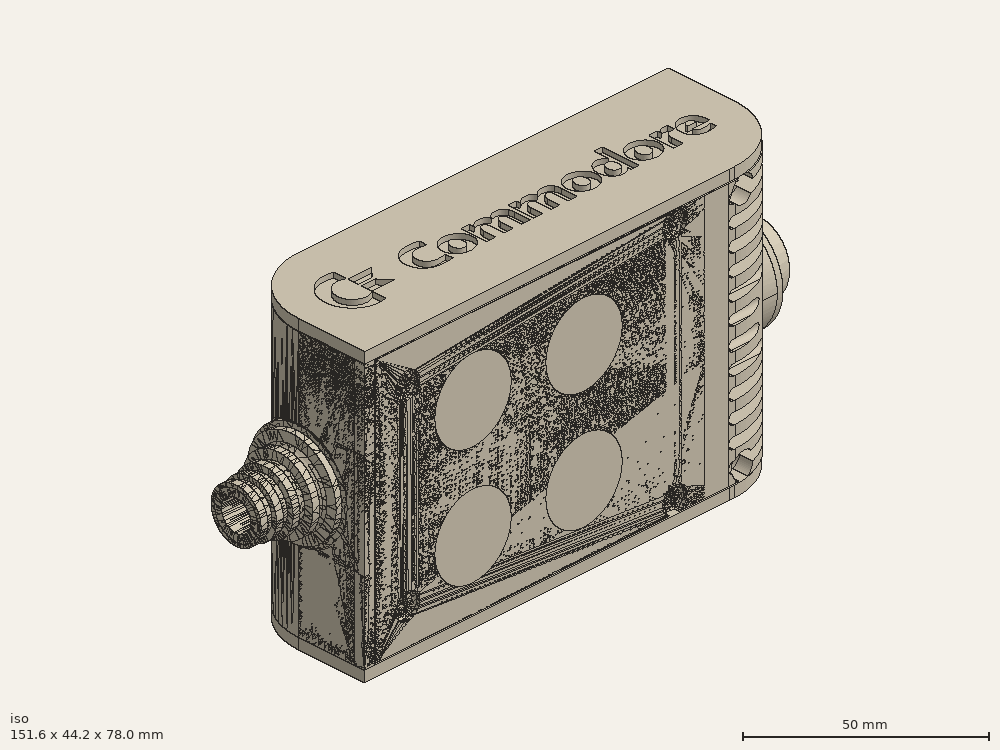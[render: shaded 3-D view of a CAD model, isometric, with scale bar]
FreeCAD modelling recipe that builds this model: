
FCSTD DOCUMENT  (FreeCAD 0.19R0.19.2)
Label: enclosure_222FCStd
License: All rights reserved
LicenseURL: http://en.wikipedia.org/wiki/All_rights_reserved
objects: Part::Revolution×152, Part::MultiFuse×146, Part::Feature×146, Sketcher::SketchObject×89, Part::Extrusion×74, Part::Cut×72, Part::Cylinder×70, Part::Fillet×58, Part::Box×38, App::MeasureDistance×4, Part::Chamfer×4, Part::FeaturePython×2, Image::ImagePlane×1, PartDesign::Body×1, Part::Mirroring×1
note: 853 computed .brp shape members not serialized (recipe doc carries the construction recipe); baked Part::Feature solids carry a one-line shape summary decoded from their .brp

FEATURE [Sketcher::SketchObject] Sketch  label="topSketch"
  FullyConstrained = true
  sketch-geometry (20):
    g0: LineSegment StartX=5.21097e-06 StartY=3 StartZ=0 EndX=5.21097e-06 EndY=19 EndZ=0
    g1: ArcOfCircle CenterX=19 CenterY=19 CenterZ=0 NormalX=0 NormalY=0 NormalZ=1 AngleXU=0 Radius=19 StartAngle=1.5708 EndAngle=3.14159
    g2: ArcOfCircle CenterX=19 CenterY=19 CenterZ=0 NormalX=0 NormalY=0 NormalZ=1 AngleXU=0 Radius=16 StartAngle=1.5708 EndAngle=3.14159
    g3: LineSegment StartX=114 StartY=35 StartZ=0 EndX=19 EndY=35 EndZ=0
    g4: LineSegment StartX=5.21097e-06 StartY=3 StartZ=0 EndX=5.21097e-06 EndY=0 EndZ=0
    g5: LineSegment StartX=3 StartY=0 StartZ=0 EndX=5.21097e-06 EndY=0 EndZ=0
    g6: LineSegment StartX=3 StartY=19 StartZ=0 EndX=3 EndY=0 EndZ=0
    g7: LineSegment StartX=19 StartY=38 StartZ=0 EndX=124 EndY=38 EndZ=0
    g8: Circle CenterX=119 CenterY=35 CenterZ=0 NormalX=0 NormalY=0 NormalZ=1 AngleXU=0 Radius=1
    g9: Circle CenterX=121 CenterY=35 CenterZ=0 NormalX=0 NormalY=0 NormalZ=1 AngleXU=0 Radius=1
    g10: Circle CenterX=121 CenterY=33 CenterZ=0 NormalX=0 NormalY=0 NormalZ=1 AngleXU=0 Radius=1
    g11: BSplineCurve PolesCount=3 KnotsCount=2 Degree=2 IsPeriodic=0
    g12: GeomPoint X=119 Y=35 Z=0
    g13: GeomPoint X=121 Y=33 Z=0
    g14: LineSegment StartX=119 StartY=35 StartZ=0 EndX=114 EndY=35 EndZ=0
    g15: ArcOfCircle CenterX=105 CenterY=19 CenterZ=0 NormalX=0 NormalY=0 NormalZ=1 AngleXU=0 Radius=19 StartAngle=5.7297 EndAngle=6.28319
    g16: ArcOfCircle CenterX=105 CenterY=19 CenterZ=0 NormalX=0 NormalY=0 NormalZ=1 AngleXU=0 Radius=16 StartAngle=5.60905 EndAngle=6.28319
    g17: LineSegment StartX=121 StartY=33 StartZ=0 EndX=121 EndY=19 EndZ=0
    g18: LineSegment StartX=124 StartY=38 StartZ=0 EndX=124 EndY=19 EndZ=0
    g19: LineSegment StartX=117.5 StartY=9.01251 StartZ=0 EndX=121.163 EndY=9.0125 EndZ=0
  constraints (46):
    c: Vertical(g0)
    c: Block(g0)
    c: Coincident(g1,g0)
    c: Block(g1)
    c: Coincident(g2,g1)
    c: Block(g2)
    c: Coincident(g3,g2)
    c: Horizontal(g3)
    c: Tangent(g3,g2)
    c: Coincident(g4,g0)
    c: Distance(g4) = 3
    c: Vertical(g4)
    c: Coincident(g5,g4)
    c: Horizontal(g5)
    c: Coincident(g6,g2)
    c: Coincident(g6,g5)
    c: Vertical(g6)
    c: Horizontal(g7)
    c: Distance(g7) = 105
    c: Coincident(g7,g1)
    c: Block(g3)
    c: Weight(g8) = 1
    c: Equal(g8,g9)
    c: Equal(g8,g10)
    c: InternalAlignment(g8,g11)
    c: InternalAlignment(g9,g11)
    c: InternalAlignment(g10,g11)
    c: InternalAlignment(g12,g11)
    c: InternalAlignment(g13,g11)
    c: Block(g11)
    c: Coincident(g14,g11)
    c: Coincident(g14,g3)
    c: Horizontal(g14)
    c: Block(g15)
    c: Coincident(g16,g15)
    c: Block(g16)
    c: Coincident(g17,g11)
    c: Coincident(g17,g16)
    c: Vertical(g17)
    c: Distance(g17) = 14
    c: Coincident(g18,g7)
    c: Coincident(g18,g15)
    c: Vertical(g18)
    c: Distance(g18) = 19
    c: Coincident(g19,g16)
    c: Coincident(g19,g15)
FEATURE [Sketcher::SketchObject] Sketch001  label="bottomSketch"
  FullyConstrained = true
  sketch-geometry (32):
    g0: LineSegment StartX=3.3 StartY=-6.03275e-07 StartZ=0 EndX=98 EndY=-6.03275e-07 EndZ=0
    g1: ArcOfCircle CenterX=98 CenterY=19 CenterZ=0 NormalX=0 NormalY=0 NormalZ=1 AngleXU=0 Radius=19 StartAngle=4.71239 EndAngle=5.71103
    g2: LineSegment StartX=6.3 StartY=8 StartZ=0 EndX=3.3 EndY=8 EndZ=0
    g3: LineSegment StartX=3.3 StartY=8 StartZ=0 EndX=3.3 EndY=-6.03275e-07 EndZ=0
    g4: ArcOfCircle CenterX=8.3 CenterY=5 CenterZ=0 NormalX=0 NormalY=0 NormalZ=1 AngleXU=0 Radius=2 StartAngle=3.14159 EndAngle=4.71239
    g5: LineSegment StartX=6.3 StartY=8 StartZ=0 EndX=6.3 EndY=5 EndZ=0
    g6: ArcOfCircle CenterX=98 CenterY=19 CenterZ=0 NormalX=0 NormalY=0 NormalZ=1 AngleXU=0 Radius=12.7 StartAngle=4.71239 EndAngle=6.28319
    g7: LineSegment StartX=94.7 StartY=3 StartZ=0 EndX=8.3 EndY=3 EndZ=0
    g8-g12: Circle x5 (B-spline internal-alignment scaffolding for g13; pole/knot coordinates omitted)
    g13: BSplineCurve PolesCount=5 KnotsCount=3 Degree=3 IsPeriodic=0
    g14: GeomPoint X=98 Y=6.3 Z=0
    g15: GeomPoint X=96.3938 Y=4.71946 Z=0
    g16: GeomPoint X=94.7 Y=3 Z=0
    g17-g23: Circle x7 (B-spline internal-alignment scaffolding for g24; pole/knot coordinates omitted)
    g24: BSplineCurve PolesCount=7 KnotsCount=5 Degree=3 IsPeriodic=0
    g25-g29: GeomPoint x5 (B-spline internal-alignment scaffolding for g24; pole/knot coordinates omitted)
    g30: ArcOfCircle CenterX=98 CenterY=19 CenterZ=0 NormalX=0 NormalY=0 NormalZ=1 AngleXU=0 Radius=15.7 StartAngle=5.81226 EndAngle=6.28319
    g31: LineSegment StartX=110.7 StartY=19 StartZ=0 EndX=113.7 EndY=19 EndZ=0
  constraints (41):
    c: Horizontal(g0)
    c: Coincident(g1,g0)
    c: Block(g1)
    c: Horizontal(g2)
    c: Distance(g2) = 3
    c: Coincident(g3,g2)
    c: Vertical(g3)
    c: Coincident(g3,g0)
    c: Block(g4)
    c: Block(g2)
    c: Coincident(g5,g2)
    c: Coincident(g5,g4)
    c: Vertical(g5)
    c: Coincident(g6,g1)
    c: Block(g6)
    c: Coincident(g7,g4)
    c: Horizontal(g7)
    c: Block(g0)
    c: Block(g7)
    c: Block(g3)
    c: Coincident(g13,g6)
    c: Weight(g8) = 1
    c: Equal(g8, g9-g12) x4
    c: Coincident(g13,g7)
    c: InternalAlignment(g8-g12 -> g13) x5
    c: InternalAlignment(g14,g13)
    c: InternalAlignment(g15,g13)
    c: InternalAlignment(g16,g13)
    c: Block(g13)
    c: Weight(g17) = 1
    c: Equal(g17, g18-g23) x6
    c: Coincident(g24,g1)
    c: InternalAlignment(g17-g23 -> g24) x7
    c: InternalAlignment(g25-g29 -> g24) x5
    c: Block(g24)
    c: Coincident(g30,g24)
    c: Coincident(g31,g6)
    c: Coincident(g31,g30)
    c: Horizontal(g31)
    c: Block(g31)
    c: Block(g30)
FEATURE [Part::Extrusion] Extrude  label="top"
  Base = -> Sketch
  Dir = (0,0,1)
  DirMode = 2
  FaceMakerClass = Part::FaceMakerBullseye
  LengthFwd = 72
  LengthRev = 0
  Solid = true
  Symmetric = false
FEATURE [Part::Extrusion] Extrude001  label="bottom"
  Base = -> Sketch001
  Dir = (0,0,1)
  DirMode = 2
  FaceMakerClass = Part::FaceMakerBullseye
  LengthFwd = 71.4
  LengthRev = 0
  Placement = pos=(0,0,0.3) rot=(0,0,1;0rad)
  Solid = true
  Symmetric = false
FEATURE [Sketcher::SketchObject] Sketch002  label="topSketch001"
  FullyConstrained = true
  sketch-geometry (8):
    g0: ArcOfCircle CenterX=19 CenterY=19.0975 CenterZ=0 NormalX=0 NormalY=0 NormalZ=1 AngleXU=0 Radius=18.9025 StartAngle=1.5708 EndAngle=3.14674
    g1: LineSegment StartX=0.0977805 StartY=19.0003 StartZ=0 EndX=0.0977805 EndY=0.000251602 EndZ=0
    g2: LineSegment StartX=19 StartY=38 StartZ=0 EndX=124 EndY=38 EndZ=0
    g3: LineSegment StartX=0.0977805 StartY=0.000251602 StartZ=0 EndX=105.098 EndY=0.000251602 EndZ=0
    g4: LineSegment StartX=124 StartY=38 StartZ=0 EndX=125.616 EndY=38 EndZ=0
    g5: LineSegment StartX=105.098 StartY=0.000251602 StartZ=0 EndX=106.713 EndY=0.000251602 EndZ=0
    g6: ArcOfCircle CenterX=106.616 CenterY=19 CenterZ=0 NormalX=0 NormalY=0 NormalZ=1 AngleXU=0 Radius=19 StartAngle=4.71754 EndAngle=6.28319
    g7: LineSegment StartX=125.616 StartY=38 StartZ=0 EndX=125.616 EndY=19 EndZ=0
  constraints (21):
    c: Block(g0)
    c: Coincident(g1,g0)
    c: Vertical(g1)
    c: Horizontal(g2)
    c: Distance(g2) = 105
    c: Coincident(g2,g0)
    c: Distance(g1) = 19
    c: Coincident(g3,g1)
    c: Horizontal(g3)
    c: Distance(g3) = 105
    c: Coincident(g4,g2)
    c: Horizontal(g4)
    c: Distance(g4) = 1.61553
    c: Horizontal(g5)
    c: Equal(g4,g5) = 1.61553
    c: Coincident(g5,g3)
    c: Block(g6)
    c: Coincident(g6,g5)
    c: Coincident(g7,g4)
    c: Coincident(g7,g6)
    c: Vertical(g7)
FEATURE [Part::Extrusion] Extrude002  label="sideA"
  Base = -> Sketch002
  Dir = (0,0,1)
  DirMode = 2
  FaceMakerClass = Part::FaceMakerBullseye
  LengthFwd = 3
  LengthRev = 0
  Placement = pos=(0,0,-3) rot=(0,0,1;0rad)
  Solid = true
  Symmetric = false
FEATURE [Sketcher::SketchObject] Sketch003  label="topSketch002"
  FullyConstrained = true
  sketch-geometry (6):
    g0: LineSegment StartX=19 StartY=38 StartZ=0 EndX=117 EndY=38 EndZ=0
    g1: ArcOfCircle CenterX=19 CenterY=19 CenterZ=0 NormalX=0 NormalY=0 NormalZ=1 AngleXU=0 Radius=19 StartAngle=1.5708 EndAngle=3.14159
    g2: LineSegment StartX=117 StartY=38 StartZ=0 EndX=117 EndY=19 EndZ=0
    g3: LineSegment StartX=98 StartY=1.0161e-12 StartZ=0 EndX=5.22862e-06 EndY=1.0161e-12 EndZ=0
    g4: LineSegment StartX=5.22862e-06 StartY=19 StartZ=0 EndX=5.22862e-06 EndY=1.0161e-12 EndZ=0
    g5: ArcOfCircle CenterX=98 CenterY=19 CenterZ=0 NormalX=0 NormalY=0 NormalZ=1 AngleXU=0 Radius=19 StartAngle=4.71239 EndAngle=6.28319
  constraints (16):
    c: Horizontal(g0)
    c: Distance(g0) = 98
    c: Coincident(g1,g0)
    c: Block(g1)
    c: Coincident(g2,g0)
    c: Vertical(g2)
    c: Distance(g2) = 19
    c: Horizontal(g3)
    c: Coincident(g4,g1)
    c: Vertical(g4)
    c: Coincident(g3,g4)
    c: Block(g3)
    c: Coincident(g5,g2)
    c: Coincident(g5,g3)
    c: Block(g0)
    c: Block(g5)
FEATURE [Sketcher::SketchObject] Sketch004
  FullyConstrained = true
  MapMode = 3
  Placement = pos=(0,0,0) rot=(1,0,0;1.5708rad)
  Support = -> [Extrude]
  sketch-geometry (8):
    g0: Circle CenterX=80.351 CenterY=-67.6202 CenterZ=0 NormalX=0 NormalY=0 NormalZ=1 AngleXU=0 Radius=2
    g1: Circle CenterX=80.351 CenterY=-67.6202 CenterZ=0 NormalX=0 NormalY=0 NormalZ=1 AngleXU=0 Radius=3
    g2: Circle CenterX=80.351 CenterY=-4.92017 CenterZ=0 NormalX=0 NormalY=0 NormalZ=1 AngleXU=0 Radius=2
    g3: Circle CenterX=80.351 CenterY=-4.92017 CenterZ=0 NormalX=0 NormalY=0 NormalZ=1 AngleXU=0 Radius=3
    g4: Circle CenterX=23.851 CenterY=-4.92017 CenterZ=0 NormalX=0 NormalY=0 NormalZ=1 AngleXU=0 Radius=2
    g5: Circle CenterX=23.851 CenterY=-4.92017 CenterZ=0 NormalX=0 NormalY=0 NormalZ=1 AngleXU=0 Radius=3
    g6: Circle CenterX=23.851 CenterY=-67.6202 CenterZ=0 NormalX=0 NormalY=0 NormalZ=1 AngleXU=0 Radius=2
    g7: Circle CenterX=23.851 CenterY=-67.6202 CenterZ=0 NormalX=0 NormalY=0 NormalZ=1 AngleXU=0 Radius=3
  constraints (8):
    c: Block(g3)
    c: Block(g2)
    c: Block(g1)
    c: Block(g0)
    c: Block(g6)
    c: Block(g7)
    c: Block(g4)
    c: Block(g5)
FEATURE [Part::Extrusion] Extrude004
  Base = -> Sketch004
  Dir = (0,-1,2e-16)
  DirMode = 2
  FaceMakerClass = Part::FaceMakerBullseye
  LengthFwd = 6
  LengthRev = 0
  Placement = pos=(0,9,0) rot=(0,0,1;0rad)
  Solid = true
  Symmetric = false
FEATURE [Sketcher::SketchObject] Sketch005
  FullyConstrained = true
  MapMode = 3
  Placement = pos=(0,0,0) rot=(1,0,0;1.5708rad)
  Support = -> [Extrude]
  sketch-geometry (8):
    g0: Circle CenterX=80.351 CenterY=-67.6202 CenterZ=0 NormalX=0 NormalY=0 NormalZ=1 AngleXU=0 Radius=3
    g1: Circle CenterX=80.351 CenterY=-4.92017 CenterZ=0 NormalX=0 NormalY=0 NormalZ=1 AngleXU=0 Radius=3
    g2: Circle CenterX=23.851 CenterY=-4.92017 CenterZ=0 NormalX=0 NormalY=0 NormalZ=1 AngleXU=0 Radius=3
    g3: Circle CenterX=23.851 CenterY=-67.6202 CenterZ=0 NormalX=0 NormalY=0 NormalZ=1 AngleXU=0 Radius=3
    g4: Circle CenterX=23.851 CenterY=-67.6202 CenterZ=0 NormalX=0 NormalY=0 NormalZ=1 AngleXU=0 Radius=5
    g5: Circle CenterX=80.351 CenterY=-67.6202 CenterZ=0 NormalX=0 NormalY=0 NormalZ=1 AngleXU=0 Radius=5
    g6: Circle CenterX=23.851 CenterY=-4.92017 CenterZ=0 NormalX=0 NormalY=0 NormalZ=1 AngleXU=0 Radius=5
    g7: Circle CenterX=80.351 CenterY=-4.92017 CenterZ=0 NormalX=0 NormalY=0 NormalZ=1 AngleXU=0 Radius=5
  constraints (8):
    c: Block(g1)
    c: Block(g0)
    c: Block(g3)
    c: Block(g2)
    c: Block(g5)
    c: Block(g4)
    c: Block(g6)
    c: Block(g7)
FEATURE [Part::Extrusion] Extrude005
  Base = -> Sketch005
  Dir = (0,-1,2e-16)
  DirMode = 2
  FaceMakerClass = Part::FaceMakerBullseye
  LengthFwd = 2
  LengthRev = 0
  Solid = true
  Symmetric = false
FEATURE [Sketcher::SketchObject] Sketch006
  FullyConstrained = true
  MapMode = 3
  Placement = pos=(0,0,0) rot=(1,0,0;1.5708rad)
  sketch-geometry (8):
    g0: Circle CenterX=80.351 CenterY=-67.6202 CenterZ=0 NormalX=0 NormalY=0 NormalZ=1 AngleXU=0 Radius=3
    g1: Circle CenterX=80.351 CenterY=-4.92017 CenterZ=0 NormalX=0 NormalY=0 NormalZ=1 AngleXU=0 Radius=3
    g2: Circle CenterX=23.851 CenterY=-4.92017 CenterZ=0 NormalX=0 NormalY=0 NormalZ=1 AngleXU=0 Radius=3
    g3: Circle CenterX=23.851 CenterY=-67.6202 CenterZ=0 NormalX=0 NormalY=0 NormalZ=1 AngleXU=0 Radius=3
    g4: Circle CenterX=23.851 CenterY=-67.6202 CenterZ=0 NormalX=0 NormalY=0 NormalZ=1 AngleXU=0 Radius=5
    g5: Circle CenterX=80.351 CenterY=-67.6202 CenterZ=0 NormalX=0 NormalY=0 NormalZ=1 AngleXU=0 Radius=5
    g6: Circle CenterX=23.851 CenterY=-4.92017 CenterZ=0 NormalX=0 NormalY=0 NormalZ=1 AngleXU=0 Radius=5
    g7: Circle CenterX=80.351 CenterY=-4.92017 CenterZ=0 NormalX=0 NormalY=0 NormalZ=1 AngleXU=0 Radius=5
  constraints (8):
    c: Block(g1)
    c: Block(g0)
    c: Block(g3)
    c: Block(g2)
    c: Block(g5)
    c: Block(g4)
    c: Block(g6)
    c: Block(g7)
FEATURE [Part::Extrusion] Extrude007
  Base = -> Sketch006
  Dir = (0,-1,2e-16)
  DirMode = 2
  FaceMakerClass = Part::FaceMakerBullseye
  LengthFwd = 2
  LengthRev = 0
  Solid = true
  Symmetric = false
FEATURE [Part::Fillet] Fillet
  Base = -> Extrude007
  Edges = 4 edges r=1.99: [Edge6,Edge12,Edge18,Edge24]
FEATURE [Part::Cut] Cut
  Base = -> Extrude005
  Placement = pos=(0,5,0) rot=(0,0,1;0rad)
  Tool = -> Fillet
FEATURE [Part::MultiFuse] Fusion  label="pCBScrews"
  Placement = pos=(-2.5,0,72.3) rot=(0,0,1;0rad)
  Shapes = -> [Extrude004,Cut]
FEATURE [App::MeasureDistance] Distance  label="Distance: 0.69 mm"
  Distance = 0.685967
  P1 = (24.0138,2.9647,0.3)
  P2 = (23.8901,3,-0.373787)
FEATURE [App::MeasureDistance] Distance001  label="Distance: 0.53 mm"
  Distance = 0.533607
  P1 = (80.2939,3,72.2334)
  P2 = (80.281,2.99661,71.7)
FEATURE [Part::Fillet] Fillet001
  Base = -> Extrude001
  Edges = 1 edges r=2.4: [Edge17]
FEATURE [Part::Fillet] Fillet002  label="bottom001"
  Base = -> Fillet001
  Edges = 1 edges r=2.4: [Edge36]
FEATURE [Part::Fillet] Fillet003  label="top001"
  Base = -> Extrude
  Edges = 1 edges r=2: [Edge1]
FEATURE [Sketcher::SketchObject] Sketch007
  FullyConstrained = true
  sketch-geometry (16):
    g0: LineSegment StartX=4 StartY=0 StartZ=0 EndX=4 EndY=2.4 EndZ=0
    g1: LineSegment StartX=4 StartY=2.4 StartZ=0 EndX=7 EndY=2.4 EndZ=0
    g2: LineSegment StartX=4 StartY=0 StartZ=0 EndX=5.7 EndY=0 EndZ=0
    g3: LineSegment StartX=5.7 StartY=0 StartZ=0 EndX=5.7 EndY=-5.6 EndZ=0
    g4-g8: Circle x5 (B-spline internal-alignment scaffolding for g9; pole/knot coordinates omitted)
    g9: BSplineCurve PolesCount=5 KnotsCount=3 Degree=3 IsPeriodic=0
    g10: GeomPoint X=7 Y=2.4 Z=0
    g11: GeomPoint X=10.4582 Y=-1.55472 Z=0
    g12: GeomPoint X=14 Y=-5.6 Z=0
    g13: LineSegment StartX=14 StartY=-5.6 StartZ=0 EndX=14 EndY=-14.1 EndZ=0
    g14: LineSegment StartX=14 StartY=-14.1 StartZ=0 EndX=6.5 EndY=-14.1 EndZ=0
    g15: LineSegment StartX=5.7 StartY=-5.6 StartZ=0 EndX=6.5 EndY=-14.1 EndZ=0
  constraints (28):
    c: Distance(g0) = 2.4
    c: Vertical(g0)
    c: Block(g0)
    c: Coincident(g1,g0)
    c: Horizontal(g1)
    c: Distance(g1) = 3
    c: Coincident(g2,g0)
    c: Horizontal(g2)
    c: Distance(g2) = 1.7
    c: Coincident(g3,g2)
    c: Vertical(g3)
    c: Distance(g3) = 5.6
    c: Coincident(g9,g1)
    c: Weight(g4) = 1
    c: Equal(g4, g5-g8) x4
    c: InternalAlignment(g4-g8 -> g9) x5
    c: InternalAlignment(g10,g9)
    c: InternalAlignment(g11,g9)
    c: InternalAlignment(g12,g9)
    c: Block(g9)
    c: Coincident(g13,g9)
    c: Vertical(g13)
    c: Distance(g13) = 8.5
    c: Coincident(g14,g13)
    c: Horizontal(g14)
    c: Distance(g14) = 7.5
    c: Coincident(g15,g3)
    c: Coincident(g15,g14)
FEATURE [Part::Feature] Face
  shape: bbox 10 x 16.5 x 2e-07 mm, 1 faces, 0 solids (baked)
FEATURE [Part::Revolution] Revolve  label="plugHousing"
  Angle = 360
  Axis = (0,1,0)
  Base = (0,0,0)
  FaceMakerClass = Part::FaceMakerBullseye
  Placement = pos=(0,0,36.15) rot=(0,0,1;0rad)
  Solid = false
  Source = -> Face
  Symmetric = false
FEATURE [Part::Feature] Face001
  shape: bbox 10 x 16.5 x 2e-07 mm, 1 faces, 0 solids (baked)
FEATURE [Part::Revolution] Revolve001  label="plugHousing001"
  Angle = 360
  Axis = (0,1,0)
  Base = (0,0,0)
  FaceMakerClass = Part::FaceMakerBullseye
  Placement = pos=(0,0,36.15) rot=(0,0,1;0rad)
  Solid = false
  Source = -> Face001
  Symmetric = false
FEATURE [Part::MultiFuse] Fusion001  label="plugHousing002"
  Placement = pos=(0,0,0) rot=(0,0,1;1.5708rad)
  Shapes = -> [Revolve001,Revolve]
FEATURE [Part::Feature] Face002
  shape: bbox 10 x 16.5 x 2e-07 mm, 1 faces, 0 solids (baked)
FEATURE [Part::Revolution] Revolve003  label="plugHousing005"
  Angle = 360
  Axis = (0,1,0)
  Base = (0,0,0)
  FaceMakerClass = Part::FaceMakerBullseye
  Placement = pos=(0,0,36.15) rot=(0,0,1;0rad)
  Solid = false
  Source = -> Face002
  Symmetric = false
FEATURE [Part::Feature] Face003
  shape: bbox 10 x 16.5 x 2e-07 mm, 1 faces, 0 solids (baked)
FEATURE [Part::Revolution] Revolve002  label="plugHousing003"
  Angle = 360
  Axis = (0,1,0)
  Base = (0,0,0)
  FaceMakerClass = Part::FaceMakerBullseye
  Placement = pos=(0,0,36.15) rot=(0,0,1;0rad)
  Solid = false
  Source = -> Face003
  Symmetric = false
FEATURE [Part::MultiFuse] Fusion002  label="plugHousing004"
  Placement = pos=(0,0,0) rot=(0,0,1;1.5708rad)
  Shapes = -> [Revolve002,Revolve003]
FEATURE [Part::MultiFuse] Fusion003  label="plugHousing006"
  Placement = pos=(0,19,0) rot=(0,0,1;3.14159rad)
  Shapes = -> [Fusion002,Fusion001]
FEATURE [Part::Feature] Face004
  shape: bbox 10 x 16.5 x 2e-07 mm, 1 faces, 0 solids (baked)
FEATURE [Part::Revolution] Revolve006  label="plugHousing010"
  Angle = 360
  Axis = (0,1,0)
  Base = (0,0,0)
  FaceMakerClass = Part::FaceMakerBullseye
  Placement = pos=(0,0,36.15) rot=(0,0,1;0rad)
  Solid = false
  Source = -> Face004
  Symmetric = false
FEATURE [Part::Feature] Face005
  shape: bbox 10 x 16.5 x 2e-07 mm, 1 faces, 0 solids (baked)
FEATURE [Part::Revolution] Revolve007  label="plugHousing011"
  Angle = 360
  Axis = (0,1,0)
  Base = (0,0,0)
  FaceMakerClass = Part::FaceMakerBullseye
  Placement = pos=(0,0,36.15) rot=(0,0,1;0rad)
  Solid = false
  Source = -> Face005
  Symmetric = false
FEATURE [Part::Feature] Face006
  shape: bbox 10 x 16.5 x 2e-07 mm, 1 faces, 0 solids (baked)
FEATURE [Part::Revolution] Revolve004  label="plugHousing007"
  Angle = 360
  Axis = (0,1,0)
  Base = (0,0,0)
  FaceMakerClass = Part::FaceMakerBullseye
  Placement = pos=(0,0,36.15) rot=(0,0,1;0rad)
  Solid = false
  Source = -> Face006
  Symmetric = false
FEATURE [Part::MultiFuse] Fusion004  label="plugHousing009"
  Placement = pos=(0,0,0) rot=(0,0,1;1.5708rad)
  Shapes = -> [Revolve004,Revolve007]
FEATURE [Part::Feature] Face007
  shape: bbox 10 x 16.5 x 2e-07 mm, 1 faces, 0 solids (baked)
FEATURE [Part::Revolution] Revolve005  label="plugHousing008"
  Angle = 360
  Axis = (0,1,0)
  Base = (0,0,0)
  FaceMakerClass = Part::FaceMakerBullseye
  Placement = pos=(0,0,36.15) rot=(0,0,1;0rad)
  Solid = false
  Source = -> Face007
  Symmetric = false
FEATURE [Part::MultiFuse] Fusion005  label="plugHousing012"
  Placement = pos=(0,0,0) rot=(0,0,1;1.5708rad)
  Shapes = -> [Revolve006,Revolve005]
FEATURE [Part::MultiFuse] Fusion006  label="plugHousing013"
  Placement = pos=(0,19,0) rot=(0,0,1;3.14159rad)
  Shapes = -> [Fusion005,Fusion004]
FEATURE [Part::MultiFuse] Fusion007  label="plugHousing014"
  Placement = pos=(122.621,0,-0.15) rot=(0,0,1;0rad)
  Shapes = -> [Fusion003,Fusion006]
FEATURE [Part::Cylinder] Cylinder002
  Angle = 360
  AttacherType = Attacher::AttachEngine3D
  Height = 20
  Placement = pos=(0,0,36.15) rot=(0,0,1;0rad)
  Radius = 4
FEATURE [Part::Cylinder] Cylinder003
  Angle = 360
  AttacherType = Attacher::AttachEngine3D
  Height = 10
  Placement = pos=(0,0,36.15) rot=(0,0,1;0rad)
  Radius = 4
FEATURE [Part::MultiFuse] Fusion009  label="removeToCreateHoleForPlugHousing"
  Placement = pos=(70,19,36.15) rot=(0,1,0;1.5708rad)
  Shapes = -> [Cylinder002,Cylinder003]
FEATURE [Part::Cylinder] Cylinder004
  Angle = 360
  AttacherType = Attacher::AttachEngine3D
  Height = 20
  Placement = pos=(0,0,36.15) rot=(0,0,1;0rad)
  Radius = 4
FEATURE [Part::Cylinder] Cylinder005
  Angle = 360
  AttacherType = Attacher::AttachEngine3D
  Height = 10
  Placement = pos=(0,0,36.15) rot=(0,0,1;0rad)
  Radius = 4
FEATURE [Part::MultiFuse] Fusion010  label="removeToCreateHoleForPlugHousing001"
  Placement = pos=(70,19,36.15) rot=(0,1,0;1.5708rad)
  Shapes = -> [Cylinder004,Cylinder005]
FEATURE [Part::Cut] Cut001
  Base = -> Fillet003
  Tool = -> Fusion010
FEATURE [Part::Cut] Cut002  label="Bottom"
  Base = -> Fillet002
  Tool = -> Fusion009
FEATURE [Part::Feature] Face008
  shape: bbox 10 x 16.5 x 2e-07 mm, 1 faces, 0 solids (baked)
FEATURE [Part::Revolution] Revolve011  label="plugHousing021"
  Angle = 360
  Axis = (0,1,0)
  Base = (0,0,0)
  FaceMakerClass = Part::FaceMakerBullseye
  Placement = pos=(0,0,36.15) rot=(0,0,1;0rad)
  Solid = false
  Source = -> Face008
  Symmetric = false
FEATURE [Part::Feature] Face009
  shape: bbox 10 x 16.5 x 2e-07 mm, 1 faces, 0 solids (baked)
FEATURE [Part::Revolution] Revolve012  label="plugHousing022"
  Angle = 360
  Axis = (0,1,0)
  Base = (0,0,0)
  FaceMakerClass = Part::FaceMakerBullseye
  Placement = pos=(0,0,36.15) rot=(0,0,1;0rad)
  Solid = false
  Source = -> Face009
  Symmetric = false
FEATURE [Part::Feature] Face010 .. Face013  x4 (patterned run collapsed; names and placements below)
  shape: bbox 10 x 16.5 x 2e-07 mm, 1 faces, 0 solids (baked)
FEATURE [Part::Revolution] Revolve015  label="plugHousing027"
  Angle = 360
  Axis = (0,1,0)
  Base = (0,0,0)
  FaceMakerClass = Part::FaceMakerBullseye
  Placement = pos=(0,0,36.15) rot=(0,0,1;0rad)
  Solid = false
  Source = -> Face013
  Symmetric = false
FEATURE [Part::Feature] Face014
  shape: bbox 10 x 16.5 x 2e-07 mm, 1 faces, 0 solids (baked)
FEATURE [Part::Feature] Face015
  shape: bbox 10 x 16.5 x 2e-07 mm, 1 faces, 0 solids (baked)
FEATURE [Part::Feature] Face016
  shape: bbox 10 x 16.5 x 2e-07 mm, 1 faces, 0 solids (baked)
FEATURE [Part::Revolution] Revolve019  label="plugHousing033"
  Angle = 360
  Axis = (0,1,0)
  Base = (0,0,0)
  FaceMakerClass = Part::FaceMakerBullseye
  Placement = pos=(0,0,36.15) rot=(0,0,1;0rad)
  Solid = false
  Source = -> Face016
  Symmetric = false
FEATURE [Part::Feature] Face017
  shape: bbox 10 x 16.5 x 2e-07 mm, 1 faces, 0 solids (baked)
FEATURE [Part::Revolution] Revolve020  label="plugHousing034"
  Angle = 360
  Axis = (0,1,0)
  Base = (0,0,0)
  FaceMakerClass = Part::FaceMakerBullseye
  Placement = pos=(0,0,36.15) rot=(0,0,1;0rad)
  Solid = false
  Source = -> Face017
  Symmetric = false
FEATURE [Part::Feature] Face018
  shape: bbox 10 x 16.5 x 2e-07 mm, 1 faces, 0 solids (baked)
FEATURE [Part::Revolution] Revolve016  label="plugHousing030"
  Angle = 360
  Axis = (0,1,0)
  Base = (0,0,0)
  FaceMakerClass = Part::FaceMakerBullseye
  Placement = pos=(0,0,36.15) rot=(0,0,1;0rad)
  Solid = false
  Source = -> Face018
  Symmetric = false
FEATURE [Part::MultiFuse] Fusion020  label="plugHousing038"
  Placement = pos=(0,0,0) rot=(0,0,1;1.5708rad)
  Shapes = -> [Revolve016,Revolve020]
FEATURE [Part::Feature] Face019
  shape: bbox 10 x 16.5 x 2e-07 mm, 1 faces, 0 solids (baked)
FEATURE [Part::Feature] Face020
  shape: bbox 10 x 16.5 x 2e-07 mm, 1 faces, 0 solids (baked)
FEATURE [Part::Revolution] Revolve017  label="plugHousing031"
  Angle = 360
  Axis = (0,1,0)
  Base = (0,0,0)
  FaceMakerClass = Part::FaceMakerBullseye
  Placement = pos=(0,0,36.15) rot=(0,0,1;0rad)
  Solid = false
  Source = -> Face020
  Symmetric = false
FEATURE [Part::MultiFuse] Fusion021  label="plugHousing039"
  Placement = pos=(0,0,0) rot=(0,0,1;1.5708rad)
  Shapes = -> [Revolve019,Revolve017]
FEATURE [Part::MultiFuse] Fusion023  label="plugHousing041"
  Placement = pos=(0,19,0) rot=(0,0,1;3.14159rad)
  Shapes = -> [Fusion021,Fusion020]
FEATURE [Part::Revolution] Revolve022  label="plugHousing043"
  Angle = 360
  Axis = (0,1,0)
  Base = (0,0,0)
  FaceMakerClass = Part::FaceMakerBullseye
  Placement = pos=(0,0,36.15) rot=(0,0,1;0rad)
  Solid = false
  Source = -> Face019
  Symmetric = false
FEATURE [Part::Feature] Face021
  shape: bbox 10 x 16.5 x 2e-07 mm, 1 faces, 0 solids (baked)
FEATURE [Part::Revolution] Revolve023  label="plugHousing044"
  Angle = 360
  Axis = (0,1,0)
  Base = (0,0,0)
  FaceMakerClass = Part::FaceMakerBullseye
  Placement = pos=(0,0,36.15) rot=(0,0,1;0rad)
  Solid = false
  Source = -> Face021
  Symmetric = false
FEATURE [Part::Feature] Face022
  shape: bbox 10 x 16.5 x 2e-07 mm, 1 faces, 0 solids (baked)
FEATURE [Part::Revolution] Revolve018  label="plugHousing032"
  Angle = 360
  Axis = (0,1,0)
  Base = (0,0,0)
  FaceMakerClass = Part::FaceMakerBullseye
  Placement = pos=(0,0,36.15) rot=(0,0,1;0rad)
  Solid = false
  Source = -> Face022
  Symmetric = false
FEATURE [Part::MultiFuse] Fusion022  label="plugHousing040"
  Placement = pos=(0,0,0) rot=(0,0,1;1.5708rad)
  Shapes = -> [Revolve018,Revolve023]
FEATURE [Part::Feature] Face023
  shape: bbox 10 x 16.5 x 2e-07 mm, 1 faces, 0 solids (baked)
FEATURE [Part::Revolution] Revolve021  label="plugHousing035"
  Angle = 360
  Axis = (0,1,0)
  Base = (0,0,0)
  FaceMakerClass = Part::FaceMakerBullseye
  Placement = pos=(0,0,36.15) rot=(0,0,1;0rad)
  Solid = false
  Source = -> Face023
  Symmetric = false
FEATURE [Part::MultiFuse] Fusion018  label="plugHousing036"
  Placement = pos=(0,0,0) rot=(0,0,1;1.5708rad)
  Shapes = -> [Revolve022,Revolve021]
FEATURE [Part::MultiFuse] Fusion019  label="plugHousing037"
  Placement = pos=(0,19,0) rot=(0,0,1;3.14159rad)
  Shapes = -> [Fusion018,Fusion022]
FEATURE [Part::MultiFuse] Fusion024  label="plugHousing042"
  Placement = pos=(122.621,0,-0.15) rot=(0,0,1;0rad)
  Shapes = -> [Fusion023,Fusion019]
FEATURE [Part::Cylinder] Cylinder006
  Angle = 360
  AttacherType = Attacher::AttachEngine3D
  Height = 20
  Placement = pos=(0,0,36.15) rot=(0,0,1;0rad)
  Radius = 14.3
FEATURE [Part::Cylinder] Cylinder007
  Angle = 360
  AttacherType = Attacher::AttachEngine3D
  Height = 10
  Placement = pos=(0,0,36.15) rot=(0,0,1;0rad)
  Radius = 4
FEATURE [Part::MultiFuse] Fusion026  label="removeToCreteHoleForPlugHousing"
  Placement = pos=(70,19,36) rot=(0,1,0;1.5708rad)
  Shapes = -> [Cylinder006,Cylinder007]
FEATURE [Part::Box] Box001  label="Cube001"
  AttacherType = Attacher::AttachEngine3D
  Height = 28
  Length = 3
  Placement = pos=(110.7,19,22) rot=(0,0,1;0rad)
  Width = 15.7
FEATURE [Part::Cut] Cut003  label="top002"
  Base = -> Cut001
  Tool = -> Fusion007
FEATURE [Part::Revolution] Revolve008  label="plugHousing015"
  Angle = 360
  Axis = (0,1,0)
  Base = (0,0,0)
  FaceMakerClass = Part::FaceMakerBullseye
  Placement = pos=(0,0,36.15) rot=(0,0,1;0rad)
  Solid = false
  Source = -> Face010
  Symmetric = false
FEATURE [Part::MultiFuse] Fusion013  label="plugHousing020"
  Placement = pos=(0,0,0) rot=(0,0,1;1.5708rad)
  Shapes = -> [Revolve008,Revolve012]
FEATURE [Part::Cut] Cut004  label="top003"
  Base = -> Cut003
  Placement = pos=(1,0,0) rot=(0,0,1;0rad)
  Tool = -> Fusion026
FEATURE [Part::Cylinder] Cylinder008
  Angle = 360
  AttacherType = Attacher::AttachEngine3D
  Height = 20
  Placement = pos=(0,0,36.15) rot=(0,0,1;0rad)
  Radius = 10.3
FEATURE [Part::Cylinder] Cylinder009
  Angle = 360
  AttacherType = Attacher::AttachEngine3D
  Height = 10
  Placement = pos=(0,0,36.15) rot=(0,0,1;0rad)
  Radius = 4
FEATURE [Part::MultiFuse] Fusion027  label="removeToCreteHoleForPlugHousing001"
  Placement = pos=(70,19,36) rot=(0,1,0;1.5708rad)
  Shapes = -> [Cylinder008,Cylinder009]
FEATURE [Part::Cut] Cut005  label="plugHousingTab"
  Base = -> Box001
  Tool = -> Fusion027
FEATURE [Part::MultiFuse] Fusion028  label="plugHousing045"
  Shapes = -> [Fusion024,Cut005]
FEATURE [Part::Box] Box002  label="Cube002"
  AttacherType = Attacher::AttachEngine3D
  Height = 28.8
  Length = 3
  Placement = pos=(107.3,28,21.6) rot=(0,0,1;0rad)
  Width = 7
FEATURE [Part::Box] Box003  label="Cube003"
  AttacherType = Attacher::AttachEngine3D
  Height = 3
  Length = 6.4
  Placement = pos=(107.3,28,18.6) rot=(0,0,1;0rad)
  Width = 7
FEATURE [Part::Box] Box004  label="Cube004"
  AttacherType = Attacher::AttachEngine3D
  Height = 3
  Length = 6.4
  Placement = pos=(107.3,28,50.4) rot=(0,0,1;0rad)
  Width = 7
FEATURE [Part::MultiFuse] Fusion029  label="plugHousingBracketHolder"
  Shapes = -> [Box004,Box002,Box003]
FEATURE [Part::Cylinder] Cylinder010
  Angle = 360
  AttacherType = Attacher::AttachEngine3D
  Height = 20
  Placement = pos=(0,0,36.15) rot=(0,0,1;0rad)
  Radius = 14.3
FEATURE [Part::Cylinder] Cylinder011
  Angle = 360
  AttacherType = Attacher::AttachEngine3D
  Height = 10
  Placement = pos=(0,0,36.15) rot=(0,0,1;0rad)
  Radius = 4
FEATURE [Part::MultiFuse] Fusion030  label="removeToCreteHoleForPlugHousing002"
  Placement = pos=(70,19,36) rot=(0,1,0;1.5708rad)
  Shapes = -> [Cylinder010,Cylinder011]
FEATURE [Part::Cut] Cut006  label="plugHousingBracketHolder001"
  Base = -> Fusion029
  Tool = -> Fusion030
FEATURE [Part::Cylinder] Cylinder012
  Angle = 360
  AttacherType = Attacher::AttachEngine3D
  Height = 20
  Placement = pos=(0,0,36.15) rot=(0,0,1;0rad)
  Radius = 7
FEATURE [Part::Cylinder] Cylinder013
  Angle = 360
  AttacherType = Attacher::AttachEngine3D
  Height = 10
  Placement = pos=(0,0,36.15) rot=(0,0,1;0rad)
  Radius = 4
FEATURE [Part::MultiFuse] Fusion032  label="removeToCreteHoleForPlugHousing003"
  Placement = pos=(70,19,36) rot=(0,1,0;1.5708rad)
  Shapes = -> [Cylinder012,Cylinder013]
FEATURE [Part::Cut] Cut007  label="bottom002"
  Base = -> Cut002
  Tool = -> Fusion032
FEATURE [Sketcher::SketchObject] Sketch008
  FullyConstrained = true
  sketch-geometry (54):
    g0: LineSegment StartX=-4.2 StartY=0 StartZ=0 EndX=-6.2 EndY=0 EndZ=0
    g1: LineSegment StartX=-14 StartY=-18 StartZ=0 EndX=-14 EndY=-26.5 EndZ=0
    g2: LineSegment StartX=-4.2 StartY=0 StartZ=0 EndX=-4.2 EndY=-13.4877 EndZ=0
    g3: Circle CenterX=-4.2 CenterY=-13.4877 CenterZ=0 NormalX=0 NormalY=0 NormalZ=1 AngleXU=0 Radius=1
    g4: Circle CenterX=-4.2 CenterY=-26.5 CenterZ=0 NormalX=0 NormalY=0 NormalZ=1 AngleXU=0 Radius=1
    g5: Circle CenterX=-8.2 CenterY=-26.5 CenterZ=0 NormalX=0 NormalY=0 NormalZ=1 AngleXU=0 Radius=1
    g6: BSplineCurve PolesCount=3 KnotsCount=2 Degree=2 IsPeriodic=0
    g7: GeomPoint X=-4.2 Y=-13.4877 Z=0
    g8: GeomPoint X=-8.2 Y=-26.5 Z=0
    g9: LineSegment StartX=-14 StartY=-26.5 StartZ=0 EndX=-8.2 EndY=-26.5 EndZ=0
    g10: LineSegment StartX=-10.15 StartY=-12 StartZ=0 EndX=-10.15 EndY=-14 EndZ=0
    g11: LineSegment StartX=-12.8401 StartY=-16 StartZ=0 EndX=-10.1571 EndY=-16 EndZ=0
    g12: LineSegment StartX=-10.15 StartY=-14 StartZ=0 EndX=-8.70761 EndY=-14 EndZ=0
    g13: LineSegment StartX=-12.8401 StartY=-16 StartZ=0 EndX=-12.8401 EndY=-17.6958 EndZ=0
    g14: LineSegment StartX=-10.15 StartY=-12 StartZ=0 EndX=-7.79258 EndY=-12 EndZ=0
    g15: Circle CenterX=-6.2215 CenterY=-2 CenterZ=0 NormalX=0 NormalY=0 NormalZ=1 AngleXU=0 Radius=1
    g16: Circle CenterX=-6.22762 CenterY=-2.58724 CenterZ=0 NormalX=0 NormalY=0 NormalZ=1 AngleXU=0 Radius=1
    g17: Circle CenterX=-6.32538 CenterY=-4 CenterZ=0 NormalX=0 NormalY=0 NormalZ=1 AngleXU=0 Radius=1
    g18: BSplineCurve PolesCount=3 KnotsCount=2 Degree=2 IsPeriodic=0
    g19: GeomPoint X=-6.2215 Y=-2 Z=0
    g20: GeomPoint X=-6.32538 Y=-4 Z=0
    g21: Circle CenterX=-6.48644 CenterY=-5.99526 CenterZ=0 NormalX=0 NormalY=0 NormalZ=1 AngleXU=0 Radius=1
    g22: Circle CenterX=-6.58486 CenterY=-6.99526 CenterZ=0 NormalX=0 NormalY=0 NormalZ=1 AngleXU=0 Radius=1
    g23: Circle CenterX=-6.77343 CenterY=-8 CenterZ=0 NormalX=0 NormalY=0 NormalZ=1 AngleXU=0 Radius=1
    g24: BSplineCurve PolesCount=3 KnotsCount=2 Degree=2 IsPeriodic=0
    g25: GeomPoint X=-6.48644 Y=-5.99526 Z=0
    g26: GeomPoint X=-6.77343 Y=-8 Z=0
    g27: Circle CenterX=-7.19003 CenterY=-10 CenterZ=0 NormalX=0 NormalY=0 NormalZ=1 AngleXU=0 Radius=1
    g28: Circle CenterX=-7.44407 CenterY=-11.0915 CenterZ=0 NormalX=0 NormalY=0 NormalZ=1 AngleXU=0 Radius=1
    g29: Circle CenterX=-7.79258 CenterY=-12 CenterZ=0 NormalX=0 NormalY=0 NormalZ=1 AngleXU=0 Radius=1
    g30: BSplineCurve PolesCount=3 KnotsCount=2 Degree=2 IsPeriodic=0
    g31: GeomPoint X=-7.19003 Y=-10 Z=0
    g32: GeomPoint X=-7.79258 Y=-12 Z=0
    g33: Circle CenterX=-8.70761 CenterY=-14 CenterZ=0 NormalX=0 NormalY=0 NormalZ=1 AngleXU=0 Radius=1
    g34: Circle CenterX=-9.33087 CenterY=-15.1837 CenterZ=0 NormalX=0 NormalY=0 NormalZ=1 AngleXU=0 Radius=1
    g35: Circle CenterX=-10.1571 CenterY=-16 CenterZ=0 NormalX=0 NormalY=0 NormalZ=1 AngleXU=0 Radius=1
    g36: BSplineCurve PolesCount=3 KnotsCount=2 Degree=2 IsPeriodic=0
    g37: GeomPoint X=-8.70761 Y=-14 Z=0
    g38: GeomPoint X=-10.1571 Y=-16 Z=0
    g39: Circle CenterX=-12.8401 CenterY=-17.6958 CenterZ=0 NormalX=0 NormalY=0 NormalZ=1 AngleXU=0 Radius=1
    g40: Circle CenterX=-13.3521 CenterY=-17.9027 CenterZ=0 NormalX=0 NormalY=0 NormalZ=1 AngleXU=0 Radius=1
    g41: Circle CenterX=-14 CenterY=-18 CenterZ=0 NormalX=0 NormalY=0 NormalZ=1 AngleXU=0 Radius=1
    g42: BSplineCurve PolesCount=3 KnotsCount=2 Degree=2 IsPeriodic=0
    g43: GeomPoint X=-12.8401 Y=-17.6958 Z=0
    g44: GeomPoint X=-14 Y=-18 Z=0
    g45: LineSegment StartX=-6.2 StartY=0 StartZ=0 EndX=-7.2 EndY=0 EndZ=0
    g46: LineSegment StartX=-7.2 StartY=0 StartZ=0 EndX=-7.2 EndY=-2 EndZ=0
    g47: LineSegment StartX=-7.2 StartY=-2 StartZ=0 EndX=-6.2215 EndY=-2 EndZ=0
    g48: LineSegment StartX=-6.32538 StartY=-4 StartZ=0 EndX=-7.65538 EndY=-4 EndZ=0
    g49: LineSegment StartX=-7.65538 StartY=-4 StartZ=0 EndX=-7.65538 EndY=-5.99526 EndZ=0
    g50: LineSegment StartX=-7.65538 StartY=-5.99526 StartZ=0 EndX=-6.48644 EndY=-5.99526 EndZ=0
    g51: LineSegment StartX=-6.77343 StartY=-8 StartZ=0 EndX=-8.43343 EndY=-8 EndZ=0
    g52: LineSegment StartX=-8.43343 StartY=-8 StartZ=0 EndX=-8.43343 EndY=-10 EndZ=0
    g53: LineSegment StartX=-8.43343 StartY=-10 StartZ=0 EndX=-7.19003 EndY=-10 EndZ=0
  constraints (112):
    c: Horizontal(g0)
    c: Distance(g0) = 2
    c: Block(g0)
    c: Vertical(g1)
    c: Coincident(g2,g0)
    c: Vertical(g2)
    c: Block(g2)
    c: Coincident(g6,g2)
    c: Weight(g3) = 1
    c: Equal(g3,g4)
    c: Equal(g3,g5)
    c: InternalAlignment(g3,g6)
    c: InternalAlignment(g4,g6)
    c: InternalAlignment(g5,g6)
    c: InternalAlignment(g7,g6)
    c: InternalAlignment(g8,g6)
    c: Block(g6)
    c: Coincident(g9,g1)
    c: Coincident(g9,g6)
    c: Horizontal(g9)
    c: Vertical(g10)
    c: Block(g10)
    c: Horizontal(g11)
    c: Block(g11)
    c: Coincident(g12,g10)
    c: Horizontal(g12)
    c: Block(g12)
    c: Coincident(g13,g11)
    c: Vertical(g13)
    c: Block(g13)
    c: Coincident(g14,g10)
    c: Horizontal(g14)
    c: Block(g14)
    c: Block(g9)
    c: Block(g1)
    c: Weight(g15) = 1
    c: Equal(g15,g16)
    c: Equal(g15,g17)
    c: InternalAlignment(g15,g18)
    c: InternalAlignment(g16,g18)
    c: InternalAlignment(g17,g18)
    c: InternalAlignment(g19,g18)
    c: InternalAlignment(g20,g18)
    c: Weight(g21) = 1
    c: Equal(g21,g22)
    c: Equal(g21,g23)
    c: InternalAlignment(g21,g24)
    c: InternalAlignment(g22,g24)
    c: InternalAlignment(g23,g24)
    c: InternalAlignment(g25,g24)
    c: InternalAlignment(g26,g24)
    c: Weight(g27) = 1
    c: Equal(g27,g28)
    c: Equal(g27,g29)
    c: Coincident(g30,g14)
    c: InternalAlignment(g27,g30)
    c: InternalAlignment(g28,g30)
    c: InternalAlignment(g29,g30)
    c: InternalAlignment(g31,g30)
    c: InternalAlignment(g32,g30)
    c: Coincident(g36,g12)
    c: Weight(g33) = 1
    c: Equal(g33,g34)
    c: Equal(g33,g35)
    c: Coincident(g36,g11)
    c: InternalAlignment(g33,g36)
    c: InternalAlignment(g34,g36)
    c: InternalAlignment(g35,g36)
    c: InternalAlignment(g37,g36)
    c: InternalAlignment(g38,g36)
    c: Coincident(g42,g13)
    c: Weight(g39) = 1
    c: Equal(g39,g40)
    c: Equal(g39,g41)
    c: Coincident(g42,g1)
    c: InternalAlignment(g39,g42)
    c: InternalAlignment(g40,g42)
    c: InternalAlignment(g41,g42)
    c: InternalAlignment(g43,g42)
    c: InternalAlignment(g44,g42)
    c: Block(g18)
    c: Block(g24)
    c: Block(g30)
    c: Block(g36)
    c: Block(g42)
    c: Horizontal(g45)
    c: Coincident(g45,g0)
    c: Vertical(g46)
    c: Coincident(g46,g45)
    c: Coincident(g47,g46)
    c: Coincident(g47,g18)
    c: Horizontal(g47)
    c: Block(g46)
    c: Coincident(g48,g18)
    c: Horizontal(g48)
    c: Distance(g48) = 1.33
    c: Vertical(g49)
    c: Coincident(g49,g48)
    c: Coincident(g50,g49)
    c: Coincident(g50,g24)
    c: Horizontal(g50)
    c: Tangent(g50,g22)
    c: Horizontal(g51)
    c: Coincident(g51,g24)
    c: Block(g51)
    c: Vertical(g52)
    c: Block(g52)
    c: Coincident(g52,g51)
    c: Coincident(g53,g52)
    c: Coincident(g53,g30)
    c: Horizontal(g53)
    c: Distance(g1) = 8.5
FEATURE [Part::Feature] Face024
  shape: bbox 9.8 x 26.5 x 2e-07 mm, 1 faces, 0 solids (baked)
FEATURE [Part::Revolution] Revolve024
  Angle = 360
  Axis = (0,1,0)
  Base = (0,0,0)
  FaceMakerClass = Part::FaceMakerBullseye
  Placement = pos=(0,0,0) rot=(0,0,1;1.5708rad)
  Solid = false
  Source = -> Face024
  Symmetric = false
FEATURE [Part::Feature] Face025
  shape: bbox 9.8 x 26.5 x 2e-07 mm, 1 faces, 0 solids (baked)
FEATURE [Part::Revolution] Revolve025
  Angle = 360
  Axis = (0,1,0)
  Base = (0,0,0)
  FaceMakerClass = Part::FaceMakerBullseye
  Placement = pos=(0,0,0) rot=(0,0,1;1.5708rad)
  Solid = false
  Source = -> Face025
  Symmetric = false
FEATURE [Part::MultiFuse] Fusion033
  Placement = pos=(-18,19,36) rot=(0,0,1;0rad)
  Shapes = -> [Revolve025,Revolve024]
FEATURE [Part::Cylinder] Cylinder014
  Angle = 360
  AttacherType = Attacher::AttachEngine3D
  Height = 20
  Placement = pos=(0,0,36.15) rot=(0,0,1;0rad)
  Radius = 14.3
FEATURE [Part::Cylinder] Cylinder015
  Angle = 360
  AttacherType = Attacher::AttachEngine3D
  Height = 10
  Placement = pos=(0,0,36.15) rot=(0,0,1;0rad)
  Radius = 4
FEATURE [Part::MultiFuse] Fusion034  label="removeToCreteHoleForPlugHousing004"
  Placement = pos=(-42,19,36) rot=(0,1,0;1.5708rad)
  Shapes = -> [Cylinder014,Cylinder015]
FEATURE [Part::Cut] Cut008  label="top004"
  Base = -> Cut004
  Placement = pos=(-1,0,0) rot=(0,0,1;0rad)
  Tool = -> Fusion034
FEATURE [Part::Box] Box005  label="Cube005"
  AttacherType = Attacher::AttachEngine3D
  Height = 28
  Length = 3
  Placement = pos=(110.7,19,22) rot=(0,0,1;0rad)
  Width = 15.7
FEATURE [Part::Cylinder] Cylinder016
  Angle = 360
  AttacherType = Attacher::AttachEngine3D
  Height = 10
  Placement = pos=(0,0,36.15) rot=(0,0,1;0rad)
  Radius = 4
FEATURE [Part::Cylinder] Cylinder017
  Angle = 360
  AttacherType = Attacher::AttachEngine3D
  Height = 20
  Placement = pos=(0,0,36.15) rot=(0,0,1;0rad)
  Radius = 10.3
FEATURE [Part::MultiFuse] Fusion035  label="removeToCreteHoleForPlugHousing005"
  Placement = pos=(70,19,36) rot=(0,1,0;1.5708rad)
  Shapes = -> [Cylinder017,Cylinder016]
FEATURE [Part::Cut] Cut009  label="plugHousingTab001"
  Base = -> Box005
  Placement = pos=(-107.4,-14,0) rot=(0,0,1;0rad)
  Tool = -> Fusion035
FEATURE [Part::Box] Box006  label="Cube006"
  AttacherType = Attacher::AttachEngine3D
  Height = 28
  Length = 3
  Placement = pos=(110.7,19,22) rot=(0,0,1;0rad)
  Width = 15.7
FEATURE [Part::Cylinder] Cylinder018
  Angle = 360
  AttacherType = Attacher::AttachEngine3D
  Height = 10
  Placement = pos=(0,0,36.15) rot=(0,0,1;0rad)
  Radius = 4
FEATURE [Part::Cylinder] Cylinder019
  Angle = 360
  AttacherType = Attacher::AttachEngine3D
  Height = 20
  Placement = pos=(0,0,36.15) rot=(0,0,1;0rad)
  Radius = 10.3
FEATURE [Part::MultiFuse] Fusion036  label="removeToCreteHoleForPlugHousing006"
  Placement = pos=(70,19,36) rot=(0,1,0;1.5708rad)
  Shapes = -> [Cylinder019,Cylinder018]
FEATURE [Part::Cut] Cut010  label="plugHousingTab002"
  Base = -> Box006
  Placement = pos=(-107.4,-14,0) rot=(0,0,1;0rad)
  Tool = -> Fusion036
FEATURE [Part::MultiFuse] Fusion037
  Placement = pos=(9.6,23,0) rot=(0,0,1;3.14159rad)
  Shapes = -> [Cut009,Cut010]
FEATURE [Part::Box] Box  label="Cube"
  AttacherType = Attacher::AttachEngine3D
  Height = 10
  Length = 3
  Placement = pos=(3.3,4,12) rot=(0,0,1;0rad)
  Width = 10
FEATURE [Part::Fillet] Fillet004
  Base = -> Fusion028
  Edges = 1 edges r=2: [Edge25]
FEATURE [Part::Fillet] Fillet005  label="plugHousing046"
  Base = -> Fillet004
  Edges = 1 edges r=2: [Edge8]
FEATURE [Part::Fillet] Fillet006
  Base = -> Box
  Edges = 1 edges r=2: [Edge11]
FEATURE [Part::Box] Box007  label="Cube007"
  AttacherType = Attacher::AttachEngine3D
  Height = 10
  Length = 3
  Placement = pos=(3.3,4,50) rot=(0,0,1;0rad)
  Width = 10
FEATURE [Part::Fillet] Fillet007
  Base = -> Box007
  Edges = 1 edges r=2: [Edge12]
FEATURE [Part::Box] Box008  label="Cube008"
  AttacherType = Attacher::AttachEngine3D
  Height = 28
  Length = 4
  Placement = pos=(5,0,22) rot=(0,0,1;0rad)
  Width = 10
FEATURE [Part::Fillet] Fillet008
  Base = -> Box008
  Edges = 1 edges r=1: [Edge7]
FEATURE [Part::Fillet] Fillet009
  Base = -> Fillet008
  Edges = 1 edges r=2: [Edge5]
FEATURE [Part::Fillet] Fillet010
  Base = -> Fillet009
  Edges = 1 edges r=2: [Edge2]
FEATURE [Sketcher::SketchObject] Sketch009  label="topSketch003"
  FullyConstrained = true
  sketch-geometry (4):
    g0: LineSegment StartX=16.8446 StartY=31.512 StartZ=0 EndX=16.3251 EndY=34.4666 EndZ=0
    g1: ArcOfCircle CenterX=19 CenterY=19.2524 CenterZ=0 NormalX=0 NormalY=0 NormalZ=1 AngleXU=0 Radius=15.4476 StartAngle=1.74483 EndAngle=2.72717
    g2: ArcOfCircle CenterX=19 CenterY=19.2524 CenterZ=0 NormalX=0 NormalY=0 NormalZ=1 AngleXU=0 Radius=12.4476 StartAngle=1.74483 EndAngle=2.73189
    g3: LineSegment StartX=4.86004 StartY=25.4725 StartZ=0 EndX=7.58253 EndY=24.2107 EndZ=0
  constraints (7):
    c: Block(g0)
    c: Coincident(g1,g0)
    c: Coincident(g2,g0)
    c: Coincident(g3,g1)
    c: Coincident(g3,g2)
    c: Block(g1)
    c: Block(g2)
FEATURE [Part::Extrusion] Extrude008
  Base = -> Sketch009
  Dir = (0,0,1)
  DirMode = 2
  FaceMakerClass = Part::FaceMakerBullseye
  LengthFwd = 10
  LengthRev = 0
  Placement = pos=(0,0,31) rot=(0,0,1;0rad)
  Solid = true
  Symmetric = false
FEATURE [Part::Cylinder] Cylinder020
  Angle = 360
  AttacherType = Attacher::AttachEngine3D
  Height = 20
  Placement = pos=(0,0,36.15) rot=(0,0,1;0rad)
  Radius = 8.2
FEATURE [Part::Cylinder] Cylinder021
  Angle = 360
  AttacherType = Attacher::AttachEngine3D
  Height = 10
  Placement = pos=(0,0,36.15) rot=(0,0,1;0rad)
  Radius = 4
FEATURE [Part::MultiFuse] Fusion038  label="removeToCreteHoleForPlugHousing007"
  Placement = pos=(-42,19,36) rot=(0,1,0;1.5708rad)
  Shapes = -> [Cylinder020,Cylinder021]
FEATURE [Part::Cut] Cut011
  Base = -> Extrude008
  Tool = -> Fusion038
FEATURE [Part::Fillet] Fillet011
  Base = -> Cut011
  Edges = 1 edges r=2: [Edge1]
FEATURE [Part::Fillet] Fillet012
  Base = -> Fillet011
  Edges = 1 edges r=2.5: [Edge1]
FEATURE [Part::Fillet] Fillet013
  Base = -> Fillet012
  Edges = 1 edges r=2.5: [Edge2]
FEATURE [Part::Box] Box010  label="Cube010"
  AttacherType = Attacher::AttachEngine3D
  Height = 16
  Length = 8
  Placement = pos=(12.7,31.52,28) rot=(0,0,1;0rad)
  Width = 4
FEATURE [Sketcher::SketchObject] Sketch010  label="topSketch004"
  FullyConstrained = true
  sketch-geometry (4):
    g0: LineSegment StartX=16.8446 StartY=31.512 StartZ=0 EndX=16.3251 EndY=34.4666 EndZ=0
    g1: ArcOfCircle CenterX=19 CenterY=19.2524 CenterZ=0 NormalX=0 NormalY=0 NormalZ=1 AngleXU=0 Radius=15.4476 StartAngle=1.74483 EndAngle=2.72717
    g2: ArcOfCircle CenterX=19 CenterY=19.2524 CenterZ=0 NormalX=0 NormalY=0 NormalZ=1 AngleXU=0 Radius=12.4476 StartAngle=1.74483 EndAngle=2.73189
    g3: LineSegment StartX=4.86004 StartY=25.4725 StartZ=0 EndX=7.58253 EndY=24.2107 EndZ=0
  constraints (7):
    c: Block(g0)
    c: Coincident(g1,g0)
    c: Coincident(g2,g0)
    c: Coincident(g3,g1)
    c: Coincident(g3,g2)
    c: Block(g1)
    c: Block(g2)
FEATURE [Part::Cylinder] Cylinder022
  Angle = 360
  AttacherType = Attacher::AttachEngine3D
  Height = 10
  Placement = pos=(0,0,36.15) rot=(0,0,1;0rad)
  Radius = 4
FEATURE [Sketcher::SketchObject] Sketch011  label="topSketch005"
  FullyConstrained = true
  sketch-geometry (4):
    g0: LineSegment StartX=16.8446 StartY=31.512 StartZ=0 EndX=16.3251 EndY=34.4666 EndZ=0
    g1: ArcOfCircle CenterX=19 CenterY=19.2524 CenterZ=0 NormalX=0 NormalY=0 NormalZ=1 AngleXU=0 Radius=15.4476 StartAngle=1.74483 EndAngle=2.72717
    g2: ArcOfCircle CenterX=19 CenterY=19.2524 CenterZ=0 NormalX=0 NormalY=0 NormalZ=1 AngleXU=0 Radius=12.4476 StartAngle=1.74483 EndAngle=2.73189
    g3: LineSegment StartX=4.86004 StartY=25.4725 StartZ=0 EndX=7.58253 EndY=24.2107 EndZ=0
  constraints (7):
    c: Block(g0)
    c: Coincident(g1,g0)
    c: Coincident(g2,g0)
    c: Coincident(g3,g1)
    c: Coincident(g3,g2)
    c: Block(g1)
    c: Block(g2)
FEATURE [Part::Extrusion] Extrude010
  Base = -> Sketch011
  Dir = (0,0,1)
  DirMode = 2
  FaceMakerClass = Part::FaceMakerBullseye
  LengthFwd = 10.6
  LengthRev = 0
  Placement = pos=(0,0,31) rot=(0,0,1;0rad)
  Solid = true
  Symmetric = false
FEATURE [Part::Cylinder] Cylinder023
  Angle = 360
  AttacherType = Attacher::AttachEngine3D
  Height = 20
  Placement = pos=(0,0,36.15) rot=(0,0,1;0rad)
  Radius = 8.2
FEATURE [Part::MultiFuse] Fusion039  label="removeToCreteHoleForPlugHousing008"
  Placement = pos=(-42,19,36) rot=(0,1,0;1.5708rad)
  Shapes = -> [Cylinder023,Cylinder022]
FEATURE [Part::Cut] Cut012
  Base = -> Extrude010
  Placement = pos=(0,0,-0.3) rot=(0,0,1;0rad)
  Tool = -> Fusion039
FEATURE [Part::Cut] Cut013
  Base = -> Box010
  Tool = -> Cut012
FEATURE [Part::Fillet] Fillet014
  Base = -> Cut013
  Edges = 1 edges r=0.7: [Edge13]
FEATURE [Part::Fillet] Fillet015
  Base = -> Fillet014
  Edges = 1 edges r=0.7: [Edge13]
FEATURE [Part::Fillet] Fillet016
  Base = -> Fillet015
  Edges = 1 edges r=0.7: [Edge16]
FEATURE [Part::Fillet] Fillet017
  Base = -> Fillet016
  Edges = 1 edges r=0.7: [Edge11]
FEATURE [Part::Fillet] Fillet018
  Base = -> Fillet017
  Edges = 1 edges r=0.7: [Edge10]
FEATURE [Part::Fillet] Fillet019
  Base = -> Fillet018
  Edges = 1 edges r=1.2: [Edge5]
FEATURE [Part::Fillet] Fillet020
  Base = -> Fillet019
  Edges = 1 edges r=1.2: [Edge12]
FEATURE [Part::Fillet] Fillet021
  Base = -> Fillet020
  Edges = 1 edges r=2: [Edge1]
  Placement = pos=(0.3,0,0) rot=(0,0,1;0rad)
FEATURE [Part::MultiFuse] Fusion040  label="top005"
  Shapes = -> [Cut008,Fillet021]
FEATURE [Part::MultiFuse] Fusion041  label="wireHolder"
  Shapes = -> [Fusion033,Fillet013]
FEATURE [Part::MultiFuse] Fusion042
  Shapes = -> [Fillet007,Fusion041]
FEATURE [Part::MultiFuse] Fusion043  label="wireHolder001"
  Shapes = -> [Fusion042,Fillet010]
FEATURE [Part::MultiFuse] Fusion044  label="wireHolder002"
  Shapes = -> [Fillet006,Fusion037,Fusion043]
FEATURE [Part::Feature] Face026
  shape: bbox 11 x 6 x 2e-07 mm, 1 faces, 0 solids (baked)
FEATURE [Part::Revolution] Revolve026
  Angle = 360
  Axis = (0,1,0)
  Base = (0,0,0)
  FaceMakerClass = Part::FaceMakerBullseye
  Placement = pos=(30.3,-1,19.7) rot=(0,0,1;0rad)
  Solid = false
  Source = -> Face026
  Symmetric = false
FEATURE [Sketcher::SketchObject] Sketch013  label="topSketch006"
  FullyConstrained = true
  sketch-geometry (13):
    g0: LineSegment StartX=117 StartY=19 StartZ=0 EndX=117 EndY=38 EndZ=0
    g1: ArcOfCircle CenterX=98 CenterY=19 CenterZ=0 NormalX=0 NormalY=0 NormalZ=1 AngleXU=0 Radius=19 StartAngle=5.7297 EndAngle=6.28319
    g2: LineSegment StartX=0 StartY=3 StartZ=0 EndX=0 EndY=19 EndZ=0
    g3: LineSegment StartX=19 StartY=38 StartZ=0 EndX=117 EndY=38 EndZ=0
    g4: ArcOfCircle CenterX=19 CenterY=19 CenterZ=0 NormalX=0 NormalY=0 NormalZ=1 AngleXU=0 Radius=19 StartAngle=1.5708 EndAngle=3.14159
    g5: ArcOfCircle CenterX=19 CenterY=19 CenterZ=0 NormalX=0 NormalY=0 NormalZ=1 AngleXU=0 Radius=16 StartAngle=1.5708 EndAngle=3.14159
    g6: ArcOfCircle CenterX=98 CenterY=19 CenterZ=0 NormalX=0 NormalY=0 NormalZ=1 AngleXU=0 Radius=16 StartAngle=5.60905 EndAngle=6.28319
    g7: LineSegment StartX=114 StartY=19 StartZ=0 EndX=114 EndY=35 EndZ=0
    g8: LineSegment StartX=110.5 StartY=9.01251 StartZ=0 EndX=114.163 EndY=9.01251 EndZ=0
    g9: LineSegment StartX=114 StartY=35 StartZ=0 EndX=19 EndY=35 EndZ=0
    g10: LineSegment StartX=0 StartY=3 StartZ=0 EndX=0 EndY=0 EndZ=0
    g11: LineSegment StartX=3 StartY=0 StartZ=0 EndX=0 EndY=0 EndZ=0
    g12: LineSegment StartX=3 StartY=19 StartZ=0 EndX=3 EndY=0 EndZ=0
  constraints (33):
    c: Vertical(g0)
    c: Distance(g0) = 19
    c: Block(g0)
    c: Coincident(g1,g0)
    c: Block(g1)
    c: Vertical(g2)
    c: Block(g2)
    c: Coincident(g3,g0)
    c: Horizontal(g3)
    c: Distance(g3) = 98
    c: Coincident(g4,g3)
    c: Coincident(g4,g2)
    c: Block(g4)
    c: Coincident(g5,g4)
    c: Coincident(g6,g1)
    c: Block(g6)
    c: Block(g5)
    c: Coincident(g7,g6)
    c: Vertical(g7)
    c: Coincident(g8,g6)
    c: Coincident(g8,g1)
    c: Coincident(g9,g7)
    c: Coincident(g9,g5)
    c: Horizontal(g9)
    c: Tangent(g9,g5)
    c: Coincident(g10,g2)
    c: Distance(g10) = 3
    c: Vertical(g10)
    c: Coincident(g11,g10)
    c: Horizontal(g11)
    c: Coincident(g12,g5)
    c: Coincident(g12,g11)
    c: Vertical(g12)
FEATURE [Part::Extrusion] Extrude011  label="top006"
  Base = -> Sketch013
  Dir = (0,0,1)
  DirMode = 2
  FaceMakerClass = Part::FaceMakerBullseye
  LengthFwd = 72
  LengthRev = 0
  Solid = true
  Symmetric = false
FEATURE [Sketcher::SketchObject] Sketch014
  FullyConstrained = true
  MapMode = 3
  Placement = pos=(0,0,0) rot=(1,0,0;1.5708rad)
  Support = -> [Extrude011]
  sketch-geometry (8):
    g0: Circle CenterX=80.351 CenterY=-67.6202 CenterZ=0 NormalX=0 NormalY=0 NormalZ=1 AngleXU=0 Radius=2
    g1: Circle CenterX=80.351 CenterY=-67.6202 CenterZ=0 NormalX=0 NormalY=0 NormalZ=1 AngleXU=0 Radius=3
    g2: Circle CenterX=80.351 CenterY=-4.92017 CenterZ=0 NormalX=0 NormalY=0 NormalZ=1 AngleXU=0 Radius=2
    g3: Circle CenterX=80.351 CenterY=-4.92017 CenterZ=0 NormalX=0 NormalY=0 NormalZ=1 AngleXU=0 Radius=3
    g4: Circle CenterX=23.851 CenterY=-4.92017 CenterZ=0 NormalX=0 NormalY=0 NormalZ=1 AngleXU=0 Radius=2
    g5: Circle CenterX=23.851 CenterY=-4.92017 CenterZ=0 NormalX=0 NormalY=0 NormalZ=1 AngleXU=0 Radius=3
    g6: Circle CenterX=23.851 CenterY=-67.6202 CenterZ=0 NormalX=0 NormalY=0 NormalZ=1 AngleXU=0 Radius=2
    g7: Circle CenterX=23.851 CenterY=-67.6202 CenterZ=0 NormalX=0 NormalY=0 NormalZ=1 AngleXU=0 Radius=3
  constraints (8):
    c: Block(g3)
    c: Block(g2)
    c: Block(g1)
    c: Block(g0)
    c: Block(g6)
    c: Block(g7)
    c: Block(g4)
    c: Block(g5)
FEATURE [Part::Feature] Face027
  shape: bbox 11 x 6 x 2e-07 mm, 1 faces, 0 solids (baked)
FEATURE [Part::Revolution] Revolve027
  Angle = 360
  Axis = (0,1,0)
  Base = (0,0,0)
  FaceMakerClass = Part::FaceMakerBullseye
  Placement = pos=(30.3,-1,51.7) rot=(0,0,1;0rad)
  Solid = false
  Source = -> Face027
  Symmetric = false
FEATURE [Part::Feature] Face028
  shape: bbox 11 x 6 x 2e-07 mm, 1 faces, 0 solids (baked)
FEATURE [Part::Revolution] Revolve028
  Angle = 360
  Axis = (0,1,0)
  Base = (0,0,0)
  FaceMakerClass = Part::FaceMakerBullseye
  Placement = pos=(62.3,-1,19.7) rot=(0,0,1;0rad)
  Solid = false
  Source = -> Face028
  Symmetric = false
FEATURE [Part::Feature] Face029
  shape: bbox 11 x 6 x 2e-07 mm, 1 faces, 0 solids (baked)
FEATURE [Part::Revolution] Revolve029
  Angle = 360
  Axis = (0,1,0)
  Base = (0,0,0)
  FaceMakerClass = Part::FaceMakerBullseye
  Placement = pos=(62.3,-1,51.7) rot=(0,0,1;0rad)
  Solid = false
  Source = -> Face029
  Symmetric = false
FEATURE [Part::Feature] Wire
  shape: bbox 11 x 5.2 x 2e-07 mm, 0 faces, 0 solids (baked)
FEATURE [Part::Revolution] Revolve030
  Angle = 360
  Axis = (0,1,0)
  Base = (0,0,0)
  FaceMakerClass = Part::FaceMakerBullseye
  Placement = pos=(30.3,38,19.7) rot=(0,0,1;0rad)
  Solid = true
  Source = -> Wire
  Symmetric = false
FEATURE [Part::Feature] Wire001
  shape: bbox 11 x 5.2 x 2e-07 mm, 0 faces, 0 solids (baked)
FEATURE [Part::Revolution] Revolve031
  Angle = 360
  Axis = (0,1,0)
  Base = (0,0,0)
  FaceMakerClass = Part::FaceMakerBullseye
  Placement = pos=(30.3,38,51.7) rot=(0,0,1;0rad)
  Solid = true
  Source = -> Wire001
  Symmetric = false
FEATURE [Part::Feature] Wire002
  shape: bbox 11 x 5.2 x 2e-07 mm, 0 faces, 0 solids (baked)
FEATURE [Part::Revolution] Revolve032
  Angle = 360
  Axis = (0,1,0)
  Base = (0,0,0)
  FaceMakerClass = Part::FaceMakerBullseye
  Placement = pos=(62.3,38,51.7) rot=(0,0,1;0rad)
  Solid = true
  Source = -> Wire002
  Symmetric = false
FEATURE [Part::Feature] Wire003
  shape: bbox 11 x 5.2 x 2e-07 mm, 0 faces, 0 solids (baked)
FEATURE [Part::Revolution] Revolve033
  Angle = 360
  Axis = (0,1,0)
  Base = (0,0,0)
  FaceMakerClass = Part::FaceMakerBullseye
  Placement = pos=(62.3,38,19.7) rot=(0,0,1;0rad)
  Solid = true
  Source = -> Wire003
  Symmetric = false
FEATURE [Part::MultiFuse] Fusion045  label="altRandScrewHousing"
  Shapes = -> [Revolve029,Revolve027,Revolve028,Revolve026]
FEATURE [Part::MultiFuse] Fusion046  label="fanScrewHousing"
  Shapes = -> [Revolve033,Revolve032,Revolve031,Revolve030]
FEATURE [Sketcher::SketchObject] Sketch015
  FullyConstrained = true
  sketch-geometry (17):
    g0: Circle CenterX=-3.5 CenterY=23.5 CenterZ=0 NormalX=0 NormalY=0 NormalZ=1 AngleXU=0 Radius=1
    g1: Circle CenterX=-1 CenterY=15.25 CenterZ=0 NormalX=0 NormalY=0 NormalZ=1 AngleXU=0 Radius=1
    g2: Circle CenterX=-3.5 CenterY=7 CenterZ=0 NormalX=0 NormalY=0 NormalZ=1 AngleXU=0 Radius=1
    g3: BSplineCurve PolesCount=3 KnotsCount=2 Degree=2 IsPeriodic=0
    g4: GeomPoint X=-3.5 Y=23.5 Z=0
    g5: GeomPoint X=-3.5 Y=7 Z=0
    g6: Circle CenterX=-4.8 CenterY=30.5 CenterZ=0 NormalX=0 NormalY=0 NormalZ=1 AngleXU=0 Radius=1
    g7: Circle CenterX=-3.5 CenterY=30.5 CenterZ=0 NormalX=0 NormalY=0 NormalZ=1 AngleXU=0 Radius=1
    g8: Circle CenterX=-3.5 CenterY=29.2 CenterZ=0 NormalX=0 NormalY=0 NormalZ=1 AngleXU=0 Radius=1
    g9: BSplineCurve PolesCount=3 KnotsCount=2 Degree=2 IsPeriodic=0
    g10: GeomPoint X=-4.8 Y=30.5 Z=0
    g11: GeomPoint X=-3.5 Y=29.2 Z=0
    g12: LineSegment StartX=-3.5 StartY=29.2 StartZ=0 EndX=-3.5 EndY=23.5 EndZ=0
    g13: LineSegment StartX=-4.8 StartY=30.5 StartZ=0 EndX=0 EndY=30.5 EndZ=0
    g14: LineSegment StartX=-3.5 StartY=0.3 StartZ=0 EndX=0 EndY=0.3 EndZ=0
    g15: LineSegment StartX=-3.5 StartY=0.3 StartZ=0 EndX=-3.5 EndY=7 EndZ=0
    g16: LineSegment StartX=0 StartY=0.3 StartZ=0 EndX=0 EndY=30.5 EndZ=0
  constraints (34):
    c: Weight(g0) = 1
    c: Equal(g0,g1)
    c: Equal(g0,g2)
    c: InternalAlignment(g0,g3)
    c: InternalAlignment(g1,g3)
    c: InternalAlignment(g2,g3)
    c: InternalAlignment(g4,g3)
    c: InternalAlignment(g5,g3)
    c: Block(g3)
    c: Weight(g6) = 1
    c: Equal(g6,g7)
    c: Equal(g6,g8)
    c: InternalAlignment(g6,g9)
    c: InternalAlignment(g7,g9)
    c: InternalAlignment(g8,g9)
    c: InternalAlignment(g10,g9)
    c: InternalAlignment(g11,g9)
    c: Block(g9)
    c: Coincident(g12,g9)
    c: Coincident(g12,g3)
    c: Vertical(g12)
    c: Coincident(g13,g9)
    c: Horizontal(g13)
    c: Distance(g13) = 4.8
    c: Horizontal(g14)
    c: Block(g14)
    c: Coincident(g15,g14)
    c: Coincident(g15,g3)
    c: Vertical(g15)
    c: Coincident(g16,g14)
    c: Coincident(g16,g13)
    c: Vertical(g16)
    c: Tangent(g16,g1)
    c: Distance(g14) = 3.5
FEATURE [Sketcher::SketchObject] Sketch016
  FullyConstrained = true
  sketch-geometry (16):
    g0: Circle CenterX=-3.5 CenterY=23.5 CenterZ=0 NormalX=0 NormalY=0 NormalZ=1 AngleXU=0 Radius=1
    g1: Circle CenterX=-1 CenterY=15.25 CenterZ=0 NormalX=0 NormalY=0 NormalZ=1 AngleXU=0 Radius=1
    g2: Circle CenterX=-3.5 CenterY=7 CenterZ=0 NormalX=0 NormalY=0 NormalZ=1 AngleXU=0 Radius=1
    g3: BSplineCurve PolesCount=3 KnotsCount=2 Degree=2 IsPeriodic=0
    g4: GeomPoint X=-3.5 Y=23.5 Z=0
    g5: GeomPoint X=-3.5 Y=7 Z=0
    g6: LineSegment StartX=-3.5 StartY=28.2 StartZ=0 EndX=-3.5 EndY=23.5 EndZ=0
    g7: LineSegment StartX=0 StartY=29.5 StartZ=0 EndX=0 EndY=30 EndZ=0
    g8: LineSegment StartX=-3.5 StartY=28.2 StartZ=0 EndX=-3.5 EndY=30 EndZ=0
    g9: LineSegment StartX=0 StartY=30 StartZ=0 EndX=0 EndY=30.5 EndZ=0
    g10: LineSegment StartX=0 StartY=30.5 StartZ=0 EndX=-3.5 EndY=30.5 EndZ=0
    g11: LineSegment StartX=-3.5 StartY=30.5 StartZ=0 EndX=-3.5 EndY=30 EndZ=0
    g12: LineSegment StartX=0 StartY=29.5 StartZ=0 EndX=0 EndY=5 EndZ=0
    g13: LineSegment StartX=-3.5 StartY=0.3 StartZ=0 EndX=-3.5 EndY=7 EndZ=0
    g14: LineSegment StartX=-3.5 StartY=0.3 StartZ=0 EndX=0 EndY=0.3 EndZ=0
    g15: LineSegment StartX=0 StartY=5 StartZ=0 EndX=0 EndY=0.3 EndZ=0
  constraints (39):
    c: Weight(g0) = 1
    c: Equal(g0,g1)
    c: Equal(g0,g2)
    c: InternalAlignment(g0,g3)
    c: InternalAlignment(g1,g3)
    c: InternalAlignment(g2,g3)
    c: InternalAlignment(g4,g3)
    c: InternalAlignment(g5,g3)
    c: Block(g3)
    c: Coincident(g6,g3)
    c: Vertical(g6)
    c: Vertical(g7)
    c: Distance(g7) = 0.5
    c: Coincident(g8,g6)
    c: Vertical(g8)
    c: Block(g6)
    c: Block(g7)
    c: Vertical(g9)
    c: Equal(g7,g9) = 0.5
    c: Block(g9)
    c: Coincident(g9,g7)
    c: Horizontal(g10)
    c: Coincident(g10,g9)
    c: Coincident(g11,g10)
    c: Coincident(g11,g8)
    c: Vertical(g11)
    c: Block(g11)
    c: Coincident(g12,g7)
    c: Vertical(g12)
    c: Coincident(g13,g3)
    c: Vertical(g13)
    c: Distance(g13) = 6.7
    c: Coincident(g14,g13)
    c: Horizontal(g14)
    c: Block(g14)
    c: Coincident(g15,g12)
    c: Coincident(g15,g14)
    c: Vertical(g15)
    c: Block(g15)
FEATURE [Sketcher::SketchObject] Sketch017
  FullyConstrained = true
  sketch-geometry (11):
    g0: LineSegment StartX=-3.5 StartY=1e-16 StartZ=0 EndX=-1.6 EndY=1e-16 EndZ=0
    g1: LineSegment StartX=-1.6 StartY=1e-16 StartZ=0 EndX=-1.6 EndY=1.5 EndZ=0
    g2: LineSegment StartX=-3.5 StartY=1.5 StartZ=0 EndX=-1.6 EndY=1.5 EndZ=0
    g3: LineSegment StartX=-3.5 StartY=1e-16 StartZ=0 EndX=-4.8 EndY=1e-16 EndZ=0
    g4: Circle CenterX=-3.5 CenterY=1.3 CenterZ=0 NormalX=0 NormalY=0 NormalZ=1 AngleXU=0 Radius=1
    g5: Circle CenterX=-3.5 CenterY=1e-16 CenterZ=0 NormalX=0 NormalY=0 NormalZ=1 AngleXU=0 Radius=1
    g6: Circle CenterX=-4.8 CenterY=1e-16 CenterZ=0 NormalX=0 NormalY=0 NormalZ=1 AngleXU=0 Radius=1
    g7: BSplineCurve PolesCount=3 KnotsCount=2 Degree=2 IsPeriodic=0
    g8: GeomPoint X=-3.5 Y=1.3 Z=0
    g9: GeomPoint X=-4.8 Y=1e-16 Z=0
    g10: LineSegment StartX=-3.5 StartY=1.3 StartZ=0 EndX=-3.5 EndY=1.5 EndZ=0
  constraints (24):
    c: Horizontal(g0)
    c: Distance(g0) = 1.9
    c: Block(g0)
    c: Coincident(g1,g0)
    c: Vertical(g1)
    c: Coincident(g2,g1)
    c: Horizontal(g2)
    c: Coincident(g3,g0)
    c: Horizontal(g3)
    c: Distance(g3) = 1.3
    c: Weight(g4) = 1
    c: Equal(g4,g5)
    c: Coincident(g5,g0)
    c: Equal(g4,g6)
    c: Coincident(g7,g3)
    c: InternalAlignment(g4,g7)
    c: InternalAlignment(g5,g7)
    c: InternalAlignment(g6,g7)
    c: InternalAlignment(g8,g7)
    c: InternalAlignment(g9,g7)
    c: Coincident(g10,g7)
    c: Coincident(g10,g2)
    c: Vertical(g10)
    c: Block(g10)
FEATURE [Part::Feature] Face035
  shape: bbox 3.2 x 1.5 x 2e-07 mm, 1 faces, 0 solids (baked)
FEATURE [Part::Revolution] Revolve039  label="backCaseScrewRetainer"
  Angle = 360
  Axis = (0,1,0)
  Base = (0,0,0)
  FaceMakerClass = Part::FaceMakerBullseye
  Placement = pos=(12.5,3,62) rot=(0,0,1;0rad)
  Solid = false
  Source = -> Face035
  Symmetric = false
FEATURE [Part::Feature] Face036
  shape: bbox 3.2 x 1.5 x 2e-07 mm, 1 faces, 0 solids (baked)
FEATURE [Part::Feature] Face039
  shape: bbox 4.8 x 30.2 x 2e-07 mm, 1 faces, 0 solids (baked)
FEATURE [Part::Revolution] Revolve043  label="frontCaseScrewPost002"
  Angle = 360
  Axis = (0,1,0)
  Base = (0,0,0)
  FaceMakerClass = Part::FaceMakerBullseye
  Placement = pos=(89.5,4.5,3.5) rot=(0,0,1;0rad)
  Solid = false
  Source = -> Face039
  Symmetric = false
FEATURE [Part::Feature] Face042
  shape: bbox 4.8 x 30.2 x 2e-07 mm, 1 faces, 0 solids (baked)
FEATURE [Part::Revolution] Revolve046  label="frontCaseScrewPost003"
  Angle = 360
  Axis = (0,1,0)
  Base = (0,0,0)
  FaceMakerClass = Part::FaceMakerBullseye
  Placement = pos=(89.5,4.5,68.5) rot=(0,0,1;0rad)
  Solid = false
  Source = -> Face042
  Symmetric = false
FEATURE [Part::Feature] Face043
  shape: bbox 3.2 x 1.5 x 2e-07 mm, 1 faces, 0 solids (baked)
FEATURE [Part::Revolution] Revolve047  label="frontCaseScrewRetainer002"
  Angle = 360
  Axis = (0,1,0)
  Base = (0,0,0)
  FaceMakerClass = Part::FaceMakerBullseye
  Placement = pos=(89.5,3,68.5) rot=(0,0,1;0rad)
  Solid = false
  Source = -> Face043
  Symmetric = false
FEATURE [Part::Feature] Face044
  shape: bbox 3.2 x 1.5 x 2e-07 mm, 1 faces, 0 solids (baked)
FEATURE [Part::Revolution] Revolve048  label="frontCaseScrewRetainer003"
  Angle = 360
  Axis = (0,1,0)
  Base = (0,0,0)
  FaceMakerClass = Part::FaceMakerBullseye
  Placement = pos=(89.5,3,3.5) rot=(0,0,1;0rad)
  Solid = false
  Source = -> Face044
  Symmetric = false
FEATURE [App::MeasureDistance] Distance002  label="Distance: 1.67 mm"
  Distance = 1.66921
  P1 = (99.2361,4.7524,71.7)
  P2 = (99.2347,6.42161,71.7)
FEATURE [Sketcher::SketchObject] Sketch018
  FullyConstrained = true
  sketch-geometry (7):
    g0: LineSegment StartX=0 StartY=0 StartZ=0 EndX=0 EndY=6 EndZ=0
    g1: Circle CenterX=0 CenterY=0 CenterZ=0 NormalX=0 NormalY=0 NormalZ=1 AngleXU=0 Radius=1
    g2: Circle CenterX=8 CenterY=6 CenterZ=0 NormalX=0 NormalY=0 NormalZ=1 AngleXU=0 Radius=1
    g3: BSplineCurve PolesCount=3 KnotsCount=2 Degree=2 IsPeriodic=0
    g4: GeomPoint X=0 Y=0 Z=0
    g5: GeomPoint X=8 Y=6 Z=0
    g6: LineSegment StartX=0 StartY=6 StartZ=0 EndX=8 EndY=6 EndZ=0
  constraints (14):
    c: Coincident(g0,g-1)
    c: Distance(g0) = 6
    c: Vertical(g0)
    c: Coincident(g3,g0)
    c: Weight(g1) = 1
    c: Equal(g1,g2)
    c: InternalAlignment(g1,g3)
    c: InternalAlignment(g2,g3)
    c: InternalAlignment(g4,g3)
    c: InternalAlignment(g5,g3)
    c: Block(g3)
    c: Coincident(g6,g0)
    c: Coincident(g6,g3)
    c: Horizontal(g6)
FEATURE [Part::Extrusion] Extrude012  label="caseScrewPillarBracket"
  Base = -> Sketch018
  Dir = (0,0,1)
  DirMode = 2
  FaceMakerClass = Part::FaceMakerBullseye
  LengthFwd = 2.4
  LengthRev = 0
  Placement = pos=(15.76,29,8.8) rot=(0,1,0;0rad)
  Solid = true
  Symmetric = false
FEATURE [Sketcher::SketchObject] Sketch019
  FullyConstrained = true
  sketch-geometry (7):
    g0: LineSegment StartX=0 StartY=0 StartZ=0 EndX=0 EndY=6 EndZ=0
    g1: Circle CenterX=0 CenterY=0 CenterZ=0 NormalX=0 NormalY=0 NormalZ=1 AngleXU=0 Radius=1
    g2: Circle CenterX=8 CenterY=6 CenterZ=0 NormalX=0 NormalY=0 NormalZ=1 AngleXU=0 Radius=1
    g3: BSplineCurve PolesCount=3 KnotsCount=2 Degree=2 IsPeriodic=0
    g4: GeomPoint X=0 Y=0 Z=0
    g5: GeomPoint X=8 Y=6 Z=0
    g6: LineSegment StartX=0 StartY=6 StartZ=0 EndX=8 EndY=6 EndZ=0
  constraints (14):
    c: Coincident(g0,g-1)
    c: Distance(g0) = 6
    c: Vertical(g0)
    c: Coincident(g3,g0)
    c: Weight(g1) = 1
    c: Equal(g1,g2)
    c: InternalAlignment(g1,g3)
    c: InternalAlignment(g2,g3)
    c: InternalAlignment(g4,g3)
    c: InternalAlignment(g5,g3)
    c: Block(g3)
    c: Coincident(g6,g0)
    c: Coincident(g6,g3)
    c: Horizontal(g6)
FEATURE [Part::Extrusion] Extrude013  label="caseScrewPillarBracket001"
  Base = -> Sketch019
  Dir = (0,0,1)
  DirMode = 2
  FaceMakerClass = Part::FaceMakerBullseye
  LengthFwd = 2.4
  LengthRev = 0
  Placement = pos=(15.76,29,60.8) rot=(0,0,1;0rad)
  Solid = true
  Symmetric = false
FEATURE [Sketcher::SketchObject] Sketch020
  FullyConstrained = true
  sketch-geometry (7):
    g0: LineSegment StartX=0 StartY=0 StartZ=0 EndX=0 EndY=6 EndZ=0
    g1: Circle CenterX=0 CenterY=0 CenterZ=0 NormalX=0 NormalY=0 NormalZ=1 AngleXU=0 Radius=1
    g2: Circle CenterX=8 CenterY=6 CenterZ=0 NormalX=0 NormalY=0 NormalZ=1 AngleXU=0 Radius=1
    g3: BSplineCurve PolesCount=3 KnotsCount=2 Degree=2 IsPeriodic=0
    g4: GeomPoint X=0 Y=0 Z=0
    g5: GeomPoint X=8 Y=6 Z=0
    g6: LineSegment StartX=0 StartY=6 StartZ=0 EndX=8 EndY=6 EndZ=0
  constraints (14):
    c: Coincident(g0,g-1)
    c: Distance(g0) = 6
    c: Vertical(g0)
    c: Coincident(g3,g0)
    c: Weight(g1) = 1
    c: Equal(g1,g2)
    c: InternalAlignment(g1,g3)
    c: InternalAlignment(g2,g3)
    c: InternalAlignment(g4,g3)
    c: InternalAlignment(g5,g3)
    c: Block(g3)
    c: Coincident(g6,g0)
    c: Coincident(g6,g3)
    c: Horizontal(g6)
FEATURE [Part::Extrusion] Extrude014  label="caseScrewPillarBracket002"
  Base = -> Sketch020
  Dir = (0,0,1)
  DirMode = 2
  FaceMakerClass = Part::FaceMakerBullseye
  LengthFwd = 2.4
  LengthRev = 0
  Placement = pos=(13.7,29,13.26) rot=(0,-1,0;1.5708rad)
  Solid = true
  Symmetric = false
FEATURE [Sketcher::SketchObject] Sketch021
  FullyConstrained = true
  sketch-geometry (7):
    g0: LineSegment StartX=0 StartY=0 StartZ=0 EndX=0 EndY=6 EndZ=0
    g1: Circle CenterX=0 CenterY=0 CenterZ=0 NormalX=0 NormalY=0 NormalZ=1 AngleXU=0 Radius=1
    g2: Circle CenterX=8 CenterY=6 CenterZ=0 NormalX=0 NormalY=0 NormalZ=1 AngleXU=0 Radius=1
    g3: BSplineCurve PolesCount=3 KnotsCount=2 Degree=2 IsPeriodic=0
    g4: GeomPoint X=0 Y=0 Z=0
    g5: GeomPoint X=8 Y=6 Z=0
    g6: LineSegment StartX=0 StartY=6 StartZ=0 EndX=8 EndY=6 EndZ=0
  constraints (14):
    c: Coincident(g0,g-1)
    c: Distance(g0) = 6
    c: Vertical(g0)
    c: Coincident(g3,g0)
    c: Weight(g1) = 1
    c: Equal(g1,g2)
    c: InternalAlignment(g1,g3)
    c: InternalAlignment(g2,g3)
    c: InternalAlignment(g4,g3)
    c: InternalAlignment(g5,g3)
    c: Block(g3)
    c: Coincident(g6,g0)
    c: Coincident(g6,g3)
    c: Horizontal(g6)
FEATURE [Part::Extrusion] Extrude015  label="caseScrewPillarBracket003"
  Base = -> Sketch021
  Dir = (0,0,1)
  DirMode = 2
  FaceMakerClass = Part::FaceMakerBullseye
  LengthFwd = 2.4
  LengthRev = 0
  Placement = pos=(11.3,29,58.74) rot=(0,1,0;1.5708rad)
  Solid = true
  Symmetric = false
FEATURE [Sketcher::SketchObject] Sketch022
  FullyConstrained = true
  sketch-geometry (7):
    g0: LineSegment StartX=0 StartY=0 StartZ=0 EndX=0 EndY=6 EndZ=0
    g1: Circle CenterX=0 CenterY=0 CenterZ=0 NormalX=0 NormalY=0 NormalZ=1 AngleXU=0 Radius=1
    g2: Circle CenterX=8 CenterY=6 CenterZ=0 NormalX=0 NormalY=0 NormalZ=1 AngleXU=0 Radius=1
    g3: BSplineCurve PolesCount=3 KnotsCount=2 Degree=2 IsPeriodic=0
    g4: GeomPoint X=0 Y=0 Z=0
    g5: GeomPoint X=8 Y=6 Z=0
    g6: LineSegment StartX=0 StartY=6 StartZ=0 EndX=8 EndY=6 EndZ=0
  constraints (14):
    c: Coincident(g0,g-1)
    c: Distance(g0) = 6
    c: Vertical(g0)
    c: Coincident(g3,g0)
    c: Weight(g1) = 1
    c: Equal(g1,g2)
    c: InternalAlignment(g1,g3)
    c: InternalAlignment(g2,g3)
    c: InternalAlignment(g4,g3)
    c: InternalAlignment(g5,g3)
    c: Block(g3)
    c: Coincident(g6,g0)
    c: Coincident(g6,g3)
    c: Horizontal(g6)
FEATURE [Part::Extrusion] Extrude016  label="caseScrewPillarBracket004"
  Base = -> Sketch022
  Dir = (0,0,1)
  DirMode = 2
  FaceMakerClass = Part::FaceMakerBullseye
  LengthFwd = 2.4
  LengthRev = 0
  Placement = pos=(88.3,29,65.23) rot=(0,1,0;1.5708rad)
  Solid = true
  Symmetric = false
FEATURE [Sketcher::SketchObject] Sketch023
  FullyConstrained = true
  sketch-geometry (7):
    g0: LineSegment StartX=0 StartY=0 StartZ=0 EndX=0 EndY=6 EndZ=0
    g1: Circle CenterX=0 CenterY=0 CenterZ=0 NormalX=0 NormalY=0 NormalZ=1 AngleXU=0 Radius=1
    g2: Circle CenterX=8 CenterY=6 CenterZ=0 NormalX=0 NormalY=0 NormalZ=1 AngleXU=0 Radius=1
    g3: BSplineCurve PolesCount=3 KnotsCount=2 Degree=2 IsPeriodic=0
    g4: GeomPoint X=0 Y=0 Z=0
    g5: GeomPoint X=8 Y=6 Z=0
    g6: LineSegment StartX=0 StartY=6 StartZ=0 EndX=8 EndY=6 EndZ=0
  constraints (14):
    c: Coincident(g0,g-1)
    c: Distance(g0) = 6
    c: Vertical(g0)
    c: Coincident(g3,g0)
    c: Weight(g1) = 1
    c: Equal(g1,g2)
    c: InternalAlignment(g1,g3)
    c: InternalAlignment(g2,g3)
    c: InternalAlignment(g4,g3)
    c: InternalAlignment(g5,g3)
    c: Block(g3)
    c: Coincident(g6,g0)
    c: Coincident(g6,g3)
    c: Horizontal(g6)
FEATURE [Part::Extrusion] Extrude017  label="caseScrewPillarBracket005"
  Base = -> Sketch023
  Dir = (0,0,1)
  DirMode = 2
  FaceMakerClass = Part::FaceMakerBullseye
  LengthFwd = 2.4
  LengthRev = 0
  Placement = pos=(90.7,29,6.77) rot=(0,-1,0;1.5708rad)
  Solid = true
  Symmetric = false
FEATURE [Sketcher::SketchObject] Sketch024
  FullyConstrained = true
  sketch-geometry (7):
    g0: LineSegment StartX=0 StartY=0 StartZ=0 EndX=0 EndY=6 EndZ=0
    g1: Circle CenterX=0 CenterY=0 CenterZ=0 NormalX=0 NormalY=0 NormalZ=1 AngleXU=0 Radius=1
    g2: Circle CenterX=8 CenterY=6 CenterZ=0 NormalX=0 NormalY=0 NormalZ=1 AngleXU=0 Radius=1
    g3: BSplineCurve PolesCount=3 KnotsCount=2 Degree=2 IsPeriodic=0
    g4: GeomPoint X=0 Y=0 Z=0
    g5: GeomPoint X=8 Y=6 Z=0
    g6: LineSegment StartX=0 StartY=6 StartZ=0 EndX=8 EndY=6 EndZ=0
  constraints (14):
    c: Coincident(g0,g-1)
    c: Distance(g0) = 6
    c: Vertical(g0)
    c: Coincident(g3,g0)
    c: Weight(g1) = 1
    c: Equal(g1,g2)
    c: InternalAlignment(g1,g3)
    c: InternalAlignment(g2,g3)
    c: InternalAlignment(g4,g3)
    c: InternalAlignment(g5,g3)
    c: Block(g3)
    c: Coincident(g6,g0)
    c: Coincident(g6,g3)
    c: Horizontal(g6)
FEATURE [Part::Extrusion] Extrude018  label="caseScrewPillarBracket006"
  Base = -> Sketch024
  Dir = (0,0,1)
  DirMode = 2
  FaceMakerClass = Part::FaceMakerBullseye
  LengthFwd = 2.4
  LengthRev = 0
  Placement = pos=(103.7,29,6.77) rot=(0,-1,0;1.5708rad)
  Solid = true
  Symmetric = false
FEATURE [Sketcher::SketchObject] Sketch025
  FullyConstrained = true
  sketch-geometry (7):
    g0: LineSegment StartX=0 StartY=0 StartZ=0 EndX=0 EndY=6 EndZ=0
    g1: Circle CenterX=0 CenterY=0 CenterZ=0 NormalX=0 NormalY=0 NormalZ=1 AngleXU=0 Radius=1
    g2: Circle CenterX=8 CenterY=6 CenterZ=0 NormalX=0 NormalY=0 NormalZ=1 AngleXU=0 Radius=1
    g3: BSplineCurve PolesCount=3 KnotsCount=2 Degree=2 IsPeriodic=0
    g4: GeomPoint X=0 Y=0 Z=0
    g5: GeomPoint X=8 Y=6 Z=0
    g6: LineSegment StartX=0 StartY=6 StartZ=0 EndX=8 EndY=6 EndZ=0
  constraints (14):
    c: Coincident(g0,g-1)
    c: Distance(g0) = 6
    c: Vertical(g0)
    c: Coincident(g3,g0)
    c: Weight(g1) = 1
    c: Equal(g1,g2)
    c: InternalAlignment(g1,g3)
    c: InternalAlignment(g2,g3)
    c: InternalAlignment(g4,g3)
    c: InternalAlignment(g5,g3)
    c: Block(g3)
    c: Coincident(g6,g0)
    c: Coincident(g6,g3)
    c: Horizontal(g6)
FEATURE [Part::Extrusion] Extrude019  label="caseScrewPillarBracket007"
  Base = -> Sketch025
  Dir = (0,0,1)
  DirMode = 2
  FaceMakerClass = Part::FaceMakerBullseye
  LengthFwd = 2.4
  LengthRev = 0
  Placement = pos=(101.3,29,65.23) rot=(0,1,0;1.5708rad)
  Solid = true
  Symmetric = false
FEATURE [Part::Box] Box011  label="frontCaseScrewPillarBracket"
  AttacherType = Attacher::AttachEngine3D
  Height = 2.4
  Length = 16
  Placement = pos=(87,28,2.3) rot=(0,0,1;0rad)
  Width = 7
FEATURE [Part::Box] Box012  label="frontCaseScrewPillarBracket001"
  AttacherType = Attacher::AttachEngine3D
  Height = 2.4
  Length = 16
  Placement = pos=(87,28,67.3) rot=(0,0,1;0rad)
  Width = 7
FEATURE [Sketcher::SketchObject] Sketch026
  FullyConstrained = true
  sketch-geometry (17):
    g0: Circle CenterX=-3.5 CenterY=23.5 CenterZ=0 NormalX=0 NormalY=0 NormalZ=1 AngleXU=0 Radius=1
    g1: Circle CenterX=-1 CenterY=15.25 CenterZ=0 NormalX=0 NormalY=0 NormalZ=1 AngleXU=0 Radius=1
    g2: Circle CenterX=-3.5 CenterY=7 CenterZ=0 NormalX=0 NormalY=0 NormalZ=1 AngleXU=0 Radius=1
    g3: BSplineCurve PolesCount=3 KnotsCount=2 Degree=2 IsPeriodic=0
    g4: GeomPoint X=-3.5 Y=23.5 Z=0
    g5: GeomPoint X=-3.5 Y=7 Z=0
    g6: Circle CenterX=-4.8 CenterY=30.5 CenterZ=0 NormalX=0 NormalY=0 NormalZ=1 AngleXU=0 Radius=1
    g7: Circle CenterX=-3.5 CenterY=30.5 CenterZ=0 NormalX=0 NormalY=0 NormalZ=1 AngleXU=0 Radius=1
    g8: Circle CenterX=-3.5 CenterY=29.2 CenterZ=0 NormalX=0 NormalY=0 NormalZ=1 AngleXU=0 Radius=1
    g9: BSplineCurve PolesCount=3 KnotsCount=2 Degree=2 IsPeriodic=0
    g10: GeomPoint X=-4.8 Y=30.5 Z=0
    g11: GeomPoint X=-3.5 Y=29.2 Z=0
    g12: LineSegment StartX=-3.5 StartY=29.2 StartZ=0 EndX=-3.5 EndY=23.5 EndZ=0
    g13: LineSegment StartX=-4.8 StartY=30.5 StartZ=0 EndX=0 EndY=30.5 EndZ=0
    g14: LineSegment StartX=-3.5 StartY=5 StartZ=0 EndX=-3.5 EndY=7 EndZ=0
    g15: LineSegment StartX=0 StartY=5 StartZ=0 EndX=0 EndY=30.5 EndZ=0
    g16: LineSegment StartX=-3.5 StartY=5 StartZ=0 EndX=0 EndY=5 EndZ=0
  constraints (33):
    c: Weight(g0) = 1
    c: Equal(g0,g1)
    c: Equal(g0,g2)
    c: InternalAlignment(g0,g3)
    c: InternalAlignment(g1,g3)
    c: InternalAlignment(g2,g3)
    c: InternalAlignment(g4,g3)
    c: InternalAlignment(g5,g3)
    c: Block(g3)
    c: Weight(g6) = 1
    c: Equal(g6,g7)
    c: Equal(g6,g8)
    c: InternalAlignment(g6,g9)
    c: InternalAlignment(g7,g9)
    c: InternalAlignment(g8,g9)
    c: InternalAlignment(g10,g9)
    c: InternalAlignment(g11,g9)
    c: Block(g9)
    c: Coincident(g12,g9)
    c: Coincident(g12,g3)
    c: Vertical(g12)
    c: Coincident(g13,g9)
    c: Horizontal(g13)
    c: Distance(g13) = 4.8
    c: Coincident(g14,g3)
    c: Vertical(g14)
    c: Coincident(g15,g13)
    c: Vertical(g15)
    c: Tangent(g15,g1)
    c: Distance(g14) = 2
    c: Coincident(g16,g14)
    c: Horizontal(g16)
    c: Coincident(g15,g16)
FEATURE [Part::Feature] Face050
  shape: bbox 4.8 x 25.5 x 2e-07 mm, 1 faces, 0 solids (baked)
FEATURE [Part::Revolution] Revolve054  label="moreFrontCaseScrewPost001"
  Angle = 360
  Axis = (0,1,0)
  Base = (0,0,0)
  FaceMakerClass = Part::FaceMakerBullseye
  Placement = pos=(102.5,4.5,3.5) rot=(0,0,1;0rad)
  Solid = false
  Source = -> Face050
  Symmetric = false
FEATURE [Part::Feature] Face051
  shape: bbox 4.8 x 25.5 x 2e-07 mm, 1 faces, 0 solids (baked)
FEATURE [Part::Revolution] Revolve055  label="moreFrontCaseScrewPost002"
  Angle = 360
  Axis = (0,1,0)
  Base = (0,0,0)
  FaceMakerClass = Part::FaceMakerBullseye
  Placement = pos=(102.5,4.5,68.5) rot=(0,0,1;0rad)
  Solid = false
  Source = -> Face051
  Symmetric = false
FEATURE [Sketcher::SketchObject] Sketch027
  FullyConstrained = true
  sketch-geometry (10):
    g0: LineSegment StartX=-1.6 StartY=4.7 StartZ=0 EndX=-1.6 EndY=1.7 EndZ=0
    g1: LineSegment StartX=-3.5 StartY=4.7 StartZ=0 EndX=-1.6 EndY=4.7 EndZ=0
    g2: LineSegment StartX=-1.6 StartY=1.7 StartZ=0 EndX=-1.6 EndY=1.5 EndZ=0
    g3: LineSegment StartX=-1.6 StartY=1.5 StartZ=0 EndX=-5.2 EndY=1.5 EndZ=0
    g4: Circle CenterX=-3.5 CenterY=4.7 CenterZ=0 NormalX=0 NormalY=0 NormalZ=1 AngleXU=0 Radius=1
    g5: Circle CenterX=-3.59627 CenterY=2.99743 CenterZ=0 NormalX=0 NormalY=0 NormalZ=1 AngleXU=0 Radius=1
    g6: Circle CenterX=-5.2 CenterY=1.5 CenterZ=0 NormalX=0 NormalY=0 NormalZ=1 AngleXU=0 Radius=1
    g7: BSplineCurve PolesCount=3 KnotsCount=2 Degree=2 IsPeriodic=0
    g8: GeomPoint X=-3.5 Y=4.7 Z=0
    g9: GeomPoint X=-5.2 Y=1.5 Z=0
  constraints (23):
    c: Vertical(g0)
    c: Distance(g0) = 3
    c: Coincident(g1,g0)
    c: Horizontal(g1)
    c: Block(g0)
    c: Block(g1)
    c: Coincident(g2,g0)
    c: Vertical(g2)
    c: Distance(g2) = 0.2
    c: Coincident(g3,g2)
    c: Horizontal(g3)
    c: Block(g3)
    c: Coincident(g7,g1)
    c: Weight(g4) = 1
    c: Equal(g4,g5)
    c: Equal(g4,g6)
    c: Coincident(g7,g3)
    c: InternalAlignment(g4,g7)
    c: InternalAlignment(g5,g7)
    c: InternalAlignment(g6,g7)
    c: InternalAlignment(g8,g7)
    c: InternalAlignment(g9,g7)
    c: Block(g7)
FEATURE [Sketcher::SketchObject] Sketch028
  FullyConstrained = true
  sketch-geometry (18):
    g0: LineSegment StartX=0 StartY=3e-16 StartZ=0 EndX=0 EndY=1.7 EndZ=0
    g1: LineSegment StartX=-3.5 StartY=0 StartZ=0 EndX=-3.5 EndY=0.9 EndZ=0
    g2: Circle CenterX=-2.7 CenterY=1.7 CenterZ=0 NormalX=0 NormalY=0 NormalZ=1 AngleXU=0 Radius=1
    g3: Circle CenterX=-3.5 CenterY=1.7 CenterZ=0 NormalX=0 NormalY=0 NormalZ=1 AngleXU=0 Radius=1
    g4: Circle CenterX=-3.5 CenterY=0.9 CenterZ=0 NormalX=0 NormalY=0 NormalZ=1 AngleXU=0 Radius=1
    g5: BSplineCurve PolesCount=3 KnotsCount=2 Degree=2 IsPeriodic=0
    g6: GeomPoint X=-2.7 Y=1.7 Z=0
    g7: GeomPoint X=-3.5 Y=0.9 Z=0
    g8: LineSegment StartX=-3.5 StartY=0 StartZ=0 EndX=-3.5 EndY=-7 EndZ=0
    g9: LineSegment StartX=0 StartY=3e-16 StartZ=0 EndX=0 EndY=-7 EndZ=0
    g10: LineSegment StartX=-3.5 StartY=-7 StartZ=0 EndX=0 EndY=-7 EndZ=0
    g11: LineSegment StartX=-2.7 StartY=1.7 StartZ=0 EndX=-1.6 EndY=1.7 EndZ=0
    g12: LineSegment StartX=0 StartY=1.7 StartZ=0 EndX=0 EndY=4.5 EndZ=0
    g13: LineSegment StartX=0 StartY=4.5 StartZ=0 EndX=0 EndY=10.8 EndZ=0
    g14: LineSegment StartX=0 StartY=10.8 StartZ=0 EndX=-2 EndY=10.8 EndZ=0
    g15: LineSegment StartX=-1.6 StartY=4.7 StartZ=0 EndX=-1.6 EndY=1.7 EndZ=0
    g16: LineSegment StartX=-1.6 StartY=4.7 StartZ=0 EndX=-2 EndY=4.7 EndZ=0
    g17: LineSegment StartX=-2 StartY=4.7 StartZ=0 EndX=-2 EndY=10.8 EndZ=0
  constraints (44):
    c: Vertical(g0)
    c: Vertical(g1)
    c: Distance(g1) = 0.9
    c: Block(g0)
    c: Distance(g0) = 1.7
    c: Weight(g2) = 1
    c: Equal(g2,g3)
    c: Equal(g2,g4)
    c: Coincident(g5,g1)
    c: InternalAlignment(g2,g5)
    c: InternalAlignment(g3,g5)
    c: InternalAlignment(g4,g5)
    c: InternalAlignment(g6,g5)
    c: InternalAlignment(g7,g5)
    c: Block(g5)
    c: Coincident(g8,g1)
    c: Vertical(g8)
    c: Distance(g8) = 7
    c: Vertical(g9)
    c: Equal(g8,g9) = 7
    c: Coincident(g9,g0)
    c: Coincident(g10,g8)
    c: Coincident(g10,g9)
    c: Horizontal(g10)
    c: Coincident(g11,g5)
    c: Horizontal(g11)
    c: Coincident(g12,g0)
    c: Vertical(g12)
    c: Distance(g12) = 2.8
    c: Coincident(g13,g12)
    c: Vertical(g13)
    c: Distance(g13) = 6.3
    c: Coincident(g14,g13)
    c: Horizontal(g14)
    c: Distance(g14) = 2
    c: Vertical(g15)
    c: Distance(g15) = 3
    c: Block(g11)
    c: Coincident(g15,g11)
    c: Coincident(g16,g15)
    c: Horizontal(g16)
    c: Coincident(g17,g16)
    c: Coincident(g17,g14)
    c: Vertical(g17)
FEATURE [Part::Revolution] Revolve040  label="backCaseScrewRetainer001"
  Angle = 360
  Axis = (0,1,0)
  Base = (0,0,0)
  FaceMakerClass = Part::FaceMakerBullseye
  Placement = pos=(12.5,3,10) rot=(0,0,1;0rad)
  Solid = false
  Source = -> Face036
  Symmetric = false
FEATURE [Part::Feature] Face055
  shape: bbox 3.5 x 30.2 x 2e-07 mm, 1 faces, 0 solids (baked)
FEATURE [Part::Revolution] Revolve059  label="backCaseScrewPost"
  Angle = 360
  Axis = (0,1,0)
  Base = (0,0,0)
  FaceMakerClass = Part::FaceMakerBullseye
  Placement = pos=(12.5,4.5,10) rot=(0,0,1;0rad)
  Solid = false
  Source = -> Face055
  Symmetric = false
FEATURE [Part::Feature] Face056
  shape: bbox 3.5 x 30.2 x 2e-07 mm, 1 faces, 0 solids (baked)
FEATURE [Part::Revolution] Revolve060  label="backCaseScrewPost001"
  Angle = 360
  Axis = (0,1,0)
  Base = (0,0,0)
  FaceMakerClass = Part::FaceMakerBullseye
  Placement = pos=(12.5,4.5,62) rot=(0,0,1;0rad)
  Solid = false
  Source = -> Face056
  Symmetric = false
FEATURE [Part::Feature] Face057
  shape: bbox 3.5 x 17.8 x 2e-07 mm, 1 faces, 0 solids (baked)
FEATURE [Part::Revolution] Revolve061  label="removeToCreateScrewAndThreadedInsertHole"
  Angle = 360
  Axis = (0,1,0)
  Base = (0,0,0)
  FaceMakerClass = Part::FaceMakerBullseye
  Placement = pos=(12.5,0,10) rot=(0,0,1;0rad)
  Solid = false
  Source = -> Face057
  Symmetric = false
FEATURE [Part::Feature] Face058
  shape: bbox 3.5 x 17.8 x 2e-07 mm, 1 faces, 0 solids (baked)
FEATURE [Part::Revolution] Revolve062  label="removeToCreateScrewAndThreadedInsertHole001"
  Angle = 360
  Axis = (0,1,0)
  Base = (0,0,0)
  FaceMakerClass = Part::FaceMakerBullseye
  Placement = pos=(12.5,0,62) rot=(0,0,1;0rad)
  Solid = false
  Source = -> Face058
  Symmetric = false
FEATURE [Part::Feature] Face059
  shape: bbox 3.5 x 17.8 x 2e-07 mm, 1 faces, 0 solids (baked)
FEATURE [Part::Revolution] Revolve063  label="removeToCreateScrewAndThreadedInsertHole002"
  Angle = 360
  Axis = (0,1,0)
  Base = (0,0,0)
  FaceMakerClass = Part::FaceMakerBullseye
  Placement = pos=(89.5,0,68.5) rot=(0,0,1;0rad)
  Solid = false
  Source = -> Face059
  Symmetric = false
FEATURE [Part::Feature] Face060
  shape: bbox 3.5 x 17.8 x 2e-07 mm, 1 faces, 0 solids (baked)
FEATURE [Part::Revolution] Revolve064  label="removeToCreateScrewAndThreadedInsertHole003"
  Angle = 360
  Axis = (0,1,0)
  Base = (0,0,0)
  FaceMakerClass = Part::FaceMakerBullseye
  Placement = pos=(89.5,0,3.5) rot=(0,0,1;0rad)
  Solid = false
  Source = -> Face060
  Symmetric = false
FEATURE [Part::Feature] Face061
  shape: bbox 3.5 x 17.8 x 2e-07 mm, 1 faces, 0 solids (baked)
FEATURE [Part::Revolution] Revolve065  label="removeToCreateScrewAndThreadedInsertHole004"
  Angle = 360
  Axis = (0,1,0)
  Base = (0,0,0)
  FaceMakerClass = Part::FaceMakerBullseye
  Placement = pos=(102.5,4.7,3.5) rot=(0,0,1;0rad)
  Solid = false
  Source = -> Face061
  Symmetric = false
FEATURE [Part::Feature] Face062
  shape: bbox 3.5 x 17.8 x 2e-07 mm, 1 faces, 0 solids (baked)
FEATURE [Part::Revolution] Revolve066  label="removeToCreateScrewAndThreadedInsertHole005"
  Angle = 360
  Axis = (0,1,0)
  Base = (0,0,0)
  FaceMakerClass = Part::FaceMakerBullseye
  Placement = pos=(102.5,4.7,68.5) rot=(0,0,1;0rad)
  Solid = false
  Source = -> Face062
  Symmetric = false
FEATURE [Part::MultiFuse] Fusion047  label="makeHoles"
  Shapes = -> [Revolve066,Revolve065,Revolve064,Revolve063,Revolve062,Revolve061]
FEATURE [Part::Feature] Face063
  shape: bbox 3.6 x 3.2 x 2e-07 mm, 1 faces, 0 solids (baked)
FEATURE [Part::Revolution] Revolve067  label="moreFrontCaseScrewRetainer002"
  Angle = 360
  Axis = (0,1,0)
  Base = (0,0,0)
  FaceMakerClass = Part::FaceMakerBullseye
  Placement = pos=(102.5,4.5,68.5) rot=(0,0,1;0rad)
  Solid = false
  Source = -> Face063
  Symmetric = false
FEATURE [Part::Feature] Face064
  shape: bbox 3.6 x 3.2 x 2e-07 mm, 1 faces, 0 solids (baked)
FEATURE [Part::Revolution] Revolve068  label="moreFrontCaseScrewRetainer003"
  Angle = 360
  Axis = (0,1,0)
  Base = (0,0,0)
  FaceMakerClass = Part::FaceMakerBullseye
  Placement = pos=(102.5,4.5,3.5) rot=(0,0,1;0rad)
  Solid = false
  Source = -> Face064
  Symmetric = false
FEATURE [Part::Feature] Face065
  shape: bbox 3.5 x 17.8 x 2e-07 mm, 1 faces, 0 solids (baked)
FEATURE [Part::Revolution] Revolve069  label="removeToCreateScrewAndThreadedInsertHole006"
  Angle = 360
  Axis = (0,1,0)
  Base = (0,0,0)
  FaceMakerClass = Part::FaceMakerBullseye
  Placement = pos=(12.5,0,10) rot=(0,0,1;0rad)
  Solid = false
  Source = -> Face065
  Symmetric = false
FEATURE [Part::Feature] Face066
  shape: bbox 3.5 x 17.8 x 2e-07 mm, 1 faces, 0 solids (baked)
FEATURE [Part::Revolution] Revolve070  label="removeToCreateScrewAndThreadedInsertHole007"
  Angle = 360
  Axis = (0,1,0)
  Base = (0,0,0)
  FaceMakerClass = Part::FaceMakerBullseye
  Placement = pos=(12.5,0,62) rot=(0,0,1;0rad)
  Solid = false
  Source = -> Face066
  Symmetric = false
FEATURE [Part::Feature] Face067
  shape: bbox 3.5 x 17.8 x 2e-07 mm, 1 faces, 0 solids (baked)
FEATURE [Part::Revolution] Revolve071  label="removeToCreateScrewAndThreadedInsertHole008"
  Angle = 360
  Axis = (0,1,0)
  Base = (0,0,0)
  FaceMakerClass = Part::FaceMakerBullseye
  Placement = pos=(89.5,0,68.5) rot=(0,0,1;0rad)
  Solid = false
  Source = -> Face067
  Symmetric = false
FEATURE [Part::Feature] Face068
  shape: bbox 3.5 x 17.8 x 2e-07 mm, 1 faces, 0 solids (baked)
FEATURE [Part::Revolution] Revolve072  label="removeToCreateScrewAndThreadedInsertHole009"
  Angle = 360
  Axis = (0,1,0)
  Base = (0,0,0)
  FaceMakerClass = Part::FaceMakerBullseye
  Placement = pos=(89.5,0,3.5) rot=(0,0,1;0rad)
  Solid = false
  Source = -> Face068
  Symmetric = false
FEATURE [Part::Feature] Face069
  shape: bbox 3.5 x 17.8 x 2e-07 mm, 1 faces, 0 solids (baked)
FEATURE [Part::Feature] Face070
  shape: bbox 3.5 x 17.8 x 2e-07 mm, 1 faces, 0 solids (baked)
FEATURE [Part::Revolution] Revolve073  label="removeToCreateScrewAndThreadedInsertHole010"
  Angle = 360
  Axis = (0,1,0)
  Base = (0,0,0)
  FaceMakerClass = Part::FaceMakerBullseye
  Placement = pos=(102.5,4.7,3.5) rot=(0,0,1;0rad)
  Solid = false
  Source = -> Face069
  Symmetric = false
FEATURE [Part::Revolution] Revolve074  label="removeToCreateScrewAndThreadedInsertHole011"
  Angle = 360
  Axis = (0,1,0)
  Base = (0,0,0)
  FaceMakerClass = Part::FaceMakerBullseye
  Placement = pos=(102.5,4.7,68.5) rot=(0,0,1;0rad)
  Solid = false
  Source = -> Face070
  Symmetric = false
FEATURE [Part::MultiFuse] Fusion048  label="makeHoles001"
  Shapes = -> [Revolve074,Revolve073,Revolve072,Revolve071,Revolve070,Revolve069]
FEATURE [Part::MultiFuse] Fusion049  label="caseScrewRetainers"
  Shapes = -> [Revolve067,Revolve068,Revolve048,Revolve047,Revolve039,Revolve040]
FEATURE [Part::Cut] Cut015  label="caseScrewRetainers001"
  Base = -> Fusion049
  Tool = -> Fusion048
FEATURE [Part::MultiFuse] Fusion050  label="casePillars"
  Shapes = -> [Revolve055,Revolve054,Revolve043,Revolve046,Revolve059,Revolve060]
FEATURE [Part::Feature] Face071 .. Face076  x6 (patterned run collapsed; names and placements below)
  shape: bbox 3.5 x 17.8 x 2e-07 mm, 1 faces, 0 solids (baked)
FEATURE [Part::Revolution] Revolve075  label="removeToCreateScrewAndThreadedInsertHole012"
  Angle = 360
  Axis = (0,1,0)
  Base = (0,0,0)
  FaceMakerClass = Part::FaceMakerBullseye
  Placement = pos=(12.5,0,10) rot=(0,0,1;0rad)
  Solid = false
  Source = -> Face071
  Symmetric = false
FEATURE [Part::Revolution] Revolve076  label="removeToCreateScrewAndThreadedInsertHole013"
  Angle = 360
  Axis = (0,1,0)
  Base = (0,0,0)
  FaceMakerClass = Part::FaceMakerBullseye
  Placement = pos=(12.5,0,62) rot=(0,0,1;0rad)
  Solid = false
  Source = -> Face072
  Symmetric = false
FEATURE [Part::Revolution] Revolve077  label="removeToCreateScrewAndThreadedInsertHole014"
  Angle = 360
  Axis = (0,1,0)
  Base = (0,0,0)
  FaceMakerClass = Part::FaceMakerBullseye
  Placement = pos=(89.5,0,68.5) rot=(0,0,1;0rad)
  Solid = false
  Source = -> Face073
  Symmetric = false
FEATURE [Part::Revolution] Revolve078  label="removeToCreateScrewAndThreadedInsertHole015"
  Angle = 360
  Axis = (0,1,0)
  Base = (0,0,0)
  FaceMakerClass = Part::FaceMakerBullseye
  Placement = pos=(89.5,0,3.5) rot=(0,0,1;0rad)
  Solid = false
  Source = -> Face074
  Symmetric = false
FEATURE [Part::Revolution] Revolve079  label="removeToCreateScrewAndThreadedInsertHole016"
  Angle = 360
  Axis = (0,1,0)
  Base = (0,0,0)
  FaceMakerClass = Part::FaceMakerBullseye
  Placement = pos=(102.5,4.7,3.5) rot=(0,0,1;0rad)
  Solid = false
  Source = -> Face075
  Symmetric = false
FEATURE [Part::Revolution] Revolve080  label="removeToCreateScrewAndThreadedInsertHole017"
  Angle = 360
  Axis = (0,1,0)
  Base = (0,0,0)
  FaceMakerClass = Part::FaceMakerBullseye
  Placement = pos=(102.5,4.7,68.5) rot=(0,0,1;0rad)
  Solid = false
  Source = -> Face076
  Symmetric = false
FEATURE [Part::MultiFuse] Fusion051  label="makeHoles002"
  Shapes = -> [Revolve080,Revolve079,Revolve078,Revolve077,Revolve076,Revolve075]
FEATURE [Part::Cut] Cut016  label="caesPillars"
  Base = -> Fusion050
  Tool = -> Fusion051
FEATURE [Part::Revolution] Revolve009  label="plugHousing016"
  Angle = 360
  Axis = (0,1,0)
  Base = (0,0,0)
  FaceMakerClass = Part::FaceMakerBullseye
  Placement = pos=(0,0,36.15) rot=(0,0,1;0rad)
  Solid = false
  Source = -> Face012
  Symmetric = false
FEATURE [Part::MultiFuse] Fusion014  label="plugHousing023"
  Placement = pos=(0,0,0) rot=(0,0,1;1.5708rad)
  Shapes = -> [Revolve011,Revolve009]
FEATURE [Part::Revolution] Revolve010  label="plugHousing017"
  Angle = 360
  Axis = (0,1,0)
  Base = (0,0,0)
  FaceMakerClass = Part::FaceMakerBullseye
  Placement = pos=(0,0,36.15) rot=(0,0,1;0rad)
  Solid = false
  Source = -> Face014
  Symmetric = false
FEATURE [Part::MultiFuse] Fusion015  label="plugHousing024"
  Placement = pos=(0,0,0) rot=(0,0,1;1.5708rad)
  Shapes = -> [Revolve010,Revolve015]
FEATURE [Part::Revolution] Revolve014  label="plugHousing026"
  Angle = 360
  Axis = (0,1,0)
  Base = (0,0,0)
  FaceMakerClass = Part::FaceMakerBullseye
  Placement = pos=(0,0,36.15) rot=(0,0,1;0rad)
  Solid = false
  Source = -> Face011
  Symmetric = false
FEATURE [Part::Revolution] Revolve013  label="plugHousing025"
  Angle = 360
  Axis = (0,1,0)
  Base = (0,0,0)
  FaceMakerClass = Part::FaceMakerBullseye
  Placement = pos=(0,0,36.15) rot=(0,0,1;0rad)
  Solid = false
  Source = -> Face015
  Symmetric = false
FEATURE [Part::MultiFuse] Fusion016  label="plugHousing028"
  Placement = pos=(0,19,0) rot=(0,0,1;3.14159rad)
  Shapes = -> [Fusion014,Fusion013]
FEATURE [Part::MultiFuse] Fusion011  label="plugHousing018"
  Placement = pos=(0,0,0) rot=(0,0,1;1.5708rad)
  Shapes = -> [Revolve014,Revolve013]
FEATURE [Part::MultiFuse] Fusion012  label="plugHousing019"
  Placement = pos=(0,19,0) rot=(0,0,1;3.14159rad)
  Shapes = -> [Fusion011,Fusion015]
FEATURE [Part::MultiFuse] Fusion017  label="plugHousing029"
  Placement = pos=(122.621,0,-0.15) rot=(0,0,1;0rad)
  Shapes = -> [Fusion016,Fusion012]
FEATURE [Part::MultiFuse] Fusion052  label="casePillarRetainers"
  Shapes = -> [Extrude012,Extrude013,Extrude014,Extrude015,Extrude016,Extrude017,Extrude018,Extrude019,Box011,Box012]
FEATURE [Part::Feature] Face077
  shape: bbox 3.5 x 17.8 x 2e-07 mm, 1 faces, 0 solids (baked)
FEATURE [Part::Revolution] Revolve081  label="removeToCreateScrewAndThreadedInsertHole018"
  Angle = 360
  Axis = (0,1,0)
  Base = (0,0,0)
  FaceMakerClass = Part::FaceMakerBullseye
  Placement = pos=(62.3,30.3,19.7) rot=(0,0,1;0rad)
  Solid = false
  Source = -> Face077
  Symmetric = false
FEATURE [Part::Feature] Face078
  shape: bbox 3.5 x 17.8 x 2e-07 mm, 1 faces, 0 solids (baked)
FEATURE [Part::Revolution] Revolve082  label="removeToCreateScrewAndThreadedInsertHole019"
  Angle = 360
  Axis = (0,1,0)
  Base = (0,0,0)
  FaceMakerClass = Part::FaceMakerBullseye
  Placement = pos=(62.3,30.3,51.7) rot=(0,0,1;0rad)
  Solid = false
  Source = -> Face078
  Symmetric = false
FEATURE [Part::Feature] Face079
  shape: bbox 3.5 x 17.8 x 2e-07 mm, 1 faces, 0 solids (baked)
FEATURE [Part::Revolution] Revolve083  label="removeToCreateScrewAndThreadedInsertHole020"
  Angle = 360
  Axis = (0,1,0)
  Base = (0,0,0)
  FaceMakerClass = Part::FaceMakerBullseye
  Placement = pos=(30.3,30.3,19.7) rot=(0,0,1;0rad)
  Solid = false
  Source = -> Face079
  Symmetric = false
FEATURE [Part::Feature] Face080
  shape: bbox 3.5 x 17.8 x 2e-07 mm, 1 faces, 0 solids (baked)
FEATURE [Part::Revolution] Revolve084  label="removeToCreateScrewAndThreadedInsertHole021"
  Angle = 360
  Axis = (0,1,0)
  Base = (0,0,0)
  FaceMakerClass = Part::FaceMakerBullseye
  Placement = pos=(30.3,30.3,51.7) rot=(0,0,1;0rad)
  Solid = false
  Source = -> Face080
  Symmetric = false
FEATURE [Part::MultiFuse] Fusion053  label="createThreadedInsertHolesForFan"
  Shapes = -> [Revolve081,Revolve082,Revolve083,Revolve084]
FEATURE [Part::Cut] Cut017  label="fanScrewHousing001"
  Base = -> Fusion046
  Tool = -> Fusion053
FEATURE [Part::Feature] Face081
  shape: bbox 3.5 x 17.8 x 2e-07 mm, 1 faces, 0 solids (baked)
FEATURE [Part::Revolution] Revolve085  label="removeToCreateScrewAndThreadedInsertHole022"
  Angle = 360
  Axis = (0,1,0)
  Base = (0,0,0)
  FaceMakerClass = Part::FaceMakerBullseye
  Placement = pos=(62.3,30.3,19.7) rot=(0,0,1;0rad)
  Solid = false
  Source = -> Face081
  Symmetric = false
FEATURE [Part::Feature] Face082
  shape: bbox 3.5 x 17.8 x 2e-07 mm, 1 faces, 0 solids (baked)
FEATURE [Part::Revolution] Revolve086  label="removeToCreateScrewAndThreadedInsertHole023"
  Angle = 360
  Axis = (0,1,0)
  Base = (0,0,0)
  FaceMakerClass = Part::FaceMakerBullseye
  Placement = pos=(62.3,30.3,51.7) rot=(0,0,1;0rad)
  Solid = false
  Source = -> Face082
  Symmetric = false
FEATURE [Part::Feature] Face083
  shape: bbox 3.5 x 17.8 x 2e-07 mm, 1 faces, 0 solids (baked)
FEATURE [Part::Revolution] Revolve087  label="removeToCreateScrewAndThreadedInsertHole024"
  Angle = 360
  Axis = (0,1,0)
  Base = (0,0,0)
  FaceMakerClass = Part::FaceMakerBullseye
  Placement = pos=(30.3,30.3,19.7) rot=(0,0,1;0rad)
  Solid = false
  Source = -> Face083
  Symmetric = false
FEATURE [Part::Feature] Face084
  shape: bbox 3.5 x 17.8 x 2e-07 mm, 1 faces, 0 solids (baked)
FEATURE [Part::Revolution] Revolve088  label="removeToCreateScrewAndThreadedInsertHole025"
  Angle = 360
  Axis = (0,1,0)
  Base = (0,0,0)
  FaceMakerClass = Part::FaceMakerBullseye
  Placement = pos=(30.3,30.3,51.7) rot=(0,0,1;0rad)
  Solid = false
  Source = -> Face084
  Symmetric = false
FEATURE [Part::MultiFuse] Fusion054  label="createThreadedInsertHolesForFan001"
  Shapes = -> [Revolve085,Revolve086,Revolve087,Revolve088]
FEATURE [Part::Cut] Cut018  label="top007"
  Base = -> Fusion040
  Tool = -> Fusion054
FEATURE [Sketcher::SketchObject] Sketch029
  FullyConstrained = false
  Placement = pos=(0,0,0) rot=(1,0,0;1.5708rad)
  sketch-geometry (24):
    g0: ArcOfCircle CenterX=-4 CenterY=-10.5 CenterZ=0 NormalX=0 NormalY=0 NormalZ=1 AngleXU=0 Radius=1.5 StartAngle=6e-16 EndAngle=3.14159
    g1: ArcOfCircle CenterX=-34.2 CenterY=-10.5 CenterZ=0 NormalX=0 NormalY=0 NormalZ=1 AngleXU=0 Radius=1.5 StartAngle=0 EndAngle=3.14159
    g2: ArcOfCircle CenterX=-34.2 CenterY=-27.7 CenterZ=0 NormalX=0 NormalY=0 NormalZ=1 AngleXU=0 Radius=1.5 StartAngle=3.14159 EndAngle=6.28319
    g3: ArcOfCircle CenterX=-4 CenterY=-27.7 CenterZ=0 NormalX=0 NormalY=0 NormalZ=1 AngleXU=0 Radius=1.5 StartAngle=3.1416 EndAngle=6.28319
    g4: ArcOfCircle CenterX=-10 CenterY=-4.3 CenterZ=0 NormalX=0 NormalY=0 NormalZ=1 AngleXU=0 Radius=1.5 StartAngle=2e-16 EndAngle=3.14159
    g5: ArcOfCircle CenterX=-16.1 CenterY=-1.8 CenterZ=0 NormalX=0 NormalY=0 NormalZ=1 AngleXU=0 Radius=1.5 StartAngle=5e-16 EndAngle=3.14159
    g6: ArcOfCircle CenterX=-22.1 CenterY=-1.8 CenterZ=0 NormalX=0 NormalY=0 NormalZ=1 AngleXU=0 Radius=1.5 StartAngle=5e-16 EndAngle=3.14159
    g7: ArcOfCircle CenterX=-28.2 CenterY=-4.3 CenterZ=0 NormalX=0 NormalY=0 NormalZ=1 AngleXU=0 Radius=1.5 StartAngle=2e-16 EndAngle=3.14159
    g8: ArcOfCircle CenterX=-10 CenterY=-33.9 CenterZ=0 NormalX=0 NormalY=0 NormalZ=1 AngleXU=0 Radius=1.5 StartAngle=3.14159 EndAngle=6.28319
    g9: ArcOfCircle CenterX=-16.1 CenterY=-36.4 CenterZ=0 NormalX=0 NormalY=0 NormalZ=1 AngleXU=0 Radius=1.5 StartAngle=3.14159 EndAngle=6.28319
    g10: ArcOfCircle CenterX=-22.1 CenterY=-36.4 CenterZ=0 NormalX=0 NormalY=0 NormalZ=1 AngleXU=0 Radius=1.5 StartAngle=3.14159 EndAngle=6.28319
    g11: ArcOfCircle CenterX=-28.2 CenterY=-33.9 CenterZ=0 NormalX=0 NormalY=0 NormalZ=1 AngleXU=0 Radius=1.5 StartAngle=3.14159 EndAngle=6.28319
    g12: LineSegment StartX=-35.7 StartY=-10.5 StartZ=0 EndX=-35.7 EndY=-27.7 EndZ=0
    g13: LineSegment StartX=-32.7 StartY=-10.5 StartZ=0 EndX=-32.7 EndY=-27.7 EndZ=0
    g14: LineSegment StartX=-29.7 StartY=-33.9 StartZ=0 EndX=-29.7 EndY=-4.3 EndZ=0
    g15: LineSegment StartX=-26.7 StartY=-33.9 StartZ=0 EndX=-26.7 EndY=-4.3 EndZ=0
    g16: LineSegment StartX=-2.5 StartY=-10.5 StartZ=0 EndX=-2.5 EndY=-27.7 EndZ=0
    g17: LineSegment StartX=-8.5 StartY=-4.3 StartZ=0 EndX=-8.5 EndY=-33.9 EndZ=0
    g18: LineSegment StartX=-5.5 StartY=-10.5 StartZ=0 EndX=-5.5 EndY=-27.7 EndZ=0
    g19: LineSegment StartX=-11.5 StartY=-4.3 StartZ=0 EndX=-11.5 EndY=-33.9 EndZ=0
    g20: LineSegment StartX=-14.6 StartY=-1.8 StartZ=0 EndX=-14.6 EndY=-36.4 EndZ=0
    g21: LineSegment StartX=-17.6 StartY=-1.8 StartZ=0 EndX=-17.6 EndY=-36.4 EndZ=0
    g22: LineSegment StartX=-20.6 StartY=-36.4 StartZ=0 EndX=-20.6 EndY=-1.8 EndZ=0
    g23: LineSegment StartX=-23.6 StartY=-1.8 StartZ=0 EndX=-23.6 EndY=-36.4 EndZ=0
  constraints (48):
    c: Block(g0)
    c: Block(g1)
    c: Block(g2)
    c: Block(g3)
    c: Block(g4)
    c: Block(g5)
    c: Block(g6)
    c: Block(g7)
    c: Block(g8)
    c: Block(g9)
    c: Block(g10)
    c: Block(g11)
    c: Coincident(g12,g1)
    c: Coincident(g12,g2)
    c: Vertical(g12)
    c: Coincident(g13,g1)
    c: Coincident(g13,g2)
    c: Vertical(g13)
    c: Coincident(g14,g11)
    c: Coincident(g14,g7)
    c: Vertical(g14)
    c: Coincident(g15,g11)
    c: Coincident(g15,g7)
    c: Vertical(g15)
    c: Coincident(g16,g0)
    c: Coincident(g16,g3)
    c: Vertical(g16)
    c: Coincident(g17,g4)
    c: Coincident(g17,g8)
    c: Vertical(g17)
    c: Coincident(g18,g0)
    c: Coincident(g18,g3)
    c: Vertical(g18)
    c: Coincident(g19,g4)
    c: Coincident(g19,g8)
    c: Vertical(g19)
    c: Coincident(g20,g5)
    c: Coincident(g20,g9)
    c: Vertical(g20)
    c: Coincident(g21,g5)
    c: Coincident(g21,g9)
    c: Vertical(g21)
    c: Coincident(g22,g10)
    c: Coincident(g22,g6)
    c: Vertical(g22)
    c: Coincident(g23,g6)
    c: Coincident(g23,g10)
    c: Vertical(g23)
FEATURE [Part::Extrusion] Extrude020  label="removeToCreateFanGrillHoles"
  Base = -> Sketch029
  Dir = (0,-1,6e-16)
  DirMode = 2
  FaceMakerClass = Part::FaceMakerBullseye
  LengthFwd = 10
  LengthRev = 0
  Placement = pos=(65.4,44,54.82) rot=(0,0,1;0rad)
  Solid = true
  Symmetric = false
FEATURE [Part::MultiFuse] Fusion055  label="top008"
  Shapes = -> [Cut017,Cut018]
FEATURE [Part::Cut] Cut019  label="top009"
  Base = -> Fusion055
  Tool = -> Extrude020
FEATURE [App::MeasureDistance] Distance003  label="Distance: 71.95 mm"
  Distance = 71.9513
  P1 = (117,38,72)
  P2 = (117,38,0.0487319)
FEATURE [Sketcher::SketchObject] Sketch030
  FullyConstrained = true
  Placement = pos=(117,19,0) rot=(0.57735,0.57735,0.57735;2.0944rad)
  sketch-geometry (48):
    g0: LineSegment StartX=-49.19 StartY=69.25 StartZ=0 EndX=-49.19 EndY=66.25 EndZ=0
    g1: LineSegment StartX=-49.19 StartY=63.5 StartZ=0 EndX=-49.19 EndY=60.5 EndZ=0
    g2: LineSegment StartX=-49.19 StartY=57.75 StartZ=0 EndX=-49.19 EndY=54.75 EndZ=0
    g3: LineSegment StartX=-49.19 StartY=52 StartZ=0 EndX=-49.19 EndY=49 EndZ=0
    g4: LineSegment StartX=-49.19 StartY=46.25 StartZ=0 EndX=-49.19 EndY=43.25 EndZ=0
    g5: LineSegment StartX=-49.19 StartY=40.5 StartZ=0 EndX=-49.19 EndY=37.5 EndZ=0
    g6: LineSegment StartX=-49.19 StartY=34.5 StartZ=0 EndX=-49.19 EndY=31.5 EndZ=0
    g7: LineSegment StartX=-49.19 StartY=28.75 StartZ=0 EndX=-49.19 EndY=25.75 EndZ=0
    g8: LineSegment StartX=-49.19 StartY=23 StartZ=0 EndX=-49.19 EndY=20 EndZ=0
    g9: LineSegment StartX=-49.19 StartY=17.25 StartZ=0 EndX=-49.19 EndY=14.25 EndZ=0
    g10: LineSegment StartX=-49.19 StartY=11.5 StartZ=0 EndX=-49.19 EndY=8.5 EndZ=0
    g11: LineSegment StartX=-49.19 StartY=5.75 StartZ=0 EndX=-49.19 EndY=2.75 EndZ=0
    g12: ArcOfCircle CenterX=-1.5 CenterY=67.75 CenterZ=0 NormalX=0 NormalY=0 NormalZ=1 AngleXU=0 Radius=1.5 StartAngle=4.71239 EndAngle=7.85398
    g13: ArcOfCircle CenterX=-1.5 CenterY=62 CenterZ=0 NormalX=0 NormalY=0 NormalZ=1 AngleXU=0 Radius=1.5 StartAngle=4.71239 EndAngle=7.85398
    g14: ArcOfCircle CenterX=-1.5 CenterY=56.25 CenterZ=0 NormalX=0 NormalY=0 NormalZ=1 AngleXU=0 Radius=1.5 StartAngle=4.71239 EndAngle=7.85398
    g15: ArcOfCircle CenterX=-11.49 CenterY=50.5 CenterZ=0 NormalX=0 NormalY=0 NormalZ=1 AngleXU=0 Radius=1.5 StartAngle=4.71239 EndAngle=7.85398
    g16: ArcOfCircle CenterX=-16.28 CenterY=44.75 CenterZ=0 NormalX=0 NormalY=0 NormalZ=1 AngleXU=0 Radius=1.5 StartAngle=4.71239 EndAngle=7.85398
    g17: ArcOfCircle CenterX=-18.2337 CenterY=39 CenterZ=0 NormalX=0 NormalY=0 NormalZ=1 AngleXU=0 Radius=1.5 StartAngle=4.71485 EndAngle=7.85398
    g18: ArcOfCircle CenterX=-16.2837 CenterY=27.25 CenterZ=0 NormalX=0 NormalY=0 NormalZ=1 AngleXU=0 Radius=1.5 StartAngle=4.71485 EndAngle=7.85398
    g19: ArcOfCircle CenterX=-18.2337 CenterY=33 CenterZ=0 NormalX=0 NormalY=0 NormalZ=1 AngleXU=0 Radius=1.5 StartAngle=4.71485 EndAngle=7.85398
    g20: ArcOfCircle CenterX=-11.49 CenterY=21.5 CenterZ=0 NormalX=0 NormalY=0 NormalZ=1 AngleXU=0 Radius=1.5 StartAngle=4.71239 EndAngle=7.85398
    g21: ArcOfCircle CenterX=-1.5 CenterY=4.25 CenterZ=0 NormalX=0 NormalY=0 NormalZ=1 AngleXU=0 Radius=1.5 StartAngle=4.71239 EndAngle=7.85398
    g22: ArcOfCircle CenterX=-1.5 CenterY=10 CenterZ=0 NormalX=0 NormalY=0 NormalZ=1 AngleXU=0 Radius=1.5 StartAngle=4.71239 EndAngle=7.85398
    g23: ArcOfCircle CenterX=-1.5 CenterY=15.75 CenterZ=0 NormalX=0 NormalY=0 NormalZ=1 AngleXU=0 Radius=1.5 StartAngle=4.71239 EndAngle=7.85398
    g24: LineSegment StartX=-49.19 StartY=69.25 StartZ=0 EndX=-1.5 EndY=69.25 EndZ=0
    g25: LineSegment StartX=-49.19 StartY=66.25 StartZ=0 EndX=-1.5 EndY=66.25 EndZ=0
    g26: LineSegment StartX=-49.19 StartY=63.5 StartZ=0 EndX=-1.5 EndY=63.5 EndZ=0
    g27: LineSegment StartX=-49.19 StartY=60.5 StartZ=0 EndX=-1.5 EndY=60.5 EndZ=0
    g28: LineSegment StartX=-49.19 StartY=57.75 StartZ=0 EndX=-1.5 EndY=57.75 EndZ=0
    g29: LineSegment StartX=-49.19 StartY=54.75 StartZ=0 EndX=-1.5 EndY=54.75 EndZ=0
    g30: LineSegment StartX=-49.19 StartY=52 StartZ=0 EndX=-11.49 EndY=52 EndZ=0
    g31: LineSegment StartX=-49.19 StartY=49 StartZ=0 EndX=-11.49 EndY=49 EndZ=0
    g32: LineSegment StartX=-49.19 StartY=46.25 StartZ=0 EndX=-16.28 EndY=46.25 EndZ=0
    g33: LineSegment StartX=-49.19 StartY=43.25 StartZ=0 EndX=-16.28 EndY=43.25 EndZ=0
    g34: LineSegment StartX=-49.19 StartY=40.5 StartZ=0 EndX=-18.2337 EndY=40.5 EndZ=0
    g35: LineSegment StartX=-49.19 StartY=37.5 StartZ=0 EndX=-18.23 EndY=37.5 EndZ=0
    g36: LineSegment StartX=-49.19 StartY=34.5 StartZ=0 EndX=-18.2337 EndY=34.5 EndZ=0
    g37: LineSegment StartX=-49.19 StartY=31.5 StartZ=0 EndX=-18.23 EndY=31.5 EndZ=0
    g38: LineSegment StartX=-49.19 StartY=28.75 StartZ=0 EndX=-16.2837 EndY=28.75 EndZ=0
    g39: LineSegment StartX=-49.19 StartY=25.75 StartZ=0 EndX=-16.28 EndY=25.75 EndZ=0
    g40: LineSegment StartX=-49.19 StartY=23 StartZ=0 EndX=-11.49 EndY=23 EndZ=0
    g41: LineSegment StartX=-49.19 StartY=20 StartZ=0 EndX=-11.49 EndY=20 EndZ=0
    g42: LineSegment StartX=-49.19 StartY=17.25 StartZ=0 EndX=-1.5 EndY=17.25 EndZ=0
    g43: LineSegment StartX=-49.19 StartY=14.25 StartZ=0 EndX=-1.5 EndY=14.25 EndZ=0
    g44: LineSegment StartX=-49.19 StartY=11.5 StartZ=0 EndX=-1.5 EndY=11.5 EndZ=0
    g45: LineSegment StartX=-49.19 StartY=8.5 StartZ=0 EndX=-1.5 EndY=8.5 EndZ=0
    g46: LineSegment StartX=-49.19 StartY=5.75 StartZ=0 EndX=-1.5 EndY=5.75 EndZ=0
    g47: LineSegment StartX=-49.19 StartY=2.75 StartZ=0 EndX=-1.5 EndY=2.75 EndZ=0
  constraints (120):
    c: Vertical(g0)
    c: Distance(g0) = 3
    c: Block(g0)
    c: Vertical(g1)
    c: Distance(g1) = 3
    c: Vertical(g2)
    c: Equal(g0,g2) = 3
    c: Block(g2)
    c: Vertical(g3)
    c: Equal(g1,g3) = 3
    c: Vertical(g4)
    c: Equal(g0,g4) = 3
    c: Block(g4)
    c: Vertical(g5)
    c: Equal(g1,g5) = 3
    c: Vertical(g6)
    c: Equal(g0,g6) = 3
    c: Block(g6)
    c: Vertical(g7)
    c: Equal(g1,g7) = 3
    c: Vertical(g8)
    c: Equal(g0,g8) = 3
    c: Block(g8)
    c: Vertical(g9)
    c: Equal(g1,g9) = 3
    c: Vertical(g10)
    c: Equal(g0,g10) = 3
    c: Block(g10)
    c: Vertical(g11)
    c: Equal(g1,g11) = 3
    c: Block(g12)
    c: Block(g13)
    c: Block(g14)
    c: Block(g15)
    c: Block(g16)
    c: Block(g17)
    c: Block(g18)
    c: Block(g19)
    c: Block(g20)
    c: Block(g21)
    c: Block(g22)
    c: Block(g23)
    c: Block(g11)
    c: Block(g9)
    c: Block(g7)
    c: Block(g5)
    c: Block(g3)
    c: Block(g1)
    c: Coincident(g24,g0)
    c: Coincident(g24,g12)
    c: Horizontal(g24)
    c: Coincident(g25,g0)
    c: Coincident(g25,g12)
    c: Horizontal(g25)
    c: Coincident(g26,g1)
    c: Coincident(g26,g13)
    c: Horizontal(g26)
    c: Coincident(g27,g1)
    c: Coincident(g27,g13)
    c: Horizontal(g27)
    c: Coincident(g28,g2)
    c: Coincident(g28,g14)
    c: Horizontal(g28)
    c: Coincident(g29,g2)
    c: Coincident(g29,g14)
    c: Horizontal(g29)
    c: Coincident(g30,g3)
    c: Coincident(g30,g15)
    c: Horizontal(g30)
    c: Coincident(g31,g3)
    c: Coincident(g31,g15)
    c: Horizontal(g31)
    c: Coincident(g32,g4)
    c: Coincident(g32,g16)
    c: Horizontal(g32)
    c: Coincident(g33,g4)
    c: Coincident(g33,g16)
    c: Horizontal(g33)
    c: Coincident(g34,g5)
    c: Coincident(g34,g17)
    c: Horizontal(g34)
    c: Coincident(g35,g5)
    c: Coincident(g35,g17)
    c: Horizontal(g35)
    c: Coincident(g36,g6)
    c: Coincident(g36,g19)
    c: Horizontal(g36)
    c: Coincident(g37,g6)
    c: Coincident(g37,g19)
    c: Horizontal(g37)
    c: Coincident(g38,g7)
    c: Coincident(g38,g18)
    c: Horizontal(g38)
    c: Coincident(g39,g7)
    c: Coincident(g39,g18)
    c: Horizontal(g39)
    c: Coincident(g40,g8)
    c: Coincident(g40,g20)
    c: Horizontal(g40)
    c: Coincident(g41,g8)
    c: Coincident(g41,g20)
    c: Horizontal(g41)
    c: Coincident(g42,g9)
    c: Coincident(g42,g23)
    c: Horizontal(g42)
    c: Coincident(g43,g9)
    c: Coincident(g43,g23)
    c: Horizontal(g43)
    c: Coincident(g44,g10)
    c: Coincident(g44,g22)
    c: Horizontal(g44)
    c: Coincident(g45,g10)
    c: Coincident(g45,g22)
    c: Horizontal(g45)
    c: Coincident(g46,g11)
    c: Coincident(g46,g21)
    c: Horizontal(g46)
    c: Coincident(g47,g11)
    c: Coincident(g47,g21)
    c: Horizontal(g47)
FEATURE [Sketcher::SketchObject] Sketch031
  FullyConstrained = true
  Placement = pos=(117,19,0) rot=(0.57735,0.57735,0.57735;2.0944rad)
  sketch-geometry (24):
    g0: ArcOfCircle CenterX=-49.19 CenterY=67.75 CenterZ=0 NormalX=0 NormalY=0 NormalZ=1 AngleXU=0 Radius=1.5 StartAngle=1.5708 EndAngle=4.71239
    g1: ArcOfCircle CenterX=-49.19 CenterY=62 CenterZ=0 NormalX=0 NormalY=0 NormalZ=1 AngleXU=0 Radius=1.5 StartAngle=1.5708 EndAngle=4.71239
    g2: ArcOfCircle CenterX=-49.19 CenterY=56.25 CenterZ=0 NormalX=0 NormalY=0 NormalZ=1 AngleXU=0 Radius=1.5 StartAngle=1.5708 EndAngle=4.71239
    g3: ArcOfCircle CenterX=-49.19 CenterY=50.5 CenterZ=0 NormalX=0 NormalY=0 NormalZ=1 AngleXU=0 Radius=1.5 StartAngle=1.5708 EndAngle=4.71239
    g4: ArcOfCircle CenterX=-49.19 CenterY=44.75 CenterZ=0 NormalX=0 NormalY=0 NormalZ=1 AngleXU=0 Radius=1.5 StartAngle=1.5708 EndAngle=4.71239
    g5: ArcOfCircle CenterX=-49.19 CenterY=39 CenterZ=0 NormalX=0 NormalY=0 NormalZ=1 AngleXU=0 Radius=1.5 StartAngle=1.5708 EndAngle=4.71239
    g6: ArcOfCircle CenterX=-49.19 CenterY=33 CenterZ=0 NormalX=0 NormalY=0 NormalZ=1 AngleXU=0 Radius=1.5 StartAngle=1.5708 EndAngle=4.71239
    g7: ArcOfCircle CenterX=-49.19 CenterY=27.25 CenterZ=0 NormalX=0 NormalY=0 NormalZ=1 AngleXU=0 Radius=1.5 StartAngle=1.5708 EndAngle=4.71239
    g8: ArcOfCircle CenterX=-49.19 CenterY=21.5 CenterZ=0 NormalX=0 NormalY=0 NormalZ=1 AngleXU=0 Radius=1.5 StartAngle=1.5708 EndAngle=4.71239
    g9: ArcOfCircle CenterX=-49.19 CenterY=15.75 CenterZ=0 NormalX=0 NormalY=0 NormalZ=1 AngleXU=0 Radius=1.5 StartAngle=1.5708 EndAngle=4.71239
    g10: ArcOfCircle CenterX=-49.19 CenterY=10 CenterZ=0 NormalX=0 NormalY=0 NormalZ=1 AngleXU=0 Radius=1.5 StartAngle=1.5708 EndAngle=4.71239
    g11: ArcOfCircle CenterX=-49.19 CenterY=4.25 CenterZ=0 NormalX=0 NormalY=0 NormalZ=1 AngleXU=0 Radius=1.5 StartAngle=1.5708 EndAngle=4.71239
    g12: LineSegment StartX=-49.19 StartY=69.25 StartZ=0 EndX=-49.19 EndY=66.25 EndZ=0
    g13: LineSegment StartX=-49.19 StartY=63.5 StartZ=0 EndX=-49.19 EndY=60.5 EndZ=0
    g14: LineSegment StartX=-49.19 StartY=57.75 StartZ=0 EndX=-49.19 EndY=54.75 EndZ=0
    g15: LineSegment StartX=-49.19 StartY=52 StartZ=0 EndX=-49.19 EndY=49 EndZ=0
    g16: LineSegment StartX=-49.19 StartY=46.25 StartZ=0 EndX=-49.19 EndY=43.25 EndZ=0
    g17: LineSegment StartX=-49.19 StartY=40.5 StartZ=0 EndX=-49.19 EndY=37.5 EndZ=0
    g18: LineSegment StartX=-49.19 StartY=34.5 StartZ=0 EndX=-49.19 EndY=31.5 EndZ=0
    g19: LineSegment StartX=-49.19 StartY=28.75 StartZ=0 EndX=-49.19 EndY=25.75 EndZ=0
    g20: LineSegment StartX=-49.19 StartY=23 StartZ=0 EndX=-49.19 EndY=20 EndZ=0
    g21: LineSegment StartX=-49.19 StartY=17.25 StartZ=0 EndX=-49.19 EndY=14.25 EndZ=0
    g22: LineSegment StartX=-49.19 StartY=11.5 StartZ=0 EndX=-49.19 EndY=8.5 EndZ=0
    g23: LineSegment StartX=-49.19 StartY=5.75 StartZ=0 EndX=-49.19 EndY=2.75 EndZ=0
  constraints (48):
    c: Block(g0)
    c: Block(g1)
    c: Block(g2)
    c: Block(g3)
    c: Block(g4)
    c: Block(g5)
    c: Block(g6)
    c: Block(g7)
    c: Block(g8)
    c: Block(g9)
    c: Block(g10)
    c: Block(g11)
    c: Coincident(g12,g0)
    c: Coincident(g12,g0)
    c: Vertical(g12)
    c: Vertical(g13)
    c: Coincident(g13,g1)
    c: Vertical(g14)
    c: Coincident(g14,g2)
    c: Vertical(g15)
    c: Coincident(g15,g3)
    c: Vertical(g16)
    c: Coincident(g16,g4)
    c: Vertical(g17)
    c: Coincident(g17,g5)
    c: Vertical(g18)
    c: Coincident(g18,g6)
    c: Vertical(g19)
    c: Coincident(g19,g7)
    c: Vertical(g20)
    c: Coincident(g20,g8)
    c: Vertical(g21)
    c: Coincident(g21,g9)
    c: Vertical(g22)
    c: Coincident(g22,g10)
    c: Vertical(g23)
    c: Coincident(g23,g11)
    c: Block(g23)
    c: Block(g22)
    c: Block(g21)
    c: Block(g20)
    c: Block(g13)
    c: Block(g14)
    c: Block(g15)
    c: Block(g16)
    c: Block(g17)
    c: Block(g18)
    c: Block(g19)
FEATURE [Part::Extrusion] Extrude022
  Base = -> Sketch030
  Dir = (1,-2e-16,2e-16)
  DirMode = 2
  FaceMakerClass = Part::FaceMakerBullseye
  LengthFwd = 19
  LengthRev = 0
  Placement = pos=(-19,0,0) rot=(0,0,1;0rad)
  Solid = true
  Symmetric = false
FEATURE [Part::Fillet] Fillet022
  Base = -> Extrude022
  Edges = 24 edges r=1.49: [Edge6,Edge11,Edge18,Edge23,Edge30,Edge35,Edge42,Edge47,Edge54,Edge59,Edge66,Edge71,Edge78,Edge83,Edge90,Edge95,Edge102,Edge107,Edge114,Edge119,Edge126,Edge131,Edge138,Edge143]
FEATURE [Part::Cut] Cut020  label="top010"
  Base = -> Cut019
  Tool = -> Fillet022
FEATURE [Sketcher::SketchObject] Sketch032
  FullyConstrained = true
  Placement = pos=(117,19,0) rot=(0.57735,0.57735,0.57735;2.0944rad)
  sketch-geometry (48):
    g0: LineSegment StartX=-49.19 StartY=69.25 StartZ=0 EndX=-49.19 EndY=66.25 EndZ=0
    g1: LineSegment StartX=-49.19 StartY=63.5 StartZ=0 EndX=-49.19 EndY=60.5 EndZ=0
    g2: LineSegment StartX=-49.19 StartY=57.75 StartZ=0 EndX=-49.19 EndY=54.75 EndZ=0
    g3: LineSegment StartX=-49.19 StartY=52 StartZ=0 EndX=-49.19 EndY=49 EndZ=0
    g4: LineSegment StartX=-49.19 StartY=46.25 StartZ=0 EndX=-49.19 EndY=43.25 EndZ=0
    g5: LineSegment StartX=-49.19 StartY=40.5 StartZ=0 EndX=-49.19 EndY=37.5 EndZ=0
    g6: LineSegment StartX=-49.19 StartY=34.5 StartZ=0 EndX=-49.19 EndY=31.5 EndZ=0
    g7: LineSegment StartX=-49.19 StartY=28.75 StartZ=0 EndX=-49.19 EndY=25.75 EndZ=0
    g8: LineSegment StartX=-49.19 StartY=23 StartZ=0 EndX=-49.19 EndY=20 EndZ=0
    g9: LineSegment StartX=-49.19 StartY=17.25 StartZ=0 EndX=-49.19 EndY=14.25 EndZ=0
    g10: LineSegment StartX=-49.19 StartY=11.5 StartZ=0 EndX=-49.19 EndY=8.5 EndZ=0
    g11: LineSegment StartX=-49.19 StartY=5.75 StartZ=0 EndX=-49.19 EndY=2.75 EndZ=0
    g12: ArcOfCircle CenterX=-1.5 CenterY=67.75 CenterZ=0 NormalX=0 NormalY=0 NormalZ=1 AngleXU=0 Radius=1.5 StartAngle=4.71239 EndAngle=7.85398
    g13: ArcOfCircle CenterX=-1.5 CenterY=62 CenterZ=0 NormalX=0 NormalY=0 NormalZ=1 AngleXU=0 Radius=1.5 StartAngle=4.71239 EndAngle=7.85398
    g14: ArcOfCircle CenterX=-1.5 CenterY=56.25 CenterZ=0 NormalX=0 NormalY=0 NormalZ=1 AngleXU=0 Radius=1.5 StartAngle=4.71239 EndAngle=7.85398
    g15: ArcOfCircle CenterX=-11.49 CenterY=50.5 CenterZ=0 NormalX=0 NormalY=0 NormalZ=1 AngleXU=0 Radius=1.5 StartAngle=4.71239 EndAngle=7.85398
    g16: ArcOfCircle CenterX=-16.28 CenterY=44.75 CenterZ=0 NormalX=0 NormalY=0 NormalZ=1 AngleXU=0 Radius=1.5 StartAngle=4.71239 EndAngle=7.85398
    g17: ArcOfCircle CenterX=-18.2337 CenterY=39 CenterZ=0 NormalX=0 NormalY=0 NormalZ=1 AngleXU=0 Radius=1.5 StartAngle=4.71485 EndAngle=7.85398
    g18: ArcOfCircle CenterX=-16.2837 CenterY=27.25 CenterZ=0 NormalX=0 NormalY=0 NormalZ=1 AngleXU=0 Radius=1.5 StartAngle=4.71485 EndAngle=7.85398
    g19: ArcOfCircle CenterX=-18.2337 CenterY=33 CenterZ=0 NormalX=0 NormalY=0 NormalZ=1 AngleXU=0 Radius=1.5 StartAngle=4.71485 EndAngle=7.85398
    g20: ArcOfCircle CenterX=-11.49 CenterY=21.5 CenterZ=0 NormalX=0 NormalY=0 NormalZ=1 AngleXU=0 Radius=1.5 StartAngle=4.71239 EndAngle=7.85398
    g21: ArcOfCircle CenterX=-1.5 CenterY=4.25 CenterZ=0 NormalX=0 NormalY=0 NormalZ=1 AngleXU=0 Radius=1.5 StartAngle=4.71239 EndAngle=7.85398
    g22: ArcOfCircle CenterX=-1.5 CenterY=10 CenterZ=0 NormalX=0 NormalY=0 NormalZ=1 AngleXU=0 Radius=1.5 StartAngle=4.71239 EndAngle=7.85398
    g23: ArcOfCircle CenterX=-1.5 CenterY=15.75 CenterZ=0 NormalX=0 NormalY=0 NormalZ=1 AngleXU=0 Radius=1.5 StartAngle=4.71239 EndAngle=7.85398
    g24: LineSegment StartX=-49.19 StartY=69.25 StartZ=0 EndX=-1.5 EndY=69.25 EndZ=0
    g25: LineSegment StartX=-49.19 StartY=66.25 StartZ=0 EndX=-1.5 EndY=66.25 EndZ=0
    g26: LineSegment StartX=-49.19 StartY=63.5 StartZ=0 EndX=-1.5 EndY=63.5 EndZ=0
    g27: LineSegment StartX=-49.19 StartY=60.5 StartZ=0 EndX=-1.5 EndY=60.5 EndZ=0
    g28: LineSegment StartX=-49.19 StartY=57.75 StartZ=0 EndX=-1.5 EndY=57.75 EndZ=0
    g29: LineSegment StartX=-49.19 StartY=54.75 StartZ=0 EndX=-1.5 EndY=54.75 EndZ=0
    g30: LineSegment StartX=-49.19 StartY=52 StartZ=0 EndX=-11.49 EndY=52 EndZ=0
    g31: LineSegment StartX=-49.19 StartY=49 StartZ=0 EndX=-11.49 EndY=49 EndZ=0
    g32: LineSegment StartX=-49.19 StartY=46.25 StartZ=0 EndX=-16.28 EndY=46.25 EndZ=0
    g33: LineSegment StartX=-49.19 StartY=43.25 StartZ=0 EndX=-16.28 EndY=43.25 EndZ=0
    g34: LineSegment StartX=-49.19 StartY=40.5 StartZ=0 EndX=-18.2337 EndY=40.5 EndZ=0
    g35: LineSegment StartX=-49.19 StartY=37.5 StartZ=0 EndX=-18.23 EndY=37.5 EndZ=0
    g36: LineSegment StartX=-49.19 StartY=34.5 StartZ=0 EndX=-18.2337 EndY=34.5 EndZ=0
    g37: LineSegment StartX=-49.19 StartY=31.5 StartZ=0 EndX=-18.23 EndY=31.5 EndZ=0
    g38: LineSegment StartX=-49.19 StartY=28.75 StartZ=0 EndX=-16.2837 EndY=28.75 EndZ=0
    g39: LineSegment StartX=-49.19 StartY=25.75 StartZ=0 EndX=-16.28 EndY=25.75 EndZ=0
    g40: LineSegment StartX=-49.19 StartY=23 StartZ=0 EndX=-11.49 EndY=23 EndZ=0
    g41: LineSegment StartX=-49.19 StartY=20 StartZ=0 EndX=-11.49 EndY=20 EndZ=0
    g42: LineSegment StartX=-49.19 StartY=17.25 StartZ=0 EndX=-1.5 EndY=17.25 EndZ=0
    g43: LineSegment StartX=-49.19 StartY=14.25 StartZ=0 EndX=-1.5 EndY=14.25 EndZ=0
    g44: LineSegment StartX=-49.19 StartY=11.5 StartZ=0 EndX=-1.5 EndY=11.5 EndZ=0
    g45: LineSegment StartX=-49.19 StartY=8.5 StartZ=0 EndX=-1.5 EndY=8.5 EndZ=0
    g46: LineSegment StartX=-49.19 StartY=5.75 StartZ=0 EndX=-1.5 EndY=5.75 EndZ=0
    g47: LineSegment StartX=-49.19 StartY=2.75 StartZ=0 EndX=-1.5 EndY=2.75 EndZ=0
  constraints (120):
    c: Vertical(g0)
    c: Distance(g0) = 3
    c: Block(g0)
    c: Vertical(g1)
    c: Distance(g1) = 3
    c: Vertical(g2)
    c: Equal(g0,g2) = 3
    c: Block(g2)
    c: Vertical(g3)
    c: Equal(g1,g3) = 3
    c: Vertical(g4)
    c: Equal(g0,g4) = 3
    c: Block(g4)
    c: Vertical(g5)
    c: Equal(g1,g5) = 3
    c: Vertical(g6)
    c: Equal(g0,g6) = 3
    c: Block(g6)
    c: Vertical(g7)
    c: Equal(g1,g7) = 3
    c: Vertical(g8)
    c: Equal(g0,g8) = 3
    c: Block(g8)
    c: Vertical(g9)
    c: Equal(g1,g9) = 3
    c: Vertical(g10)
    c: Equal(g0,g10) = 3
    c: Block(g10)
    c: Vertical(g11)
    c: Equal(g1,g11) = 3
    c: Block(g12)
    c: Block(g13)
    c: Block(g14)
    c: Block(g15)
    c: Block(g16)
    c: Block(g17)
    c: Block(g18)
    c: Block(g19)
    c: Block(g20)
    c: Block(g21)
    c: Block(g22)
    c: Block(g23)
    c: Block(g11)
    c: Block(g9)
    c: Block(g7)
    c: Block(g5)
    c: Block(g3)
    c: Block(g1)
    c: Coincident(g24,g0)
    c: Coincident(g24,g12)
    c: Horizontal(g24)
    c: Coincident(g25,g0)
    c: Coincident(g25,g12)
    c: Horizontal(g25)
    c: Coincident(g26,g1)
    c: Coincident(g26,g13)
    c: Horizontal(g26)
    c: Coincident(g27,g1)
    c: Coincident(g27,g13)
    c: Horizontal(g27)
    c: Coincident(g28,g2)
    c: Coincident(g28,g14)
    c: Horizontal(g28)
    c: Coincident(g29,g2)
    c: Coincident(g29,g14)
    c: Horizontal(g29)
    c: Coincident(g30,g3)
    c: Coincident(g30,g15)
    c: Horizontal(g30)
    c: Coincident(g31,g3)
    c: Coincident(g31,g15)
    c: Horizontal(g31)
    c: Coincident(g32,g4)
    c: Coincident(g32,g16)
    c: Horizontal(g32)
    c: Coincident(g33,g4)
    c: Coincident(g33,g16)
    c: Horizontal(g33)
    c: Coincident(g34,g5)
    c: Coincident(g34,g17)
    c: Horizontal(g34)
    c: Coincident(g35,g5)
    c: Coincident(g35,g17)
    c: Horizontal(g35)
    c: Coincident(g36,g6)
    c: Coincident(g36,g19)
    c: Horizontal(g36)
    c: Coincident(g37,g6)
    c: Coincident(g37,g19)
    c: Horizontal(g37)
    c: Coincident(g38,g7)
    c: Coincident(g38,g18)
    c: Horizontal(g38)
    c: Coincident(g39,g7)
    c: Coincident(g39,g18)
    c: Horizontal(g39)
    c: Coincident(g40,g8)
    c: Coincident(g40,g20)
    c: Horizontal(g40)
    c: Coincident(g41,g8)
    c: Coincident(g41,g20)
    c: Horizontal(g41)
    c: Coincident(g42,g9)
    c: Coincident(g42,g23)
    c: Horizontal(g42)
    c: Coincident(g43,g9)
    c: Coincident(g43,g23)
    c: Horizontal(g43)
    c: Coincident(g44,g10)
    c: Coincident(g44,g22)
    c: Horizontal(g44)
    c: Coincident(g45,g10)
    c: Coincident(g45,g22)
    c: Horizontal(g45)
    c: Coincident(g46,g11)
    c: Coincident(g46,g21)
    c: Horizontal(g46)
    c: Coincident(g47,g11)
    c: Coincident(g47,g21)
    c: Horizontal(g47)
FEATURE [Part::Extrusion] Extrude023
  Base = -> Sketch032
  Dir = (1,-2e-16,2e-16)
  DirMode = 2
  FaceMakerClass = Part::FaceMakerBullseye
  LengthFwd = 19
  LengthRev = 0
  Placement = pos=(-19,0,0) rot=(0,0,1;0rad)
  Solid = true
  Symmetric = false
FEATURE [Part::Fillet] Fillet023
  Base = -> Extrude023
  Edges = <same value as first occurrence — deduplicated (x6 in doc)>
  Placement = pos=(0,0.05,0) rot=(0,0,1;0rad)
FEATURE [Part::Cut] Cut014  label="bottom003"
  Base = -> Cut007
  Tool = -> Fusion047
FEATURE [Part::Cut] Cut021  label="bottom004"
  Base = -> Cut014
  Tool = -> Fillet023
FEATURE [Sketcher::SketchObject] Sketch033
  FullyConstrained = true
  Placement = pos=(117,19,0) rot=(0.57735,0.57735,0.57735;2.0944rad)
  sketch-geometry (8):
    g0: LineSegment StartX=-49.19 StartY=69.25 StartZ=0 EndX=-49.19 EndY=66.25 EndZ=0
    g1: LineSegment StartX=-49.19 StartY=5.75 StartZ=0 EndX=-49.19 EndY=2.75 EndZ=0
    g2: ArcOfCircle CenterX=-1.5 CenterY=67.75 CenterZ=0 NormalX=0 NormalY=0 NormalZ=1 AngleXU=0 Radius=1.5 StartAngle=4.71239 EndAngle=7.85398
    g3: ArcOfCircle CenterX=-1.5 CenterY=4.25 CenterZ=0 NormalX=0 NormalY=0 NormalZ=1 AngleXU=0 Radius=1.5 StartAngle=4.71239 EndAngle=7.85398
    g4: LineSegment StartX=-49.19 StartY=69.25 StartZ=0 EndX=-1.5 EndY=69.25 EndZ=0
    g5: LineSegment StartX=-49.19 StartY=66.25 StartZ=0 EndX=-1.5 EndY=66.25 EndZ=0
    g6: LineSegment StartX=-49.19 StartY=5.75 StartZ=0 EndX=-1.5 EndY=5.75 EndZ=0
    g7: LineSegment StartX=-49.19 StartY=2.75 StartZ=0 EndX=-1.5 EndY=2.75 EndZ=0
  constraints (19):
    c: Vertical(g0)
    c: Distance(g0) = 3
    c: Block(g0)
    c: Vertical(g1)
    c: Block(g2)
    c: Block(g3)
    c: Block(g1)
    c: Coincident(g4,g0)
    c: Coincident(g4,g2)
    c: Horizontal(g4)
    c: Coincident(g5,g0)
    c: Coincident(g5,g2)
    c: Horizontal(g5)
    c: Coincident(g6,g1)
    c: Coincident(g6,g3)
    c: Horizontal(g6)
    c: Coincident(g7,g1)
    c: Coincident(g7,g3)
    c: Horizontal(g7)
FEATURE [Sketcher::SketchObject] Sketch034
  FullyConstrained = true
  Placement = pos=(117,19,0) rot=(0.57735,0.57735,0.57735;2.0944rad)
  sketch-geometry (8):
    g0: LineSegment StartX=-49.19 StartY=63.5 StartZ=0 EndX=-49.19 EndY=60.5 EndZ=0
    g1: LineSegment StartX=-49.19 StartY=11.5 StartZ=0 EndX=-49.19 EndY=8.5 EndZ=0
    g2: ArcOfCircle CenterX=-1.5 CenterY=62 CenterZ=0 NormalX=0 NormalY=0 NormalZ=1 AngleXU=0 Radius=1.5 StartAngle=4.71239 EndAngle=7.85398
    g3: ArcOfCircle CenterX=-1.5 CenterY=10 CenterZ=0 NormalX=0 NormalY=0 NormalZ=1 AngleXU=0 Radius=1.5 StartAngle=4.71239 EndAngle=7.85398
    g4: LineSegment StartX=-49.19 StartY=63.5 StartZ=0 EndX=-1.5 EndY=63.5 EndZ=0
    g5: LineSegment StartX=-49.19 StartY=60.5 StartZ=0 EndX=-1.5 EndY=60.5 EndZ=0
    g6: LineSegment StartX=-49.19 StartY=11.5 StartZ=0 EndX=-1.5 EndY=11.5 EndZ=0
    g7: LineSegment StartX=-49.19 StartY=8.5 StartZ=0 EndX=-1.5 EndY=8.5 EndZ=0
  constraints (19):
    c: Vertical(g0)
    c: Distance(g0) = 3
    c: Vertical(g1)
    c: Block(g1)
    c: Block(g2)
    c: Block(g3)
    c: Block(g0)
    c: Coincident(g4,g0)
    c: Coincident(g4,g2)
    c: Horizontal(g4)
    c: Coincident(g5,g0)
    c: Coincident(g5,g2)
    c: Horizontal(g5)
    c: Coincident(g6,g1)
    c: Coincident(g6,g3)
    c: Horizontal(g6)
    c: Coincident(g7,g1)
    c: Coincident(g7,g3)
    c: Horizontal(g7)
FEATURE [Part::Extrusion] Extrude024
  Base = -> Sketch033
  Dir = (1,0,0)
  DirMode = 2
  FaceMakerClass = Part::FaceMakerBullseye
  LengthFwd = 10
  LengthRev = 0
  Solid = true
  Symmetric = false
FEATURE [Part::Extrusion] Extrude025
  Base = -> Sketch034
  Dir = (1,0,0)
  DirMode = 2
  FaceMakerClass = Part::FaceMakerBullseye
  LengthFwd = 10
  LengthRev = 0
  Solid = true
  Symmetric = false
FEATURE [Part::Fillet] Fillet024  label="removeFromtMoreFrontCaseScrewRetainers"
  Base = -> Extrude024
  Edges = 4 edges r=1.49: [Edge6,Edge11,Edge18,Edge23]
  Placement = pos=(-11,0,0) rot=(0,0,1;0rad)
FEATURE [Part::Fillet] Fillet025  label="removeFromtMoreFrontCaseScrewRetainers001"
  Base = -> Extrude025
  Edges = 4 edges r=1.49: [Edge6,Edge11,Edge18,Edge23]
  Placement = pos=(-19,0,0) rot=(0,0,1;0rad)
FEATURE [Part::Cut] Cut022
  Base = -> Cut015
  Tool = -> Fillet025
FEATURE [Part::Cut] Cut023  label="screwRetainers"
  Base = -> Cut022
  Tool = -> Fillet024
FEATURE [Part::MultiFuse] Fusion056  label="bottom005"
  Shapes = -> [Fusion044,Cut021]
FEATURE [Part::MultiFuse] Fusion057  label="casePillars001"
  Shapes = -> [Cut016,Fusion052]
FEATURE [Part::MultiFuse] Fusion058  label="bottom006"
  Shapes = -> [Fusion056,Cut023]
FEATURE [Part::MultiFuse] Fusion059  label="bottom007"
  Shapes = -> [Fusion058,Fillet005]
FEATURE [Part::MultiFuse] Fusion060  label="bottom008"
  Shapes = -> [Fusion059,Fusion]
FEATURE [Part::MultiFuse] Fusion061  label="top011"
  Shapes = -> [Cut006,Cut020]
FEATURE [Part::MultiFuse] Fusion062  label="top012"
  Shapes = -> [Fusion057,Fusion061]
FEATURE [Sketcher::SketchObject] Sketch035  label="topSketch007"
  FullyConstrained = true
  sketch-geometry (6):
    g0: LineSegment StartX=19 StartY=38 StartZ=0 EndX=117 EndY=38 EndZ=0
    g1: ArcOfCircle CenterX=19 CenterY=19 CenterZ=0 NormalX=0 NormalY=0 NormalZ=1 AngleXU=0 Radius=19 StartAngle=1.5708 EndAngle=3.14159
    g2: LineSegment StartX=117 StartY=38 StartZ=0 EndX=117 EndY=19 EndZ=0
    g3: LineSegment StartX=98 StartY=1.0161e-12 StartZ=0 EndX=5.22862e-06 EndY=1.0161e-12 EndZ=0
    g4: LineSegment StartX=5.22862e-06 StartY=19 StartZ=0 EndX=5.22862e-06 EndY=1.0161e-12 EndZ=0
    g5: ArcOfCircle CenterX=98 CenterY=19 CenterZ=0 NormalX=0 NormalY=0 NormalZ=1 AngleXU=0 Radius=19 StartAngle=4.71239 EndAngle=6.28319
  constraints (16):
    c: Horizontal(g0)
    c: Distance(g0) = 98
    c: Coincident(g1,g0)
    c: Block(g1)
    c: Coincident(g2,g0)
    c: Vertical(g2)
    c: Distance(g2) = 19
    c: Horizontal(g3)
    c: Coincident(g4,g1)
    c: Vertical(g4)
    c: Coincident(g3,g4)
    c: Block(g3)
    c: Coincident(g5,g2)
    c: Coincident(g5,g3)
    c: Block(g0)
    c: Block(g5)
FEATURE [Part::Extrusion] Extrude026  label="sideA001"
  Base = -> Sketch035
  Dir = (0,0,1)
  DirMode = 2
  FaceMakerClass = Part::FaceMakerBullseye
  LengthFwd = 3
  LengthRev = 0
  Placement = pos=(0,0,-2.7) rot=(0,0,1;0rad)
  Solid = true
  Symmetric = false
FEATURE [Sketcher::SketchObject] Sketch036  label="topSketch008"
  FullyConstrained = true
  sketch-geometry (6):
    g0: LineSegment StartX=19 StartY=38 StartZ=0 EndX=117 EndY=38 EndZ=0
    g1: ArcOfCircle CenterX=19 CenterY=19 CenterZ=0 NormalX=0 NormalY=0 NormalZ=1 AngleXU=0 Radius=19 StartAngle=1.5708 EndAngle=3.14159
    g2: LineSegment StartX=117 StartY=38 StartZ=0 EndX=117 EndY=19 EndZ=0
    g3: LineSegment StartX=98 StartY=1.0161e-12 StartZ=0 EndX=5.22862e-06 EndY=1.0161e-12 EndZ=0
    g4: LineSegment StartX=5.22862e-06 StartY=19 StartZ=0 EndX=5.22862e-06 EndY=1.0161e-12 EndZ=0
    g5: ArcOfCircle CenterX=98 CenterY=19 CenterZ=0 NormalX=0 NormalY=0 NormalZ=1 AngleXU=0 Radius=19 StartAngle=4.71239 EndAngle=6.28319
  constraints (16):
    c: Horizontal(g0)
    c: Distance(g0) = 98
    c: Coincident(g1,g0)
    c: Block(g1)
    c: Coincident(g2,g0)
    c: Vertical(g2)
    c: Distance(g2) = 19
    c: Horizontal(g3)
    c: Coincident(g4,g1)
    c: Vertical(g4)
    c: Coincident(g3,g4)
    c: Block(g3)
    c: Coincident(g5,g2)
    c: Coincident(g5,g3)
    c: Block(g0)
    c: Block(g5)
FEATURE [Part::Extrusion] Extrude027  label="sideB001"
  Base = -> Sketch036
  Dir = (0,0,1)
  DirMode = 2
  FaceMakerClass = Part::FaceMakerBullseye
  LengthFwd = 3
  LengthRev = 0
  Placement = pos=(0,0,71.7) rot=(0,0,1;0rad)
  Solid = true
  Symmetric = false
FEATURE [Part::MultiFuse] Fusion064  label="removeFromBottom"
  Shapes = -> [Extrude026,Extrude027]
FEATURE [Part::Cut] Cut024  label="bottom009"
  Base = -> Fusion060
  Tool = -> Fusion064
FEATURE [Sketcher::SketchObject] Sketch037  label="topSketch009"
  FullyConstrained = true
  sketch-geometry (8):
    g0: ArcOfCircle CenterX=19 CenterY=19.1201 CenterZ=0 NormalX=0 NormalY=0 NormalZ=1 AngleXU=0 Radius=18.8799 StartAngle=1.5708 EndAngle=3.14793
    g1: LineSegment StartX=0.120501 StartY=19.0004 StartZ=0 EndX=0.120501 EndY=0.000382114 EndZ=0
    g2: LineSegment StartX=19 StartY=38 StartZ=0 EndX=124 EndY=38 EndZ=0
    g3: LineSegment StartX=0.120501 StartY=0.000382114 StartZ=0 EndX=105.121 EndY=0.000382114 EndZ=0
    g4: LineSegment StartX=124 StartY=38 StartZ=0 EndX=125.616 EndY=38 EndZ=0
    g5: LineSegment StartX=105.121 StartY=0.000382114 StartZ=0 EndX=106.736 EndY=0.000382114 EndZ=0
    g6: ArcOfCircle CenterX=106.616 CenterY=19 CenterZ=0 NormalX=0 NormalY=0 NormalZ=1 AngleXU=0 Radius=19 StartAngle=4.71873 EndAngle=6.28319
    g7: LineSegment StartX=125.616 StartY=38 StartZ=0 EndX=125.616 EndY=19 EndZ=0
  constraints (21):
    c: Block(g0)
    c: Coincident(g1,g0)
    c: Vertical(g1)
    c: Horizontal(g2)
    c: Distance(g2) = 105
    c: Coincident(g2,g0)
    c: Distance(g1) = 19
    c: Coincident(g3,g1)
    c: Horizontal(g3)
    c: Distance(g3) = 105
    c: Coincident(g4,g2)
    c: Horizontal(g4)
    c: Distance(g4) = 1.61553
    c: Horizontal(g5)
    c: Equal(g4,g5) = 1.61553
    c: Coincident(g5,g3)
    c: Block(g6)
    c: Coincident(g6,g5)
    c: Coincident(g7,g4)
    c: Coincident(g7,g6)
    c: Vertical(g7)
FEATURE [Part::Extrusion] Extrude028  label="sideB"
  Base = -> Sketch037
  Dir = (0,0,1)
  DirMode = 2
  FaceMakerClass = Part::FaceMakerBullseye
  LengthFwd = 3
  LengthRev = 0
  Placement = pos=(0,0,72) rot=(0,0,1;0rad)
  Solid = true
  Symmetric = false
FEATURE [Sketcher::SketchObject] Sketch038  label="topSketch010"
  FullyConstrained = true
  sketch-geometry (22):
    g0: LineSegment StartX=5.21097e-06 StartY=3 StartZ=0 EndX=5.21097e-06 EndY=19 EndZ=0
    g1: ArcOfCircle CenterX=19 CenterY=19 CenterZ=0 NormalX=0 NormalY=0 NormalZ=1 AngleXU=0 Radius=19 StartAngle=1.5708 EndAngle=3.14159
    g2: ArcOfCircle CenterX=19 CenterY=19 CenterZ=0 NormalX=0 NormalY=0 NormalZ=1 AngleXU=0 Radius=16 StartAngle=1.5708 EndAngle=3.14159
    g3: LineSegment StartX=114 StartY=35 StartZ=0 EndX=19 EndY=35 EndZ=0
    g4: LineSegment StartX=5.21097e-06 StartY=3 StartZ=0 EndX=5.21097e-06 EndY=0 EndZ=0
    g5: LineSegment StartX=3 StartY=0 StartZ=0 EndX=5.21097e-06 EndY=0 EndZ=0
    g6: LineSegment StartX=3 StartY=19 StartZ=0 EndX=3 EndY=0 EndZ=0
    g7: LineSegment StartX=19 StartY=38 StartZ=0 EndX=124 EndY=38 EndZ=0
    g8: Circle CenterX=119 CenterY=35 CenterZ=0 NormalX=0 NormalY=0 NormalZ=1 AngleXU=0 Radius=1
    g9: Circle CenterX=121 CenterY=35 CenterZ=0 NormalX=0 NormalY=0 NormalZ=1 AngleXU=0 Radius=1
    g10: Circle CenterX=121 CenterY=33 CenterZ=0 NormalX=0 NormalY=0 NormalZ=1 AngleXU=0 Radius=1
    g11: BSplineCurve PolesCount=3 KnotsCount=2 Degree=2 IsPeriodic=0
    g12: GeomPoint X=119 Y=35 Z=0
    g13: GeomPoint X=121 Y=33 Z=0
    g14: LineSegment StartX=119 StartY=35 StartZ=0 EndX=114 EndY=35 EndZ=0
    g15: ArcOfCircle CenterX=105 CenterY=19 CenterZ=0 NormalX=0 NormalY=0 NormalZ=1 AngleXU=0 Radius=16 StartAngle=5.60905 EndAngle=6.28319
    g16: LineSegment StartX=121 StartY=33 StartZ=0 EndX=121 EndY=19 EndZ=0
    g17: LineSegment StartX=117.5 StartY=9.01251 StartZ=0 EndX=121.163 EndY=9.0125 EndZ=0
    g18: ArcOfCircle CenterX=105 CenterY=19 CenterZ=0 NormalX=0 NormalY=0 NormalZ=1 AngleXU=0 Radius=20.6155 StartAngle=5.7297 EndAngle=6.28319
    g19: LineSegment StartX=121.163 StartY=9.0125 StartZ=0 EndX=122.538 EndY=8.16329 EndZ=0
    g20: LineSegment StartX=124 StartY=38 StartZ=0 EndX=125.616 EndY=38 EndZ=0
    g21: LineSegment StartX=125.616 StartY=19 StartZ=0 EndX=125.616 EndY=38 EndZ=0
  constraints (49):
    c: Vertical(g0)
    c: Block(g0)
    c: Coincident(g1,g0)
    c: Block(g1)
    c: Coincident(g2,g1)
    c: Block(g2)
    c: Coincident(g3,g2)
    c: Horizontal(g3)
    c: Tangent(g3,g2)
    c: Coincident(g4,g0)
    c: Distance(g4) = 3
    c: Vertical(g4)
    c: Coincident(g5,g4)
    c: Horizontal(g5)
    c: Coincident(g6,g2)
    c: Coincident(g6,g5)
    c: Vertical(g6)
    c: Horizontal(g7)
    c: Distance(g7) = 105
    c: Coincident(g7,g1)
    c: Block(g3)
    c: Weight(g8) = 1
    c: Equal(g8,g9)
    c: Equal(g8,g10)
    c: InternalAlignment(g8,g11)
    c: InternalAlignment(g9,g11)
    c: InternalAlignment(g10,g11)
    c: InternalAlignment(g12,g11)
    c: InternalAlignment(g13,g11)
    c: Block(g11)
    c: Coincident(g14,g11)
    c: Coincident(g14,g3)
    c: Horizontal(g14)
    c: Block(g15)
    c: Coincident(g16,g11)
    c: Coincident(g16,g15)
    c: Vertical(g16)
    c: Distance(g16) = 14
    c: Coincident(g17,g15)
    c: Block(g18)
    c: Coincident(g19,g18)
    c: Coincident(g20,g7)
    c: Horizontal(g20)
    c: Vertical(g21)
    c: Coincident(g20,g21)
    c: Block(g20)
    c: Block(g21)
    c: Block(g19)
    c: Block(g17)
FEATURE [Part::Extrusion] Extrude029
  Base = -> Sketch038
  Dir = (0,0,1)
  DirMode = 2
  FaceMakerClass = Part::FaceMakerBullseye
  LengthFwd = 72
  LengthRev = 0
  Solid = true
  Symmetric = false
FEATURE [Part::Feature] Face085
  shape: bbox 4.8 x 25.5 x 2e-07 mm, 1 faces, 0 solids (baked)
FEATURE [Part::Revolution] Revolve089  label="moreFrontCaseScrewPost003"
  Angle = 360
  Axis = (0,1,0)
  Base = (0,0,0)
  FaceMakerClass = Part::FaceMakerBullseye
  Placement = pos=(109.5,4.5,3.5) rot=(0,0,1;0rad)
  Solid = false
  Source = -> Face085
  Symmetric = false
FEATURE [Part::Feature] Face086
  shape: bbox 4.8 x 25.5 x 2e-07 mm, 1 faces, 0 solids (baked)
FEATURE [Part::Revolution] Revolve090  label="moreFrontCaseScrewPost004"
  Angle = 360
  Axis = (0,1,0)
  Base = (0,0,0)
  FaceMakerClass = Part::FaceMakerBullseye
  Placement = pos=(109.5,4.5,68.5) rot=(0,0,1;0rad)
  Solid = false
  Source = -> Face086
  Symmetric = false
FEATURE [Part::Fillet] Fillet026  label="top013"
  Base = -> Extrude029
  Edges = 1 edges r=2: [Edge35]
FEATURE [Sketcher::SketchObject] Sketch039
  FullyConstrained = true
  sketch-geometry (7):
    g0: LineSegment StartX=0 StartY=0 StartZ=0 EndX=0 EndY=6 EndZ=0
    g1: Circle CenterX=0 CenterY=0 CenterZ=0 NormalX=0 NormalY=0 NormalZ=1 AngleXU=0 Radius=1
    g2: Circle CenterX=8 CenterY=6 CenterZ=0 NormalX=0 NormalY=0 NormalZ=1 AngleXU=0 Radius=1
    g3: BSplineCurve PolesCount=3 KnotsCount=2 Degree=2 IsPeriodic=0
    g4: GeomPoint X=0 Y=0 Z=0
    g5: GeomPoint X=8 Y=6 Z=0
    g6: LineSegment StartX=0 StartY=6 StartZ=0 EndX=8 EndY=6 EndZ=0
  constraints (14):
    c: Coincident(g0,g-1)
    c: Distance(g0) = 6
    c: Vertical(g0)
    c: Coincident(g3,g0)
    c: Weight(g1) = 1
    c: Equal(g1,g2)
    c: InternalAlignment(g1,g3)
    c: InternalAlignment(g2,g3)
    c: InternalAlignment(g4,g3)
    c: InternalAlignment(g5,g3)
    c: Block(g3)
    c: Coincident(g6,g0)
    c: Coincident(g6,g3)
    c: Horizontal(g6)
FEATURE [Sketcher::SketchObject] Sketch040
  FullyConstrained = true
  sketch-geometry (7):
    g0: LineSegment StartX=0 StartY=0 StartZ=0 EndX=0 EndY=6 EndZ=0
    g1: Circle CenterX=0 CenterY=0 CenterZ=0 NormalX=0 NormalY=0 NormalZ=1 AngleXU=0 Radius=1
    g2: Circle CenterX=8 CenterY=6 CenterZ=0 NormalX=0 NormalY=0 NormalZ=1 AngleXU=0 Radius=1
    g3: BSplineCurve PolesCount=3 KnotsCount=2 Degree=2 IsPeriodic=0
    g4: GeomPoint X=0 Y=0 Z=0
    g5: GeomPoint X=8 Y=6 Z=0
    g6: LineSegment StartX=0 StartY=6 StartZ=0 EndX=8 EndY=6 EndZ=0
  constraints (14):
    c: Coincident(g0,g-1)
    c: Distance(g0) = 6
    c: Vertical(g0)
    c: Coincident(g3,g0)
    c: Weight(g1) = 1
    c: Equal(g1,g2)
    c: InternalAlignment(g1,g3)
    c: InternalAlignment(g2,g3)
    c: InternalAlignment(g4,g3)
    c: InternalAlignment(g5,g3)
    c: Block(g3)
    c: Coincident(g6,g0)
    c: Coincident(g6,g3)
    c: Horizontal(g6)
FEATURE [Sketcher::SketchObject] Sketch041
  FullyConstrained = true
  sketch-geometry (7):
    g0: LineSegment StartX=0 StartY=0 StartZ=0 EndX=0 EndY=6 EndZ=0
    g1: Circle CenterX=0 CenterY=0 CenterZ=0 NormalX=0 NormalY=0 NormalZ=1 AngleXU=0 Radius=1
    g2: Circle CenterX=8 CenterY=6 CenterZ=0 NormalX=0 NormalY=0 NormalZ=1 AngleXU=0 Radius=1
    g3: BSplineCurve PolesCount=3 KnotsCount=2 Degree=2 IsPeriodic=0
    g4: GeomPoint X=0 Y=0 Z=0
    g5: GeomPoint X=8 Y=6 Z=0
    g6: LineSegment StartX=0 StartY=6 StartZ=0 EndX=8 EndY=6 EndZ=0
  constraints (14):
    c: Coincident(g0,g-1)
    c: Distance(g0) = 6
    c: Vertical(g0)
    c: Coincident(g3,g0)
    c: Weight(g1) = 1
    c: Equal(g1,g2)
    c: InternalAlignment(g1,g3)
    c: InternalAlignment(g2,g3)
    c: InternalAlignment(g4,g3)
    c: InternalAlignment(g5,g3)
    c: Block(g3)
    c: Coincident(g6,g0)
    c: Coincident(g6,g3)
    c: Horizontal(g6)
FEATURE [Sketcher::SketchObject] Sketch042
  FullyConstrained = true
  sketch-geometry (7):
    g0: LineSegment StartX=0 StartY=0 StartZ=0 EndX=0 EndY=6 EndZ=0
    g1: Circle CenterX=0 CenterY=0 CenterZ=0 NormalX=0 NormalY=0 NormalZ=1 AngleXU=0 Radius=1
    g2: Circle CenterX=8 CenterY=6 CenterZ=0 NormalX=0 NormalY=0 NormalZ=1 AngleXU=0 Radius=1
    g3: BSplineCurve PolesCount=3 KnotsCount=2 Degree=2 IsPeriodic=0
    g4: GeomPoint X=0 Y=0 Z=0
    g5: GeomPoint X=8 Y=6 Z=0
    g6: LineSegment StartX=0 StartY=6 StartZ=0 EndX=8 EndY=6 EndZ=0
  constraints (14):
    c: Coincident(g0,g-1)
    c: Distance(g0) = 6
    c: Vertical(g0)
    c: Coincident(g3,g0)
    c: Weight(g1) = 1
    c: Equal(g1,g2)
    c: InternalAlignment(g1,g3)
    c: InternalAlignment(g2,g3)
    c: InternalAlignment(g4,g3)
    c: InternalAlignment(g5,g3)
    c: Block(g3)
    c: Coincident(g6,g0)
    c: Coincident(g6,g3)
    c: Horizontal(g6)
FEATURE [Part::Extrusion] Extrude030  label="caseScrewPillarBracket008"
  Base = -> Sketch039
  Dir = (0,0,1)
  DirMode = 2
  FaceMakerClass = Part::FaceMakerBullseye
  LengthFwd = 2.4
  LengthRev = 0
  Placement = pos=(15.76,29,8.8) rot=(0,1,0;0rad)
  Solid = true
  Symmetric = false
FEATURE [Part::Extrusion] Extrude031  label="caseScrewPillarBracket009"
  Base = -> Sketch040
  Dir = (0,0,1)
  DirMode = 2
  FaceMakerClass = Part::FaceMakerBullseye
  LengthFwd = 2.4
  LengthRev = 0
  Placement = pos=(15.76,29,60.8) rot=(0,0,1;0rad)
  Solid = true
  Symmetric = false
FEATURE [Part::Extrusion] Extrude032  label="caseScrewPillarBracket010"
  Base = -> Sketch041
  Dir = (0,0,1)
  DirMode = 2
  FaceMakerClass = Part::FaceMakerBullseye
  LengthFwd = 2.4
  LengthRev = 0
  Placement = pos=(13.7,29,13.26) rot=(0,-1,0;1.5708rad)
  Solid = true
  Symmetric = false
FEATURE [Part::Extrusion] Extrude033  label="caseScrewPillarBracket011"
  Base = -> Sketch042
  Dir = (0,0,1)
  DirMode = 2
  FaceMakerClass = Part::FaceMakerBullseye
  LengthFwd = 2.4
  LengthRev = 0
  Placement = pos=(11.3,29,58.74) rot=(0,1,0;1.5708rad)
  Solid = true
  Symmetric = false
FEATURE [Sketcher::SketchObject] Sketch043
  FullyConstrained = true
  sketch-geometry (7):
    g0: LineSegment StartX=0 StartY=0 StartZ=0 EndX=0 EndY=6 EndZ=0
    g1: Circle CenterX=0 CenterY=0 CenterZ=0 NormalX=0 NormalY=0 NormalZ=1 AngleXU=0 Radius=1
    g2: Circle CenterX=8 CenterY=6 CenterZ=0 NormalX=0 NormalY=0 NormalZ=1 AngleXU=0 Radius=1
    g3: BSplineCurve PolesCount=3 KnotsCount=2 Degree=2 IsPeriodic=0
    g4: GeomPoint X=0 Y=0 Z=0
    g5: GeomPoint X=8 Y=6 Z=0
    g6: LineSegment StartX=0 StartY=6 StartZ=0 EndX=8 EndY=6 EndZ=0
  constraints (14):
    c: Coincident(g0,g-1)
    c: Distance(g0) = 6
    c: Vertical(g0)
    c: Coincident(g3,g0)
    c: Weight(g1) = 1
    c: Equal(g1,g2)
    c: InternalAlignment(g1,g3)
    c: InternalAlignment(g2,g3)
    c: InternalAlignment(g4,g3)
    c: InternalAlignment(g5,g3)
    c: Block(g3)
    c: Coincident(g6,g0)
    c: Coincident(g6,g3)
    c: Horizontal(g6)
FEATURE [Part::Extrusion] Extrude034  label="caseScrewPillarBracket012"
  Base = -> Sketch043
  Dir = (0,0,1)
  DirMode = 2
  FaceMakerClass = Part::FaceMakerBullseye
  LengthFwd = 2.4
  LengthRev = 0
  Placement = pos=(88.3,29,65.23) rot=(0,1,0;1.5708rad)
  Solid = true
  Symmetric = false
FEATURE [Sketcher::SketchObject] Sketch044
  FullyConstrained = true
  sketch-geometry (7):
    g0: LineSegment StartX=0 StartY=0 StartZ=0 EndX=0 EndY=6 EndZ=0
    g1: Circle CenterX=0 CenterY=0 CenterZ=0 NormalX=0 NormalY=0 NormalZ=1 AngleXU=0 Radius=1
    g2: Circle CenterX=8 CenterY=6 CenterZ=0 NormalX=0 NormalY=0 NormalZ=1 AngleXU=0 Radius=1
    g3: BSplineCurve PolesCount=3 KnotsCount=2 Degree=2 IsPeriodic=0
    g4: GeomPoint X=0 Y=0 Z=0
    g5: GeomPoint X=8 Y=6 Z=0
    g6: LineSegment StartX=0 StartY=6 StartZ=0 EndX=8 EndY=6 EndZ=0
  constraints (14):
    c: Coincident(g0,g-1)
    c: Distance(g0) = 6
    c: Vertical(g0)
    c: Coincident(g3,g0)
    c: Weight(g1) = 1
    c: Equal(g1,g2)
    c: InternalAlignment(g1,g3)
    c: InternalAlignment(g2,g3)
    c: InternalAlignment(g4,g3)
    c: InternalAlignment(g5,g3)
    c: Block(g3)
    c: Coincident(g6,g0)
    c: Coincident(g6,g3)
    c: Horizontal(g6)
FEATURE [Part::Extrusion] Extrude035  label="caseScrewPillarBracket013"
  Base = -> Sketch044
  Dir = (0,0,1)
  DirMode = 2
  FaceMakerClass = Part::FaceMakerBullseye
  LengthFwd = 2.4
  LengthRev = 0
  Placement = pos=(90.7,29,6.77) rot=(0,-1,0;1.5708rad)
  Solid = true
  Symmetric = false
FEATURE [Sketcher::SketchObject] Sketch045
  FullyConstrained = true
  sketch-geometry (7):
    g0: LineSegment StartX=0 StartY=0 StartZ=0 EndX=0 EndY=6 EndZ=0
    g1: Circle CenterX=0 CenterY=0 CenterZ=0 NormalX=0 NormalY=0 NormalZ=1 AngleXU=0 Radius=1
    g2: Circle CenterX=8 CenterY=6 CenterZ=0 NormalX=0 NormalY=0 NormalZ=1 AngleXU=0 Radius=1
    g3: BSplineCurve PolesCount=3 KnotsCount=2 Degree=2 IsPeriodic=0
    g4: GeomPoint X=0 Y=0 Z=0
    g5: GeomPoint X=8 Y=6 Z=0
    g6: LineSegment StartX=0 StartY=6 StartZ=0 EndX=8 EndY=6 EndZ=0
  constraints (14):
    c: Coincident(g0,g-1)
    c: Distance(g0) = 6
    c: Vertical(g0)
    c: Coincident(g3,g0)
    c: Weight(g1) = 1
    c: Equal(g1,g2)
    c: InternalAlignment(g1,g3)
    c: InternalAlignment(g2,g3)
    c: InternalAlignment(g4,g3)
    c: InternalAlignment(g5,g3)
    c: Block(g3)
    c: Coincident(g6,g0)
    c: Coincident(g6,g3)
    c: Horizontal(g6)
FEATURE [Sketcher::SketchObject] Sketch046
  FullyConstrained = true
  sketch-geometry (7):
    g0: LineSegment StartX=0 StartY=0 StartZ=0 EndX=0 EndY=6 EndZ=0
    g1: Circle CenterX=0 CenterY=0 CenterZ=0 NormalX=0 NormalY=0 NormalZ=1 AngleXU=0 Radius=1
    g2: Circle CenterX=8 CenterY=6 CenterZ=0 NormalX=0 NormalY=0 NormalZ=1 AngleXU=0 Radius=1
    g3: BSplineCurve PolesCount=3 KnotsCount=2 Degree=2 IsPeriodic=0
    g4: GeomPoint X=0 Y=0 Z=0
    g5: GeomPoint X=8 Y=6 Z=0
    g6: LineSegment StartX=0 StartY=6 StartZ=0 EndX=8 EndY=6 EndZ=0
  constraints (14):
    c: Coincident(g0,g-1)
    c: Distance(g0) = 6
    c: Vertical(g0)
    c: Coincident(g3,g0)
    c: Weight(g1) = 1
    c: Equal(g1,g2)
    c: InternalAlignment(g1,g3)
    c: InternalAlignment(g2,g3)
    c: InternalAlignment(g4,g3)
    c: InternalAlignment(g5,g3)
    c: Block(g3)
    c: Coincident(g6,g0)
    c: Coincident(g6,g3)
    c: Horizontal(g6)
FEATURE [Part::Extrusion] Extrude036  label="caseScrewPillarBracket014"
  Base = -> Sketch045
  Dir = (0,0,1)
  DirMode = 2
  FaceMakerClass = Part::FaceMakerBullseye
  LengthFwd = 2.4
  LengthRev = 0
  Placement = pos=(110.7,29,6.77) rot=(0,-1,0;1.5708rad)
  Solid = true
  Symmetric = false
FEATURE [Part::Extrusion] Extrude037  label="caseScrewPillarBracket015"
  Base = -> Sketch046
  Dir = (0,0,1)
  DirMode = 2
  FaceMakerClass = Part::FaceMakerBullseye
  LengthFwd = 2.4
  LengthRev = 0
  Placement = pos=(108.3,29,65.23) rot=(0,1,0;1.5708rad)
  Solid = true
  Symmetric = false
FEATURE [Part::Box] Box013  label="frontCaseScrewPillarBracket002"
  AttacherType = Attacher::AttachEngine3D
  Height = 2.4
  Length = 22
  Placement = pos=(87,28,2.3) rot=(0,0,1;0rad)
  Width = 7
FEATURE [Part::Box] Box014  label="frontCaseScrewPillarBracket003"
  AttacherType = Attacher::AttachEngine3D
  Height = 2.4
  Length = 22
  Placement = pos=(87,28,67.3) rot=(0,0,1;0rad)
  Width = 7
FEATURE [Part::Feature] Face087
  shape: bbox 4.8 x 30.2 x 2e-07 mm, 1 faces, 0 solids (baked)
FEATURE [Part::Revolution] Revolve091  label="frontCaseScrewPost004"
  Angle = 360
  Axis = (0,1,0)
  Base = (0,0,0)
  FaceMakerClass = Part::FaceMakerBullseye
  Placement = pos=(89.5,4.5,3.5) rot=(0,0,1;0rad)
  Solid = false
  Source = -> Face087
  Symmetric = false
FEATURE [Part::Feature] Face088
  shape: bbox 4.8 x 30.2 x 2e-07 mm, 1 faces, 0 solids (baked)
FEATURE [Part::Revolution] Revolve092  label="frontCaseScrewPost005"
  Angle = 360
  Axis = (0,1,0)
  Base = (0,0,0)
  FaceMakerClass = Part::FaceMakerBullseye
  Placement = pos=(89.5,4.5,68.5) rot=(0,0,1;0rad)
  Solid = false
  Source = -> Face088
  Symmetric = false
FEATURE [Part::Feature] Face089
  shape: bbox 3.5 x 30.2 x 2e-07 mm, 1 faces, 0 solids (baked)
FEATURE [Part::Revolution] Revolve093  label="backCaseScrewPost002"
  Angle = 360
  Axis = (0,1,0)
  Base = (0,0,0)
  FaceMakerClass = Part::FaceMakerBullseye
  Placement = pos=(12.5,4.5,10) rot=(0,0,1;0rad)
  Solid = false
  Source = -> Face089
  Symmetric = false
FEATURE [Part::Feature] Face090
  shape: bbox 3.5 x 30.2 x 2e-07 mm, 1 faces, 0 solids (baked)
FEATURE [Part::Revolution] Revolve094  label="backCaseScrewPost003"
  Angle = 360
  Axis = (0,1,0)
  Base = (0,0,0)
  FaceMakerClass = Part::FaceMakerBullseye
  Placement = pos=(12.5,4.5,62) rot=(0,0,1;0rad)
  Solid = false
  Source = -> Face090
  Symmetric = false
FEATURE [Part::Box] Box015  label="Cube011"
  AttacherType = Attacher::AttachEngine3D
  Height = 28.8
  Length = 3
  Placement = pos=(107.3,28,21.6) rot=(0,0,1;0rad)
  Width = 7
FEATURE [Part::Box] Box016  label="Cube012"
  AttacherType = Attacher::AttachEngine3D
  Height = 3
  Length = 7.4
  Placement = pos=(107.3,28,18.6) rot=(0,0,1;0rad)
  Width = 7
FEATURE [Part::Box] Box017  label="Cube013"
  AttacherType = Attacher::AttachEngine3D
  Height = 3
  Length = 7.4
  Placement = pos=(107.3,28,50.4) rot=(0,0,1;0rad)
  Width = 7
FEATURE [Part::Cylinder] Cylinder024
  Angle = 360
  AttacherType = Attacher::AttachEngine3D
  Height = 20
  Placement = pos=(0,0,36.15) rot=(0,0,1;0rad)
  Radius = 14.3
FEATURE [Part::Cylinder] Cylinder025
  Angle = 360
  AttacherType = Attacher::AttachEngine3D
  Height = 10
  Placement = pos=(0,0,36.15) rot=(0,0,1;0rad)
  Radius = 4
FEATURE [Part::MultiFuse] Fusion066  label="removeToCreteHoleForPlugHousing009"
  Placement = pos=(70,19,36) rot=(0,1,0;1.5708rad)
  Shapes = -> [Cylinder024,Cylinder025]
FEATURE [Part::MultiFuse] Fusion065  label="plugHousingBracketHolder002"
  Shapes = -> [Box017,Box015,Box016]
FEATURE [Part::Cut] Cut025  label="plugHousingBracketHolder003"
  Base = -> Fusion065
  Placement = pos=(7,0,0) rot=(0,0,1;0rad)
  Tool = -> Fusion066
FEATURE [Sketcher::SketchObject] Sketch047
  FullyConstrained = false
  Placement = pos=(0,0,0) rot=(1,0,0;1.5708rad)
  sketch-geometry (24):
    g0: ArcOfCircle CenterX=-4 CenterY=-10.5 CenterZ=0 NormalX=0 NormalY=0 NormalZ=1 AngleXU=0 Radius=1.5 StartAngle=6e-16 EndAngle=3.14159
    g1: ArcOfCircle CenterX=-34.2 CenterY=-10.5 CenterZ=0 NormalX=0 NormalY=0 NormalZ=1 AngleXU=0 Radius=1.5 StartAngle=0 EndAngle=3.14159
    g2: ArcOfCircle CenterX=-34.2 CenterY=-27.7 CenterZ=0 NormalX=0 NormalY=0 NormalZ=1 AngleXU=0 Radius=1.5 StartAngle=3.14159 EndAngle=6.28319
    g3: ArcOfCircle CenterX=-4 CenterY=-27.7 CenterZ=0 NormalX=0 NormalY=0 NormalZ=1 AngleXU=0 Radius=1.5 StartAngle=3.1416 EndAngle=6.28319
    g4: ArcOfCircle CenterX=-10 CenterY=-4.3 CenterZ=0 NormalX=0 NormalY=0 NormalZ=1 AngleXU=0 Radius=1.5 StartAngle=2e-16 EndAngle=3.14159
    g5: ArcOfCircle CenterX=-16.1 CenterY=-1.8 CenterZ=0 NormalX=0 NormalY=0 NormalZ=1 AngleXU=0 Radius=1.5 StartAngle=5e-16 EndAngle=3.14159
    g6: ArcOfCircle CenterX=-22.1 CenterY=-1.8 CenterZ=0 NormalX=0 NormalY=0 NormalZ=1 AngleXU=0 Radius=1.5 StartAngle=5e-16 EndAngle=3.14159
    g7: ArcOfCircle CenterX=-28.2 CenterY=-4.3 CenterZ=0 NormalX=0 NormalY=0 NormalZ=1 AngleXU=0 Radius=1.5 StartAngle=2e-16 EndAngle=3.14159
    g8: ArcOfCircle CenterX=-10 CenterY=-33.9 CenterZ=0 NormalX=0 NormalY=0 NormalZ=1 AngleXU=0 Radius=1.5 StartAngle=3.14159 EndAngle=6.28319
    g9: ArcOfCircle CenterX=-16.1 CenterY=-36.4 CenterZ=0 NormalX=0 NormalY=0 NormalZ=1 AngleXU=0 Radius=1.5 StartAngle=3.14159 EndAngle=6.28319
    g10: ArcOfCircle CenterX=-22.1 CenterY=-36.4 CenterZ=0 NormalX=0 NormalY=0 NormalZ=1 AngleXU=0 Radius=1.5 StartAngle=3.14159 EndAngle=6.28319
    g11: ArcOfCircle CenterX=-28.2 CenterY=-33.9 CenterZ=0 NormalX=0 NormalY=0 NormalZ=1 AngleXU=0 Radius=1.5 StartAngle=3.14159 EndAngle=6.28319
    g12: LineSegment StartX=-35.7 StartY=-10.5 StartZ=0 EndX=-35.7 EndY=-27.7 EndZ=0
    g13: LineSegment StartX=-32.7 StartY=-10.5 StartZ=0 EndX=-32.7 EndY=-27.7 EndZ=0
    g14: LineSegment StartX=-29.7 StartY=-33.9 StartZ=0 EndX=-29.7 EndY=-4.3 EndZ=0
    g15: LineSegment StartX=-26.7 StartY=-33.9 StartZ=0 EndX=-26.7 EndY=-4.3 EndZ=0
    g16: LineSegment StartX=-2.5 StartY=-10.5 StartZ=0 EndX=-2.5 EndY=-27.7 EndZ=0
    g17: LineSegment StartX=-8.5 StartY=-4.3 StartZ=0 EndX=-8.5 EndY=-33.9 EndZ=0
    g18: LineSegment StartX=-5.5 StartY=-10.5 StartZ=0 EndX=-5.5 EndY=-27.7 EndZ=0
    g19: LineSegment StartX=-11.5 StartY=-4.3 StartZ=0 EndX=-11.5 EndY=-33.9 EndZ=0
    g20: LineSegment StartX=-14.6 StartY=-1.8 StartZ=0 EndX=-14.6 EndY=-36.4 EndZ=0
    g21: LineSegment StartX=-17.6 StartY=-1.8 StartZ=0 EndX=-17.6 EndY=-36.4 EndZ=0
    g22: LineSegment StartX=-20.6 StartY=-36.4 StartZ=0 EndX=-20.6 EndY=-1.8 EndZ=0
    g23: LineSegment StartX=-23.6 StartY=-1.8 StartZ=0 EndX=-23.6 EndY=-36.4 EndZ=0
  constraints (48):
    c: Block(g0)
    c: Block(g1)
    c: Block(g2)
    c: Block(g3)
    c: Block(g4)
    c: Block(g5)
    c: Block(g6)
    c: Block(g7)
    c: Block(g8)
    c: Block(g9)
    c: Block(g10)
    c: Block(g11)
    c: Coincident(g12,g1)
    c: Coincident(g12,g2)
    c: Vertical(g12)
    c: Coincident(g13,g1)
    c: Coincident(g13,g2)
    c: Vertical(g13)
    c: Coincident(g14,g11)
    c: Coincident(g14,g7)
    c: Vertical(g14)
    c: Coincident(g15,g11)
    c: Coincident(g15,g7)
    c: Vertical(g15)
    c: Coincident(g16,g0)
    c: Coincident(g16,g3)
    c: Vertical(g16)
    c: Coincident(g17,g4)
    c: Coincident(g17,g8)
    c: Vertical(g17)
    c: Coincident(g18,g0)
    c: Coincident(g18,g3)
    c: Vertical(g18)
    c: Coincident(g19,g4)
    c: Coincident(g19,g8)
    c: Vertical(g19)
    c: Coincident(g20,g5)
    c: Coincident(g20,g9)
    c: Vertical(g20)
    c: Coincident(g21,g5)
    c: Coincident(g21,g9)
    c: Vertical(g21)
    c: Coincident(g22,g10)
    c: Coincident(g22,g6)
    c: Vertical(g22)
    c: Coincident(g23,g6)
    c: Coincident(g23,g10)
    c: Vertical(g23)
FEATURE [Part::Extrusion] Extrude038  label="removeToCreateFanGrillHoles001"
  Base = -> Sketch047
  Dir = (0,-1,6e-16)
  DirMode = 2
  FaceMakerClass = Part::FaceMakerBullseye
  LengthFwd = 10
  LengthRev = 0
  Placement = pos=(65.4,44,54.82) rot=(0,0,1;0rad)
  Solid = true
  Symmetric = false
FEATURE [Part::Feature] Wire004
  shape: bbox 11 x 5.2 x 2e-07 mm, 0 faces, 0 solids (baked)
FEATURE [Part::Revolution] Revolve095
  Angle = 360
  Axis = (0,1,0)
  Base = (0,0,0)
  FaceMakerClass = Part::FaceMakerBullseye
  Placement = pos=(30.3,38,19.7) rot=(0,0,1;0rad)
  Solid = true
  Source = -> Wire004
  Symmetric = false
FEATURE [Part::Feature] Wire005
  shape: bbox 11 x 5.2 x 2e-07 mm, 0 faces, 0 solids (baked)
FEATURE [Part::Revolution] Revolve096
  Angle = 360
  Axis = (0,1,0)
  Base = (0,0,0)
  FaceMakerClass = Part::FaceMakerBullseye
  Placement = pos=(30.3,38,51.7) rot=(0,0,1;0rad)
  Solid = true
  Source = -> Wire005
  Symmetric = false
FEATURE [Part::Feature] Wire006
  shape: bbox 11 x 5.2 x 2e-07 mm, 0 faces, 0 solids (baked)
FEATURE [Part::Revolution] Revolve097
  Angle = 360
  Axis = (0,1,0)
  Base = (0,0,0)
  FaceMakerClass = Part::FaceMakerBullseye
  Placement = pos=(62.3,38,51.7) rot=(0,0,1;0rad)
  Solid = true
  Source = -> Wire006
  Symmetric = false
FEATURE [Part::Feature] Wire007
  shape: bbox 11 x 5.2 x 2e-07 mm, 0 faces, 0 solids (baked)
FEATURE [Part::Revolution] Revolve098
  Angle = 360
  Axis = (0,1,0)
  Base = (0,0,0)
  FaceMakerClass = Part::FaceMakerBullseye
  Placement = pos=(62.3,38,19.7) rot=(0,0,1;0rad)
  Solid = true
  Source = -> Wire007
  Symmetric = false
FEATURE [Part::MultiFuse] Fusion067  label="fanScrewHousing002"
  Shapes = -> [Revolve098,Revolve097,Revolve096,Revolve095]
FEATURE [Part::Feature] Face091 .. Face094  x4 (patterned run collapsed; names and placements below)
  shape: bbox 3.5 x 17.8 x 2e-07 mm, 1 faces, 0 solids (baked)
FEATURE [Part::Revolution] Revolve099  label="removeToCreateScrewAndThreadedInsertHole026"
  Angle = 360
  Axis = (0,1,0)
  Base = (0,0,0)
  FaceMakerClass = Part::FaceMakerBullseye
  Placement = pos=(62.3,30.3,19.7) rot=(0,0,1;0rad)
  Solid = false
  Source = -> Face091
  Symmetric = false
FEATURE [Part::Revolution] Revolve100  label="removeToCreateScrewAndThreadedInsertHole027"
  Angle = 360
  Axis = (0,1,0)
  Base = (0,0,0)
  FaceMakerClass = Part::FaceMakerBullseye
  Placement = pos=(62.3,30.3,51.7) rot=(0,0,1;0rad)
  Solid = false
  Source = -> Face092
  Symmetric = false
FEATURE [Part::Revolution] Revolve101  label="removeToCreateScrewAndThreadedInsertHole028"
  Angle = 360
  Axis = (0,1,0)
  Base = (0,0,0)
  FaceMakerClass = Part::FaceMakerBullseye
  Placement = pos=(30.3,30.3,19.7) rot=(0,0,1;0rad)
  Solid = false
  Source = -> Face093
  Symmetric = false
FEATURE [Part::Revolution] Revolve102  label="removeToCreateScrewAndThreadedInsertHole029"
  Angle = 360
  Axis = (0,1,0)
  Base = (0,0,0)
  FaceMakerClass = Part::FaceMakerBullseye
  Placement = pos=(30.3,30.3,51.7) rot=(0,0,1;0rad)
  Solid = false
  Source = -> Face094
  Symmetric = false
FEATURE [Part::MultiFuse] Fusion068  label="createThreadedInsertHolesForFan002"
  Shapes = -> [Revolve099,Revolve100,Revolve101,Revolve102]
FEATURE [Part::Cut] Cut026  label="fanScrewHousing003"
  Base = -> Fusion067
  Tool = -> Fusion068
FEATURE [Sketcher::SketchObject] Sketch048
  FullyConstrained = false
  Placement = pos=(0,0,0) rot=(1,0,0;1.5708rad)
  sketch-geometry (24):
    g0: ArcOfCircle CenterX=-4 CenterY=-10.5 CenterZ=0 NormalX=0 NormalY=0 NormalZ=1 AngleXU=0 Radius=1.5 StartAngle=6e-16 EndAngle=3.14159
    g1: ArcOfCircle CenterX=-34.2 CenterY=-10.5 CenterZ=0 NormalX=0 NormalY=0 NormalZ=1 AngleXU=0 Radius=1.5 StartAngle=0 EndAngle=3.14159
    g2: ArcOfCircle CenterX=-34.2 CenterY=-27.7 CenterZ=0 NormalX=0 NormalY=0 NormalZ=1 AngleXU=0 Radius=1.5 StartAngle=3.14159 EndAngle=6.28319
    g3: ArcOfCircle CenterX=-4 CenterY=-27.7 CenterZ=0 NormalX=0 NormalY=0 NormalZ=1 AngleXU=0 Radius=1.5 StartAngle=3.1416 EndAngle=6.28319
    g4: ArcOfCircle CenterX=-10 CenterY=-4.3 CenterZ=0 NormalX=0 NormalY=0 NormalZ=1 AngleXU=0 Radius=1.5 StartAngle=2e-16 EndAngle=3.14159
    g5: ArcOfCircle CenterX=-16.1 CenterY=-1.8 CenterZ=0 NormalX=0 NormalY=0 NormalZ=1 AngleXU=0 Radius=1.5 StartAngle=5e-16 EndAngle=3.14159
    g6: ArcOfCircle CenterX=-22.1 CenterY=-1.8 CenterZ=0 NormalX=0 NormalY=0 NormalZ=1 AngleXU=0 Radius=1.5 StartAngle=5e-16 EndAngle=3.14159
    g7: ArcOfCircle CenterX=-28.2 CenterY=-4.3 CenterZ=0 NormalX=0 NormalY=0 NormalZ=1 AngleXU=0 Radius=1.5 StartAngle=2e-16 EndAngle=3.14159
    g8: ArcOfCircle CenterX=-10 CenterY=-33.9 CenterZ=0 NormalX=0 NormalY=0 NormalZ=1 AngleXU=0 Radius=1.5 StartAngle=3.14159 EndAngle=6.28319
    g9: ArcOfCircle CenterX=-16.1 CenterY=-36.4 CenterZ=0 NormalX=0 NormalY=0 NormalZ=1 AngleXU=0 Radius=1.5 StartAngle=3.14159 EndAngle=6.28319
    g10: ArcOfCircle CenterX=-22.1 CenterY=-36.4 CenterZ=0 NormalX=0 NormalY=0 NormalZ=1 AngleXU=0 Radius=1.5 StartAngle=3.14159 EndAngle=6.28319
    g11: ArcOfCircle CenterX=-28.2 CenterY=-33.9 CenterZ=0 NormalX=0 NormalY=0 NormalZ=1 AngleXU=0 Radius=1.5 StartAngle=3.14159 EndAngle=6.28319
    g12: LineSegment StartX=-35.7 StartY=-10.5 StartZ=0 EndX=-35.7 EndY=-27.7 EndZ=0
    g13: LineSegment StartX=-32.7 StartY=-10.5 StartZ=0 EndX=-32.7 EndY=-27.7 EndZ=0
    g14: LineSegment StartX=-29.7 StartY=-33.9 StartZ=0 EndX=-29.7 EndY=-4.3 EndZ=0
    g15: LineSegment StartX=-26.7 StartY=-33.9 StartZ=0 EndX=-26.7 EndY=-4.3 EndZ=0
    g16: LineSegment StartX=-2.5 StartY=-10.5 StartZ=0 EndX=-2.5 EndY=-27.7 EndZ=0
    g17: LineSegment StartX=-8.5 StartY=-4.3 StartZ=0 EndX=-8.5 EndY=-33.9 EndZ=0
    g18: LineSegment StartX=-5.5 StartY=-10.5 StartZ=0 EndX=-5.5 EndY=-27.7 EndZ=0
    g19: LineSegment StartX=-11.5 StartY=-4.3 StartZ=0 EndX=-11.5 EndY=-33.9 EndZ=0
    g20: LineSegment StartX=-14.6 StartY=-1.8 StartZ=0 EndX=-14.6 EndY=-36.4 EndZ=0
    g21: LineSegment StartX=-17.6 StartY=-1.8 StartZ=0 EndX=-17.6 EndY=-36.4 EndZ=0
    g22: LineSegment StartX=-20.6 StartY=-36.4 StartZ=0 EndX=-20.6 EndY=-1.8 EndZ=0
    g23: LineSegment StartX=-23.6 StartY=-1.8 StartZ=0 EndX=-23.6 EndY=-36.4 EndZ=0
  constraints (48):
    c: Block(g0)
    c: Block(g1)
    c: Block(g2)
    c: Block(g3)
    c: Block(g4)
    c: Block(g5)
    c: Block(g6)
    c: Block(g7)
    c: Block(g8)
    c: Block(g9)
    c: Block(g10)
    c: Block(g11)
    c: Coincident(g12,g1)
    c: Coincident(g12,g2)
    c: Vertical(g12)
    c: Coincident(g13,g1)
    c: Coincident(g13,g2)
    c: Vertical(g13)
    c: Coincident(g14,g11)
    c: Coincident(g14,g7)
    c: Vertical(g14)
    c: Coincident(g15,g11)
    c: Coincident(g15,g7)
    c: Vertical(g15)
    c: Coincident(g16,g0)
    c: Coincident(g16,g3)
    c: Vertical(g16)
    c: Coincident(g17,g4)
    c: Coincident(g17,g8)
    c: Vertical(g17)
    c: Coincident(g18,g0)
    c: Coincident(g18,g3)
    c: Vertical(g18)
    c: Coincident(g19,g4)
    c: Coincident(g19,g8)
    c: Vertical(g19)
    c: Coincident(g20,g5)
    c: Coincident(g20,g9)
    c: Vertical(g20)
    c: Coincident(g21,g5)
    c: Coincident(g21,g9)
    c: Vertical(g21)
    c: Coincident(g22,g10)
    c: Coincident(g22,g6)
    c: Vertical(g22)
    c: Coincident(g23,g6)
    c: Coincident(g23,g10)
    c: Vertical(g23)
FEATURE [Part::Extrusion] Extrude039  label="removeToCreateFanGrillHoles002"
  Base = -> Sketch048
  Dir = (0,-1,6e-16)
  DirMode = 2
  FaceMakerClass = Part::FaceMakerBullseye
  LengthFwd = 10
  LengthRev = 0
  Placement = pos=(65.4,44,54.82) rot=(0,0,1;0rad)
  Solid = true
  Symmetric = false
FEATURE [Part::Cut] Cut027  label="fanScrewHousing004"
  Base = -> Cut026
  Tool = -> Extrude038
FEATURE [Part::Cut] Cut028  label="top014"
  Base = -> Fillet026
  Tool = -> Extrude039
FEATURE [Part::Feature] Face095 .. Face098  x4 (patterned run collapsed; names and placements below)
  shape: bbox 3.5 x 17.8 x 2e-07 mm, 1 faces, 0 solids (baked)
FEATURE [Part::Revolution] Revolve103  label="removeToCreateScrewAndThreadedInsertHole030"
  Angle = 360
  Axis = (0,1,0)
  Base = (0,0,0)
  FaceMakerClass = Part::FaceMakerBullseye
  Placement = pos=(62.3,30.3,19.7) rot=(0,0,1;0rad)
  Solid = false
  Source = -> Face095
  Symmetric = false
FEATURE [Part::Revolution] Revolve104  label="removeToCreateScrewAndThreadedInsertHole031"
  Angle = 360
  Axis = (0,1,0)
  Base = (0,0,0)
  FaceMakerClass = Part::FaceMakerBullseye
  Placement = pos=(62.3,30.3,51.7) rot=(0,0,1;0rad)
  Solid = false
  Source = -> Face096
  Symmetric = false
FEATURE [Part::Revolution] Revolve105  label="removeToCreateScrewAndThreadedInsertHole032"
  Angle = 360
  Axis = (0,1,0)
  Base = (0,0,0)
  FaceMakerClass = Part::FaceMakerBullseye
  Placement = pos=(30.3,30.3,19.7) rot=(0,0,1;0rad)
  Solid = false
  Source = -> Face097
  Symmetric = false
FEATURE [Part::Revolution] Revolve106  label="removeToCreateScrewAndThreadedInsertHole033"
  Angle = 360
  Axis = (0,1,0)
  Base = (0,0,0)
  FaceMakerClass = Part::FaceMakerBullseye
  Placement = pos=(30.3,30.3,51.7) rot=(0,0,1;0rad)
  Solid = false
  Source = -> Face098
  Symmetric = false
FEATURE [Part::MultiFuse] Fusion069  label="createThreadedInsertHolesForFan003"
  Shapes = -> [Revolve103,Revolve104,Revolve105,Revolve106]
FEATURE [Part::Cut] Cut029  label="top015"
  Base = -> Cut028
  Tool = -> Fusion054
FEATURE [Part::Cut] Cut030  label="fanScrewHousing005"
  Base = -> Cut027
  Tool = -> Fusion069
FEATURE [Part::Cylinder] Cylinder026  label="removeToCreteHoleForPlugHousing010"
  Angle = 360
  AttacherType = Attacher::AttachEngine3D
  Height = 20
  Placement = pos=(-2,19,36) rot=(0,1,0;1.5708rad)
  Radius = 14.3
FEATURE [Part::Box] Box018  label="removeToCreteHoleForPlugHousing011"
  AttacherType = Attacher::AttachEngine3D
  Height = 28.6
  Length = 10
  Placement = pos=(-2,0,21.7) rot=(0,0,1;0rad)
  Width = 19
FEATURE [Part::Box] Box019  label="wireHolderBottomCaseBit"
  AttacherType = Attacher::AttachEngine3D
  Height = 28
  Length = 3
  Placement = pos=(0,0,22) rot=(0,0,1;0rad)
  Width = 21
FEATURE [Part::Cylinder] Cylinder027  label="removeToCreteHoleForPlugHousing012"
  Angle = 360
  AttacherType = Attacher::AttachEngine3D
  Height = 20
  Placement = pos=(-2,19,36) rot=(0,1,0;1.5708rad)
  Radius = 14.3
FEATURE [Part::Cut] Cut031  label="wireHolderBottomCaseBit001"
  Base = -> Box019
  Tool = -> Cylinder027
FEATURE [Part::MultiFuse] Fusion070  label="removeToCreteHoleForPlugHousing013"
  Shapes = -> [Box018,Cylinder026]
FEATURE [Part::Cut] Cut032  label="top016"
  Base = -> Cut029
  Tool = -> Fusion070
FEATURE [Part::Cylinder] Cylinder028
  Angle = 360
  AttacherType = Attacher::AttachEngine3D
  Height = 20
  Placement = pos=(0,0,36.15) rot=(0,0,1;0rad)
  Radius = 14.3
FEATURE [Part::Cylinder] Cylinder029
  Angle = 360
  AttacherType = Attacher::AttachEngine3D
  Height = 10
  Placement = pos=(0,0,36.15) rot=(0,0,1;0rad)
  Radius = 4
FEATURE [Part::MultiFuse] Fusion071  label="removeToCreteHoleForPlugHousing014"
  Placement = pos=(70,19,36) rot=(0,1,0;1.5708rad)
  Shapes = -> [Cylinder028,Cylinder029]
FEATURE [Sketcher::SketchObject] Sketch049  label="topSketch011"
  FullyConstrained = true
  sketch-geometry (4):
    g0: ArcOfCircle CenterX=105 CenterY=19 CenterZ=0 NormalX=0 NormalY=0 NormalZ=1 AngleXU=0 Radius=20.6155 StartAngle=5.54125 EndAngle=6.28319
    g1: ArcOfCircle CenterX=105 CenterY=19 CenterZ=0 NormalX=0 NormalY=0 NormalZ=1 AngleXU=0 Radius=13 StartAngle=5.54125 EndAngle=6.28319
    g2: LineSegment StartX=118 StartY=19 StartZ=0 EndX=125.616 EndY=19 EndZ=0
    g3: LineSegment StartX=114.583 StartY=10.2157 StartZ=0 EndX=120.197 EndY=5.06982 EndZ=0
  constraints (7):
    c: Block(g0)
    c: Block(g1)
    c: Coincident(g2,g1)
    c: Coincident(g2,g0)
    c: Horizontal(g2)
    c: Coincident(g3,g1)
    c: Coincident(g3,g0)
FEATURE [Part::Box] Box020  label="removeToCreteHoleForPlugHousing015"
  AttacherType = Attacher::AttachEngine3D
  Height = 28.6
  Length = 20
  Placement = pos=(106.15,0,21.7) rot=(0,0,1;0rad)
  Width = 19
FEATURE [Part::MultiFuse] Fusion072  label="removeToCreteHoleForPlugHousing016"
  Shapes = -> [Box020,Fusion071]
FEATURE [Part::Cut] Cut033  label="removeToCreteHoleForPlugHousing017"
  Base = -> Cut032
  Tool = -> Fusion072
FEATURE [Part::Cylinder] Cylinder030
  Angle = 360
  AttacherType = Attacher::AttachEngine3D
  Height = 20
  Placement = pos=(0,0,36.15) rot=(0,0,1;0rad)
  Radius = 14.3
FEATURE [Part::Cylinder] Cylinder031
  Angle = 360
  AttacherType = Attacher::AttachEngine3D
  Height = 10
  Placement = pos=(0,0,36.15) rot=(0,0,1;0rad)
  Radius = 4
FEATURE [Part::Box] Box021  label="removeToCreteHoleForPlugHousing019"
  AttacherType = Attacher::AttachEngine3D
  Height = 28.6
  Length = 20
  Placement = pos=(106.15,0,21.7) rot=(0,0,1;0rad)
  Width = 19
FEATURE [Part::MultiFuse] Fusion074  label="removeToCreteHoleForPlugHousing020"
  Placement = pos=(70,19,36) rot=(0,1,0;1.5708rad)
  Shapes = -> [Cylinder030,Cylinder031]
FEATURE [Part::MultiFuse] Fusion073  label="removeToCreteHoleForPlugHousing018"
  Placement = pos=(0,0,28.3) rot=(0,0,1;0rad)
  Shapes = -> [Box021,Fusion074]
FEATURE [Part::Cylinder] Cylinder032
  Angle = 360
  AttacherType = Attacher::AttachEngine3D
  Height = 20
  Placement = pos=(0,0,36.15) rot=(0,0,1;0rad)
  Radius = 14.3
FEATURE [Part::Cylinder] Cylinder033
  Angle = 360
  AttacherType = Attacher::AttachEngine3D
  Height = 10
  Placement = pos=(0,0,36.15) rot=(0,0,1;0rad)
  Radius = 4
FEATURE [Part::Box] Box022  label="removeToCreteHoleForPlugHousing021"
  AttacherType = Attacher::AttachEngine3D
  Height = 28.6
  Length = 20
  Placement = pos=(106.15,0,21.7) rot=(0,0,1;0rad)
  Width = 19
FEATURE [Part::MultiFuse] Fusion076  label="removeToCreteHoleForPlugHousing023"
  Placement = pos=(70,19,36) rot=(0,1,0;1.5708rad)
  Shapes = -> [Cylinder032,Cylinder033]
FEATURE [Part::MultiFuse] Fusion075  label="removeToCreteHoleForPlugHousing022"
  Placement = pos=(0,0,-28.3) rot=(0,0,1;0rad)
  Shapes = -> [Box022,Fusion076]
FEATURE [Part::MultiFuse] Fusion077  label="removeToCreatePlugHousingBottomBit"
  Shapes = -> [Fusion075,Fusion073]
FEATURE [Part::Cylinder] Cylinder034
  Angle = 360
  AttacherType = Attacher::AttachEngine3D
  Height = 20
  Placement = pos=(0,0,36.15) rot=(0,0,1;0rad)
  Radius = 14
FEATURE [Part::Cylinder] Cylinder035
  Angle = 360
  AttacherType = Attacher::AttachEngine3D
  Height = 10
  Placement = pos=(0,0,36.15) rot=(0,0,1;0rad)
  Radius = 4
FEATURE [Part::MultiFuse] Fusion078  label="removeToCreteHoleForPlugHousing024"
  Placement = pos=(70,19,36) rot=(0,1,0;1.5708rad)
  Shapes = -> [Cylinder034,Cylinder035]
FEATURE [Part::MultiFuse] Fusion079  label="removeToCreatePlugHousingBottomBit001"
  Shapes = -> [Fusion078,Fusion077]
FEATURE [Part::Extrusion] Extrude040  label="bottomPlugHousingBit"
  Base = -> Sketch049
  Dir = (0,0,1)
  DirMode = 2
  FaceMakerClass = Part::FaceMakerBullseye
  LengthFwd = 72
  LengthRev = 0
  Solid = true
  Symmetric = false
FEATURE [Part::Cut] Cut034  label="bottomPlugHousingBit001"
  Base = -> Extrude040
  Placement = pos=(-0.09,0,0) rot=(0,0,1;0rad)
  Tool = -> Fusion079
FEATURE [Part::Box] Box023  label="Cube014"
  AttacherType = Attacher::AttachEngine3D
  Height = 16
  Length = 8
  Placement = pos=(12.7,31.52,28) rot=(0,0,1;0rad)
  Width = 4
FEATURE [Part::Cylinder] Cylinder036
  Angle = 360
  AttacherType = Attacher::AttachEngine3D
  Height = 10
  Placement = pos=(0,0,36.15) rot=(0,0,1;0rad)
  Radius = 4
FEATURE [Part::Cylinder] Cylinder037
  Angle = 360
  AttacherType = Attacher::AttachEngine3D
  Height = 20
  Placement = pos=(0,0,36.15) rot=(0,0,1;0rad)
  Radius = 8.2
FEATURE [Part::MultiFuse] Fusion080  label="removeToCreteHoleForPlugHousing025"
  Placement = pos=(-42,19,36) rot=(0,1,0;1.5708rad)
  Shapes = -> [Cylinder037,Cylinder036]
FEATURE [Sketcher::SketchObject] Sketch050  label="topSketch012"
  FullyConstrained = true
  sketch-geometry (4):
    g0: LineSegment StartX=16.8446 StartY=31.512 StartZ=0 EndX=16.3251 EndY=34.4666 EndZ=0
    g1: ArcOfCircle CenterX=19 CenterY=19.2524 CenterZ=0 NormalX=0 NormalY=0 NormalZ=1 AngleXU=0 Radius=15.4476 StartAngle=1.74483 EndAngle=2.72717
    g2: ArcOfCircle CenterX=19 CenterY=19.2524 CenterZ=0 NormalX=0 NormalY=0 NormalZ=1 AngleXU=0 Radius=12.4476 StartAngle=1.74483 EndAngle=2.73189
    g3: LineSegment StartX=4.86004 StartY=25.4725 StartZ=0 EndX=7.58253 EndY=24.2107 EndZ=0
  constraints (7):
    c: Block(g0)
    c: Coincident(g1,g0)
    c: Coincident(g2,g0)
    c: Coincident(g3,g1)
    c: Coincident(g3,g2)
    c: Block(g1)
    c: Block(g2)
FEATURE [Part::Extrusion] Extrude041
  Base = -> Sketch050
  Dir = (0,0,1)
  DirMode = 2
  FaceMakerClass = Part::FaceMakerBullseye
  LengthFwd = 10.6
  LengthRev = 0
  Placement = pos=(0,0,31) rot=(0,0,1;0rad)
  Solid = true
  Symmetric = false
FEATURE [Part::Cut] Cut035
  Base = -> Extrude041
  Placement = pos=(0,0,-0.3) rot=(0,0,1;0rad)
  Tool = -> Fusion080
FEATURE [Part::Cut] Cut036
  Base = -> Box023
  Tool = -> Cut035
FEATURE [Part::Fillet] Fillet027
  Base = -> Cut036
  Edges = 1 edges r=0.7: [Edge13]
FEATURE [Part::Fillet] Fillet028
  Base = -> Fillet027
  Edges = 1 edges r=0.7: [Edge13]
FEATURE [Part::Fillet] Fillet029
  Base = -> Fillet028
  Edges = 1 edges r=0.7: [Edge16]
FEATURE [Part::Fillet] Fillet030
  Base = -> Fillet029
  Edges = 1 edges r=0.7: [Edge11]
FEATURE [Part::Fillet] Fillet031
  Base = -> Fillet030
  Edges = 1 edges r=0.7: [Edge10]
FEATURE [Part::Fillet] Fillet032
  Base = -> Fillet031
  Edges = 1 edges r=1.2: [Edge5]
FEATURE [Part::Fillet] Fillet033
  Base = -> Fillet032
  Edges = 1 edges r=1.2: [Edge12]
FEATURE [Part::Fillet] Fillet034  label="wireHousingRetainer"
  Base = -> Fillet033
  Edges = 1 edges r=2: [Edge1]
  Placement = pos=(0.3,0,0) rot=(0,0,1;0rad)
FEATURE [Part::Feature] Face099
  shape: bbox 3.5 x 17.8 x 2e-07 mm, 1 faces, 0 solids (baked)
FEATURE [Part::Revolution] Revolve107  label="removeToCreateScrewAndThreadedInsertHole034"
  Angle = 360
  Axis = (0,1,0)
  Base = (0,0,0)
  FaceMakerClass = Part::FaceMakerBullseye
  Placement = pos=(12.5,0,10) rot=(0,0,1;0rad)
  Solid = false
  Source = -> Face099
  Symmetric = false
FEATURE [Part::Feature] Face100
  shape: bbox 3.5 x 17.8 x 2e-07 mm, 1 faces, 0 solids (baked)
FEATURE [Part::Revolution] Revolve108  label="removeToCreateScrewAndThreadedInsertHole035"
  Angle = 360
  Axis = (0,1,0)
  Base = (0,0,0)
  FaceMakerClass = Part::FaceMakerBullseye
  Placement = pos=(12.5,0,62) rot=(0,0,1;0rad)
  Solid = false
  Source = -> Face100
  Symmetric = false
FEATURE [Part::Feature] Face101
  shape: bbox 3.5 x 17.8 x 2e-07 mm, 1 faces, 0 solids (baked)
FEATURE [Part::Revolution] Revolve109  label="removeToCreateScrewAndThreadedInsertHole036"
  Angle = 360
  Axis = (0,1,0)
  Base = (0,0,0)
  FaceMakerClass = Part::FaceMakerBullseye
  Placement = pos=(89.5,0,68.5) rot=(0,0,1;0rad)
  Solid = false
  Source = -> Face101
  Symmetric = false
FEATURE [Part::Feature] Face102
  shape: bbox 3.5 x 17.8 x 2e-07 mm, 1 faces, 0 solids (baked)
FEATURE [Part::Revolution] Revolve110  label="removeToCreateScrewAndThreadedInsertHole037"
  Angle = 360
  Axis = (0,1,0)
  Base = (0,0,0)
  FaceMakerClass = Part::FaceMakerBullseye
  Placement = pos=(89.5,0,3.5) rot=(0,0,1;0rad)
  Solid = false
  Source = -> Face102
  Symmetric = false
FEATURE [Part::Feature] Face103
  shape: bbox 3.5 x 17.8 x 2e-07 mm, 1 faces, 0 solids (baked)
FEATURE [Part::Revolution] Revolve111  label="removeToCreateScrewAndThreadedInsertHole038"
  Angle = 360
  Axis = (0,1,0)
  Base = (0,0,0)
  FaceMakerClass = Part::FaceMakerBullseye
  Placement = pos=(109.5,4.7,3.5) rot=(0,0,1;0rad)
  Solid = false
  Source = -> Face103
  Symmetric = false
FEATURE [Part::Feature] Face104
  shape: bbox 3.5 x 17.8 x 2e-07 mm, 1 faces, 0 solids (baked)
FEATURE [Part::Revolution] Revolve112  label="removeToCreateScrewAndThreadedInsertHole039"
  Angle = 360
  Axis = (0,1,0)
  Base = (0,0,0)
  FaceMakerClass = Part::FaceMakerBullseye
  Placement = pos=(109.5,4.7,68.5) rot=(0,0,1;0rad)
  Solid = false
  Source = -> Face104
  Symmetric = false
FEATURE [Part::MultiFuse] Fusion081  label="removeToCreateScrewAndThreadedInsertHole040"
  Shapes = -> [Revolve107,Revolve108,Revolve109,Revolve110,Revolve111,Revolve112]
FEATURE [Part::MultiFuse] Fusion082  label="casePillars002"
  Shapes = -> [Revolve094,Revolve092,Revolve090,Revolve089,Revolve091,Revolve093]
FEATURE [Part::Cut] Cut037  label="casePillars003"
  Base = -> Fusion082
  Tool = -> Fusion081
FEATURE [Sketcher::SketchObject] Sketch051
  FullyConstrained = true
  Placement = pos=(117,19,0) rot=(0.57735,0.57735,0.57735;2.0944rad)
  sketch-geometry (48):
    g0: LineSegment StartX=-49.19 StartY=69.25 StartZ=0 EndX=-49.19 EndY=66.25 EndZ=0
    g1: LineSegment StartX=-49.19 StartY=63.5 StartZ=0 EndX=-49.19 EndY=60.5 EndZ=0
    g2: LineSegment StartX=-49.19 StartY=57.75 StartZ=0 EndX=-49.19 EndY=54.75 EndZ=0
    g3: LineSegment StartX=-49.19 StartY=52 StartZ=0 EndX=-49.19 EndY=49 EndZ=0
    g4: LineSegment StartX=-49.19 StartY=46.25 StartZ=0 EndX=-49.19 EndY=43.25 EndZ=0
    g5: LineSegment StartX=-49.19 StartY=40.5 StartZ=0 EndX=-49.19 EndY=37.5 EndZ=0
    g6: LineSegment StartX=-49.19 StartY=34.5 StartZ=0 EndX=-49.19 EndY=31.5 EndZ=0
    g7: LineSegment StartX=-49.19 StartY=28.75 StartZ=0 EndX=-49.19 EndY=25.75 EndZ=0
    g8: LineSegment StartX=-49.19 StartY=23 StartZ=0 EndX=-49.19 EndY=20 EndZ=0
    g9: LineSegment StartX=-49.19 StartY=17.25 StartZ=0 EndX=-49.19 EndY=14.25 EndZ=0
    g10: LineSegment StartX=-49.19 StartY=11.5 StartZ=0 EndX=-49.19 EndY=8.5 EndZ=0
    g11: LineSegment StartX=-49.19 StartY=5.75 StartZ=0 EndX=-49.19 EndY=2.75 EndZ=0
    g12: ArcOfCircle CenterX=-1.5 CenterY=67.75 CenterZ=0 NormalX=0 NormalY=0 NormalZ=1 AngleXU=0 Radius=1.5 StartAngle=4.71239 EndAngle=7.85398
    g13: ArcOfCircle CenterX=-1.5 CenterY=62 CenterZ=0 NormalX=0 NormalY=0 NormalZ=1 AngleXU=0 Radius=1.5 StartAngle=4.71239 EndAngle=7.85398
    g14: ArcOfCircle CenterX=-1.5 CenterY=56.25 CenterZ=0 NormalX=0 NormalY=0 NormalZ=1 AngleXU=0 Radius=1.5 StartAngle=4.71239 EndAngle=7.85398
    g15: ArcOfCircle CenterX=-11.49 CenterY=50.5 CenterZ=0 NormalX=0 NormalY=0 NormalZ=1 AngleXU=0 Radius=1.5 StartAngle=4.71239 EndAngle=7.85398
    g16: ArcOfCircle CenterX=-16.28 CenterY=44.75 CenterZ=0 NormalX=0 NormalY=0 NormalZ=1 AngleXU=0 Radius=1.5 StartAngle=4.71239 EndAngle=7.85398
    g17: ArcOfCircle CenterX=-18.2337 CenterY=39 CenterZ=0 NormalX=0 NormalY=0 NormalZ=1 AngleXU=0 Radius=1.5 StartAngle=4.71485 EndAngle=7.85398
    g18: ArcOfCircle CenterX=-16.2837 CenterY=27.25 CenterZ=0 NormalX=0 NormalY=0 NormalZ=1 AngleXU=0 Radius=1.5 StartAngle=4.71485 EndAngle=7.85398
    g19: ArcOfCircle CenterX=-18.2337 CenterY=33 CenterZ=0 NormalX=0 NormalY=0 NormalZ=1 AngleXU=0 Radius=1.5 StartAngle=4.71485 EndAngle=7.85398
    g20: ArcOfCircle CenterX=-11.49 CenterY=21.5 CenterZ=0 NormalX=0 NormalY=0 NormalZ=1 AngleXU=0 Radius=1.5 StartAngle=4.71239 EndAngle=7.85398
    g21: ArcOfCircle CenterX=-1.5 CenterY=4.25 CenterZ=0 NormalX=0 NormalY=0 NormalZ=1 AngleXU=0 Radius=1.5 StartAngle=4.71239 EndAngle=7.85398
    g22: ArcOfCircle CenterX=-1.5 CenterY=10 CenterZ=0 NormalX=0 NormalY=0 NormalZ=1 AngleXU=0 Radius=1.5 StartAngle=4.71239 EndAngle=7.85398
    g23: ArcOfCircle CenterX=-1.5 CenterY=15.75 CenterZ=0 NormalX=0 NormalY=0 NormalZ=1 AngleXU=0 Radius=1.5 StartAngle=4.71239 EndAngle=7.85398
    g24: LineSegment StartX=-49.19 StartY=69.25 StartZ=0 EndX=-1.5 EndY=69.25 EndZ=0
    g25: LineSegment StartX=-49.19 StartY=66.25 StartZ=0 EndX=-1.5 EndY=66.25 EndZ=0
    g26: LineSegment StartX=-49.19 StartY=63.5 StartZ=0 EndX=-1.5 EndY=63.5 EndZ=0
    g27: LineSegment StartX=-49.19 StartY=60.5 StartZ=0 EndX=-1.5 EndY=60.5 EndZ=0
    g28: LineSegment StartX=-49.19 StartY=57.75 StartZ=0 EndX=-1.5 EndY=57.75 EndZ=0
    g29: LineSegment StartX=-49.19 StartY=54.75 StartZ=0 EndX=-1.5 EndY=54.75 EndZ=0
    g30: LineSegment StartX=-49.19 StartY=52 StartZ=0 EndX=-11.49 EndY=52 EndZ=0
    g31: LineSegment StartX=-49.19 StartY=49 StartZ=0 EndX=-11.49 EndY=49 EndZ=0
    g32: LineSegment StartX=-49.19 StartY=46.25 StartZ=0 EndX=-16.28 EndY=46.25 EndZ=0
    g33: LineSegment StartX=-49.19 StartY=43.25 StartZ=0 EndX=-16.28 EndY=43.25 EndZ=0
    g34: LineSegment StartX=-49.19 StartY=40.5 StartZ=0 EndX=-18.2337 EndY=40.5 EndZ=0
    g35: LineSegment StartX=-49.19 StartY=37.5 StartZ=0 EndX=-18.23 EndY=37.5 EndZ=0
    g36: LineSegment StartX=-49.19 StartY=34.5 StartZ=0 EndX=-18.2337 EndY=34.5 EndZ=0
    g37: LineSegment StartX=-49.19 StartY=31.5 StartZ=0 EndX=-18.23 EndY=31.5 EndZ=0
    g38: LineSegment StartX=-49.19 StartY=28.75 StartZ=0 EndX=-16.2837 EndY=28.75 EndZ=0
    g39: LineSegment StartX=-49.19 StartY=25.75 StartZ=0 EndX=-16.28 EndY=25.75 EndZ=0
    g40: LineSegment StartX=-49.19 StartY=23 StartZ=0 EndX=-11.49 EndY=23 EndZ=0
    g41: LineSegment StartX=-49.19 StartY=20 StartZ=0 EndX=-11.49 EndY=20 EndZ=0
    g42: LineSegment StartX=-49.19 StartY=17.25 StartZ=0 EndX=-1.5 EndY=17.25 EndZ=0
    g43: LineSegment StartX=-49.19 StartY=14.25 StartZ=0 EndX=-1.5 EndY=14.25 EndZ=0
    g44: LineSegment StartX=-49.19 StartY=11.5 StartZ=0 EndX=-1.5 EndY=11.5 EndZ=0
    g45: LineSegment StartX=-49.19 StartY=8.5 StartZ=0 EndX=-1.5 EndY=8.5 EndZ=0
    g46: LineSegment StartX=-49.19 StartY=5.75 StartZ=0 EndX=-1.5 EndY=5.75 EndZ=0
    g47: LineSegment StartX=-49.19 StartY=2.75 StartZ=0 EndX=-1.5 EndY=2.75 EndZ=0
  constraints (120):
    c: Vertical(g0)
    c: Distance(g0) = 3
    c: Block(g0)
    c: Vertical(g1)
    c: Distance(g1) = 3
    c: Vertical(g2)
    c: Equal(g0,g2) = 3
    c: Block(g2)
    c: Vertical(g3)
    c: Equal(g1,g3) = 3
    c: Vertical(g4)
    c: Equal(g0,g4) = 3
    c: Block(g4)
    c: Vertical(g5)
    c: Equal(g1,g5) = 3
    c: Vertical(g6)
    c: Equal(g0,g6) = 3
    c: Block(g6)
    c: Vertical(g7)
    c: Equal(g1,g7) = 3
    c: Vertical(g8)
    c: Equal(g0,g8) = 3
    c: Block(g8)
    c: Vertical(g9)
    c: Equal(g1,g9) = 3
    c: Vertical(g10)
    c: Equal(g0,g10) = 3
    c: Block(g10)
    c: Vertical(g11)
    c: Equal(g1,g11) = 3
    c: Block(g12)
    c: Block(g13)
    c: Block(g14)
    c: Block(g15)
    c: Block(g16)
    c: Block(g17)
    c: Block(g18)
    c: Block(g19)
    c: Block(g20)
    c: Block(g21)
    c: Block(g22)
    c: Block(g23)
    c: Block(g11)
    c: Block(g9)
    c: Block(g7)
    c: Block(g5)
    c: Block(g3)
    c: Block(g1)
    c: Coincident(g24,g0)
    c: Coincident(g24,g12)
    c: Horizontal(g24)
    c: Coincident(g25,g0)
    c: Coincident(g25,g12)
    c: Horizontal(g25)
    c: Coincident(g26,g1)
    c: Coincident(g26,g13)
    c: Horizontal(g26)
    c: Coincident(g27,g1)
    c: Coincident(g27,g13)
    c: Horizontal(g27)
    c: Coincident(g28,g2)
    c: Coincident(g28,g14)
    c: Horizontal(g28)
    c: Coincident(g29,g2)
    c: Coincident(g29,g14)
    c: Horizontal(g29)
    c: Coincident(g30,g3)
    c: Coincident(g30,g15)
    c: Horizontal(g30)
    c: Coincident(g31,g3)
    c: Coincident(g31,g15)
    c: Horizontal(g31)
    c: Coincident(g32,g4)
    c: Coincident(g32,g16)
    c: Horizontal(g32)
    c: Coincident(g33,g4)
    c: Coincident(g33,g16)
    c: Horizontal(g33)
    c: Coincident(g34,g5)
    c: Coincident(g34,g17)
    c: Horizontal(g34)
    c: Coincident(g35,g5)
    c: Coincident(g35,g17)
    c: Horizontal(g35)
    c: Coincident(g36,g6)
    c: Coincident(g36,g19)
    c: Horizontal(g36)
    c: Coincident(g37,g6)
    c: Coincident(g37,g19)
    c: Horizontal(g37)
    c: Coincident(g38,g7)
    c: Coincident(g38,g18)
    c: Horizontal(g38)
    c: Coincident(g39,g7)
    c: Coincident(g39,g18)
    c: Horizontal(g39)
    c: Coincident(g40,g8)
    c: Coincident(g40,g20)
    c: Horizontal(g40)
    c: Coincident(g41,g8)
    c: Coincident(g41,g20)
    c: Horizontal(g41)
    c: Coincident(g42,g9)
    c: Coincident(g42,g23)
    c: Horizontal(g42)
    c: Coincident(g43,g9)
    c: Coincident(g43,g23)
    c: Horizontal(g43)
    c: Coincident(g44,g10)
    c: Coincident(g44,g22)
    c: Horizontal(g44)
    c: Coincident(g45,g10)
    c: Coincident(g45,g22)
    c: Horizontal(g45)
    c: Coincident(g46,g11)
    c: Coincident(g46,g21)
    c: Horizontal(g46)
    c: Coincident(g47,g11)
    c: Coincident(g47,g21)
    c: Horizontal(g47)
FEATURE [Part::Extrusion] Extrude042
  Base = -> Sketch051
  Dir = (1,-2e-16,2e-16)
  DirMode = 2
  FaceMakerClass = Part::FaceMakerBullseye
  LengthFwd = 19
  LengthRev = 0
  Placement = pos=(-19,0,0) rot=(0,0,1;0rad)
  Solid = true
  Symmetric = false
FEATURE [Part::Fillet] Fillet035  label="removeToCreateVentalationHoles"
  Base = -> Extrude042
  Edges = <same value as first occurrence — deduplicated (x6 in doc)>
  Placement = pos=(7,0,0) rot=(0,0,1;0rad)
FEATURE [Part::Cut] Cut038  label="top017"
  Base = -> Cut033
  Tool = -> Fillet035
FEATURE [Sketcher::SketchObject] Sketch052  label="bottomSketch001"
  FullyConstrained = true
  sketch-geometry (45):
    g0: LineSegment StartX=6.29999 StartY=8 StartZ=0 EndX=3.29999 EndY=8 EndZ=0
    g1: LineSegment StartX=3.29999 StartY=8 StartZ=0 EndX=3.29999 EndY=-6.03275e-07 EndZ=0
    g2: ArcOfCircle CenterX=8.29999 CenterY=5 CenterZ=0 NormalX=0 NormalY=0 NormalZ=1 AngleXU=0 Radius=2 StartAngle=3.14159 EndAngle=4.71239
    g3: LineSegment StartX=6.29999 StartY=8 StartZ=0 EndX=6.29999 EndY=5 EndZ=0
    g4: ArcOfCircle CenterX=105 CenterY=19 CenterZ=0 NormalX=0 NormalY=0 NormalZ=1 AngleXU=0 Radius=12.7 StartAngle=4.71239 EndAngle=5.94289
    g5-g11: Circle x7 (B-spline internal-alignment scaffolding for g12; pole/knot coordinates omitted)
    g12: BSplineCurve PolesCount=7 KnotsCount=5 Degree=3 IsPeriodic=0
    g13-g17: GeomPoint x5 (B-spline internal-alignment scaffolding for g12; pole/knot coordinates omitted)
    g18: ArcOfCircle CenterX=105 CenterY=19 CenterZ=0 NormalX=0 NormalY=0 NormalZ=1 AngleXU=0 Radius=15.7 StartAngle=5.81226 EndAngle=6.28319
    g19: BSplineCurve PolesCount=5 KnotsCount=3 Degree=3 IsPeriodic=0
    g20: LineSegment StartX=8.29999 StartY=3 StartZ=0 EndX=101.7 EndY=3 EndZ=0
    g21: LineSegment StartX=3.29999 StartY=-6.03275e-07 StartZ=0 EndX=105 EndY=-6.03275e-07 EndZ=0
    g22: LineSegment StartX=120.974 StartY=8.71251 StartZ=0 EndX=122.332 EndY=7.83778 EndZ=0
    g23: LineSegment StartX=105 StartY=-6.03274e-07 StartZ=0 EndX=113 EndY=-6.03274e-07 EndZ=0
    g24: ArcOfCircle CenterX=105 CenterY=19 CenterZ=0 NormalX=0 NormalY=0 NormalZ=1 AngleXU=0 Radius=20.6155 StartAngle=5.11091 EndAngle=5.71103
    g25: ArcOfCircle CenterX=117.7 CenterY=19 CenterZ=0 NormalX=0 NormalY=0 NormalZ=1 AngleXU=0 Radius=3 StartAngle=1.2e-15 EndAngle=2.10468
    g26: Circle CenterX=116.345 CenterY=16.3232 CenterZ=0 NormalX=0 NormalY=0 NormalZ=1 AngleXU=0 Radius=1
    g27: Circle CenterX=117.24 CenterY=15.7584 CenterZ=0 NormalX=0 NormalY=0 NormalZ=1 AngleXU=0 Radius=1
    g28: Circle CenterX=116.972 CenterY=14.7612 CenterZ=0 NormalX=0 NormalY=0 NormalZ=1 AngleXU=0 Radius=1
    g29: BSplineCurve PolesCount=3 KnotsCount=2 Degree=2 IsPeriodic=0
    g30: GeomPoint X=116.345 Y=16.3232 Z=0
    g31: GeomPoint X=116.972 Y=14.7612 Z=0
    g32: Circle CenterX=115.828 CenterY=17.157 CenterZ=0 NormalX=0 NormalY=0 NormalZ=1 AngleXU=0 Radius=1
    g33: Circle CenterX=115.841 CenterY=16.639 CenterZ=0 NormalX=0 NormalY=0 NormalZ=1 AngleXU=0 Radius=1
    g34: Circle CenterX=116.345 CenterY=16.3232 CenterZ=0 NormalX=0 NormalY=0 NormalZ=1 AngleXU=0 Radius=1
    g35: BSplineCurve PolesCount=3 KnotsCount=2 Degree=2 IsPeriodic=0
    g36: GeomPoint X=115.828 Y=17.157 Z=0
    g37: GeomPoint X=116.345 Y=16.3232 Z=0
    g38: LineSegment StartX=115.828 StartY=17.157 StartZ=0 EndX=115.828 EndY=20.8307 EndZ=0
    g39: Circle CenterX=115.828 CenterY=20.8307 CenterZ=0 NormalX=0 NormalY=0 NormalZ=1 AngleXU=0 Radius=1
    g40: Circle CenterX=115.831 CenterY=21.3396 CenterZ=0 NormalX=0 NormalY=0 NormalZ=1 AngleXU=0 Radius=1
    g41: Circle CenterX=116.173 CenterY=21.5825 CenterZ=0 NormalX=0 NormalY=0 NormalZ=1 AngleXU=0 Radius=1
    g42: BSplineCurve PolesCount=3 KnotsCount=2 Degree=2 IsPeriodic=0
    g43: GeomPoint X=115.828 Y=20.8307 Z=0
    g44: GeomPoint X=116.173 Y=21.5825 Z=0
  constraints (70):
    c: Horizontal(g0)
    c: Distance(g0) = 3
    c: Coincident(g1,g0)
    c: Vertical(g1)
    c: Block(g2)
    c: Block(g0)
    c: Coincident(g3,g0)
    c: Coincident(g3,g2)
    c: Vertical(g3)
    c: Block(g1)
    c: Block(g4)
    c: Coincident(g19,g4)
    c: Block(g19)
    c: Equal(g5, g6-g11) x6
    c: InternalAlignment(g5-g11 -> g12) x7
    c: InternalAlignment(g13-g17 -> g12) x5
    c: Block(g12)
    c: Coincident(g18,g12)
    c: Block(g18)
    c: Coincident(g20,g2)
    c: Coincident(g20,g19)
    c: Horizontal(g20)
    c: Distance(g20) = 93.4
    c: Coincident(g21,g1)
    c: Horizontal(g21)
    c: Distance(g21) = 101.7
    c: Horizontal(g23)
    c: Distance(g23) = 8
    c: Coincident(g24,g23)
    c: Block(g23)
    c: Coincident(g22,g24)
    c: Block(g24)
    c: Block(g22)
    c: Distance(g22) = 1.61553
    c: Coincident(g25,g18)
    c: Block(g25)
    c: Weight(g26) = 1
    c: Equal(g26,g27)
    c: Equal(g26,g28)
    c: Coincident(g29,g4)
    c: InternalAlignment(g26,g29)
    c: InternalAlignment(g27,g29)
    c: InternalAlignment(g28,g29)
    c: InternalAlignment(g30,g29)
    c: InternalAlignment(g31,g29)
    c: Block(g29)
    c: Weight(g32) = 1
    c: Equal(g32,g33)
    c: Equal(g32,g34)
    c: Coincident(g35,g29)
    c: InternalAlignment(g32,g35)
    c: InternalAlignment(g33,g35)
    c: InternalAlignment(g34,g35)
    c: InternalAlignment(g36,g35)
    c: InternalAlignment(g37,g35)
    c: Block(g35)
    c: Coincident(g38,g35)
    c: Vertical(g38)
    c: Block(g38)
    c: Coincident(g42,g38)
    c: Weight(g39) = 1
    c: Equal(g39,g40)
    c: Equal(g39,g41)
    c: Coincident(g42,g25)
    c: InternalAlignment(g39,g42)
    c: InternalAlignment(g40,g42)
    c: InternalAlignment(g41,g42)
    c: InternalAlignment(g43,g42)
    c: InternalAlignment(g44,g42)
    c: Block(g42)
FEATURE [Part::Extrusion] Extrude043  label="bottom010"
  Base = -> Sketch052
  Dir = (0,0,1)
  DirMode = 2
  FaceMakerClass = Part::FaceMakerBullseye
  LengthFwd = 71.4
  LengthRev = 0
  Placement = pos=(0,0,0.3) rot=(0,0,1;0rad)
  Solid = true
  Symmetric = false
FEATURE [Sketcher::SketchObject] Sketch053  label="topSketch013"
  FullyConstrained = true
  sketch-geometry (22):
    g0: LineSegment StartX=5.21097e-06 StartY=3 StartZ=0 EndX=5.21097e-06 EndY=19 EndZ=0
    g1: ArcOfCircle CenterX=19 CenterY=19 CenterZ=0 NormalX=0 NormalY=0 NormalZ=1 AngleXU=0 Radius=19 StartAngle=1.5708 EndAngle=3.14159
    g2: ArcOfCircle CenterX=19 CenterY=19 CenterZ=0 NormalX=0 NormalY=0 NormalZ=1 AngleXU=0 Radius=16 StartAngle=1.5708 EndAngle=3.14159
    g3: LineSegment StartX=114 StartY=35 StartZ=0 EndX=19 EndY=35 EndZ=0
    g4: LineSegment StartX=5.21097e-06 StartY=3 StartZ=0 EndX=5.21097e-06 EndY=0 EndZ=0
    g5: LineSegment StartX=3 StartY=0 StartZ=0 EndX=5.21097e-06 EndY=0 EndZ=0
    g6: LineSegment StartX=3 StartY=19 StartZ=0 EndX=3 EndY=0 EndZ=0
    g7: LineSegment StartX=19 StartY=38 StartZ=0 EndX=124 EndY=38 EndZ=0
    g8: Circle CenterX=119 CenterY=35 CenterZ=0 NormalX=0 NormalY=0 NormalZ=1 AngleXU=0 Radius=1
    g9: Circle CenterX=121 CenterY=35 CenterZ=0 NormalX=0 NormalY=0 NormalZ=1 AngleXU=0 Radius=1
    g10: Circle CenterX=121 CenterY=33 CenterZ=0 NormalX=0 NormalY=0 NormalZ=1 AngleXU=0 Radius=1
    g11: BSplineCurve PolesCount=3 KnotsCount=2 Degree=2 IsPeriodic=0
    g12: GeomPoint X=119 Y=35 Z=0
    g13: GeomPoint X=121 Y=33 Z=0
    g14: LineSegment StartX=119 StartY=35 StartZ=0 EndX=114 EndY=35 EndZ=0
    g15: ArcOfCircle CenterX=105 CenterY=19 CenterZ=0 NormalX=0 NormalY=0 NormalZ=1 AngleXU=0 Radius=16 StartAngle=5.60905 EndAngle=6.28319
    g16: LineSegment StartX=121 StartY=33 StartZ=0 EndX=121 EndY=19 EndZ=0
    g17: LineSegment StartX=117.5 StartY=9.01251 StartZ=0 EndX=121.163 EndY=9.0125 EndZ=0
    g18: ArcOfCircle CenterX=105 CenterY=19 CenterZ=0 NormalX=0 NormalY=0 NormalZ=1 AngleXU=0 Radius=20.6155 StartAngle=5.7297 EndAngle=6.28319
    g19: LineSegment StartX=121.163 StartY=9.0125 StartZ=0 EndX=122.538 EndY=8.16329 EndZ=0
    g20: LineSegment StartX=124 StartY=38 StartZ=0 EndX=125.616 EndY=38 EndZ=0
    g21: LineSegment StartX=125.616 StartY=19 StartZ=0 EndX=125.616 EndY=38 EndZ=0
  constraints (50):
    c: Vertical(g0)
    c: Block(g0)
    c: Coincident(g1,g0)
    c: Block(g1)
    c: Coincident(g2,g1)
    c: Block(g2)
    c: Coincident(g3,g2)
    c: Horizontal(g3)
    c: Tangent(g3,g2)
    c: Coincident(g4,g0)
    c: Distance(g4) = 3
    c: Vertical(g4)
    c: Coincident(g5,g4)
    c: Horizontal(g5)
    c: Coincident(g6,g2)
    c: Coincident(g6,g5)
    c: Vertical(g6)
    c: Horizontal(g7)
    c: Distance(g7) = 105
    c: Coincident(g7,g1)
    c: Block(g3)
    c: Weight(g8) = 1
    c: Equal(g8,g9)
    c: Equal(g8,g10)
    c: InternalAlignment(g8,g11)
    c: InternalAlignment(g9,g11)
    c: InternalAlignment(g10,g11)
    c: InternalAlignment(g12,g11)
    c: InternalAlignment(g13,g11)
    c: Block(g11)
    c: Coincident(g14,g11)
    c: Coincident(g14,g3)
    c: Horizontal(g14)
    c: Block(g15)
    c: Coincident(g16,g11)
    c: Coincident(g16,g15)
    c: Vertical(g16)
    c: Distance(g16) = 14
    c: Coincident(g17,g15)
    c: Block(g18)
    c: Coincident(g19,g18)
    c: Coincident(g20,g7)
    c: Horizontal(g20)
    c: Vertical(g21)
    c: Coincident(g20,g21)
    c: Block(g20)
    c: Block(g21)
    c: Block(g19)
    c: Block(g17)
    c: Distance(g20) = 1.61553
FEATURE [Part::Extrusion] Extrude044
  Base = -> Sketch053
  Dir = (0,0,1)
  DirMode = 2
  FaceMakerClass = Part::FaceMakerBullseye
  LengthFwd = 72
  LengthRev = 0
  Solid = true
  Symmetric = false
FEATURE [Part::Fillet] Fillet036  label="top018"
  Base = -> Extrude044
  Edges = 1 edges r=2: [Edge41]
FEATURE [Sketcher::SketchObject] Sketch054
  FullyConstrained = false
  Placement = pos=(0,0,0) rot=(1,0,0;1.5708rad)
  sketch-geometry (24):
    g0: ArcOfCircle CenterX=-4 CenterY=-10.5 CenterZ=0 NormalX=0 NormalY=0 NormalZ=1 AngleXU=0 Radius=1.5 StartAngle=6e-16 EndAngle=3.14159
    g1: ArcOfCircle CenterX=-34.2 CenterY=-10.5 CenterZ=0 NormalX=0 NormalY=0 NormalZ=1 AngleXU=0 Radius=1.5 StartAngle=0 EndAngle=3.14159
    g2: ArcOfCircle CenterX=-34.2 CenterY=-27.7 CenterZ=0 NormalX=0 NormalY=0 NormalZ=1 AngleXU=0 Radius=1.5 StartAngle=3.14159 EndAngle=6.28319
    g3: ArcOfCircle CenterX=-4 CenterY=-27.7 CenterZ=0 NormalX=0 NormalY=0 NormalZ=1 AngleXU=0 Radius=1.5 StartAngle=3.1416 EndAngle=6.28319
    g4: ArcOfCircle CenterX=-10 CenterY=-4.3 CenterZ=0 NormalX=0 NormalY=0 NormalZ=1 AngleXU=0 Radius=1.5 StartAngle=2e-16 EndAngle=3.14159
    g5: ArcOfCircle CenterX=-16.1 CenterY=-1.8 CenterZ=0 NormalX=0 NormalY=0 NormalZ=1 AngleXU=0 Radius=1.5 StartAngle=5e-16 EndAngle=3.14159
    g6: ArcOfCircle CenterX=-22.1 CenterY=-1.8 CenterZ=0 NormalX=0 NormalY=0 NormalZ=1 AngleXU=0 Radius=1.5 StartAngle=5e-16 EndAngle=3.14159
    g7: ArcOfCircle CenterX=-28.2 CenterY=-4.3 CenterZ=0 NormalX=0 NormalY=0 NormalZ=1 AngleXU=0 Radius=1.5 StartAngle=2e-16 EndAngle=3.14159
    g8: ArcOfCircle CenterX=-10 CenterY=-33.9 CenterZ=0 NormalX=0 NormalY=0 NormalZ=1 AngleXU=0 Radius=1.5 StartAngle=3.14159 EndAngle=6.28319
    g9: ArcOfCircle CenterX=-16.1 CenterY=-36.4 CenterZ=0 NormalX=0 NormalY=0 NormalZ=1 AngleXU=0 Radius=1.5 StartAngle=3.14159 EndAngle=6.28319
    g10: ArcOfCircle CenterX=-22.1 CenterY=-36.4 CenterZ=0 NormalX=0 NormalY=0 NormalZ=1 AngleXU=0 Radius=1.5 StartAngle=3.14159 EndAngle=6.28319
    g11: ArcOfCircle CenterX=-28.2 CenterY=-33.9 CenterZ=0 NormalX=0 NormalY=0 NormalZ=1 AngleXU=0 Radius=1.5 StartAngle=3.14159 EndAngle=6.28319
    g12: LineSegment StartX=-35.7 StartY=-10.5 StartZ=0 EndX=-35.7 EndY=-27.7 EndZ=0
    g13: LineSegment StartX=-32.7 StartY=-10.5 StartZ=0 EndX=-32.7 EndY=-27.7 EndZ=0
    g14: LineSegment StartX=-29.7 StartY=-33.9 StartZ=0 EndX=-29.7 EndY=-4.3 EndZ=0
    g15: LineSegment StartX=-26.7 StartY=-33.9 StartZ=0 EndX=-26.7 EndY=-4.3 EndZ=0
    g16: LineSegment StartX=-2.5 StartY=-10.5 StartZ=0 EndX=-2.5 EndY=-27.7 EndZ=0
    g17: LineSegment StartX=-8.5 StartY=-4.3 StartZ=0 EndX=-8.5 EndY=-33.9 EndZ=0
    g18: LineSegment StartX=-5.5 StartY=-10.5 StartZ=0 EndX=-5.5 EndY=-27.7 EndZ=0
    g19: LineSegment StartX=-11.5 StartY=-4.3 StartZ=0 EndX=-11.5 EndY=-33.9 EndZ=0
    g20: LineSegment StartX=-14.6 StartY=-1.8 StartZ=0 EndX=-14.6 EndY=-36.4 EndZ=0
    g21: LineSegment StartX=-17.6 StartY=-1.8 StartZ=0 EndX=-17.6 EndY=-36.4 EndZ=0
    g22: LineSegment StartX=-20.6 StartY=-36.4 StartZ=0 EndX=-20.6 EndY=-1.8 EndZ=0
    g23: LineSegment StartX=-23.6 StartY=-1.8 StartZ=0 EndX=-23.6 EndY=-36.4 EndZ=0
  constraints (48):
    c: Block(g0)
    c: Block(g1)
    c: Block(g2)
    c: Block(g3)
    c: Block(g4)
    c: Block(g5)
    c: Block(g6)
    c: Block(g7)
    c: Block(g8)
    c: Block(g9)
    c: Block(g10)
    c: Block(g11)
    c: Coincident(g12,g1)
    c: Coincident(g12,g2)
    c: Vertical(g12)
    c: Coincident(g13,g1)
    c: Coincident(g13,g2)
    c: Vertical(g13)
    c: Coincident(g14,g11)
    c: Coincident(g14,g7)
    c: Vertical(g14)
    c: Coincident(g15,g11)
    c: Coincident(g15,g7)
    c: Vertical(g15)
    c: Coincident(g16,g0)
    c: Coincident(g16,g3)
    c: Vertical(g16)
    c: Coincident(g17,g4)
    c: Coincident(g17,g8)
    c: Vertical(g17)
    c: Coincident(g18,g0)
    c: Coincident(g18,g3)
    c: Vertical(g18)
    c: Coincident(g19,g4)
    c: Coincident(g19,g8)
    c: Vertical(g19)
    c: Coincident(g20,g5)
    c: Coincident(g20,g9)
    c: Vertical(g20)
    c: Coincident(g21,g5)
    c: Coincident(g21,g9)
    c: Vertical(g21)
    c: Coincident(g22,g10)
    c: Coincident(g22,g6)
    c: Vertical(g22)
    c: Coincident(g23,g6)
    c: Coincident(g23,g10)
    c: Vertical(g23)
FEATURE [Part::Extrusion] Extrude045  label="removeToCreateFanGrillHoles003"
  Base = -> Sketch054
  Dir = (0,-1,6e-16)
  DirMode = 2
  FaceMakerClass = Part::FaceMakerBullseye
  LengthFwd = 10
  LengthRev = 0
  Placement = pos=(65.4,44,54.82) rot=(0,0,1;0rad)
  Solid = true
  Symmetric = false
FEATURE [Part::Feature] Face105 .. Face108  x4 (patterned run collapsed; names and placements below)
  shape: bbox 3.5 x 17.8 x 2e-07 mm, 1 faces, 0 solids (baked)
FEATURE [Part::Revolution] Revolve113  label="removeToCreateScrewAndThreadedInsertHole041"
  Angle = 360
  Axis = (0,1,0)
  Base = (0,0,0)
  FaceMakerClass = Part::FaceMakerBullseye
  Placement = pos=(62.3,30.3,19.7) rot=(0,0,1;0rad)
  Solid = false
  Source = -> Face105
  Symmetric = false
FEATURE [Part::Revolution] Revolve114  label="removeToCreateScrewAndThreadedInsertHole042"
  Angle = 360
  Axis = (0,1,0)
  Base = (0,0,0)
  FaceMakerClass = Part::FaceMakerBullseye
  Placement = pos=(62.3,30.3,51.7) rot=(0,0,1;0rad)
  Solid = false
  Source = -> Face106
  Symmetric = false
FEATURE [Part::Revolution] Revolve115  label="removeToCreateScrewAndThreadedInsertHole043"
  Angle = 360
  Axis = (0,1,0)
  Base = (0,0,0)
  FaceMakerClass = Part::FaceMakerBullseye
  Placement = pos=(30.3,30.3,19.7) rot=(0,0,1;0rad)
  Solid = false
  Source = -> Face107
  Symmetric = false
FEATURE [Part::Revolution] Revolve116  label="removeToCreateScrewAndThreadedInsertHole044"
  Angle = 360
  Axis = (0,1,0)
  Base = (0,0,0)
  FaceMakerClass = Part::FaceMakerBullseye
  Placement = pos=(30.3,30.3,51.7) rot=(0,0,1;0rad)
  Solid = false
  Source = -> Face108
  Symmetric = false
FEATURE [Part::MultiFuse] Fusion083  label="createThreadedInsertHolesForFan004"
  Shapes = -> [Revolve113,Revolve114,Revolve115,Revolve116]
FEATURE [Part::Box] Box024  label="removeToCreteHoleForPlugHousing026"
  AttacherType = Attacher::AttachEngine3D
  Height = 28.6
  Length = 10
  Placement = pos=(-2,0,21.7) rot=(0,0,1;0rad)
  Width = 19
FEATURE [Part::Cylinder] Cylinder038  label="removeToCreteHoleForPlugHousing027"
  Angle = 360
  AttacherType = Attacher::AttachEngine3D
  Height = 20
  Placement = pos=(-2,19,36) rot=(0,1,0;1.5708rad)
  Radius = 14.3
FEATURE [Part::MultiFuse] Fusion084  label="removeToCreteHoleForPlugHousing028"
  Shapes = -> [Box024,Cylinder038]
FEATURE [Part::Cylinder] Cylinder039
  Angle = 360
  AttacherType = Attacher::AttachEngine3D
  Height = 20
  Placement = pos=(0,0,36.15) rot=(0,0,1;0rad)
  Radius = 14.3
FEATURE [Part::Cylinder] Cylinder040
  Angle = 360
  AttacherType = Attacher::AttachEngine3D
  Height = 10
  Placement = pos=(0,0,36.15) rot=(0,0,1;0rad)
  Radius = 4
FEATURE [Part::Box] Box025  label="removeToCreteHoleForPlugHousing030"
  AttacherType = Attacher::AttachEngine3D
  Height = 28.6
  Length = 20
  Placement = pos=(106.15,0,21.7) rot=(0,0,1;0rad)
  Width = 19
FEATURE [Part::MultiFuse] Fusion086  label="removeToCreteHoleForPlugHousing031"
  Placement = pos=(70,19,36) rot=(0,1,0;1.5708rad)
  Shapes = -> [Cylinder039,Cylinder040]
FEATURE [Part::MultiFuse] Fusion085  label="removeToCreteHoleForPlugHousing029"
  Shapes = -> [Box025,Fusion086]
FEATURE [Sketcher::SketchObject] Sketch055
  FullyConstrained = true
  Placement = pos=(117,19,0) rot=(0.57735,0.57735,0.57735;2.0944rad)
  sketch-geometry (48):
    g0: LineSegment StartX=-49.19 StartY=69.25 StartZ=0 EndX=-49.19 EndY=66.25 EndZ=0
    g1: LineSegment StartX=-49.19 StartY=63.5 StartZ=0 EndX=-49.19 EndY=60.5 EndZ=0
    g2: LineSegment StartX=-49.19 StartY=57.75 StartZ=0 EndX=-49.19 EndY=54.75 EndZ=0
    g3: LineSegment StartX=-49.19 StartY=52 StartZ=0 EndX=-49.19 EndY=49 EndZ=0
    g4: LineSegment StartX=-49.19 StartY=46.25 StartZ=0 EndX=-49.19 EndY=43.25 EndZ=0
    g5: LineSegment StartX=-49.19 StartY=40.5 StartZ=0 EndX=-49.19 EndY=37.5 EndZ=0
    g6: LineSegment StartX=-49.19 StartY=34.5 StartZ=0 EndX=-49.19 EndY=31.5 EndZ=0
    g7: LineSegment StartX=-49.19 StartY=28.75 StartZ=0 EndX=-49.19 EndY=25.75 EndZ=0
    g8: LineSegment StartX=-49.19 StartY=23 StartZ=0 EndX=-49.19 EndY=20 EndZ=0
    g9: LineSegment StartX=-49.19 StartY=17.25 StartZ=0 EndX=-49.19 EndY=14.25 EndZ=0
    g10: LineSegment StartX=-49.19 StartY=11.5 StartZ=0 EndX=-49.19 EndY=8.5 EndZ=0
    g11: LineSegment StartX=-49.19 StartY=5.75 StartZ=0 EndX=-49.19 EndY=2.75 EndZ=0
    g12: ArcOfCircle CenterX=-1.5 CenterY=67.75 CenterZ=0 NormalX=0 NormalY=0 NormalZ=1 AngleXU=0 Radius=1.5 StartAngle=4.71239 EndAngle=7.85398
    g13: ArcOfCircle CenterX=-1.5 CenterY=62 CenterZ=0 NormalX=0 NormalY=0 NormalZ=1 AngleXU=0 Radius=1.5 StartAngle=4.71239 EndAngle=7.85398
    g14: ArcOfCircle CenterX=-1.5 CenterY=56.25 CenterZ=0 NormalX=0 NormalY=0 NormalZ=1 AngleXU=0 Radius=1.5 StartAngle=4.71239 EndAngle=7.85398
    g15: ArcOfCircle CenterX=-11.49 CenterY=50.5 CenterZ=0 NormalX=0 NormalY=0 NormalZ=1 AngleXU=0 Radius=1.5 StartAngle=4.71239 EndAngle=7.85398
    g16: ArcOfCircle CenterX=-16.28 CenterY=44.75 CenterZ=0 NormalX=0 NormalY=0 NormalZ=1 AngleXU=0 Radius=1.5 StartAngle=4.71239 EndAngle=7.85398
    g17: ArcOfCircle CenterX=-18.2337 CenterY=39 CenterZ=0 NormalX=0 NormalY=0 NormalZ=1 AngleXU=0 Radius=1.5 StartAngle=4.71485 EndAngle=7.85398
    g18: ArcOfCircle CenterX=-16.2837 CenterY=27.25 CenterZ=0 NormalX=0 NormalY=0 NormalZ=1 AngleXU=0 Radius=1.5 StartAngle=4.71485 EndAngle=7.85398
    g19: ArcOfCircle CenterX=-18.2337 CenterY=33 CenterZ=0 NormalX=0 NormalY=0 NormalZ=1 AngleXU=0 Radius=1.5 StartAngle=4.71485 EndAngle=7.85398
    g20: ArcOfCircle CenterX=-11.49 CenterY=21.5 CenterZ=0 NormalX=0 NormalY=0 NormalZ=1 AngleXU=0 Radius=1.5 StartAngle=4.71239 EndAngle=7.85398
    g21: ArcOfCircle CenterX=-1.5 CenterY=4.25 CenterZ=0 NormalX=0 NormalY=0 NormalZ=1 AngleXU=0 Radius=1.5 StartAngle=4.71239 EndAngle=7.85398
    g22: ArcOfCircle CenterX=-1.5 CenterY=10 CenterZ=0 NormalX=0 NormalY=0 NormalZ=1 AngleXU=0 Radius=1.5 StartAngle=4.71239 EndAngle=7.85398
    g23: ArcOfCircle CenterX=-1.5 CenterY=15.75 CenterZ=0 NormalX=0 NormalY=0 NormalZ=1 AngleXU=0 Radius=1.5 StartAngle=4.71239 EndAngle=7.85398
    g24: LineSegment StartX=-49.19 StartY=69.25 StartZ=0 EndX=-1.5 EndY=69.25 EndZ=0
    g25: LineSegment StartX=-49.19 StartY=66.25 StartZ=0 EndX=-1.5 EndY=66.25 EndZ=0
    g26: LineSegment StartX=-49.19 StartY=63.5 StartZ=0 EndX=-1.5 EndY=63.5 EndZ=0
    g27: LineSegment StartX=-49.19 StartY=60.5 StartZ=0 EndX=-1.5 EndY=60.5 EndZ=0
    g28: LineSegment StartX=-49.19 StartY=57.75 StartZ=0 EndX=-1.5 EndY=57.75 EndZ=0
    g29: LineSegment StartX=-49.19 StartY=54.75 StartZ=0 EndX=-1.5 EndY=54.75 EndZ=0
    g30: LineSegment StartX=-49.19 StartY=52 StartZ=0 EndX=-11.49 EndY=52 EndZ=0
    g31: LineSegment StartX=-49.19 StartY=49 StartZ=0 EndX=-11.49 EndY=49 EndZ=0
    g32: LineSegment StartX=-49.19 StartY=46.25 StartZ=0 EndX=-16.28 EndY=46.25 EndZ=0
    g33: LineSegment StartX=-49.19 StartY=43.25 StartZ=0 EndX=-16.28 EndY=43.25 EndZ=0
    g34: LineSegment StartX=-49.19 StartY=40.5 StartZ=0 EndX=-18.2337 EndY=40.5 EndZ=0
    g35: LineSegment StartX=-49.19 StartY=37.5 StartZ=0 EndX=-18.23 EndY=37.5 EndZ=0
    g36: LineSegment StartX=-49.19 StartY=34.5 StartZ=0 EndX=-18.2337 EndY=34.5 EndZ=0
    g37: LineSegment StartX=-49.19 StartY=31.5 StartZ=0 EndX=-18.23 EndY=31.5 EndZ=0
    g38: LineSegment StartX=-49.19 StartY=28.75 StartZ=0 EndX=-16.2837 EndY=28.75 EndZ=0
    g39: LineSegment StartX=-49.19 StartY=25.75 StartZ=0 EndX=-16.28 EndY=25.75 EndZ=0
    g40: LineSegment StartX=-49.19 StartY=23 StartZ=0 EndX=-11.49 EndY=23 EndZ=0
    g41: LineSegment StartX=-49.19 StartY=20 StartZ=0 EndX=-11.49 EndY=20 EndZ=0
    g42: LineSegment StartX=-49.19 StartY=17.25 StartZ=0 EndX=-1.5 EndY=17.25 EndZ=0
    g43: LineSegment StartX=-49.19 StartY=14.25 StartZ=0 EndX=-1.5 EndY=14.25 EndZ=0
    g44: LineSegment StartX=-49.19 StartY=11.5 StartZ=0 EndX=-1.5 EndY=11.5 EndZ=0
    g45: LineSegment StartX=-49.19 StartY=8.5 StartZ=0 EndX=-1.5 EndY=8.5 EndZ=0
    g46: LineSegment StartX=-49.19 StartY=5.75 StartZ=0 EndX=-1.5 EndY=5.75 EndZ=0
    g47: LineSegment StartX=-49.19 StartY=2.75 StartZ=0 EndX=-1.5 EndY=2.75 EndZ=0
  constraints (120):
    c: Vertical(g0)
    c: Distance(g0) = 3
    c: Block(g0)
    c: Vertical(g1)
    c: Distance(g1) = 3
    c: Vertical(g2)
    c: Equal(g0,g2) = 3
    c: Block(g2)
    c: Vertical(g3)
    c: Equal(g1,g3) = 3
    c: Vertical(g4)
    c: Equal(g0,g4) = 3
    c: Block(g4)
    c: Vertical(g5)
    c: Equal(g1,g5) = 3
    c: Vertical(g6)
    c: Equal(g0,g6) = 3
    c: Block(g6)
    c: Vertical(g7)
    c: Equal(g1,g7) = 3
    c: Vertical(g8)
    c: Equal(g0,g8) = 3
    c: Block(g8)
    c: Vertical(g9)
    c: Equal(g1,g9) = 3
    c: Vertical(g10)
    c: Equal(g0,g10) = 3
    c: Block(g10)
    c: Vertical(g11)
    c: Equal(g1,g11) = 3
    c: Block(g12)
    c: Block(g13)
    c: Block(g14)
    c: Block(g15)
    c: Block(g16)
    c: Block(g17)
    c: Block(g18)
    c: Block(g19)
    c: Block(g20)
    c: Block(g21)
    c: Block(g22)
    c: Block(g23)
    c: Block(g11)
    c: Block(g9)
    c: Block(g7)
    c: Block(g5)
    c: Block(g3)
    c: Block(g1)
    c: Coincident(g24,g0)
    c: Coincident(g24,g12)
    c: Horizontal(g24)
    c: Coincident(g25,g0)
    c: Coincident(g25,g12)
    c: Horizontal(g25)
    c: Coincident(g26,g1)
    c: Coincident(g26,g13)
    c: Horizontal(g26)
    c: Coincident(g27,g1)
    c: Coincident(g27,g13)
    c: Horizontal(g27)
    c: Coincident(g28,g2)
    c: Coincident(g28,g14)
    c: Horizontal(g28)
    c: Coincident(g29,g2)
    c: Coincident(g29,g14)
    c: Horizontal(g29)
    c: Coincident(g30,g3)
    c: Coincident(g30,g15)
    c: Horizontal(g30)
    c: Coincident(g31,g3)
    c: Coincident(g31,g15)
    c: Horizontal(g31)
    c: Coincident(g32,g4)
    c: Coincident(g32,g16)
    c: Horizontal(g32)
    c: Coincident(g33,g4)
    c: Coincident(g33,g16)
    c: Horizontal(g33)
    c: Coincident(g34,g5)
    c: Coincident(g34,g17)
    c: Horizontal(g34)
    c: Coincident(g35,g5)
    c: Coincident(g35,g17)
    c: Horizontal(g35)
    c: Coincident(g36,g6)
    c: Coincident(g36,g19)
    c: Horizontal(g36)
    c: Coincident(g37,g6)
    c: Coincident(g37,g19)
    c: Horizontal(g37)
    c: Coincident(g38,g7)
    c: Coincident(g38,g18)
    c: Horizontal(g38)
    c: Coincident(g39,g7)
    c: Coincident(g39,g18)
    c: Horizontal(g39)
    c: Coincident(g40,g8)
    c: Coincident(g40,g20)
    c: Horizontal(g40)
    c: Coincident(g41,g8)
    c: Coincident(g41,g20)
    c: Horizontal(g41)
    c: Coincident(g42,g9)
    c: Coincident(g42,g23)
    c: Horizontal(g42)
    c: Coincident(g43,g9)
    c: Coincident(g43,g23)
    c: Horizontal(g43)
    c: Coincident(g44,g10)
    c: Coincident(g44,g22)
    c: Horizontal(g44)
    c: Coincident(g45,g10)
    c: Coincident(g45,g22)
    c: Horizontal(g45)
    c: Coincident(g46,g11)
    c: Coincident(g46,g21)
    c: Horizontal(g46)
    c: Coincident(g47,g11)
    c: Coincident(g47,g21)
    c: Horizontal(g47)
FEATURE [Part::Extrusion] Extrude046
  Base = -> Sketch055
  Dir = (1,0,0)
  DirMode = 2
  FaceMakerClass = Part::FaceMakerBullseye
  LengthFwd = 23
  LengthRev = 0
  Placement = pos=(-19,0,0) rot=(0,0,1;0rad)
  Solid = true
  Symmetric = false
FEATURE [Part::Fillet] Fillet038  label="removeToCreateVentalationHoles001"
  Base = -> Extrude046
  Edges = <same value as first occurrence — deduplicated (x6 in doc)>
  Placement = pos=(7,0,0) rot=(0,0,1;0rad)
FEATURE [Sketcher::SketchObject] Sketch056  label="topSketch014"
  FullyConstrained = true
  sketch-geometry (22):
    g0: LineSegment StartX=5.21097e-06 StartY=3 StartZ=0 EndX=5.21097e-06 EndY=19 EndZ=0
    g1: ArcOfCircle CenterX=19 CenterY=19 CenterZ=0 NormalX=0 NormalY=0 NormalZ=1 AngleXU=0 Radius=19 StartAngle=1.5708 EndAngle=3.14159
    g2: ArcOfCircle CenterX=19 CenterY=19 CenterZ=0 NormalX=0 NormalY=0 NormalZ=1 AngleXU=0 Radius=16 StartAngle=1.5708 EndAngle=3.14159
    g3: LineSegment StartX=114 StartY=35 StartZ=0 EndX=19 EndY=35 EndZ=0
    g4: LineSegment StartX=5.21097e-06 StartY=3 StartZ=0 EndX=5.21097e-06 EndY=0 EndZ=0
    g5: LineSegment StartX=3 StartY=0 StartZ=0 EndX=5.21097e-06 EndY=0 EndZ=0
    g6: LineSegment StartX=3 StartY=19 StartZ=0 EndX=3 EndY=0 EndZ=0
    g7: LineSegment StartX=19 StartY=38 StartZ=0 EndX=124 EndY=38 EndZ=0
    g8: Circle CenterX=119 CenterY=35 CenterZ=0 NormalX=0 NormalY=0 NormalZ=1 AngleXU=0 Radius=1
    g9: Circle CenterX=121 CenterY=35 CenterZ=0 NormalX=0 NormalY=0 NormalZ=1 AngleXU=0 Radius=1
    g10: Circle CenterX=121 CenterY=33 CenterZ=0 NormalX=0 NormalY=0 NormalZ=1 AngleXU=0 Radius=1
    g11: BSplineCurve PolesCount=3 KnotsCount=2 Degree=2 IsPeriodic=0
    g12: GeomPoint X=119 Y=35 Z=0
    g13: GeomPoint X=121 Y=33 Z=0
    g14: LineSegment StartX=119 StartY=35 StartZ=0 EndX=114 EndY=35 EndZ=0
    g15: ArcOfCircle CenterX=105 CenterY=19 CenterZ=0 NormalX=0 NormalY=0 NormalZ=1 AngleXU=0 Radius=16 StartAngle=5.60905 EndAngle=6.28319
    g16: LineSegment StartX=121 StartY=33 StartZ=0 EndX=121 EndY=19 EndZ=0
    g17: LineSegment StartX=117.5 StartY=9.01251 StartZ=0 EndX=121.163 EndY=9.0125 EndZ=0
    g18: ArcOfCircle CenterX=105 CenterY=19 CenterZ=0 NormalX=0 NormalY=0 NormalZ=1 AngleXU=0 Radius=20.6155 StartAngle=5.7297 EndAngle=6.28319
    g19: LineSegment StartX=121.163 StartY=9.0125 StartZ=0 EndX=122.538 EndY=8.16329 EndZ=0
    g20: LineSegment StartX=124 StartY=38 StartZ=0 EndX=125.616 EndY=38 EndZ=0
    g21: LineSegment StartX=125.616 StartY=19 StartZ=0 EndX=125.616 EndY=38 EndZ=0
  constraints (49):
    c: Vertical(g0)
    c: Block(g0)
    c: Coincident(g1,g0)
    c: Block(g1)
    c: Coincident(g2,g1)
    c: Block(g2)
    c: Coincident(g3,g2)
    c: Horizontal(g3)
    c: Tangent(g3,g2)
    c: Coincident(g4,g0)
    c: Distance(g4) = 3
    c: Vertical(g4)
    c: Coincident(g5,g4)
    c: Horizontal(g5)
    c: Coincident(g6,g2)
    c: Coincident(g6,g5)
    c: Vertical(g6)
    c: Horizontal(g7)
    c: Distance(g7) = 105
    c: Coincident(g7,g1)
    c: Block(g3)
    c: Weight(g8) = 1
    c: Equal(g8,g9)
    c: Equal(g8,g10)
    c: InternalAlignment(g8,g11)
    c: InternalAlignment(g9,g11)
    c: InternalAlignment(g10,g11)
    c: InternalAlignment(g12,g11)
    c: InternalAlignment(g13,g11)
    c: Block(g11)
    c: Coincident(g14,g11)
    c: Coincident(g14,g3)
    c: Horizontal(g14)
    c: Block(g15)
    c: Coincident(g16,g11)
    c: Coincident(g16,g15)
    c: Vertical(g16)
    c: Distance(g16) = 14
    c: Coincident(g17,g15)
    c: Block(g18)
    c: Coincident(g19,g18)
    c: Coincident(g20,g7)
    c: Horizontal(g20)
    c: Vertical(g21)
    c: Coincident(g20,g21)
    c: Block(g20)
    c: Block(g21)
    c: Block(g19)
    c: Block(g17)
FEATURE [Part::Box] Box026  label="removeToCreteHoleForPlugHousing032"
  AttacherType = Attacher::AttachEngine3D
  Height = 28.6
  Length = 10
  Placement = pos=(-2,0,21.7) rot=(0,0,1;0rad)
  Width = 19
FEATURE [Part::Feature] Face109 .. Face112  x4 (patterned run collapsed; names and placements below)
  shape: bbox 3.5 x 17.8 x 2e-07 mm, 1 faces, 0 solids (baked)
FEATURE [Part::Revolution] Revolve117  label="removeToCreateScrewAndThreadedInsertHole045"
  Angle = 360
  Axis = (0,1,0)
  Base = (0,0,0)
  FaceMakerClass = Part::FaceMakerBullseye
  Placement = pos=(62.3,30.3,19.7) rot=(0,0,1;0rad)
  Solid = false
  Source = -> Face109
  Symmetric = false
FEATURE [Part::Revolution] Revolve118  label="removeToCreateScrewAndThreadedInsertHole046"
  Angle = 360
  Axis = (0,1,0)
  Base = (0,0,0)
  FaceMakerClass = Part::FaceMakerBullseye
  Placement = pos=(62.3,30.3,51.7) rot=(0,0,1;0rad)
  Solid = false
  Source = -> Face110
  Symmetric = false
FEATURE [Part::Revolution] Revolve119  label="removeToCreateScrewAndThreadedInsertHole047"
  Angle = 360
  Axis = (0,1,0)
  Base = (0,0,0)
  FaceMakerClass = Part::FaceMakerBullseye
  Placement = pos=(30.3,30.3,19.7) rot=(0,0,1;0rad)
  Solid = false
  Source = -> Face111
  Symmetric = false
FEATURE [Part::Revolution] Revolve120  label="removeToCreateScrewAndThreadedInsertHole048"
  Angle = 360
  Axis = (0,1,0)
  Base = (0,0,0)
  FaceMakerClass = Part::FaceMakerBullseye
  Placement = pos=(30.3,30.3,51.7) rot=(0,0,1;0rad)
  Solid = false
  Source = -> Face112
  Symmetric = false
FEATURE [Part::MultiFuse] Fusion087  label="createThreadedInsertHolesForFan005"
  Shapes = -> [Revolve117,Revolve118,Revolve119,Revolve120]
FEATURE [Part::Extrusion] Extrude047
  Base = -> Sketch056
  Dir = (0,0,1)
  DirMode = 2
  FaceMakerClass = Part::FaceMakerBullseye
  LengthFwd = 72
  LengthRev = 0
  Solid = true
  Symmetric = false
FEATURE [Part::Fillet] Fillet039  label="top019"
  Base = -> Extrude047
  Edges = 1 edges r=2: [Edge35]
FEATURE [Sketcher::SketchObject] Sketch057
  FullyConstrained = false
  Placement = pos=(0,0,0) rot=(1,0,0;1.5708rad)
  sketch-geometry (24):
    g0: ArcOfCircle CenterX=-4 CenterY=-10.5 CenterZ=0 NormalX=0 NormalY=0 NormalZ=1 AngleXU=0 Radius=1.5 StartAngle=6e-16 EndAngle=3.14159
    g1: ArcOfCircle CenterX=-34.2 CenterY=-10.5 CenterZ=0 NormalX=0 NormalY=0 NormalZ=1 AngleXU=0 Radius=1.5 StartAngle=0 EndAngle=3.14159
    g2: ArcOfCircle CenterX=-34.2 CenterY=-27.7 CenterZ=0 NormalX=0 NormalY=0 NormalZ=1 AngleXU=0 Radius=1.5 StartAngle=3.14159 EndAngle=6.28319
    g3: ArcOfCircle CenterX=-4 CenterY=-27.7 CenterZ=0 NormalX=0 NormalY=0 NormalZ=1 AngleXU=0 Radius=1.5 StartAngle=3.1416 EndAngle=6.28319
    g4: ArcOfCircle CenterX=-10 CenterY=-4.3 CenterZ=0 NormalX=0 NormalY=0 NormalZ=1 AngleXU=0 Radius=1.5 StartAngle=2e-16 EndAngle=3.14159
    g5: ArcOfCircle CenterX=-16.1 CenterY=-1.8 CenterZ=0 NormalX=0 NormalY=0 NormalZ=1 AngleXU=0 Radius=1.5 StartAngle=5e-16 EndAngle=3.14159
    g6: ArcOfCircle CenterX=-22.1 CenterY=-1.8 CenterZ=0 NormalX=0 NormalY=0 NormalZ=1 AngleXU=0 Radius=1.5 StartAngle=5e-16 EndAngle=3.14159
    g7: ArcOfCircle CenterX=-28.2 CenterY=-4.3 CenterZ=0 NormalX=0 NormalY=0 NormalZ=1 AngleXU=0 Radius=1.5 StartAngle=2e-16 EndAngle=3.14159
    g8: ArcOfCircle CenterX=-10 CenterY=-33.9 CenterZ=0 NormalX=0 NormalY=0 NormalZ=1 AngleXU=0 Radius=1.5 StartAngle=3.14159 EndAngle=6.28319
    g9: ArcOfCircle CenterX=-16.1 CenterY=-36.4 CenterZ=0 NormalX=0 NormalY=0 NormalZ=1 AngleXU=0 Radius=1.5 StartAngle=3.14159 EndAngle=6.28319
    g10: ArcOfCircle CenterX=-22.1 CenterY=-36.4 CenterZ=0 NormalX=0 NormalY=0 NormalZ=1 AngleXU=0 Radius=1.5 StartAngle=3.14159 EndAngle=6.28319
    g11: ArcOfCircle CenterX=-28.2 CenterY=-33.9 CenterZ=0 NormalX=0 NormalY=0 NormalZ=1 AngleXU=0 Radius=1.5 StartAngle=3.14159 EndAngle=6.28319
    g12: LineSegment StartX=-35.7 StartY=-10.5 StartZ=0 EndX=-35.7 EndY=-27.7 EndZ=0
    g13: LineSegment StartX=-32.7 StartY=-10.5 StartZ=0 EndX=-32.7 EndY=-27.7 EndZ=0
    g14: LineSegment StartX=-29.7 StartY=-33.9 StartZ=0 EndX=-29.7 EndY=-4.3 EndZ=0
    g15: LineSegment StartX=-26.7 StartY=-33.9 StartZ=0 EndX=-26.7 EndY=-4.3 EndZ=0
    g16: LineSegment StartX=-2.5 StartY=-10.5 StartZ=0 EndX=-2.5 EndY=-27.7 EndZ=0
    g17: LineSegment StartX=-8.5 StartY=-4.3 StartZ=0 EndX=-8.5 EndY=-33.9 EndZ=0
    g18: LineSegment StartX=-5.5 StartY=-10.5 StartZ=0 EndX=-5.5 EndY=-27.7 EndZ=0
    g19: LineSegment StartX=-11.5 StartY=-4.3 StartZ=0 EndX=-11.5 EndY=-33.9 EndZ=0
    g20: LineSegment StartX=-14.6 StartY=-1.8 StartZ=0 EndX=-14.6 EndY=-36.4 EndZ=0
    g21: LineSegment StartX=-17.6 StartY=-1.8 StartZ=0 EndX=-17.6 EndY=-36.4 EndZ=0
    g22: LineSegment StartX=-20.6 StartY=-36.4 StartZ=0 EndX=-20.6 EndY=-1.8 EndZ=0
    g23: LineSegment StartX=-23.6 StartY=-1.8 StartZ=0 EndX=-23.6 EndY=-36.4 EndZ=0
  constraints (48):
    c: Block(g0)
    c: Block(g1)
    c: Block(g2)
    c: Block(g3)
    c: Block(g4)
    c: Block(g5)
    c: Block(g6)
    c: Block(g7)
    c: Block(g8)
    c: Block(g9)
    c: Block(g10)
    c: Block(g11)
    c: Coincident(g12,g1)
    c: Coincident(g12,g2)
    c: Vertical(g12)
    c: Coincident(g13,g1)
    c: Coincident(g13,g2)
    c: Vertical(g13)
    c: Coincident(g14,g11)
    c: Coincident(g14,g7)
    c: Vertical(g14)
    c: Coincident(g15,g11)
    c: Coincident(g15,g7)
    c: Vertical(g15)
    c: Coincident(g16,g0)
    c: Coincident(g16,g3)
    c: Vertical(g16)
    c: Coincident(g17,g4)
    c: Coincident(g17,g8)
    c: Vertical(g17)
    c: Coincident(g18,g0)
    c: Coincident(g18,g3)
    c: Vertical(g18)
    c: Coincident(g19,g4)
    c: Coincident(g19,g8)
    c: Vertical(g19)
    c: Coincident(g20,g5)
    c: Coincident(g20,g9)
    c: Vertical(g20)
    c: Coincident(g21,g5)
    c: Coincident(g21,g9)
    c: Vertical(g21)
    c: Coincident(g22,g10)
    c: Coincident(g22,g6)
    c: Vertical(g22)
    c: Coincident(g23,g6)
    c: Coincident(g23,g10)
    c: Vertical(g23)
FEATURE [Part::Extrusion] Extrude048  label="removeToCreateFanGrillHoles004"
  Base = -> Sketch057
  Dir = (0,-1,6e-16)
  DirMode = 2
  FaceMakerClass = Part::FaceMakerBullseye
  LengthFwd = 10
  LengthRev = 0
  Placement = pos=(65.4,44,54.82) rot=(0,0,1;0rad)
  Solid = true
  Symmetric = false
FEATURE [Part::Cut] Cut040  label="top021"
  Base = -> Fillet039
  Tool = -> Extrude048
FEATURE [Part::Cylinder] Cylinder041  label="removeToCreteHoleForPlugHousing034"
  Angle = 360
  AttacherType = Attacher::AttachEngine3D
  Height = 20
  Placement = pos=(-2,19,36) rot=(0,1,0;1.5708rad)
  Radius = 14.3
FEATURE [Part::MultiFuse] Fusion089  label="removeToCreteHoleForPlugHousing035"
  Shapes = -> [Box026,Cylinder041]
FEATURE [Part::Cylinder] Cylinder042
  Angle = 360
  AttacherType = Attacher::AttachEngine3D
  Height = 20
  Placement = pos=(0,0,36.15) rot=(0,0,1;0rad)
  Radius = 14.3
FEATURE [Part::Cylinder] Cylinder043
  Angle = 360
  AttacherType = Attacher::AttachEngine3D
  Height = 10
  Placement = pos=(0,0,36.15) rot=(0,0,1;0rad)
  Radius = 4
FEATURE [Part::Box] Box027  label="removeToCreteHoleForPlugHousing036"
  AttacherType = Attacher::AttachEngine3D
  Height = 28.6
  Length = 20
  Placement = pos=(106.15,0,21.7) rot=(0,0,1;0rad)
  Width = 19
FEATURE [Part::Cut] Cut041  label="top022"
  Base = -> Cut040
  Tool = -> Fusion087
FEATURE [Part::Cut] Cut039  label="top020"
  Base = -> Cut041
  Tool = -> Fusion089
FEATURE [Part::MultiFuse] Fusion090  label="removeToCreteHoleForPlugHousing037"
  Placement = pos=(70,19,36) rot=(0,1,0;1.5708rad)
  Shapes = -> [Cylinder042,Cylinder043]
FEATURE [Part::MultiFuse] Fusion088  label="removeToCreteHoleForPlugHousing033"
  Shapes = -> [Box027,Fusion090]
FEATURE [Part::Cut] Cut042  label="removeToCreteHoleForPlugHousing038"
  Base = -> Cut039
  Tool = -> Fusion088
FEATURE [Part::MultiFuse] Fusion091  label="removeFromTop"
  Shapes = -> [Fillet038,Fusion085,Fusion084,Fusion083,Extrude045]
FEATURE [Part::Cut] Cut043  label="REAL TOP ====="
  Base = -> Fillet036
  Tool = -> Fusion091
FEATURE [Part::MultiFuse] Fusion092  label="caseScrewPillarBracket016"
  Shapes = -> [Extrude030,Extrude031,Extrude032,Extrude033,Extrude034,Extrude035,Extrude036,Extrude037,Box013,Box014]
FEATURE [Sketcher::SketchObject] Sketch058  label="topSketch015"
  FullyConstrained = true
  sketch-geometry (20):
    g0: LineSegment StartX=5.21097e-06 StartY=3 StartZ=0 EndX=5.21097e-06 EndY=19 EndZ=0
    g1: ArcOfCircle CenterX=19 CenterY=19 CenterZ=0 NormalX=0 NormalY=0 NormalZ=1 AngleXU=0 Radius=19 StartAngle=1.5708 EndAngle=3.14159
    g2: ArcOfCircle CenterX=19 CenterY=19 CenterZ=0 NormalX=0 NormalY=0 NormalZ=1 AngleXU=0 Radius=16 StartAngle=1.5708 EndAngle=3.14159
    g3: LineSegment StartX=114 StartY=35 StartZ=0 EndX=19 EndY=35 EndZ=0
    g4: LineSegment StartX=5.21097e-06 StartY=3 StartZ=0 EndX=5.21097e-06 EndY=0 EndZ=0
    g5: LineSegment StartX=3 StartY=0 StartZ=0 EndX=5.21097e-06 EndY=0 EndZ=0
    g6: LineSegment StartX=3 StartY=19 StartZ=0 EndX=3 EndY=0 EndZ=0
    g7: LineSegment StartX=19 StartY=38 StartZ=0 EndX=124 EndY=38 EndZ=0
    g8: Circle CenterX=119 CenterY=35 CenterZ=0 NormalX=0 NormalY=0 NormalZ=1 AngleXU=0 Radius=1
    g9: Circle CenterX=121 CenterY=35 CenterZ=0 NormalX=0 NormalY=0 NormalZ=1 AngleXU=0 Radius=1
    g10: Circle CenterX=121 CenterY=33 CenterZ=0 NormalX=0 NormalY=0 NormalZ=1 AngleXU=0 Radius=1
    g11: BSplineCurve PolesCount=3 KnotsCount=2 Degree=2 IsPeriodic=0
    g12: GeomPoint X=119 Y=35 Z=0
    g13: GeomPoint X=121 Y=33 Z=0
    g14: LineSegment StartX=119 StartY=35 StartZ=0 EndX=114 EndY=35 EndZ=0
    g15: ArcOfCircle CenterX=105 CenterY=19 CenterZ=0 NormalX=0 NormalY=0 NormalZ=1 AngleXU=0 Radius=19 StartAngle=5.7297 EndAngle=6.28319
    g16: ArcOfCircle CenterX=105 CenterY=19 CenterZ=0 NormalX=0 NormalY=0 NormalZ=1 AngleXU=0 Radius=16 StartAngle=5.60905 EndAngle=6.28319
    g17: LineSegment StartX=121 StartY=33 StartZ=0 EndX=121 EndY=19 EndZ=0
    g18: LineSegment StartX=124 StartY=38 StartZ=0 EndX=124 EndY=19 EndZ=0
    g19: LineSegment StartX=117.5 StartY=9.01251 StartZ=0 EndX=121.163 EndY=9.0125 EndZ=0
  constraints (46):
    c: Vertical(g0)
    c: Block(g0)
    c: Coincident(g1,g0)
    c: Block(g1)
    c: Coincident(g2,g1)
    c: Block(g2)
    c: Coincident(g3,g2)
    c: Horizontal(g3)
    c: Tangent(g3,g2)
    c: Coincident(g4,g0)
    c: Distance(g4) = 3
    c: Vertical(g4)
    c: Coincident(g5,g4)
    c: Horizontal(g5)
    c: Coincident(g6,g2)
    c: Coincident(g6,g5)
    c: Vertical(g6)
    c: Horizontal(g7)
    c: Distance(g7) = 105
    c: Coincident(g7,g1)
    c: Block(g3)
    c: Weight(g8) = 1
    c: Equal(g8,g9)
    c: Equal(g8,g10)
    c: InternalAlignment(g8,g11)
    c: InternalAlignment(g9,g11)
    c: InternalAlignment(g10,g11)
    c: InternalAlignment(g12,g11)
    c: InternalAlignment(g13,g11)
    c: Block(g11)
    c: Coincident(g14,g11)
    c: Coincident(g14,g3)
    c: Horizontal(g14)
    c: Block(g15)
    c: Coincident(g16,g15)
    c: Block(g16)
    c: Coincident(g17,g11)
    c: Coincident(g17,g16)
    c: Vertical(g17)
    c: Distance(g17) = 14
    c: Coincident(g18,g7)
    c: Coincident(g18,g15)
    c: Vertical(g18)
    c: Distance(g18) = 19
    c: Coincident(g19,g16)
    c: Coincident(g19,g15)
FEATURE [Part::Extrusion] Extrude049  label="top023"
  Base = -> Sketch058
  Dir = (0,0,1)
  DirMode = 2
  FaceMakerClass = Part::FaceMakerBullseye
  LengthFwd = 72
  LengthRev = 0
  Solid = true
  Symmetric = false
FEATURE [Sketcher::SketchObject] Sketch059
  FullyConstrained = true
  MapMode = 3
  Placement = pos=(0,0,0) rot=(1,0,0;1.5708rad)
  Support = -> [Extrude049]
  sketch-geometry (8):
    g0: Circle CenterX=80.351 CenterY=-67.6202 CenterZ=0 NormalX=0 NormalY=0 NormalZ=1 AngleXU=0 Radius=2
    g1: Circle CenterX=80.351 CenterY=-67.6202 CenterZ=0 NormalX=0 NormalY=0 NormalZ=1 AngleXU=0 Radius=3
    g2: Circle CenterX=80.351 CenterY=-4.92017 CenterZ=0 NormalX=0 NormalY=0 NormalZ=1 AngleXU=0 Radius=2
    g3: Circle CenterX=80.351 CenterY=-4.92017 CenterZ=0 NormalX=0 NormalY=0 NormalZ=1 AngleXU=0 Radius=3
    g4: Circle CenterX=23.851 CenterY=-4.92017 CenterZ=0 NormalX=0 NormalY=0 NormalZ=1 AngleXU=0 Radius=2
    g5: Circle CenterX=23.851 CenterY=-4.92017 CenterZ=0 NormalX=0 NormalY=0 NormalZ=1 AngleXU=0 Radius=3
    g6: Circle CenterX=23.851 CenterY=-67.6202 CenterZ=0 NormalX=0 NormalY=0 NormalZ=1 AngleXU=0 Radius=2
    g7: Circle CenterX=23.851 CenterY=-67.6202 CenterZ=0 NormalX=0 NormalY=0 NormalZ=1 AngleXU=0 Radius=3
  constraints (8):
    c: Block(g3)
    c: Block(g2)
    c: Block(g1)
    c: Block(g0)
    c: Block(g6)
    c: Block(g7)
    c: Block(g4)
    c: Block(g5)
FEATURE [Sketcher::SketchObject] Sketch060
  FullyConstrained = true
  MapMode = 3
  Placement = pos=(0,0,0) rot=(1,0,0;1.5708rad)
  Support = -> [Extrude049]
  sketch-geometry (8):
    g0: Circle CenterX=80.351 CenterY=-67.6202 CenterZ=0 NormalX=0 NormalY=0 NormalZ=1 AngleXU=0 Radius=3
    g1: Circle CenterX=80.351 CenterY=-4.92017 CenterZ=0 NormalX=0 NormalY=0 NormalZ=1 AngleXU=0 Radius=3
    g2: Circle CenterX=23.851 CenterY=-4.92017 CenterZ=0 NormalX=0 NormalY=0 NormalZ=1 AngleXU=0 Radius=3
    g3: Circle CenterX=23.851 CenterY=-67.6202 CenterZ=0 NormalX=0 NormalY=0 NormalZ=1 AngleXU=0 Radius=3
    g4: Circle CenterX=23.851 CenterY=-67.6202 CenterZ=0 NormalX=0 NormalY=0 NormalZ=1 AngleXU=0 Radius=5
    g5: Circle CenterX=80.351 CenterY=-67.6202 CenterZ=0 NormalX=0 NormalY=0 NormalZ=1 AngleXU=0 Radius=5
    g6: Circle CenterX=23.851 CenterY=-4.92017 CenterZ=0 NormalX=0 NormalY=0 NormalZ=1 AngleXU=0 Radius=5
    g7: Circle CenterX=80.351 CenterY=-4.92017 CenterZ=0 NormalX=0 NormalY=0 NormalZ=1 AngleXU=0 Radius=5
  constraints (8):
    c: Block(g1)
    c: Block(g0)
    c: Block(g3)
    c: Block(g2)
    c: Block(g5)
    c: Block(g4)
    c: Block(g6)
    c: Block(g7)
FEATURE [Sketcher::SketchObject] Sketch061
  FullyConstrained = true
  MapMode = 3
  Placement = pos=(0,0,0) rot=(1,0,0;1.5708rad)
  sketch-geometry (8):
    g0: Circle CenterX=80.351 CenterY=-67.6202 CenterZ=0 NormalX=0 NormalY=0 NormalZ=1 AngleXU=0 Radius=3
    g1: Circle CenterX=80.351 CenterY=-4.92017 CenterZ=0 NormalX=0 NormalY=0 NormalZ=1 AngleXU=0 Radius=3
    g2: Circle CenterX=23.851 CenterY=-4.92017 CenterZ=0 NormalX=0 NormalY=0 NormalZ=1 AngleXU=0 Radius=3
    g3: Circle CenterX=23.851 CenterY=-67.6202 CenterZ=0 NormalX=0 NormalY=0 NormalZ=1 AngleXU=0 Radius=3
    g4: Circle CenterX=23.851 CenterY=-67.6202 CenterZ=0 NormalX=0 NormalY=0 NormalZ=1 AngleXU=0 Radius=5
    g5: Circle CenterX=80.351 CenterY=-67.6202 CenterZ=0 NormalX=0 NormalY=0 NormalZ=1 AngleXU=0 Radius=5
    g6: Circle CenterX=23.851 CenterY=-4.92017 CenterZ=0 NormalX=0 NormalY=0 NormalZ=1 AngleXU=0 Radius=5
    g7: Circle CenterX=80.351 CenterY=-4.92017 CenterZ=0 NormalX=0 NormalY=0 NormalZ=1 AngleXU=0 Radius=5
  constraints (8):
    c: Block(g1)
    c: Block(g0)
    c: Block(g3)
    c: Block(g2)
    c: Block(g5)
    c: Block(g4)
    c: Block(g6)
    c: Block(g7)
FEATURE [Sketcher::SketchObject] Sketch062  label="topSketch016"
  FullyConstrained = true
  sketch-geometry (20):
    g0: LineSegment StartX=5.21097e-06 StartY=3 StartZ=0 EndX=5.21097e-06 EndY=19 EndZ=0
    g1: ArcOfCircle CenterX=19 CenterY=19 CenterZ=0 NormalX=0 NormalY=0 NormalZ=1 AngleXU=0 Radius=19 StartAngle=1.5708 EndAngle=3.14159
    g2: ArcOfCircle CenterX=19 CenterY=19 CenterZ=0 NormalX=0 NormalY=0 NormalZ=1 AngleXU=0 Radius=16 StartAngle=1.5708 EndAngle=3.14159
    g3: LineSegment StartX=114 StartY=35 StartZ=0 EndX=19 EndY=35 EndZ=0
    g4: LineSegment StartX=5.21097e-06 StartY=3 StartZ=0 EndX=5.21097e-06 EndY=0 EndZ=0
    g5: LineSegment StartX=3 StartY=0 StartZ=0 EndX=5.21097e-06 EndY=0 EndZ=0
    g6: LineSegment StartX=3 StartY=19 StartZ=0 EndX=3 EndY=0 EndZ=0
    g7: LineSegment StartX=19 StartY=38 StartZ=0 EndX=124 EndY=38 EndZ=0
    g8: Circle CenterX=119 CenterY=35 CenterZ=0 NormalX=0 NormalY=0 NormalZ=1 AngleXU=0 Radius=1
    g9: Circle CenterX=121 CenterY=35 CenterZ=0 NormalX=0 NormalY=0 NormalZ=1 AngleXU=0 Radius=1
    g10: Circle CenterX=121 CenterY=33 CenterZ=0 NormalX=0 NormalY=0 NormalZ=1 AngleXU=0 Radius=1
    g11: BSplineCurve PolesCount=3 KnotsCount=2 Degree=2 IsPeriodic=0
    g12: GeomPoint X=119 Y=35 Z=0
    g13: GeomPoint X=121 Y=33 Z=0
    g14: LineSegment StartX=119 StartY=35 StartZ=0 EndX=114 EndY=35 EndZ=0
    g15: ArcOfCircle CenterX=105 CenterY=19 CenterZ=0 NormalX=0 NormalY=0 NormalZ=1 AngleXU=0 Radius=19 StartAngle=5.7297 EndAngle=6.28319
    g16: ArcOfCircle CenterX=105 CenterY=19 CenterZ=0 NormalX=0 NormalY=0 NormalZ=1 AngleXU=0 Radius=16 StartAngle=5.60905 EndAngle=6.28319
    g17: LineSegment StartX=121 StartY=33 StartZ=0 EndX=121 EndY=19 EndZ=0
    g18: LineSegment StartX=124 StartY=38 StartZ=0 EndX=124 EndY=19 EndZ=0
    g19: LineSegment StartX=117.5 StartY=9.01251 StartZ=0 EndX=121.163 EndY=9.0125 EndZ=0
  constraints (46):
    c: Vertical(g0)
    c: Block(g0)
    c: Coincident(g1,g0)
    c: Block(g1)
    c: Coincident(g2,g1)
    c: Block(g2)
    c: Coincident(g3,g2)
    c: Horizontal(g3)
    c: Tangent(g3,g2)
    c: Coincident(g4,g0)
    c: Distance(g4) = 3
    c: Vertical(g4)
    c: Coincident(g5,g4)
    c: Horizontal(g5)
    c: Coincident(g6,g2)
    c: Coincident(g6,g5)
    c: Vertical(g6)
    c: Horizontal(g7)
    c: Distance(g7) = 105
    c: Coincident(g7,g1)
    c: Block(g3)
    c: Weight(g8) = 1
    c: Equal(g8,g9)
    c: Equal(g8,g10)
    c: InternalAlignment(g8,g11)
    c: InternalAlignment(g9,g11)
    c: InternalAlignment(g10,g11)
    c: InternalAlignment(g12,g11)
    c: InternalAlignment(g13,g11)
    c: Block(g11)
    c: Coincident(g14,g11)
    c: Coincident(g14,g3)
    c: Horizontal(g14)
    c: Block(g15)
    c: Coincident(g16,g15)
    c: Block(g16)
    c: Coincident(g17,g11)
    c: Coincident(g17,g16)
    c: Vertical(g17)
    c: Distance(g17) = 14
    c: Coincident(g18,g7)
    c: Coincident(g18,g15)
    c: Vertical(g18)
    c: Distance(g18) = 19
    c: Coincident(g19,g16)
    c: Coincident(g19,g15)
FEATURE [Part::Extrusion] Extrude053  label="top024"
  Base = -> Sketch062
  Dir = (0,0,1)
  DirMode = 2
  FaceMakerClass = Part::FaceMakerBullseye
  LengthFwd = 72
  LengthRev = 0
  Solid = true
  Symmetric = false
FEATURE [Sketcher::SketchObject] Sketch063
  FullyConstrained = true
  MapMode = 3
  Placement = pos=(0,0,0) rot=(1,0,0;1.5708rad)
  Support = -> [Extrude053]
  sketch-geometry (8):
    g0: Circle CenterX=80.351 CenterY=-67.6202 CenterZ=0 NormalX=0 NormalY=0 NormalZ=1 AngleXU=0 Radius=2
    g1: Circle CenterX=80.351 CenterY=-67.6202 CenterZ=0 NormalX=0 NormalY=0 NormalZ=1 AngleXU=0 Radius=3
    g2: Circle CenterX=80.351 CenterY=-4.92017 CenterZ=0 NormalX=0 NormalY=0 NormalZ=1 AngleXU=0 Radius=2
    g3: Circle CenterX=80.351 CenterY=-4.92017 CenterZ=0 NormalX=0 NormalY=0 NormalZ=1 AngleXU=0 Radius=3
    g4: Circle CenterX=23.851 CenterY=-4.92017 CenterZ=0 NormalX=0 NormalY=0 NormalZ=1 AngleXU=0 Radius=2
    g5: Circle CenterX=23.851 CenterY=-4.92017 CenterZ=0 NormalX=0 NormalY=0 NormalZ=1 AngleXU=0 Radius=3
    g6: Circle CenterX=23.851 CenterY=-67.6202 CenterZ=0 NormalX=0 NormalY=0 NormalZ=1 AngleXU=0 Radius=2
    g7: Circle CenterX=23.851 CenterY=-67.6202 CenterZ=0 NormalX=0 NormalY=0 NormalZ=1 AngleXU=0 Radius=3
  constraints (8):
    c: Block(g3)
    c: Block(g2)
    c: Block(g1)
    c: Block(g0)
    c: Block(g6)
    c: Block(g7)
    c: Block(g4)
    c: Block(g5)
FEATURE [Part::Extrusion] Extrude054
  Base = -> Sketch063
  Dir = (0,-1,2e-16)
  DirMode = 2
  FaceMakerClass = Part::FaceMakerBullseye
  LengthFwd = 6
  LengthRev = 0
  Placement = pos=(0,9,0) rot=(0,0,1;0rad)
  Solid = true
  Symmetric = false
FEATURE [Sketcher::SketchObject] Sketch064  label="topSketch017"
  FullyConstrained = true
  sketch-geometry (20):
    g0: LineSegment StartX=5.21097e-06 StartY=3 StartZ=0 EndX=5.21097e-06 EndY=19 EndZ=0
    g1: ArcOfCircle CenterX=19 CenterY=19 CenterZ=0 NormalX=0 NormalY=0 NormalZ=1 AngleXU=0 Radius=19 StartAngle=1.5708 EndAngle=3.14159
    g2: ArcOfCircle CenterX=19 CenterY=19 CenterZ=0 NormalX=0 NormalY=0 NormalZ=1 AngleXU=0 Radius=16 StartAngle=1.5708 EndAngle=3.14159
    g3: LineSegment StartX=114 StartY=35 StartZ=0 EndX=19 EndY=35 EndZ=0
    g4: LineSegment StartX=5.21097e-06 StartY=3 StartZ=0 EndX=5.21097e-06 EndY=0 EndZ=0
    g5: LineSegment StartX=3 StartY=0 StartZ=0 EndX=5.21097e-06 EndY=0 EndZ=0
    g6: LineSegment StartX=3 StartY=19 StartZ=0 EndX=3 EndY=0 EndZ=0
    g7: LineSegment StartX=19 StartY=38 StartZ=0 EndX=124 EndY=38 EndZ=0
    g8: Circle CenterX=119 CenterY=35 CenterZ=0 NormalX=0 NormalY=0 NormalZ=1 AngleXU=0 Radius=1
    g9: Circle CenterX=121 CenterY=35 CenterZ=0 NormalX=0 NormalY=0 NormalZ=1 AngleXU=0 Radius=1
    g10: Circle CenterX=121 CenterY=33 CenterZ=0 NormalX=0 NormalY=0 NormalZ=1 AngleXU=0 Radius=1
    g11: BSplineCurve PolesCount=3 KnotsCount=2 Degree=2 IsPeriodic=0
    g12: GeomPoint X=119 Y=35 Z=0
    g13: GeomPoint X=121 Y=33 Z=0
    g14: LineSegment StartX=119 StartY=35 StartZ=0 EndX=114 EndY=35 EndZ=0
    g15: ArcOfCircle CenterX=105 CenterY=19 CenterZ=0 NormalX=0 NormalY=0 NormalZ=1 AngleXU=0 Radius=19 StartAngle=5.7297 EndAngle=6.28319
    g16: ArcOfCircle CenterX=105 CenterY=19 CenterZ=0 NormalX=0 NormalY=0 NormalZ=1 AngleXU=0 Radius=16 StartAngle=5.60905 EndAngle=6.28319
    g17: LineSegment StartX=121 StartY=33 StartZ=0 EndX=121 EndY=19 EndZ=0
    g18: LineSegment StartX=124 StartY=38 StartZ=0 EndX=124 EndY=19 EndZ=0
    g19: LineSegment StartX=117.5 StartY=9.01251 StartZ=0 EndX=121.163 EndY=9.0125 EndZ=0
  constraints (46):
    c: Vertical(g0)
    c: Block(g0)
    c: Coincident(g1,g0)
    c: Block(g1)
    c: Coincident(g2,g1)
    c: Block(g2)
    c: Coincident(g3,g2)
    c: Horizontal(g3)
    c: Tangent(g3,g2)
    c: Coincident(g4,g0)
    c: Distance(g4) = 3
    c: Vertical(g4)
    c: Coincident(g5,g4)
    c: Horizontal(g5)
    c: Coincident(g6,g2)
    c: Coincident(g6,g5)
    c: Vertical(g6)
    c: Horizontal(g7)
    c: Distance(g7) = 105
    c: Coincident(g7,g1)
    c: Block(g3)
    c: Weight(g8) = 1
    c: Equal(g8,g9)
    c: Equal(g8,g10)
    c: InternalAlignment(g8,g11)
    c: InternalAlignment(g9,g11)
    c: InternalAlignment(g10,g11)
    c: InternalAlignment(g12,g11)
    c: InternalAlignment(g13,g11)
    c: Block(g11)
    c: Coincident(g14,g11)
    c: Coincident(g14,g3)
    c: Horizontal(g14)
    c: Block(g15)
    c: Coincident(g16,g15)
    c: Block(g16)
    c: Coincident(g17,g11)
    c: Coincident(g17,g16)
    c: Vertical(g17)
    c: Distance(g17) = 14
    c: Coincident(g18,g7)
    c: Coincident(g18,g15)
    c: Vertical(g18)
    c: Distance(g18) = 19
    c: Coincident(g19,g16)
    c: Coincident(g19,g15)
FEATURE [Sketcher::SketchObject] Sketch065
  FullyConstrained = true
  MapMode = 3
  Placement = pos=(0,0,0) rot=(1,0,0;1.5708rad)
  sketch-geometry (8):
    g0: Circle CenterX=80.351 CenterY=-67.6202 CenterZ=0 NormalX=0 NormalY=0 NormalZ=1 AngleXU=0 Radius=3
    g1: Circle CenterX=80.351 CenterY=-4.92017 CenterZ=0 NormalX=0 NormalY=0 NormalZ=1 AngleXU=0 Radius=3
    g2: Circle CenterX=23.851 CenterY=-4.92017 CenterZ=0 NormalX=0 NormalY=0 NormalZ=1 AngleXU=0 Radius=3
    g3: Circle CenterX=23.851 CenterY=-67.6202 CenterZ=0 NormalX=0 NormalY=0 NormalZ=1 AngleXU=0 Radius=3
    g4: Circle CenterX=23.851 CenterY=-67.6202 CenterZ=0 NormalX=0 NormalY=0 NormalZ=1 AngleXU=0 Radius=5
    g5: Circle CenterX=80.351 CenterY=-67.6202 CenterZ=0 NormalX=0 NormalY=0 NormalZ=1 AngleXU=0 Radius=5
    g6: Circle CenterX=23.851 CenterY=-4.92017 CenterZ=0 NormalX=0 NormalY=0 NormalZ=1 AngleXU=0 Radius=5
    g7: Circle CenterX=80.351 CenterY=-4.92017 CenterZ=0 NormalX=0 NormalY=0 NormalZ=1 AngleXU=0 Radius=5
  constraints (8):
    c: Block(g1)
    c: Block(g0)
    c: Block(g3)
    c: Block(g2)
    c: Block(g5)
    c: Block(g4)
    c: Block(g6)
    c: Block(g7)
FEATURE [Part::Extrusion] Extrude056
  Base = -> Sketch065
  Dir = (0,-1,2e-16)
  DirMode = 2
  FaceMakerClass = Part::FaceMakerBullseye
  LengthFwd = 2
  LengthRev = 0
  Solid = true
  Symmetric = false
FEATURE [Part::Extrusion] Extrude057  label="top025"
  Base = -> Sketch064
  Dir = (0,0,1)
  DirMode = 2
  FaceMakerClass = Part::FaceMakerBullseye
  LengthFwd = 72
  LengthRev = 0
  Solid = true
  Symmetric = false
FEATURE [Sketcher::SketchObject] Sketch066
  FullyConstrained = true
  MapMode = 3
  Placement = pos=(0,0,0) rot=(1,0,0;1.5708rad)
  Support = -> [Extrude057]
  sketch-geometry (8):
    g0: Circle CenterX=80.351 CenterY=-67.6202 CenterZ=0 NormalX=0 NormalY=0 NormalZ=1 AngleXU=0 Radius=3
    g1: Circle CenterX=80.351 CenterY=-4.92017 CenterZ=0 NormalX=0 NormalY=0 NormalZ=1 AngleXU=0 Radius=3
    g2: Circle CenterX=23.851 CenterY=-4.92017 CenterZ=0 NormalX=0 NormalY=0 NormalZ=1 AngleXU=0 Radius=3
    g3: Circle CenterX=23.851 CenterY=-67.6202 CenterZ=0 NormalX=0 NormalY=0 NormalZ=1 AngleXU=0 Radius=3
    g4: Circle CenterX=23.851 CenterY=-67.6202 CenterZ=0 NormalX=0 NormalY=0 NormalZ=1 AngleXU=0 Radius=5
    g5: Circle CenterX=80.351 CenterY=-67.6202 CenterZ=0 NormalX=0 NormalY=0 NormalZ=1 AngleXU=0 Radius=5
    g6: Circle CenterX=23.851 CenterY=-4.92017 CenterZ=0 NormalX=0 NormalY=0 NormalZ=1 AngleXU=0 Radius=5
    g7: Circle CenterX=80.351 CenterY=-4.92017 CenterZ=0 NormalX=0 NormalY=0 NormalZ=1 AngleXU=0 Radius=5
  constraints (8):
    c: Block(g1)
    c: Block(g0)
    c: Block(g3)
    c: Block(g2)
    c: Block(g5)
    c: Block(g4)
    c: Block(g6)
    c: Block(g7)
FEATURE [Part::Extrusion] Extrude055
  Base = -> Sketch066
  Dir = (0,-1,2e-16)
  DirMode = 2
  FaceMakerClass = Part::FaceMakerBullseye
  LengthFwd = 2
  LengthRev = 0
  Solid = true
  Symmetric = false
FEATURE [Part::Fillet] Fillet041
  Base = -> Extrude056
  Edges = 4 edges r=1.99: [Edge6,Edge12,Edge18,Edge24]
FEATURE [Part::Cut] Cut045
  Base = -> Extrude055
  Placement = pos=(0,6,0) rot=(0,0,1;0rad)
  Tool = -> Fillet041
FEATURE [Part::MultiFuse] Fusion095  label="pcbScrewPillars"
  Placement = pos=(-3.2,-1,72.3) rot=(0,0,1;0rad)
  Shapes = -> [Cut045,Extrude054]
FEATURE [Part::Feature] Face113
  shape: bbox 3.2 x 1.5 x 2e-07 mm, 1 faces, 0 solids (baked)
FEATURE [Part::Revolution] Revolve121  label="backCaseScrewRetainer002"
  Angle = 360
  Axis = (0,1,0)
  Base = (0,0,0)
  FaceMakerClass = Part::FaceMakerBullseye
  Placement = pos=(12.5,3,62) rot=(0,0,1;0rad)
  Solid = false
  Source = -> Face113
  Symmetric = false
FEATURE [Part::Feature] Face114
  shape: bbox 3.2 x 1.5 x 2e-07 mm, 1 faces, 0 solids (baked)
FEATURE [Part::Feature] Face115
  shape: bbox 3.2 x 1.5 x 2e-07 mm, 1 faces, 0 solids (baked)
FEATURE [Part::Feature] Face116
  shape: bbox 3.2 x 1.5 x 2e-07 mm, 1 faces, 0 solids (baked)
FEATURE [Part::Revolution] Revolve122  label="frontCaseScrewRetainer004"
  Angle = 360
  Axis = (0,1,0)
  Base = (0,0,0)
  FaceMakerClass = Part::FaceMakerBullseye
  Placement = pos=(89.5,3,68.5) rot=(0,0,1;0rad)
  Solid = false
  Source = -> Face115
  Symmetric = false
FEATURE [Part::Revolution] Revolve123  label="frontCaseScrewRetainer005"
  Angle = 360
  Axis = (0,1,0)
  Base = (0,0,0)
  FaceMakerClass = Part::FaceMakerBullseye
  Placement = pos=(89.5,3,3.5) rot=(0,0,1;0rad)
  Solid = false
  Source = -> Face116
  Symmetric = false
FEATURE [Part::Revolution] Revolve124  label="backCaseScrewRetainer003"
  Angle = 360
  Axis = (0,1,0)
  Base = (0,0,0)
  FaceMakerClass = Part::FaceMakerBullseye
  Placement = pos=(12.5,3,10) rot=(0,0,1;0rad)
  Solid = false
  Source = -> Face114
  Symmetric = false
FEATURE [Part::Feature] Face117
  shape: bbox 3.6 x 3.2 x 2e-07 mm, 1 faces, 0 solids (baked)
FEATURE [Part::Revolution] Revolve125  label="moreFrontCaseScrewRetainer004"
  Angle = 360
  Axis = (0,1,0)
  Base = (0,0,0)
  FaceMakerClass = Part::FaceMakerBullseye
  Placement = pos=(109.5,4.5,68.5) rot=(0,0,1;0rad)
  Solid = false
  Source = -> Face117
  Symmetric = false
FEATURE [Part::Feature] Face118
  shape: bbox 3.6 x 3.2 x 2e-07 mm, 1 faces, 0 solids (baked)
FEATURE [Part::Revolution] Revolve126  label="moreFrontCaseScrewRetainer005"
  Angle = 360
  Axis = (0,1,0)
  Base = (0,0,0)
  FaceMakerClass = Part::FaceMakerBullseye
  Placement = pos=(109.5,4.5,3.5) rot=(0,0,1;0rad)
  Solid = false
  Source = -> Face118
  Symmetric = false
FEATURE [Part::MultiFuse] Fusion096  label="screwRetainers001"
  Shapes = -> [Revolve126,Revolve125,Revolve124,Revolve123,Revolve122,Revolve121]
FEATURE [Part::Feature] Face119
  shape: bbox 10 x 16.5 x 2e-07 mm, 1 faces, 0 solids (baked)
FEATURE [Part::Revolution] Revolve130  label="plugHousing050"
  Angle = 360
  Axis = (0,1,0)
  Base = (0,0,0)
  FaceMakerClass = Part::FaceMakerBullseye
  Placement = pos=(0,0,36.15) rot=(0,0,1;0rad)
  Solid = false
  Source = -> Face119
  Symmetric = false
FEATURE [Part::Feature] Face120
  shape: bbox 10 x 16.5 x 2e-07 mm, 1 faces, 0 solids (baked)
FEATURE [Part::Feature] Face121
  shape: bbox 10 x 16.5 x 2e-07 mm, 1 faces, 0 solids (baked)
FEATURE [Part::Revolution] Revolve127  label="plugHousing047"
  Angle = 360
  Axis = (0,1,0)
  Base = (0,0,0)
  FaceMakerClass = Part::FaceMakerBullseye
  Placement = pos=(0,0,36.15) rot=(0,0,1;0rad)
  Solid = false
  Source = -> Face121
  Symmetric = false
FEATURE [Part::Feature] Face122
  shape: bbox 10 x 16.5 x 2e-07 mm, 1 faces, 0 solids (baked)
FEATURE [Part::Feature] Face123
  shape: bbox 10 x 16.5 x 2e-07 mm, 1 faces, 0 solids (baked)
FEATURE [Part::Revolution] Revolve128  label="plugHousing048"
  Angle = 360
  Axis = (0,1,0)
  Base = (0,0,0)
  FaceMakerClass = Part::FaceMakerBullseye
  Placement = pos=(0,0,36.15) rot=(0,0,1;0rad)
  Solid = false
  Source = -> Face123
  Symmetric = false
FEATURE [Part::MultiFuse] Fusion100  label="plugHousing054"
  Placement = pos=(0,0,0) rot=(0,0,1;1.5708rad)
  Shapes = -> [Revolve130,Revolve128]
FEATURE [Part::Feature] Face124
  shape: bbox 10 x 16.5 x 2e-07 mm, 1 faces, 0 solids (baked)
FEATURE [Part::Feature] Face125
  shape: bbox 10 x 16.5 x 2e-07 mm, 1 faces, 0 solids (baked)
FEATURE [Part::Revolution] Revolve129  label="plugHousing049"
  Angle = 360
  Axis = (0,1,0)
  Base = (0,0,0)
  FaceMakerClass = Part::FaceMakerBullseye
  Placement = pos=(0,0,36.15) rot=(0,0,1;0rad)
  Solid = false
  Source = -> Face125
  Symmetric = false
FEATURE [Part::Feature] Face126
  shape: bbox 10 x 16.5 x 2e-07 mm, 1 faces, 0 solids (baked)
FEATURE [Part::Revolution] Revolve131  label="plugHousing058"
  Angle = 360
  Axis = (0,1,0)
  Base = (0,0,0)
  FaceMakerClass = Part::FaceMakerBullseye
  Placement = pos=(0,0,36.15) rot=(0,0,1;0rad)
  Solid = false
  Source = -> Face120
  Symmetric = false
FEATURE [Part::MultiFuse] Fusion099  label="plugHousing053"
  Placement = pos=(0,0,0) rot=(0,0,1;1.5708rad)
  Shapes = -> [Revolve127,Revolve131]
FEATURE [Part::MultiFuse] Fusion102  label="plugHousing056"
  Placement = pos=(0,19,0) rot=(0,0,1;3.14159rad)
  Shapes = -> [Fusion100,Fusion099]
FEATURE [Part::Revolution] Revolve132  label="plugHousing059"
  Angle = 360
  Axis = (0,1,0)
  Base = (0,0,0)
  FaceMakerClass = Part::FaceMakerBullseye
  Placement = pos=(0,0,36.15) rot=(0,0,1;0rad)
  Solid = false
  Source = -> Face126
  Symmetric = false
FEATURE [Part::Revolution] Revolve133  label="plugHousing060"
  Angle = 360
  Axis = (0,1,0)
  Base = (0,0,0)
  FaceMakerClass = Part::FaceMakerBullseye
  Placement = pos=(0,0,36.15) rot=(0,0,1;0rad)
  Solid = false
  Source = -> Face122
  Symmetric = false
FEATURE [Part::MultiFuse] Fusion097  label="plugHousing051"
  Placement = pos=(0,0,0) rot=(0,0,1;1.5708rad)
  Shapes = -> [Revolve133,Revolve132]
FEATURE [Part::Revolution] Revolve134  label="plugHousing061"
  Angle = 360
  Axis = (0,1,0)
  Base = (0,0,0)
  FaceMakerClass = Part::FaceMakerBullseye
  Placement = pos=(0,0,36.15) rot=(0,0,1;0rad)
  Solid = false
  Source = -> Face124
  Symmetric = false
FEATURE [Part::MultiFuse] Fusion101  label="plugHousing055"
  Placement = pos=(0,0,0) rot=(0,0,1;1.5708rad)
  Shapes = -> [Revolve129,Revolve134]
FEATURE [Part::MultiFuse] Fusion098  label="plugHousing052"
  Placement = pos=(0,19,0) rot=(0,0,1;3.14159rad)
  Shapes = -> [Fusion097,Fusion101]
FEATURE [Part::MultiFuse] Fusion103  label="plugHousing057"
  Placement = pos=(122.621,0,-0.15) rot=(0,0,1;0rad)
  Shapes = -> [Fusion102,Fusion098]
FEATURE [Part::Box] Box028  label="Cube015"
  AttacherType = Attacher::AttachEngine3D
  Height = 28
  Length = 3
  Placement = pos=(110.7,19,22) rot=(0,0,1;0rad)
  Width = 15.7
FEATURE [Part::Cylinder] Cylinder044
  Angle = 360
  AttacherType = Attacher::AttachEngine3D
  Height = 20
  Placement = pos=(0,0,36.15) rot=(0,0,1;0rad)
  Radius = 10.3
FEATURE [Part::Cylinder] Cylinder045
  Angle = 360
  AttacherType = Attacher::AttachEngine3D
  Height = 10
  Placement = pos=(0,0,36.15) rot=(0,0,1;0rad)
  Radius = 4
FEATURE [Part::MultiFuse] Fusion104  label="removeToCreteHoleForPlugHousing040"
  Placement = pos=(70,19,36) rot=(0,1,0;1.5708rad)
  Shapes = -> [Cylinder044,Cylinder045]
FEATURE [Part::Cut] Cut046  label="plugHousingTab003"
  Base = -> Box028
  Tool = -> Fusion104
FEATURE [Part::MultiFuse] Fusion105  label="plugHousing062"
  Shapes = -> [Fusion103,Cut046]
FEATURE [Part::Fillet] Fillet042
  Base = -> Fusion105
  Edges = 1 edges r=2: [Edge25]
FEATURE [Part::Fillet] Fillet043  label="plugHousing063"
  Base = -> Fillet042
  Edges = 1 edges r=2: [Edge8]
  Placement = pos=(7,0,0) rot=(0,0,1;0rad)
FEATURE [Part::Feature] Face127
  shape: bbox 10 x 16.5 x 2e-07 mm, 1 faces, 0 solids (baked)
FEATURE [Part::Feature] Face128
  shape: bbox 10 x 16.5 x 2e-07 mm, 1 faces, 0 solids (baked)
FEATURE [Part::Revolution] Revolve137  label="plugHousing070"
  Angle = 360
  Axis = (0,1,0)
  Base = (0,0,0)
  FaceMakerClass = Part::FaceMakerBullseye
  Placement = pos=(0,0,36.15) rot=(0,0,1;0rad)
  Solid = false
  Source = -> Face127
  Symmetric = false
FEATURE [Part::Revolution] Revolve140  label="plugHousing073"
  Angle = 360
  Axis = (0,1,0)
  Base = (0,0,0)
  FaceMakerClass = Part::FaceMakerBullseye
  Placement = pos=(0,0,36.15) rot=(0,0,1;0rad)
  Solid = false
  Source = -> Face128
  Symmetric = false
FEATURE [Part::Feature] Face129
  shape: bbox 10 x 16.5 x 2e-07 mm, 1 faces, 0 solids (baked)
FEATURE [Part::Revolution] Revolve138  label="plugHousing071"
  Angle = 360
  Axis = (0,1,0)
  Base = (0,0,0)
  FaceMakerClass = Part::FaceMakerBullseye
  Placement = pos=(0,0,36.15) rot=(0,0,1;0rad)
  Solid = false
  Source = -> Face129
  Symmetric = false
FEATURE [Part::Feature] Face130
  shape: bbox 10 x 16.5 x 2e-07 mm, 1 faces, 0 solids (baked)
FEATURE [Part::Revolution] Revolve139  label="plugHousing072"
  Angle = 360
  Axis = (0,1,0)
  Base = (0,0,0)
  FaceMakerClass = Part::FaceMakerBullseye
  Placement = pos=(0,0,36.15) rot=(0,0,1;0rad)
  Solid = false
  Source = -> Face130
  Symmetric = false
FEATURE [Part::Feature] Face131
  shape: bbox 10 x 16.5 x 2e-07 mm, 1 faces, 0 solids (baked)
FEATURE [Part::Revolution] Revolve135  label="plugHousing068"
  Angle = 360
  Axis = (0,1,0)
  Base = (0,0,0)
  FaceMakerClass = Part::FaceMakerBullseye
  Placement = pos=(0,0,36.15) rot=(0,0,1;0rad)
  Solid = false
  Source = -> Face131
  Symmetric = false
FEATURE [Part::MultiFuse] Fusion112  label="plugHousing078"
  Placement = pos=(0,0,0) rot=(0,0,1;1.5708rad)
  Shapes = -> [Revolve135,Revolve139]
FEATURE [Part::Feature] Face132
  shape: bbox 10 x 16.5 x 2e-07 mm, 1 faces, 0 solids (baked)
FEATURE [Part::Revolution] Revolve141  label="plugHousing074"
  Angle = 360
  Axis = (0,1,0)
  Base = (0,0,0)
  FaceMakerClass = Part::FaceMakerBullseye
  Placement = pos=(0,0,36.15) rot=(0,0,1;0rad)
  Solid = false
  Source = -> Face132
  Symmetric = false
FEATURE [Part::MultiFuse] Fusion110  label="plugHousing076"
  Placement = pos=(0,0,0) rot=(0,0,1;1.5708rad)
  Shapes = -> [Revolve141,Revolve140]
FEATURE [Part::Feature] Face133
  shape: bbox 10 x 16.5 x 2e-07 mm, 1 faces, 0 solids (baked)
FEATURE [Part::Revolution] Revolve136  label="plugHousing069"
  Angle = 360
  Axis = (0,1,0)
  Base = (0,0,0)
  FaceMakerClass = Part::FaceMakerBullseye
  Placement = pos=(0,0,36.15) rot=(0,0,1;0rad)
  Solid = false
  Source = -> Face133
  Symmetric = false
FEATURE [Part::MultiFuse] Fusion106  label="plugHousing064"
  Placement = pos=(0,0,0) rot=(0,0,1;1.5708rad)
  Shapes = -> [Revolve138,Revolve136]
FEATURE [Part::MultiFuse] Fusion108  label="plugHousing066"
  Placement = pos=(0,19,0) rot=(0,0,1;3.14159rad)
  Shapes = -> [Fusion106,Fusion112]
FEATURE [Part::Feature] Face134
  shape: bbox 10 x 16.5 x 2e-07 mm, 1 faces, 0 solids (baked)
FEATURE [Part::Revolution] Revolve142  label="plugHousing075"
  Angle = 360
  Axis = (0,1,0)
  Base = (0,0,0)
  FaceMakerClass = Part::FaceMakerBullseye
  Placement = pos=(0,0,36.15) rot=(0,0,1;0rad)
  Solid = false
  Source = -> Face134
  Symmetric = false
FEATURE [Part::MultiFuse] Fusion107  label="plugHousing065"
  Placement = pos=(0,0,0) rot=(0,0,1;1.5708rad)
  Shapes = -> [Revolve137,Revolve142]
FEATURE [Part::MultiFuse] Fusion111  label="plugHousing077"
  Placement = pos=(0,19,0) rot=(0,0,1;3.14159rad)
  Shapes = -> [Fusion110,Fusion107]
FEATURE [Part::MultiFuse] Fusion109  label="plugHousing067"
  Placement = pos=(131.236,0,-0.15) rot=(0,0,1;0rad)
  Shapes = -> [Fusion108,Fusion111]
FEATURE [Part::MultiFuse] Fusion113  label="plugHousing079"
  Shapes = -> [Fillet043,Fusion109]
FEATURE [Part::Feature] Face135
  shape: bbox 3.5 x 17.8 x 2e-07 mm, 1 faces, 0 solids (baked)
FEATURE [Part::Revolution] Revolve143  label="removeToCreateScrewAndThreadedInsertHole049"
  Angle = 360
  Axis = (0,1,0)
  Base = (0,0,0)
  FaceMakerClass = Part::FaceMakerBullseye
  Placement = pos=(12.5,0,10) rot=(0,0,1;0rad)
  Solid = false
  Source = -> Face135
  Symmetric = false
FEATURE [Part::Feature] Face136
  shape: bbox 3.5 x 17.8 x 2e-07 mm, 1 faces, 0 solids (baked)
FEATURE [Part::Revolution] Revolve144  label="removeToCreateScrewAndThreadedInsertHole050"
  Angle = 360
  Axis = (0,1,0)
  Base = (0,0,0)
  FaceMakerClass = Part::FaceMakerBullseye
  Placement = pos=(12.5,0,62) rot=(0,0,1;0rad)
  Solid = false
  Source = -> Face136
  Symmetric = false
FEATURE [Part::Feature] Face137
  shape: bbox 3.5 x 17.8 x 2e-07 mm, 1 faces, 0 solids (baked)
FEATURE [Part::Revolution] Revolve145  label="removeToCreateScrewAndThreadedInsertHole051"
  Angle = 360
  Axis = (0,1,0)
  Base = (0,0,0)
  FaceMakerClass = Part::FaceMakerBullseye
  Placement = pos=(89.5,0,68.5) rot=(0,0,1;0rad)
  Solid = false
  Source = -> Face137
  Symmetric = false
FEATURE [Part::Feature] Face138
  shape: bbox 3.5 x 17.8 x 2e-07 mm, 1 faces, 0 solids (baked)
FEATURE [Part::Revolution] Revolve146  label="removeToCreateScrewAndThreadedInsertHole052"
  Angle = 360
  Axis = (0,1,0)
  Base = (0,0,0)
  FaceMakerClass = Part::FaceMakerBullseye
  Placement = pos=(89.5,0,3.5) rot=(0,0,1;0rad)
  Solid = false
  Source = -> Face138
  Symmetric = false
FEATURE [Part::Feature] Face139
  shape: bbox 3.5 x 17.8 x 2e-07 mm, 1 faces, 0 solids (baked)
FEATURE [Part::Revolution] Revolve147  label="removeToCreateScrewAndThreadedInsertHole053"
  Angle = 360
  Axis = (0,1,0)
  Base = (0,0,0)
  FaceMakerClass = Part::FaceMakerBullseye
  Placement = pos=(109.5,4.7,3.5) rot=(0,0,1;0rad)
  Solid = false
  Source = -> Face139
  Symmetric = false
FEATURE [Part::Feature] Face140
  shape: bbox 3.5 x 17.8 x 2e-07 mm, 1 faces, 0 solids (baked)
FEATURE [Part::Revolution] Revolve148  label="removeToCreateScrewAndThreadedInsertHole054"
  Angle = 360
  Axis = (0,1,0)
  Base = (0,0,0)
  FaceMakerClass = Part::FaceMakerBullseye
  Placement = pos=(109.5,4.7,68.5) rot=(0,0,1;0rad)
  Solid = false
  Source = -> Face140
  Symmetric = false
FEATURE [Part::MultiFuse] Fusion114  label="removeToCreateScrewAndThreadedInsertHole055"
  Shapes = -> [Revolve148,Revolve147,Revolve146,Revolve145,Revolve144,Revolve143]
FEATURE [Part::Cut] Cut047  label="casePillars004"
  Base = -> Cut037
  Tool = -> Fusion114
FEATURE [Part::Feature] Face141
  shape: bbox 3.5 x 17.8 x 2e-07 mm, 1 faces, 0 solids (baked)
FEATURE [Part::Feature] Face142
  shape: bbox 3.5 x 17.8 x 2e-07 mm, 1 faces, 0 solids (baked)
FEATURE [Part::Feature] Face143
  shape: bbox 3.5 x 17.8 x 2e-07 mm, 1 faces, 0 solids (baked)
FEATURE [Part::Revolution] Revolve149  label="removeToCreateScrewAndThreadedInsertHole057"
  Angle = 360
  Axis = (0,1,0)
  Base = (0,0,0)
  FaceMakerClass = Part::FaceMakerBullseye
  Placement = pos=(12.5,0,10) rot=(0,0,1;0rad)
  Solid = false
  Source = -> Face141
  Symmetric = false
FEATURE [Part::Feature] Face144
  shape: bbox 3.5 x 17.8 x 2e-07 mm, 1 faces, 0 solids (baked)
FEATURE [Part::Feature] Face145
  shape: bbox 3.5 x 17.8 x 2e-07 mm, 1 faces, 0 solids (baked)
FEATURE [Part::Feature] Face146
  shape: bbox 3.5 x 17.8 x 2e-07 mm, 1 faces, 0 solids (baked)
FEATURE [Part::Revolution] Revolve150  label="removeToCreateScrewAndThreadedInsertHole058"
  Angle = 360
  Axis = (0,1,0)
  Base = (0,0,0)
  FaceMakerClass = Part::FaceMakerBullseye
  Placement = pos=(12.5,0,62) rot=(0,0,1;0rad)
  Solid = false
  Source = -> Face146
  Symmetric = false
FEATURE [Part::Revolution] Revolve151  label="removeToCreateScrewAndThreadedInsertHole059"
  Angle = 360
  Axis = (0,1,0)
  Base = (0,0,0)
  FaceMakerClass = Part::FaceMakerBullseye
  Placement = pos=(89.5,0,68.5) rot=(0,0,1;0rad)
  Solid = false
  Source = -> Face143
  Symmetric = false
FEATURE [Part::Revolution] Revolve152  label="removeToCreateScrewAndThreadedInsertHole060"
  Angle = 360
  Axis = (0,1,0)
  Base = (0,0,0)
  FaceMakerClass = Part::FaceMakerBullseye
  Placement = pos=(89.5,0,3.5) rot=(0,0,1;0rad)
  Solid = false
  Source = -> Face142
  Symmetric = false
FEATURE [Part::Revolution] Revolve153  label="removeToCreateScrewAndThreadedInsertHole061"
  Angle = 360
  Axis = (0,1,0)
  Base = (0,0,0)
  FaceMakerClass = Part::FaceMakerBullseye
  Placement = pos=(109.5,4.7,3.5) rot=(0,0,1;0rad)
  Solid = false
  Source = -> Face145
  Symmetric = false
FEATURE [Part::Revolution] Revolve154  label="removeToCreateScrewAndThreadedInsertHole062"
  Angle = 360
  Axis = (0,1,0)
  Base = (0,0,0)
  FaceMakerClass = Part::FaceMakerBullseye
  Placement = pos=(109.5,4.7,68.5) rot=(0,0,1;0rad)
  Solid = false
  Source = -> Face144
  Symmetric = false
FEATURE [Part::MultiFuse] Fusion115  label="removeToCreateScrewAndThreadedInsertHole056"
  Shapes = -> [Revolve154,Revolve153,Revolve152,Revolve151,Revolve150,Revolve149]
FEATURE [Part::Feature] Face147
  shape: bbox 9.8 x 26.5 x 2e-07 mm, 1 faces, 0 solids (baked)
FEATURE [Part::Revolution] Revolve155
  Angle = 360
  Axis = (0,1,0)
  Base = (0,0,0)
  FaceMakerClass = Part::FaceMakerBullseye
  Placement = pos=(0,0,0) rot=(0,0,1;1.5708rad)
  Solid = false
  Source = -> Face147
  Symmetric = false
FEATURE [Part::Feature] Face148
  shape: bbox 9.8 x 26.5 x 2e-07 mm, 1 faces, 0 solids (baked)
FEATURE [Part::Revolution] Revolve156
  Angle = 360
  Axis = (0,1,0)
  Base = (0,0,0)
  FaceMakerClass = Part::FaceMakerBullseye
  Placement = pos=(0,0,0) rot=(0,0,1;1.5708rad)
  Solid = false
  Source = -> Face148
  Symmetric = false
FEATURE [Part::MultiFuse] Fusion116
  Placement = pos=(-18,19,36) rot=(0,0,1;0rad)
  Shapes = -> [Revolve156,Revolve155]
FEATURE [Part::Box] Box029  label="Cube016"
  AttacherType = Attacher::AttachEngine3D
  Height = 28
  Length = 3
  Placement = pos=(110.7,19,22) rot=(0,0,1;0rad)
  Width = 15.7
FEATURE [Part::Cylinder] Cylinder046
  Angle = 360
  AttacherType = Attacher::AttachEngine3D
  Height = 10
  Placement = pos=(0,0,36.15) rot=(0,0,1;0rad)
  Radius = 4
FEATURE [Part::Cylinder] Cylinder047
  Angle = 360
  AttacherType = Attacher::AttachEngine3D
  Height = 20
  Placement = pos=(0,0,36.15) rot=(0,0,1;0rad)
  Radius = 10.3
FEATURE [Part::MultiFuse] Fusion117  label="removeToCreteHoleForPlugHousing041"
  Placement = pos=(70,19,36) rot=(0,1,0;1.5708rad)
  Shapes = -> [Cylinder047,Cylinder046]
FEATURE [Part::Cut] Cut049  label="plugHousingTab004"
  Base = -> Box029
  Placement = pos=(-107.4,-14,0) rot=(0,0,1;0rad)
  Tool = -> Fusion117
FEATURE [Part::Box] Box030  label="Cube017"
  AttacherType = Attacher::AttachEngine3D
  Height = 28
  Length = 3
  Placement = pos=(110.7,19,22) rot=(0,0,1;0rad)
  Width = 15.7
FEATURE [Part::Cylinder] Cylinder048
  Angle = 360
  AttacherType = Attacher::AttachEngine3D
  Height = 10
  Placement = pos=(0,0,36.15) rot=(0,0,1;0rad)
  Radius = 4
FEATURE [Part::Cylinder] Cylinder049
  Angle = 360
  AttacherType = Attacher::AttachEngine3D
  Height = 20
  Placement = pos=(0,0,36.15) rot=(0,0,1;0rad)
  Radius = 10.3
FEATURE [Part::MultiFuse] Fusion118  label="removeToCreteHoleForPlugHousing042"
  Placement = pos=(70,19,36) rot=(0,1,0;1.5708rad)
  Shapes = -> [Cylinder049,Cylinder048]
FEATURE [Part::Cut] Cut050  label="plugHousingTab005"
  Base = -> Box030
  Placement = pos=(-107.4,-14,0) rot=(0,0,1;0rad)
  Tool = -> Fusion118
FEATURE [Part::MultiFuse] Fusion119
  Placement = pos=(9.6,23,0) rot=(0,0,1;3.14159rad)
  Shapes = -> [Cut049,Cut050]
FEATURE [Part::Box] Box031  label="Cube018"
  AttacherType = Attacher::AttachEngine3D
  Height = 10
  Length = 3
  Placement = pos=(3.3,4,12) rot=(0,0,1;0rad)
  Width = 10
FEATURE [Part::Fillet] Fillet044
  Base = -> Box031
  Edges = 1 edges r=2: [Edge11]
FEATURE [Part::Box] Box032  label="Cube019"
  AttacherType = Attacher::AttachEngine3D
  Height = 10
  Length = 3
  Placement = pos=(3.3,4,50) rot=(0,0,1;0rad)
  Width = 10
FEATURE [Part::Fillet] Fillet045
  Base = -> Box032
  Edges = 1 edges r=2: [Edge12]
FEATURE [Part::Box] Box033  label="Cube020"
  AttacherType = Attacher::AttachEngine3D
  Height = 28
  Length = 4
  Placement = pos=(5,0,22) rot=(0,0,1;0rad)
  Width = 10
FEATURE [Part::Fillet] Fillet046
  Base = -> Box033
  Edges = 1 edges r=1: [Edge7]
FEATURE [Part::Fillet] Fillet047
  Base = -> Fillet046
  Edges = 1 edges r=2: [Edge5]
FEATURE [Part::Fillet] Fillet048
  Base = -> Fillet047
  Edges = 1 edges r=2: [Edge2]
FEATURE [Part::Cylinder] Cylinder050
  Angle = 360
  AttacherType = Attacher::AttachEngine3D
  Height = 20
  Placement = pos=(0,0,36.15) rot=(0,0,1;0rad)
  Radius = 8.2
FEATURE [Part::Cylinder] Cylinder051
  Angle = 360
  AttacherType = Attacher::AttachEngine3D
  Height = 10
  Placement = pos=(0,0,36.15) rot=(0,0,1;0rad)
  Radius = 4
FEATURE [Part::MultiFuse] Fusion120  label="removeToCreteHoleForPlugHousing043"
  Placement = pos=(-42,19,36) rot=(0,1,0;1.5708rad)
  Shapes = -> [Cylinder050,Cylinder051]
FEATURE [Sketcher::SketchObject] Sketch067  label="topSketch018"
  FullyConstrained = true
  sketch-geometry (4):
    g0: LineSegment StartX=16.8446 StartY=31.512 StartZ=0 EndX=16.3251 EndY=34.4666 EndZ=0
    g1: ArcOfCircle CenterX=19 CenterY=19.2524 CenterZ=0 NormalX=0 NormalY=0 NormalZ=1 AngleXU=0 Radius=15.4476 StartAngle=1.74483 EndAngle=2.72717
    g2: ArcOfCircle CenterX=19 CenterY=19.2524 CenterZ=0 NormalX=0 NormalY=0 NormalZ=1 AngleXU=0 Radius=12.4476 StartAngle=1.74483 EndAngle=2.73189
    g3: LineSegment StartX=4.86004 StartY=25.4725 StartZ=0 EndX=7.58253 EndY=24.2107 EndZ=0
  constraints (7):
    c: Block(g0)
    c: Coincident(g1,g0)
    c: Coincident(g2,g0)
    c: Coincident(g3,g1)
    c: Coincident(g3,g2)
    c: Block(g1)
    c: Block(g2)
FEATURE [Part::Extrusion] Extrude058
  Base = -> Sketch067
  Dir = (0,0,1)
  DirMode = 2
  FaceMakerClass = Part::FaceMakerBullseye
  LengthFwd = 10
  LengthRev = 0
  Placement = pos=(0,0,31) rot=(0,0,1;0rad)
  Solid = true
  Symmetric = false
FEATURE [Part::Cut] Cut051
  Base = -> Extrude058
  Tool = -> Fusion120
FEATURE [Part::Fillet] Fillet049
  Base = -> Cut051
  Edges = 1 edges r=2: [Edge1]
FEATURE [Part::Fillet] Fillet050
  Base = -> Fillet049
  Edges = 1 edges r=2.5: [Edge1]
FEATURE [Part::Fillet] Fillet051
  Base = -> Fillet050
  Edges = 1 edges r=2.5: [Edge2]
FEATURE [Part::MultiFuse] Fusion121  label="wireHolder003"
  Shapes = -> [Fusion116,Fillet051]
FEATURE [Part::MultiFuse] Fusion122
  Shapes = -> [Fillet045,Fusion121]
FEATURE [Part::MultiFuse] Fusion123  label="wireHolder004"
  Shapes = -> [Fusion122,Fillet048]
FEATURE [Part::MultiFuse] Fusion124  label="wireHolder005"
  Shapes = -> [Fillet044,Fusion119,Fusion123]
FEATURE [Sketcher::SketchObject] Sketch068  label="topSketch019"
  FullyConstrained = true
  sketch-geometry (6):
    g0: LineSegment StartX=19 StartY=38 StartZ=0 EndX=117 EndY=38 EndZ=0
    g1: ArcOfCircle CenterX=19 CenterY=19 CenterZ=0 NormalX=0 NormalY=0 NormalZ=1 AngleXU=0 Radius=19 StartAngle=1.5708 EndAngle=3.14159
    g2: LineSegment StartX=117 StartY=38 StartZ=0 EndX=117 EndY=19 EndZ=0
    g3: LineSegment StartX=98 StartY=1.0161e-12 StartZ=0 EndX=5.22862e-06 EndY=1.0161e-12 EndZ=0
    g4: LineSegment StartX=5.22862e-06 StartY=19 StartZ=0 EndX=5.22862e-06 EndY=1.0161e-12 EndZ=0
    g5: ArcOfCircle CenterX=98 CenterY=19 CenterZ=0 NormalX=0 NormalY=0 NormalZ=1 AngleXU=0 Radius=19 StartAngle=4.71239 EndAngle=6.28319
  constraints (16):
    c: Horizontal(g0)
    c: Distance(g0) = 98
    c: Coincident(g1,g0)
    c: Block(g1)
    c: Coincident(g2,g0)
    c: Vertical(g2)
    c: Distance(g2) = 19
    c: Horizontal(g3)
    c: Coincident(g4,g1)
    c: Vertical(g4)
    c: Coincident(g3,g4)
    c: Block(g3)
    c: Coincident(g5,g2)
    c: Coincident(g5,g3)
    c: Block(g0)
    c: Block(g5)
FEATURE [Part::Extrusion] Extrude059  label="sideA002"
  Base = -> Sketch068
  Dir = (0,0,1)
  DirMode = 2
  FaceMakerClass = Part::FaceMakerBullseye
  LengthFwd = 3
  LengthRev = 0
  Placement = pos=(0,0,-2.7) rot=(0,0,1;0rad)
  Solid = true
  Symmetric = false
FEATURE [Sketcher::SketchObject] Sketch069  label="topSketch020"
  FullyConstrained = true
  sketch-geometry (6):
    g0: LineSegment StartX=19 StartY=38 StartZ=0 EndX=117 EndY=38 EndZ=0
    g1: ArcOfCircle CenterX=19 CenterY=19 CenterZ=0 NormalX=0 NormalY=0 NormalZ=1 AngleXU=0 Radius=19 StartAngle=1.5708 EndAngle=3.14159
    g2: LineSegment StartX=117 StartY=38 StartZ=0 EndX=117 EndY=19 EndZ=0
    g3: LineSegment StartX=98 StartY=1.0161e-12 StartZ=0 EndX=5.22862e-06 EndY=1.0161e-12 EndZ=0
    g4: LineSegment StartX=5.22862e-06 StartY=19 StartZ=0 EndX=5.22862e-06 EndY=1.0161e-12 EndZ=0
    g5: ArcOfCircle CenterX=98 CenterY=19 CenterZ=0 NormalX=0 NormalY=0 NormalZ=1 AngleXU=0 Radius=19 StartAngle=4.71239 EndAngle=6.28319
  constraints (16):
    c: Horizontal(g0)
    c: Distance(g0) = 98
    c: Coincident(g1,g0)
    c: Block(g1)
    c: Coincident(g2,g0)
    c: Vertical(g2)
    c: Distance(g2) = 19
    c: Horizontal(g3)
    c: Coincident(g4,g1)
    c: Vertical(g4)
    c: Coincident(g3,g4)
    c: Block(g3)
    c: Coincident(g5,g2)
    c: Coincident(g5,g3)
    c: Block(g0)
    c: Block(g5)
FEATURE [Part::Extrusion] Extrude060  label="sideB002"
  Base = -> Sketch069
  Dir = (0,0,1)
  DirMode = 2
  FaceMakerClass = Part::FaceMakerBullseye
  LengthFwd = 3
  LengthRev = 0
  Placement = pos=(0,0,71.7) rot=(0,0,1;0rad)
  Solid = true
  Symmetric = false
FEATURE [Part::MultiFuse] Fusion127  label="removeFromBottom001"
  Placement = pos=(2,0,0) rot=(0,0,1;0rad)
  Shapes = -> [Extrude059,Extrude060]
FEATURE [Part::Cylinder] Cylinder052
  Angle = 360
  AttacherType = Attacher::AttachEngine3D
  Height = 20
  Placement = pos=(0,0,36.15) rot=(0,0,1;0rad)
  Radius = 14
FEATURE [Part::Cylinder] Cylinder053
  Angle = 360
  AttacherType = Attacher::AttachEngine3D
  Height = 10
  Placement = pos=(0,0,36.15) rot=(0,0,1;0rad)
  Radius = 4
FEATURE [Part::MultiFuse] Fusion128  label="removeToCreteHoleForPlugHousing044"
  Placement = pos=(70,19,36) rot=(0,1,0;1.5708rad)
  Shapes = -> [Cylinder052,Cylinder053]
FEATURE [Part::Cut] Cut052  label="bottom011"
  Base = -> Extrude043
  Tool = -> Fusion128
FEATURE [Part::Cut] Cut054  label="bottom012"
  Base = -> Cut052
  Tool = -> Fusion115
FEATURE [Sketcher::SketchObject] Sketch070
  FullyConstrained = true
  Placement = pos=(117,19,0) rot=(0.57735,0.57735,0.57735;2.0944rad)
  sketch-geometry (48):
    g0: LineSegment StartX=-49.19 StartY=69.25 StartZ=0 EndX=-49.19 EndY=66.25 EndZ=0
    g1: LineSegment StartX=-49.19 StartY=63.5 StartZ=0 EndX=-49.19 EndY=60.5 EndZ=0
    g2: LineSegment StartX=-49.19 StartY=57.75 StartZ=0 EndX=-49.19 EndY=54.75 EndZ=0
    g3: LineSegment StartX=-49.19 StartY=52 StartZ=0 EndX=-49.19 EndY=49 EndZ=0
    g4: LineSegment StartX=-49.19 StartY=46.25 StartZ=0 EndX=-49.19 EndY=43.25 EndZ=0
    g5: LineSegment StartX=-49.19 StartY=40.5 StartZ=0 EndX=-49.19 EndY=37.5 EndZ=0
    g6: LineSegment StartX=-49.19 StartY=34.5 StartZ=0 EndX=-49.19 EndY=31.5 EndZ=0
    g7: LineSegment StartX=-49.19 StartY=28.75 StartZ=0 EndX=-49.19 EndY=25.75 EndZ=0
    g8: LineSegment StartX=-49.19 StartY=23 StartZ=0 EndX=-49.19 EndY=20 EndZ=0
    g9: LineSegment StartX=-49.19 StartY=17.25 StartZ=0 EndX=-49.19 EndY=14.25 EndZ=0
    g10: LineSegment StartX=-49.19 StartY=11.5 StartZ=0 EndX=-49.19 EndY=8.5 EndZ=0
    g11: LineSegment StartX=-49.19 StartY=5.75 StartZ=0 EndX=-49.19 EndY=2.75 EndZ=0
    g12: ArcOfCircle CenterX=-1.5 CenterY=67.75 CenterZ=0 NormalX=0 NormalY=0 NormalZ=1 AngleXU=0 Radius=1.5 StartAngle=4.71239 EndAngle=7.85398
    g13: ArcOfCircle CenterX=-1.5 CenterY=62 CenterZ=0 NormalX=0 NormalY=0 NormalZ=1 AngleXU=0 Radius=1.5 StartAngle=4.71239 EndAngle=7.85398
    g14: ArcOfCircle CenterX=-1.5 CenterY=56.25 CenterZ=0 NormalX=0 NormalY=0 NormalZ=1 AngleXU=0 Radius=1.5 StartAngle=4.71239 EndAngle=7.85398
    g15: ArcOfCircle CenterX=-11.49 CenterY=50.5 CenterZ=0 NormalX=0 NormalY=0 NormalZ=1 AngleXU=0 Radius=1.5 StartAngle=4.71239 EndAngle=7.85398
    g16: ArcOfCircle CenterX=-16.28 CenterY=44.75 CenterZ=0 NormalX=0 NormalY=0 NormalZ=1 AngleXU=0 Radius=1.5 StartAngle=4.71239 EndAngle=7.85398
    g17: ArcOfCircle CenterX=-18.2337 CenterY=39 CenterZ=0 NormalX=0 NormalY=0 NormalZ=1 AngleXU=0 Radius=1.5 StartAngle=4.71485 EndAngle=7.85398
    g18: ArcOfCircle CenterX=-16.2837 CenterY=27.25 CenterZ=0 NormalX=0 NormalY=0 NormalZ=1 AngleXU=0 Radius=1.5 StartAngle=4.71485 EndAngle=7.85398
    g19: ArcOfCircle CenterX=-18.2337 CenterY=33 CenterZ=0 NormalX=0 NormalY=0 NormalZ=1 AngleXU=0 Radius=1.5 StartAngle=4.71485 EndAngle=7.85398
    g20: ArcOfCircle CenterX=-11.49 CenterY=21.5 CenterZ=0 NormalX=0 NormalY=0 NormalZ=1 AngleXU=0 Radius=1.5 StartAngle=4.71239 EndAngle=7.85398
    g21: ArcOfCircle CenterX=-1.5 CenterY=4.25 CenterZ=0 NormalX=0 NormalY=0 NormalZ=1 AngleXU=0 Radius=1.5 StartAngle=4.71239 EndAngle=7.85398
    g22: ArcOfCircle CenterX=-1.5 CenterY=10 CenterZ=0 NormalX=0 NormalY=0 NormalZ=1 AngleXU=0 Radius=1.5 StartAngle=4.71239 EndAngle=7.85398
    g23: ArcOfCircle CenterX=-1.5 CenterY=15.75 CenterZ=0 NormalX=0 NormalY=0 NormalZ=1 AngleXU=0 Radius=1.5 StartAngle=4.71239 EndAngle=7.85398
    g24: LineSegment StartX=-49.19 StartY=69.25 StartZ=0 EndX=-1.5 EndY=69.25 EndZ=0
    g25: LineSegment StartX=-49.19 StartY=66.25 StartZ=0 EndX=-1.5 EndY=66.25 EndZ=0
    g26: LineSegment StartX=-49.19 StartY=63.5 StartZ=0 EndX=-1.5 EndY=63.5 EndZ=0
    g27: LineSegment StartX=-49.19 StartY=60.5 StartZ=0 EndX=-1.5 EndY=60.5 EndZ=0
    g28: LineSegment StartX=-49.19 StartY=57.75 StartZ=0 EndX=-1.5 EndY=57.75 EndZ=0
    g29: LineSegment StartX=-49.19 StartY=54.75 StartZ=0 EndX=-1.5 EndY=54.75 EndZ=0
    g30: LineSegment StartX=-49.19 StartY=52 StartZ=0 EndX=-11.49 EndY=52 EndZ=0
    g31: LineSegment StartX=-49.19 StartY=49 StartZ=0 EndX=-11.49 EndY=49 EndZ=0
    g32: LineSegment StartX=-49.19 StartY=46.25 StartZ=0 EndX=-16.28 EndY=46.25 EndZ=0
    g33: LineSegment StartX=-49.19 StartY=43.25 StartZ=0 EndX=-16.28 EndY=43.25 EndZ=0
    g34: LineSegment StartX=-49.19 StartY=40.5 StartZ=0 EndX=-18.2337 EndY=40.5 EndZ=0
    g35: LineSegment StartX=-49.19 StartY=37.5 StartZ=0 EndX=-18.23 EndY=37.5 EndZ=0
    g36: LineSegment StartX=-49.19 StartY=34.5 StartZ=0 EndX=-18.2337 EndY=34.5 EndZ=0
    g37: LineSegment StartX=-49.19 StartY=31.5 StartZ=0 EndX=-18.23 EndY=31.5 EndZ=0
    g38: LineSegment StartX=-49.19 StartY=28.75 StartZ=0 EndX=-16.2837 EndY=28.75 EndZ=0
    g39: LineSegment StartX=-49.19 StartY=25.75 StartZ=0 EndX=-16.28 EndY=25.75 EndZ=0
    g40: LineSegment StartX=-49.19 StartY=23 StartZ=0 EndX=-11.49 EndY=23 EndZ=0
    g41: LineSegment StartX=-49.19 StartY=20 StartZ=0 EndX=-11.49 EndY=20 EndZ=0
    g42: LineSegment StartX=-49.19 StartY=17.25 StartZ=0 EndX=-1.5 EndY=17.25 EndZ=0
    g43: LineSegment StartX=-49.19 StartY=14.25 StartZ=0 EndX=-1.5 EndY=14.25 EndZ=0
    g44: LineSegment StartX=-49.19 StartY=11.5 StartZ=0 EndX=-1.5 EndY=11.5 EndZ=0
    g45: LineSegment StartX=-49.19 StartY=8.5 StartZ=0 EndX=-1.5 EndY=8.5 EndZ=0
    g46: LineSegment StartX=-49.19 StartY=5.75 StartZ=0 EndX=-1.5 EndY=5.75 EndZ=0
    g47: LineSegment StartX=-49.19 StartY=2.75 StartZ=0 EndX=-1.5 EndY=2.75 EndZ=0
  constraints (120):
    c: Vertical(g0)
    c: Distance(g0) = 3
    c: Block(g0)
    c: Vertical(g1)
    c: Distance(g1) = 3
    c: Vertical(g2)
    c: Equal(g0,g2) = 3
    c: Block(g2)
    c: Vertical(g3)
    c: Equal(g1,g3) = 3
    c: Vertical(g4)
    c: Equal(g0,g4) = 3
    c: Block(g4)
    c: Vertical(g5)
    c: Equal(g1,g5) = 3
    c: Vertical(g6)
    c: Equal(g0,g6) = 3
    c: Block(g6)
    c: Vertical(g7)
    c: Equal(g1,g7) = 3
    c: Vertical(g8)
    c: Equal(g0,g8) = 3
    c: Block(g8)
    c: Vertical(g9)
    c: Equal(g1,g9) = 3
    c: Vertical(g10)
    c: Equal(g0,g10) = 3
    c: Block(g10)
    c: Vertical(g11)
    c: Equal(g1,g11) = 3
    c: Block(g12)
    c: Block(g13)
    c: Block(g14)
    c: Block(g15)
    c: Block(g16)
    c: Block(g17)
    c: Block(g18)
    c: Block(g19)
    c: Block(g20)
    c: Block(g21)
    c: Block(g22)
    c: Block(g23)
    c: Block(g11)
    c: Block(g9)
    c: Block(g7)
    c: Block(g5)
    c: Block(g3)
    c: Block(g1)
    c: Coincident(g24,g0)
    c: Coincident(g24,g12)
    c: Horizontal(g24)
    c: Coincident(g25,g0)
    c: Coincident(g25,g12)
    c: Horizontal(g25)
    c: Coincident(g26,g1)
    c: Coincident(g26,g13)
    c: Horizontal(g26)
    c: Coincident(g27,g1)
    c: Coincident(g27,g13)
    c: Horizontal(g27)
    c: Coincident(g28,g2)
    c: Coincident(g28,g14)
    c: Horizontal(g28)
    c: Coincident(g29,g2)
    c: Coincident(g29,g14)
    c: Horizontal(g29)
    c: Coincident(g30,g3)
    c: Coincident(g30,g15)
    c: Horizontal(g30)
    c: Coincident(g31,g3)
    c: Coincident(g31,g15)
    c: Horizontal(g31)
    c: Coincident(g32,g4)
    c: Coincident(g32,g16)
    c: Horizontal(g32)
    c: Coincident(g33,g4)
    c: Coincident(g33,g16)
    c: Horizontal(g33)
    c: Coincident(g34,g5)
    c: Coincident(g34,g17)
    c: Horizontal(g34)
    c: Coincident(g35,g5)
    c: Coincident(g35,g17)
    c: Horizontal(g35)
    c: Coincident(g36,g6)
    c: Coincident(g36,g19)
    c: Horizontal(g36)
    c: Coincident(g37,g6)
    c: Coincident(g37,g19)
    c: Horizontal(g37)
    c: Coincident(g38,g7)
    c: Coincident(g38,g18)
    c: Horizontal(g38)
    c: Coincident(g39,g7)
    c: Coincident(g39,g18)
    c: Horizontal(g39)
    c: Coincident(g40,g8)
    c: Coincident(g40,g20)
    c: Horizontal(g40)
    c: Coincident(g41,g8)
    c: Coincident(g41,g20)
    c: Horizontal(g41)
    c: Coincident(g42,g9)
    c: Coincident(g42,g23)
    c: Horizontal(g42)
    c: Coincident(g43,g9)
    c: Coincident(g43,g23)
    c: Horizontal(g43)
    c: Coincident(g44,g10)
    c: Coincident(g44,g22)
    c: Horizontal(g44)
    c: Coincident(g45,g10)
    c: Coincident(g45,g22)
    c: Horizontal(g45)
    c: Coincident(g46,g11)
    c: Coincident(g46,g21)
    c: Horizontal(g46)
    c: Coincident(g47,g11)
    c: Coincident(g47,g21)
    c: Horizontal(g47)
FEATURE [Part::Extrusion] Extrude061
  Base = -> Sketch070
  Dir = (1,0,0)
  DirMode = 2
  FaceMakerClass = Part::FaceMakerBullseye
  LengthFwd = 23
  LengthRev = 0
  Placement = pos=(-19,0,0) rot=(0,0,1;0rad)
  Solid = true
  Symmetric = false
FEATURE [Part::Fillet] Fillet052  label="removeToCreateVentalationHoles002"
  Base = -> Extrude061
  Edges = <same value as first occurrence — deduplicated (x6 in doc)>
  Placement = pos=(7,0.02,0) rot=(0,0,1;0rad)
FEATURE [Part::MultiFuse] Fusion130  label="bottom013"
  Shapes = -> [Cut054,Cut034]
FEATURE [Part::Cut] Cut055
  Base = -> Fusion130
  Tool = -> Fillet052
FEATURE [Part::Cylinder] Cylinder054
  Angle = 360
  AttacherType = Attacher::AttachEngine3D
  Height = 20
  Placement = pos=(0,0,36.15) rot=(0,0,1;0rad)
  Radius = 4
FEATURE [Sketcher::SketchObject] Sketch071  label="bottomSketch002"
  FullyConstrained = true
  sketch-geometry (32):
    g0: LineSegment StartX=3.3 StartY=-6.03275e-07 StartZ=0 EndX=98 EndY=-6.03275e-07 EndZ=0
    g1: ArcOfCircle CenterX=98 CenterY=19 CenterZ=0 NormalX=0 NormalY=0 NormalZ=1 AngleXU=0 Radius=19 StartAngle=4.71239 EndAngle=5.71103
    g2: LineSegment StartX=6.3 StartY=8 StartZ=0 EndX=3.3 EndY=8 EndZ=0
    g3: LineSegment StartX=3.3 StartY=8 StartZ=0 EndX=3.3 EndY=-6.03275e-07 EndZ=0
    g4: ArcOfCircle CenterX=8.3 CenterY=5 CenterZ=0 NormalX=0 NormalY=0 NormalZ=1 AngleXU=0 Radius=2 StartAngle=3.14159 EndAngle=4.71239
    g5: LineSegment StartX=6.3 StartY=8 StartZ=0 EndX=6.3 EndY=5 EndZ=0
    g6: ArcOfCircle CenterX=98 CenterY=19 CenterZ=0 NormalX=0 NormalY=0 NormalZ=1 AngleXU=0 Radius=12.7 StartAngle=4.71239 EndAngle=6.28319
    g7: LineSegment StartX=94.7 StartY=3 StartZ=0 EndX=8.3 EndY=3 EndZ=0
    g8-g12: Circle x5 (B-spline internal-alignment scaffolding for g13; pole/knot coordinates omitted)
    g13: BSplineCurve PolesCount=5 KnotsCount=3 Degree=3 IsPeriodic=0
    g14: GeomPoint X=98 Y=6.3 Z=0
    g15: GeomPoint X=96.3938 Y=4.71946 Z=0
    g16: GeomPoint X=94.7 Y=3 Z=0
    g17-g23: Circle x7 (B-spline internal-alignment scaffolding for g24; pole/knot coordinates omitted)
    g24: BSplineCurve PolesCount=7 KnotsCount=5 Degree=3 IsPeriodic=0
    g25-g29: GeomPoint x5 (B-spline internal-alignment scaffolding for g24; pole/knot coordinates omitted)
    g30: ArcOfCircle CenterX=98 CenterY=19 CenterZ=0 NormalX=0 NormalY=0 NormalZ=1 AngleXU=0 Radius=15.7 StartAngle=5.81226 EndAngle=6.28319
    g31: LineSegment StartX=110.7 StartY=19 StartZ=0 EndX=113.7 EndY=19 EndZ=0
  constraints (41):
    c: Horizontal(g0)
    c: Coincident(g1,g0)
    c: Block(g1)
    c: Horizontal(g2)
    c: Distance(g2) = 3
    c: Coincident(g3,g2)
    c: Vertical(g3)
    c: Coincident(g3,g0)
    c: Block(g4)
    c: Block(g2)
    c: Coincident(g5,g2)
    c: Coincident(g5,g4)
    c: Vertical(g5)
    c: Coincident(g6,g1)
    c: Block(g6)
    c: Coincident(g7,g4)
    c: Horizontal(g7)
    c: Block(g0)
    c: Block(g7)
    c: Block(g3)
    c: Coincident(g13,g6)
    c: Weight(g8) = 1
    c: Equal(g8, g9-g12) x4
    c: Coincident(g13,g7)
    c: InternalAlignment(g8-g12 -> g13) x5
    c: InternalAlignment(g14,g13)
    c: InternalAlignment(g15,g13)
    c: InternalAlignment(g16,g13)
    c: Block(g13)
    c: Weight(g17) = 1
    c: Equal(g17, g18-g23) x6
    c: Coincident(g24,g1)
    c: InternalAlignment(g17-g23 -> g24) x7
    c: InternalAlignment(g25-g29 -> g24) x5
    c: Block(g24)
    c: Coincident(g30,g24)
    c: Coincident(g31,g6)
    c: Coincident(g31,g30)
    c: Horizontal(g31)
    c: Block(g31)
    c: Block(g30)
FEATURE [Part::Extrusion] Extrude062  label="bottom014"
  Base = -> Sketch071
  Dir = (0,0,1)
  DirMode = 2
  FaceMakerClass = Part::FaceMakerBullseye
  LengthFwd = 71.4
  LengthRev = 0
  Placement = pos=(0,0,0.3) rot=(0,0,1;0rad)
  Solid = true
  Symmetric = false
FEATURE [Part::Fillet] Fillet054
  Base = -> Extrude062
  Edges = 1 edges r=2.4: [Edge17]
FEATURE [Part::Fillet] Fillet055  label="bottom015"
  Base = -> Fillet054
  Edges = 1 edges r=2.4: [Edge36]
FEATURE [Part::Cylinder] Cylinder055
  Angle = 360
  AttacherType = Attacher::AttachEngine3D
  Height = 10
  Placement = pos=(0,0,36.15) rot=(0,0,1;0rad)
  Radius = 4
FEATURE [Part::MultiFuse] Fusion131  label="removeToCreateHoleForPlugHousing002"
  Placement = pos=(70,19,36.15) rot=(0,1,0;1.5708rad)
  Shapes = -> [Cylinder054,Cylinder055]
FEATURE [Part::Cut] Cut056  label="Bottom001"
  Base = -> Fillet055
  Placement = pos=(9,0,0) rot=(0,0,1;0rad)
  Tool = -> Fusion131
FEATURE [Part::Cut] Cut057
  Base = -> Cut055
  Tool = -> Cut056
FEATURE [Sketcher::SketchObject] Sketch072  label="topSketch021"
  FullyConstrained = true
  sketch-geometry (4):
    g0: ArcOfCircle CenterX=105 CenterY=19 CenterZ=0 NormalX=0 NormalY=0 NormalZ=1 AngleXU=0 Radius=20.6155 StartAngle=5.54125 EndAngle=6.28319
    g1: ArcOfCircle CenterX=105 CenterY=19 CenterZ=0 NormalX=0 NormalY=0 NormalZ=1 AngleXU=0 Radius=13 StartAngle=5.54125 EndAngle=6.28319
    g2: LineSegment StartX=118 StartY=19 StartZ=0 EndX=125.616 EndY=19 EndZ=0
    g3: LineSegment StartX=114.583 StartY=10.2157 StartZ=0 EndX=120.197 EndY=5.06982 EndZ=0
  constraints (7):
    c: Block(g0)
    c: Block(g1)
    c: Coincident(g2,g1)
    c: Coincident(g2,g0)
    c: Horizontal(g2)
    c: Coincident(g3,g1)
    c: Coincident(g3,g0)
FEATURE [Part::Extrusion] Extrude063  label="bottomPlugHousingBit003"
  Base = -> Sketch072
  Dir = (0,0,1)
  DirMode = 2
  FaceMakerClass = Part::FaceMakerBullseye
  LengthFwd = 72
  LengthRev = 0
  Solid = true
  Symmetric = false
FEATURE [Part::Cylinder] Cylinder056
  Angle = 360
  AttacherType = Attacher::AttachEngine3D
  Height = 20
  Placement = pos=(0,0,36.15) rot=(0,0,1;0rad)
  Radius = 14.3
FEATURE [Part::Cylinder] Cylinder057
  Angle = 360
  AttacherType = Attacher::AttachEngine3D
  Height = 10
  Placement = pos=(0,0,36.15) rot=(0,0,1;0rad)
  Radius = 4
FEATURE [Part::Box] Box034  label="removeToCreteHoleForPlugHousing047"
  AttacherType = Attacher::AttachEngine3D
  Height = 28.6
  Length = 20
  Placement = pos=(106.15,0,21.7) rot=(0,0,1;0rad)
  Width = 19
FEATURE [Part::Cylinder] Cylinder058
  Angle = 360
  AttacherType = Attacher::AttachEngine3D
  Height = 20
  Placement = pos=(0,0,36.15) rot=(0,0,1;0rad)
  Radius = 14.3
FEATURE [Part::Cylinder] Cylinder059
  Angle = 360
  AttacherType = Attacher::AttachEngine3D
  Height = 10
  Placement = pos=(0,0,36.15) rot=(0,0,1;0rad)
  Radius = 4
FEATURE [Part::MultiFuse] Fusion134  label="removeToCreteHoleForPlugHousing046"
  Placement = pos=(70,19,36) rot=(0,1,0;1.5708rad)
  Shapes = -> [Cylinder058,Cylinder059]
FEATURE [Part::Cylinder] Cylinder060
  Angle = 360
  AttacherType = Attacher::AttachEngine3D
  Height = 20
  Placement = pos=(0,0,36.15) rot=(0,0,1;0rad)
  Radius = 14
FEATURE [Part::Cylinder] Cylinder061
  Angle = 360
  AttacherType = Attacher::AttachEngine3D
  Height = 10
  Placement = pos=(0,0,36.15) rot=(0,0,1;0rad)
  Radius = 4
FEATURE [Part::MultiFuse] Fusion135  label="removeToCreteHoleForPlugHousing048"
  Placement = pos=(70,19,36) rot=(0,1,0;1.5708rad)
  Shapes = -> [Cylinder060,Cylinder061]
FEATURE [Part::Box] Box035  label="removeToCreteHoleForPlugHousing049"
  AttacherType = Attacher::AttachEngine3D
  Height = 28.6
  Length = 20
  Placement = pos=(106.15,0,21.7) rot=(0,0,1;0rad)
  Width = 19
FEATURE [Part::MultiFuse] Fusion133  label="removeToCreteHoleForPlugHousing045"
  Placement = pos=(0,0,-28.3) rot=(0,0,1;0rad)
  Shapes = -> [Box035,Fusion134]
FEATURE [Part::MultiFuse] Fusion138  label="removeToCreteHoleForPlugHousing051"
  Placement = pos=(70,19,36) rot=(0,1,0;1.5708rad)
  Shapes = -> [Cylinder056,Cylinder057]
FEATURE [Part::MultiFuse] Fusion137  label="removeToCreteHoleForPlugHousing050"
  Placement = pos=(0,0,28.3) rot=(0,0,1;0rad)
  Shapes = -> [Box034,Fusion138]
FEATURE [Part::MultiFuse] Fusion132  label="removeToCreatePlugHousingBottomBit002"
  Shapes = -> [Fusion133,Fusion137]
FEATURE [Part::MultiFuse] Fusion136  label="removeToCreatePlugHousingBottomBit003"
  Shapes = -> [Fusion135,Fusion132]
FEATURE [Part::Cut] Cut058  label="bottomPlugHousingBit002"
  Base = -> Extrude063
  Placement = pos=(-0.09,0,0) rot=(0,0,1;0rad)
  Tool = -> Fusion136
FEATURE [Sketcher::SketchObject] Sketch073  label="bottomSketch003"
  FullyConstrained = true
  sketch-geometry (45):
    g0: LineSegment StartX=6.29999 StartY=8 StartZ=0 EndX=3.29999 EndY=8 EndZ=0
    g1: LineSegment StartX=3.29999 StartY=8 StartZ=0 EndX=3.29999 EndY=-6.03275e-07 EndZ=0
    g2: ArcOfCircle CenterX=8.29999 CenterY=5 CenterZ=0 NormalX=0 NormalY=0 NormalZ=1 AngleXU=0 Radius=2 StartAngle=3.14159 EndAngle=4.71239
    g3: LineSegment StartX=6.29999 StartY=8 StartZ=0 EndX=6.29999 EndY=5 EndZ=0
    g4: ArcOfCircle CenterX=105 CenterY=19 CenterZ=0 NormalX=0 NormalY=0 NormalZ=1 AngleXU=0 Radius=12.7 StartAngle=4.71239 EndAngle=5.94289
    g5-g11: Circle x7 (B-spline internal-alignment scaffolding for g12; pole/knot coordinates omitted)
    g12: BSplineCurve PolesCount=7 KnotsCount=5 Degree=3 IsPeriodic=0
    g13-g17: GeomPoint x5 (B-spline internal-alignment scaffolding for g12; pole/knot coordinates omitted)
    g18: ArcOfCircle CenterX=105 CenterY=19 CenterZ=0 NormalX=0 NormalY=0 NormalZ=1 AngleXU=0 Radius=15.7 StartAngle=5.81226 EndAngle=6.28319
    g19: BSplineCurve PolesCount=5 KnotsCount=3 Degree=3 IsPeriodic=0
    g20: LineSegment StartX=8.29999 StartY=3 StartZ=0 EndX=101.7 EndY=3 EndZ=0
    g21: LineSegment StartX=3.29999 StartY=-6.03275e-07 StartZ=0 EndX=105 EndY=-6.03275e-07 EndZ=0
    g22: LineSegment StartX=120.974 StartY=8.71251 StartZ=0 EndX=122.332 EndY=7.83778 EndZ=0
    g23: LineSegment StartX=105 StartY=-6.03274e-07 StartZ=0 EndX=113 EndY=-6.03274e-07 EndZ=0
    g24: ArcOfCircle CenterX=105 CenterY=19 CenterZ=0 NormalX=0 NormalY=0 NormalZ=1 AngleXU=0 Radius=20.6155 StartAngle=5.11091 EndAngle=5.71103
    g25: ArcOfCircle CenterX=117.7 CenterY=19 CenterZ=0 NormalX=0 NormalY=0 NormalZ=1 AngleXU=0 Radius=3 StartAngle=1.2e-15 EndAngle=2.10468
    g26: Circle CenterX=116.345 CenterY=16.3232 CenterZ=0 NormalX=0 NormalY=0 NormalZ=1 AngleXU=0 Radius=1
    g27: Circle CenterX=117.24 CenterY=15.7584 CenterZ=0 NormalX=0 NormalY=0 NormalZ=1 AngleXU=0 Radius=1
    g28: Circle CenterX=116.972 CenterY=14.7612 CenterZ=0 NormalX=0 NormalY=0 NormalZ=1 AngleXU=0 Radius=1
    g29: BSplineCurve PolesCount=3 KnotsCount=2 Degree=2 IsPeriodic=0
    g30: GeomPoint X=116.345 Y=16.3232 Z=0
    g31: GeomPoint X=116.972 Y=14.7612 Z=0
    g32: Circle CenterX=115.828 CenterY=17.157 CenterZ=0 NormalX=0 NormalY=0 NormalZ=1 AngleXU=0 Radius=1
    g33: Circle CenterX=115.841 CenterY=16.639 CenterZ=0 NormalX=0 NormalY=0 NormalZ=1 AngleXU=0 Radius=1
    g34: Circle CenterX=116.345 CenterY=16.3232 CenterZ=0 NormalX=0 NormalY=0 NormalZ=1 AngleXU=0 Radius=1
    g35: BSplineCurve PolesCount=3 KnotsCount=2 Degree=2 IsPeriodic=0
    g36: GeomPoint X=115.828 Y=17.157 Z=0
    g37: GeomPoint X=116.345 Y=16.3232 Z=0
    g38: LineSegment StartX=115.828 StartY=17.157 StartZ=0 EndX=115.828 EndY=20.8307 EndZ=0
    g39: Circle CenterX=115.828 CenterY=20.8307 CenterZ=0 NormalX=0 NormalY=0 NormalZ=1 AngleXU=0 Radius=1
    g40: Circle CenterX=115.831 CenterY=21.3396 CenterZ=0 NormalX=0 NormalY=0 NormalZ=1 AngleXU=0 Radius=1
    g41: Circle CenterX=116.173 CenterY=21.5825 CenterZ=0 NormalX=0 NormalY=0 NormalZ=1 AngleXU=0 Radius=1
    g42: BSplineCurve PolesCount=3 KnotsCount=2 Degree=2 IsPeriodic=0
    g43: GeomPoint X=115.828 Y=20.8307 Z=0
    g44: GeomPoint X=116.173 Y=21.5825 Z=0
  constraints (70):
    c: Horizontal(g0)
    c: Distance(g0) = 3
    c: Coincident(g1,g0)
    c: Vertical(g1)
    c: Block(g2)
    c: Block(g0)
    c: Coincident(g3,g0)
    c: Coincident(g3,g2)
    c: Vertical(g3)
    c: Block(g1)
    c: Block(g4)
    c: Coincident(g19,g4)
    c: Block(g19)
    c: Equal(g5, g6-g11) x6
    c: InternalAlignment(g5-g11 -> g12) x7
    c: InternalAlignment(g13-g17 -> g12) x5
    c: Block(g12)
    c: Coincident(g18,g12)
    c: Block(g18)
    c: Coincident(g20,g2)
    c: Coincident(g20,g19)
    c: Horizontal(g20)
    c: Distance(g20) = 93.4
    c: Coincident(g21,g1)
    c: Horizontal(g21)
    c: Distance(g21) = 101.7
    c: Horizontal(g23)
    c: Distance(g23) = 8
    c: Coincident(g24,g23)
    c: Block(g23)
    c: Coincident(g22,g24)
    c: Block(g24)
    c: Block(g22)
    c: Distance(g22) = 1.61553
    c: Coincident(g25,g18)
    c: Block(g25)
    c: Weight(g26) = 1
    c: Equal(g26,g27)
    c: Equal(g26,g28)
    c: Coincident(g29,g4)
    c: InternalAlignment(g26,g29)
    c: InternalAlignment(g27,g29)
    c: InternalAlignment(g28,g29)
    c: InternalAlignment(g30,g29)
    c: InternalAlignment(g31,g29)
    c: Block(g29)
    c: Weight(g32) = 1
    c: Equal(g32,g33)
    c: Equal(g32,g34)
    c: Coincident(g35,g29)
    c: InternalAlignment(g32,g35)
    c: InternalAlignment(g33,g35)
    c: InternalAlignment(g34,g35)
    c: InternalAlignment(g36,g35)
    c: InternalAlignment(g37,g35)
    c: Block(g35)
    c: Coincident(g38,g35)
    c: Vertical(g38)
    c: Block(g38)
    c: Coincident(g42,g38)
    c: Weight(g39) = 1
    c: Equal(g39,g40)
    c: Equal(g39,g41)
    c: Coincident(g42,g25)
    c: InternalAlignment(g39,g42)
    c: InternalAlignment(g40,g42)
    c: InternalAlignment(g41,g42)
    c: InternalAlignment(g43,g42)
    c: InternalAlignment(g44,g42)
    c: Block(g42)
FEATURE [Part::Extrusion] Extrude064  label="bottom016"
  Base = -> Sketch073
  Dir = (0,0,1)
  DirMode = 2
  FaceMakerClass = Part::FaceMakerBullseye
  LengthFwd = 71.4
  LengthRev = 0
  Placement = pos=(0,0,0.3) rot=(0,0,1;0rad)
  Solid = true
  Symmetric = false
FEATURE [Part::Revolution] Revolve157  label="removeToCreateScrewAndThreadedInsertHole063"
  Angle = 360
  Axis = (0,1,0)
  Base = (0,0,0)
  FaceMakerClass = Part::FaceMakerBullseye
  Placement = pos=(12.5,0,10) rot=(0,0,1;0rad)
  Solid = false
  Source = -> Face141
  Symmetric = false
FEATURE [Sketcher::SketchObject] Sketch074
  FullyConstrained = true
  Placement = pos=(117,19,0) rot=(0.57735,0.57735,0.57735;2.0944rad)
  sketch-geometry (48):
    g0: LineSegment StartX=-49.19 StartY=69.25 StartZ=0 EndX=-49.19 EndY=66.25 EndZ=0
    g1: LineSegment StartX=-49.19 StartY=63.5 StartZ=0 EndX=-49.19 EndY=60.5 EndZ=0
    g2: LineSegment StartX=-49.19 StartY=57.75 StartZ=0 EndX=-49.19 EndY=54.75 EndZ=0
    g3: LineSegment StartX=-49.19 StartY=52 StartZ=0 EndX=-49.19 EndY=49 EndZ=0
    g4: LineSegment StartX=-49.19 StartY=46.25 StartZ=0 EndX=-49.19 EndY=43.25 EndZ=0
    g5: LineSegment StartX=-49.19 StartY=40.5 StartZ=0 EndX=-49.19 EndY=37.5 EndZ=0
    g6: LineSegment StartX=-49.19 StartY=34.5 StartZ=0 EndX=-49.19 EndY=31.5 EndZ=0
    g7: LineSegment StartX=-49.19 StartY=28.75 StartZ=0 EndX=-49.19 EndY=25.75 EndZ=0
    g8: LineSegment StartX=-49.19 StartY=23 StartZ=0 EndX=-49.19 EndY=20 EndZ=0
    g9: LineSegment StartX=-49.19 StartY=17.25 StartZ=0 EndX=-49.19 EndY=14.25 EndZ=0
    g10: LineSegment StartX=-49.19 StartY=11.5 StartZ=0 EndX=-49.19 EndY=8.5 EndZ=0
    g11: LineSegment StartX=-49.19 StartY=5.75 StartZ=0 EndX=-49.19 EndY=2.75 EndZ=0
    g12: ArcOfCircle CenterX=-1.5 CenterY=67.75 CenterZ=0 NormalX=0 NormalY=0 NormalZ=1 AngleXU=0 Radius=1.5 StartAngle=4.71239 EndAngle=7.85398
    g13: ArcOfCircle CenterX=-1.5 CenterY=62 CenterZ=0 NormalX=0 NormalY=0 NormalZ=1 AngleXU=0 Radius=1.5 StartAngle=4.71239 EndAngle=7.85398
    g14: ArcOfCircle CenterX=-1.5 CenterY=56.25 CenterZ=0 NormalX=0 NormalY=0 NormalZ=1 AngleXU=0 Radius=1.5 StartAngle=4.71239 EndAngle=7.85398
    g15: ArcOfCircle CenterX=-11.49 CenterY=50.5 CenterZ=0 NormalX=0 NormalY=0 NormalZ=1 AngleXU=0 Radius=1.5 StartAngle=4.71239 EndAngle=7.85398
    g16: ArcOfCircle CenterX=-16.28 CenterY=44.75 CenterZ=0 NormalX=0 NormalY=0 NormalZ=1 AngleXU=0 Radius=1.5 StartAngle=4.71239 EndAngle=7.85398
    g17: ArcOfCircle CenterX=-18.2337 CenterY=39 CenterZ=0 NormalX=0 NormalY=0 NormalZ=1 AngleXU=0 Radius=1.5 StartAngle=4.71485 EndAngle=7.85398
    g18: ArcOfCircle CenterX=-16.2837 CenterY=27.25 CenterZ=0 NormalX=0 NormalY=0 NormalZ=1 AngleXU=0 Radius=1.5 StartAngle=4.71485 EndAngle=7.85398
    g19: ArcOfCircle CenterX=-18.2337 CenterY=33 CenterZ=0 NormalX=0 NormalY=0 NormalZ=1 AngleXU=0 Radius=1.5 StartAngle=4.71485 EndAngle=7.85398
    g20: ArcOfCircle CenterX=-11.49 CenterY=21.5 CenterZ=0 NormalX=0 NormalY=0 NormalZ=1 AngleXU=0 Radius=1.5 StartAngle=4.71239 EndAngle=7.85398
    g21: ArcOfCircle CenterX=-1.5 CenterY=4.25 CenterZ=0 NormalX=0 NormalY=0 NormalZ=1 AngleXU=0 Radius=1.5 StartAngle=4.71239 EndAngle=7.85398
    g22: ArcOfCircle CenterX=-1.5 CenterY=10 CenterZ=0 NormalX=0 NormalY=0 NormalZ=1 AngleXU=0 Radius=1.5 StartAngle=4.71239 EndAngle=7.85398
    g23: ArcOfCircle CenterX=-1.5 CenterY=15.75 CenterZ=0 NormalX=0 NormalY=0 NormalZ=1 AngleXU=0 Radius=1.5 StartAngle=4.71239 EndAngle=7.85398
    g24: LineSegment StartX=-49.19 StartY=69.25 StartZ=0 EndX=-1.5 EndY=69.25 EndZ=0
    g25: LineSegment StartX=-49.19 StartY=66.25 StartZ=0 EndX=-1.5 EndY=66.25 EndZ=0
    g26: LineSegment StartX=-49.19 StartY=63.5 StartZ=0 EndX=-1.5 EndY=63.5 EndZ=0
    g27: LineSegment StartX=-49.19 StartY=60.5 StartZ=0 EndX=-1.5 EndY=60.5 EndZ=0
    g28: LineSegment StartX=-49.19 StartY=57.75 StartZ=0 EndX=-1.5 EndY=57.75 EndZ=0
    g29: LineSegment StartX=-49.19 StartY=54.75 StartZ=0 EndX=-1.5 EndY=54.75 EndZ=0
    g30: LineSegment StartX=-49.19 StartY=52 StartZ=0 EndX=-11.49 EndY=52 EndZ=0
    g31: LineSegment StartX=-49.19 StartY=49 StartZ=0 EndX=-11.49 EndY=49 EndZ=0
    g32: LineSegment StartX=-49.19 StartY=46.25 StartZ=0 EndX=-16.28 EndY=46.25 EndZ=0
    g33: LineSegment StartX=-49.19 StartY=43.25 StartZ=0 EndX=-16.28 EndY=43.25 EndZ=0
    g34: LineSegment StartX=-49.19 StartY=40.5 StartZ=0 EndX=-18.2337 EndY=40.5 EndZ=0
    g35: LineSegment StartX=-49.19 StartY=37.5 StartZ=0 EndX=-18.23 EndY=37.5 EndZ=0
    g36: LineSegment StartX=-49.19 StartY=34.5 StartZ=0 EndX=-18.2337 EndY=34.5 EndZ=0
    g37: LineSegment StartX=-49.19 StartY=31.5 StartZ=0 EndX=-18.23 EndY=31.5 EndZ=0
    g38: LineSegment StartX=-49.19 StartY=28.75 StartZ=0 EndX=-16.2837 EndY=28.75 EndZ=0
    g39: LineSegment StartX=-49.19 StartY=25.75 StartZ=0 EndX=-16.28 EndY=25.75 EndZ=0
    g40: LineSegment StartX=-49.19 StartY=23 StartZ=0 EndX=-11.49 EndY=23 EndZ=0
    g41: LineSegment StartX=-49.19 StartY=20 StartZ=0 EndX=-11.49 EndY=20 EndZ=0
    g42: LineSegment StartX=-49.19 StartY=17.25 StartZ=0 EndX=-1.5 EndY=17.25 EndZ=0
    g43: LineSegment StartX=-49.19 StartY=14.25 StartZ=0 EndX=-1.5 EndY=14.25 EndZ=0
    g44: LineSegment StartX=-49.19 StartY=11.5 StartZ=0 EndX=-1.5 EndY=11.5 EndZ=0
    g45: LineSegment StartX=-49.19 StartY=8.5 StartZ=0 EndX=-1.5 EndY=8.5 EndZ=0
    g46: LineSegment StartX=-49.19 StartY=5.75 StartZ=0 EndX=-1.5 EndY=5.75 EndZ=0
    g47: LineSegment StartX=-49.19 StartY=2.75 StartZ=0 EndX=-1.5 EndY=2.75 EndZ=0
  constraints (120):
    c: Vertical(g0)
    c: Distance(g0) = 3
    c: Block(g0)
    c: Vertical(g1)
    c: Distance(g1) = 3
    c: Vertical(g2)
    c: Equal(g0,g2) = 3
    c: Block(g2)
    c: Vertical(g3)
    c: Equal(g1,g3) = 3
    c: Vertical(g4)
    c: Equal(g0,g4) = 3
    c: Block(g4)
    c: Vertical(g5)
    c: Equal(g1,g5) = 3
    c: Vertical(g6)
    c: Equal(g0,g6) = 3
    c: Block(g6)
    c: Vertical(g7)
    c: Equal(g1,g7) = 3
    c: Vertical(g8)
    c: Equal(g0,g8) = 3
    c: Block(g8)
    c: Vertical(g9)
    c: Equal(g1,g9) = 3
    c: Vertical(g10)
    c: Equal(g0,g10) = 3
    c: Block(g10)
    c: Vertical(g11)
    c: Equal(g1,g11) = 3
    c: Block(g12)
    c: Block(g13)
    c: Block(g14)
    c: Block(g15)
    c: Block(g16)
    c: Block(g17)
    c: Block(g18)
    c: Block(g19)
    c: Block(g20)
    c: Block(g21)
    c: Block(g22)
    c: Block(g23)
    c: Block(g11)
    c: Block(g9)
    c: Block(g7)
    c: Block(g5)
    c: Block(g3)
    c: Block(g1)
    c: Coincident(g24,g0)
    c: Coincident(g24,g12)
    c: Horizontal(g24)
    c: Coincident(g25,g0)
    c: Coincident(g25,g12)
    c: Horizontal(g25)
    c: Coincident(g26,g1)
    c: Coincident(g26,g13)
    c: Horizontal(g26)
    c: Coincident(g27,g1)
    c: Coincident(g27,g13)
    c: Horizontal(g27)
    c: Coincident(g28,g2)
    c: Coincident(g28,g14)
    c: Horizontal(g28)
    c: Coincident(g29,g2)
    c: Coincident(g29,g14)
    c: Horizontal(g29)
    c: Coincident(g30,g3)
    c: Coincident(g30,g15)
    c: Horizontal(g30)
    c: Coincident(g31,g3)
    c: Coincident(g31,g15)
    c: Horizontal(g31)
    c: Coincident(g32,g4)
    c: Coincident(g32,g16)
    c: Horizontal(g32)
    c: Coincident(g33,g4)
    c: Coincident(g33,g16)
    c: Horizontal(g33)
    c: Coincident(g34,g5)
    c: Coincident(g34,g17)
    c: Horizontal(g34)
    c: Coincident(g35,g5)
    c: Coincident(g35,g17)
    c: Horizontal(g35)
    c: Coincident(g36,g6)
    c: Coincident(g36,g19)
    c: Horizontal(g36)
    c: Coincident(g37,g6)
    c: Coincident(g37,g19)
    c: Horizontal(g37)
    c: Coincident(g38,g7)
    c: Coincident(g38,g18)
    c: Horizontal(g38)
    c: Coincident(g39,g7)
    c: Coincident(g39,g18)
    c: Horizontal(g39)
    c: Coincident(g40,g8)
    c: Coincident(g40,g20)
    c: Horizontal(g40)
    c: Coincident(g41,g8)
    c: Coincident(g41,g20)
    c: Horizontal(g41)
    c: Coincident(g42,g9)
    c: Coincident(g42,g23)
    c: Horizontal(g42)
    c: Coincident(g43,g9)
    c: Coincident(g43,g23)
    c: Horizontal(g43)
    c: Coincident(g44,g10)
    c: Coincident(g44,g22)
    c: Horizontal(g44)
    c: Coincident(g45,g10)
    c: Coincident(g45,g22)
    c: Horizontal(g45)
    c: Coincident(g46,g11)
    c: Coincident(g46,g21)
    c: Horizontal(g46)
    c: Coincident(g47,g11)
    c: Coincident(g47,g21)
    c: Horizontal(g47)
FEATURE [Part::Extrusion] Extrude065
  Base = -> Sketch074
  Dir = (1,0,0)
  DirMode = 2
  FaceMakerClass = Part::FaceMakerBullseye
  LengthFwd = 23
  LengthRev = 0
  Placement = pos=(-19,0,0) rot=(0,0,1;0rad)
  Solid = true
  Symmetric = false
FEATURE [Part::Fillet] Fillet056  label="removeToCreateVentalationHoles003"
  Base = -> Extrude065
  Edges = <same value as first occurrence — deduplicated (x6 in doc)>
  Placement = pos=(7,0.02,0) rot=(0,0,1;0rad)
FEATURE [Part::Revolution] Revolve158  label="removeToCreateScrewAndThreadedInsertHole065"
  Angle = 360
  Axis = (0,1,0)
  Base = (0,0,0)
  FaceMakerClass = Part::FaceMakerBullseye
  Placement = pos=(12.5,0,62) rot=(0,0,1;0rad)
  Solid = false
  Source = -> Face146
  Symmetric = false
FEATURE [Part::Revolution] Revolve159  label="removeToCreateScrewAndThreadedInsertHole066"
  Angle = 360
  Axis = (0,1,0)
  Base = (0,0,0)
  FaceMakerClass = Part::FaceMakerBullseye
  Placement = pos=(89.5,0,68.5) rot=(0,0,1;0rad)
  Solid = false
  Source = -> Face143
  Symmetric = false
FEATURE [Part::Revolution] Revolve160  label="removeToCreateScrewAndThreadedInsertHole067"
  Angle = 360
  Axis = (0,1,0)
  Base = (0,0,0)
  FaceMakerClass = Part::FaceMakerBullseye
  Placement = pos=(89.5,0,3.5) rot=(0,0,1;0rad)
  Solid = false
  Source = -> Face142
  Symmetric = false
FEATURE [Part::Revolution] Revolve161  label="removeToCreateScrewAndThreadedInsertHole068"
  Angle = 360
  Axis = (0,1,0)
  Base = (0,0,0)
  FaceMakerClass = Part::FaceMakerBullseye
  Placement = pos=(109.5,4.7,3.5) rot=(0,0,1;0rad)
  Solid = false
  Source = -> Face145
  Symmetric = false
FEATURE [Part::Revolution] Revolve162  label="removeToCreateScrewAndThreadedInsertHole069"
  Angle = 360
  Axis = (0,1,0)
  Base = (0,0,0)
  FaceMakerClass = Part::FaceMakerBullseye
  Placement = pos=(109.5,4.7,68.5) rot=(0,0,1;0rad)
  Solid = false
  Source = -> Face144
  Symmetric = false
FEATURE [Part::MultiFuse] Fusion141  label="removeToCreateScrewAndThreadedInsertHole064"
  Shapes = -> [Revolve162,Revolve161,Revolve160,Revolve159,Revolve158,Revolve157]
FEATURE [Part::Cylinder] Cylinder062
  Angle = 360
  AttacherType = Attacher::AttachEngine3D
  Height = 20
  Placement = pos=(0,0,36.15) rot=(0,0,1;0rad)
  Radius = 14
FEATURE [Part::Cylinder] Cylinder063
  Angle = 360
  AttacherType = Attacher::AttachEngine3D
  Height = 10
  Placement = pos=(0,0,36.15) rot=(0,0,1;0rad)
  Radius = 4
FEATURE [Part::MultiFuse] Fusion139  label="removeToCreteHoleForPlugHousing052"
  Placement = pos=(70,19,36) rot=(0,1,0;1.5708rad)
  Shapes = -> [Cylinder062,Cylinder063]
FEATURE [Part::Cut] Cut060  label="bottom017"
  Base = -> Extrude064
  Tool = -> Fusion139
FEATURE [Part::Cut] Cut061  label="bottom019"
  Base = -> Cut060
  Tool = -> Fusion141
FEATURE [Part::MultiFuse] Fusion140  label="bottom018"
  Shapes = -> [Cut061,Cut058]
FEATURE [Part::Cut] Cut059  label="bottom020"
  Base = -> Fusion140
  Tool = -> Fillet056
FEATURE [Part::Box] Box036  label="Cube021"
  AttacherType = Attacher::AttachEngine3D
  Height = 80
  Length = 26
  Placement = pos=(0,-1,-5) rot=(0,0,1;0rad)
  Width = 11
FEATURE [Part::Cut] Cut062  label="removeFromBottom002"
  Base = -> Cut057
  Tool = -> Box036
FEATURE [Part::Cut] Cut063
  Base = -> Cut059
  Tool = -> Cut062
FEATURE [Part::Cut] Cut064  label="pcbStands"
  Base = -> Fusion095
  Tool = -> Fusion127
FEATURE [Sketcher::SketchObject] Sketch075  label="topSketch022"
  FullyConstrained = true
  sketch-geometry (6):
    g0: LineSegment StartX=19 StartY=38 StartZ=0 EndX=117 EndY=38 EndZ=0
    g1: ArcOfCircle CenterX=19 CenterY=19 CenterZ=0 NormalX=0 NormalY=0 NormalZ=1 AngleXU=0 Radius=19 StartAngle=1.5708 EndAngle=3.14159
    g2: LineSegment StartX=117 StartY=38 StartZ=0 EndX=117 EndY=19 EndZ=0
    g3: LineSegment StartX=98 StartY=1.0161e-12 StartZ=0 EndX=5.22862e-06 EndY=1.0161e-12 EndZ=0
    g4: LineSegment StartX=5.22862e-06 StartY=19 StartZ=0 EndX=5.22862e-06 EndY=1.0161e-12 EndZ=0
    g5: ArcOfCircle CenterX=98 CenterY=19 CenterZ=0 NormalX=0 NormalY=0 NormalZ=1 AngleXU=0 Radius=19 StartAngle=4.71239 EndAngle=6.28319
  constraints (16):
    c: Horizontal(g0)
    c: Distance(g0) = 98
    c: Coincident(g1,g0)
    c: Block(g1)
    c: Coincident(g2,g0)
    c: Vertical(g2)
    c: Distance(g2) = 19
    c: Horizontal(g3)
    c: Coincident(g4,g1)
    c: Vertical(g4)
    c: Coincident(g3,g4)
    c: Block(g3)
    c: Coincident(g5,g2)
    c: Coincident(g5,g3)
    c: Block(g0)
    c: Block(g5)
FEATURE [Part::Extrusion] Extrude067  label="sideB003"
  Base = -> Sketch075
  Dir = (0,0,1)
  DirMode = 2
  FaceMakerClass = Part::FaceMakerBullseye
  LengthFwd = 3
  LengthRev = 0
  Placement = pos=(0,0,71.7) rot=(0,0,1;0rad)
  Solid = true
  Symmetric = false
FEATURE [Sketcher::SketchObject] Sketch076  label="topSketch023"
  FullyConstrained = true
  sketch-geometry (6):
    g0: LineSegment StartX=19 StartY=38 StartZ=0 EndX=117 EndY=38 EndZ=0
    g1: ArcOfCircle CenterX=19 CenterY=19 CenterZ=0 NormalX=0 NormalY=0 NormalZ=1 AngleXU=0 Radius=19 StartAngle=1.5708 EndAngle=3.14159
    g2: LineSegment StartX=117 StartY=38 StartZ=0 EndX=117 EndY=19 EndZ=0
    g3: LineSegment StartX=98 StartY=1.0161e-12 StartZ=0 EndX=5.22862e-06 EndY=1.0161e-12 EndZ=0
    g4: LineSegment StartX=5.22862e-06 StartY=19 StartZ=0 EndX=5.22862e-06 EndY=1.0161e-12 EndZ=0
    g5: ArcOfCircle CenterX=98 CenterY=19 CenterZ=0 NormalX=0 NormalY=0 NormalZ=1 AngleXU=0 Radius=19 StartAngle=4.71239 EndAngle=6.28319
  constraints (16):
    c: Horizontal(g0)
    c: Distance(g0) = 98
    c: Coincident(g1,g0)
    c: Block(g1)
    c: Coincident(g2,g0)
    c: Vertical(g2)
    c: Distance(g2) = 19
    c: Horizontal(g3)
    c: Coincident(g4,g1)
    c: Vertical(g4)
    c: Coincident(g3,g4)
    c: Block(g3)
    c: Coincident(g5,g2)
    c: Coincident(g5,g3)
    c: Block(g0)
    c: Block(g5)
FEATURE [Part::Extrusion] Extrude066  label="sideA003"
  Base = -> Sketch076
  Dir = (0,0,1)
  DirMode = 2
  FaceMakerClass = Part::FaceMakerBullseye
  LengthFwd = 3
  LengthRev = 0
  Placement = pos=(0,0,-2.7) rot=(0,0,1;0rad)
  Solid = true
  Symmetric = false
FEATURE [Part::MultiFuse] Fusion142  label="removeFromBottom003"
  Placement = pos=(2,0,0) rot=(0,0,1;0rad)
  Shapes = -> [Extrude066,Extrude067]
FEATURE [Part::Cut] Cut065  label="screwRetainers002"
  Base = -> Fusion096
  Tool = -> Fusion142
FEATURE [Sketcher::SketchObject] Sketch077
  FullyConstrained = true
  Placement = pos=(117,19,0) rot=(0.57735,0.57735,0.57735;2.0944rad)
  sketch-geometry (8):
    g0: LineSegment StartX=-49.19 StartY=63.5 StartZ=0 EndX=-49.19 EndY=60.5 EndZ=0
    g1: LineSegment StartX=-49.19 StartY=11.5 StartZ=0 EndX=-49.19 EndY=8.5 EndZ=0
    g2: ArcOfCircle CenterX=-1.5 CenterY=62 CenterZ=0 NormalX=0 NormalY=0 NormalZ=1 AngleXU=0 Radius=1.5 StartAngle=4.71239 EndAngle=7.85398
    g3: ArcOfCircle CenterX=-1.5 CenterY=10 CenterZ=0 NormalX=0 NormalY=0 NormalZ=1 AngleXU=0 Radius=1.5 StartAngle=4.71239 EndAngle=7.85398
    g4: LineSegment StartX=-49.19 StartY=63.5 StartZ=0 EndX=-1.5 EndY=63.5 EndZ=0
    g5: LineSegment StartX=-49.19 StartY=60.5 StartZ=0 EndX=-1.5 EndY=60.5 EndZ=0
    g6: LineSegment StartX=-49.19 StartY=11.5 StartZ=0 EndX=-1.5 EndY=11.5 EndZ=0
    g7: LineSegment StartX=-49.19 StartY=8.5 StartZ=0 EndX=-1.5 EndY=8.5 EndZ=0
  constraints (19):
    c: Vertical(g0)
    c: Distance(g0) = 3
    c: Vertical(g1)
    c: Block(g1)
    c: Block(g2)
    c: Block(g3)
    c: Block(g0)
    c: Coincident(g4,g0)
    c: Coincident(g4,g2)
    c: Horizontal(g4)
    c: Coincident(g5,g0)
    c: Coincident(g5,g2)
    c: Horizontal(g5)
    c: Coincident(g6,g1)
    c: Coincident(g6,g3)
    c: Horizontal(g6)
    c: Coincident(g7,g1)
    c: Coincident(g7,g3)
    c: Horizontal(g7)
FEATURE [Part::Extrusion] Extrude068
  Base = -> Sketch077
  Dir = (1,0,0)
  DirMode = 2
  FaceMakerClass = Part::FaceMakerBullseye
  LengthFwd = 10
  LengthRev = 0
  Solid = true
  Symmetric = false
FEATURE [Part::Fillet] Fillet057  label="removeFromtMoreFrontCaseScrewRetainers002"
  Base = -> Extrude068
  Edges = 4 edges r=1.49: [Edge6,Edge11,Edge18,Edge23]
  Placement = pos=(-12,0,0) rot=(0,0,1;0rad)
FEATURE [Sketcher::SketchObject] Sketch078
  FullyConstrained = true
  Placement = pos=(117,19,0) rot=(0.57735,0.57735,0.57735;2.0944rad)
  sketch-geometry (8):
    g0: LineSegment StartX=-49.19 StartY=69.25 StartZ=0 EndX=-49.19 EndY=66.25 EndZ=0
    g1: LineSegment StartX=-49.19 StartY=5.75 StartZ=0 EndX=-49.19 EndY=2.75 EndZ=0
    g2: ArcOfCircle CenterX=-1.5 CenterY=67.75 CenterZ=0 NormalX=0 NormalY=0 NormalZ=1 AngleXU=0 Radius=1.5 StartAngle=4.71239 EndAngle=7.85398
    g3: ArcOfCircle CenterX=-1.5 CenterY=4.25 CenterZ=0 NormalX=0 NormalY=0 NormalZ=1 AngleXU=0 Radius=1.5 StartAngle=4.71239 EndAngle=7.85398
    g4: LineSegment StartX=-49.19 StartY=69.25 StartZ=0 EndX=-1.5 EndY=69.25 EndZ=0
    g5: LineSegment StartX=-49.19 StartY=66.25 StartZ=0 EndX=-1.5 EndY=66.25 EndZ=0
    g6: LineSegment StartX=-49.19 StartY=5.75 StartZ=0 EndX=-1.5 EndY=5.75 EndZ=0
    g7: LineSegment StartX=-49.19 StartY=2.75 StartZ=0 EndX=-1.5 EndY=2.75 EndZ=0
  constraints (19):
    c: Vertical(g0)
    c: Distance(g0) = 3
    c: Block(g0)
    c: Vertical(g1)
    c: Block(g2)
    c: Block(g3)
    c: Block(g1)
    c: Coincident(g4,g0)
    c: Coincident(g4,g2)
    c: Horizontal(g4)
    c: Coincident(g5,g0)
    c: Coincident(g5,g2)
    c: Horizontal(g5)
    c: Coincident(g6,g1)
    c: Coincident(g6,g3)
    c: Horizontal(g6)
    c: Coincident(g7,g1)
    c: Coincident(g7,g3)
    c: Horizontal(g7)
FEATURE [Part::Extrusion] Extrude069
  Base = -> Sketch078
  Dir = (1,0,0)
  DirMode = 2
  FaceMakerClass = Part::FaceMakerBullseye
  LengthFwd = 10
  LengthRev = 0
  Solid = true
  Symmetric = false
FEATURE [Part::Fillet] Fillet058  label="removeFromtMoreFrontCaseScrewRetainers003"
  Base = -> Extrude069
  Edges = 4 edges r=1.49: [Edge6,Edge11,Edge18,Edge23]
  Placement = pos=(-4,0,0) rot=(0,0,1;0rad)
FEATURE [Part::Cut] Cut066
  Base = -> Cut065
  Tool = -> Fillet058
FEATURE [Part::Cut] Cut067  label="screwPillars"
  Base = -> Cut066
  Tool = -> Fillet057
FEATURE [Part::MultiFuse] Fusion143  label="bottom021"
  Shapes = -> [Cut031,Cut063]
FEATURE [Part::Cylinder] Cylinder
  Angle = 360
  AttacherType = Attacher::AttachEngine3D
  Height = 10
  Placement = pos=(20.65,12,4.68) rot=(1,0,0;1.5708rad)
  Radius = 2
FEATURE [Part::Cylinder] Cylinder064
  Angle = 360
  AttacherType = Attacher::AttachEngine3D
  Height = 10
  Placement = pos=(20.65,12,67.38) rot=(1,0,0;1.5708rad)
  Radius = 2
FEATURE [Part::Cylinder] Cylinder065
  Angle = 360
  AttacherType = Attacher::AttachEngine3D
  Height = 10
  Placement = pos=(77.15,12,67.38) rot=(1,0,0;1.5708rad)
  Radius = 2
FEATURE [Part::Cylinder] Cylinder066
  Angle = 360
  AttacherType = Attacher::AttachEngine3D
  Height = 10
  Placement = pos=(77.15,12,4.68) rot=(1,0,0;1.5708rad)
  Radius = 2
FEATURE [Part::MultiFuse] Fusion144  label="removeFromThreadedInsertHousing"
  Shapes = -> [Cylinder065,Cylinder064,Cylinder,Cylinder066]
FEATURE [Part::Cut] Cut068  label="pcbStands001"
  Base = -> Cut064
  Tool = -> Fusion144
FEATURE [Part::MultiFuse] Fusion145
  Shapes = -> [Cut068,Fusion143]
FEATURE [Part::MultiFuse] Fusion146
  Shapes = -> [Fusion145]
FEATURE [Part::MultiFuse] Fusion147  label="bottom022"
  Shapes = -> [Cut067,Fusion146]
FEATURE [Part::MultiFuse] Fusion148  label="casePillars005"
  Shapes = -> [Cut047,Fusion092]
FEATURE [Part::MultiFuse] Fusion149  label="bottom023"
  Shapes = -> [Fusion124,Fusion113,Fusion147]
FEATURE [Part::MultiFuse] Fusion150  label="topBits"
  Shapes = -> [Cut025,Fusion148,Cut030,Fillet034]
FEATURE [Part::Feature] Face149 .. Face152  x4 (patterned run collapsed; names and placements below)
  shape: bbox 3.2 x 1.5 x 2e-07 mm, 1 faces, 0 solids (baked)
FEATURE [Part::Feature] Face153
  shape: bbox 3.6 x 3.2 x 2e-07 mm, 1 faces, 0 solids (baked)
FEATURE [Part::Feature] Face154
  shape: bbox 3.6 x 3.2 x 2e-07 mm, 1 faces, 0 solids (baked)
FEATURE [Sketcher::SketchObject] Sketch079  label="topSketch024"
  FullyConstrained = true
  sketch-geometry (6):
    g0: LineSegment StartX=19 StartY=38 StartZ=0 EndX=117 EndY=38 EndZ=0
    g1: ArcOfCircle CenterX=19 CenterY=19 CenterZ=0 NormalX=0 NormalY=0 NormalZ=1 AngleXU=0 Radius=19 StartAngle=1.5708 EndAngle=3.14159
    g2: LineSegment StartX=117 StartY=38 StartZ=0 EndX=117 EndY=19 EndZ=0
    g3: LineSegment StartX=98 StartY=1.0161e-12 StartZ=0 EndX=5.22862e-06 EndY=1.0161e-12 EndZ=0
    g4: LineSegment StartX=5.22862e-06 StartY=19 StartZ=0 EndX=5.22862e-06 EndY=1.0161e-12 EndZ=0
    g5: ArcOfCircle CenterX=98 CenterY=19 CenterZ=0 NormalX=0 NormalY=0 NormalZ=1 AngleXU=0 Radius=19 StartAngle=4.71239 EndAngle=6.28319
  constraints (16):
    c: Horizontal(g0)
    c: Distance(g0) = 98
    c: Coincident(g1,g0)
    c: Block(g1)
    c: Coincident(g2,g0)
    c: Vertical(g2)
    c: Distance(g2) = 19
    c: Horizontal(g3)
    c: Coincident(g4,g1)
    c: Vertical(g4)
    c: Coincident(g3,g4)
    c: Block(g3)
    c: Coincident(g5,g2)
    c: Coincident(g5,g3)
    c: Block(g0)
    c: Block(g5)
FEATURE [Sketcher::SketchObject] Sketch080  label="topSketch025"
  FullyConstrained = true
  sketch-geometry (6):
    g0: LineSegment StartX=19 StartY=38 StartZ=0 EndX=117 EndY=38 EndZ=0
    g1: ArcOfCircle CenterX=19 CenterY=19 CenterZ=0 NormalX=0 NormalY=0 NormalZ=1 AngleXU=0 Radius=19 StartAngle=1.5708 EndAngle=3.14159
    g2: LineSegment StartX=117 StartY=38 StartZ=0 EndX=117 EndY=19 EndZ=0
    g3: LineSegment StartX=98 StartY=1.0161e-12 StartZ=0 EndX=5.22862e-06 EndY=1.0161e-12 EndZ=0
    g4: LineSegment StartX=5.22862e-06 StartY=19 StartZ=0 EndX=5.22862e-06 EndY=1.0161e-12 EndZ=0
    g5: ArcOfCircle CenterX=98 CenterY=19 CenterZ=0 NormalX=0 NormalY=0 NormalZ=1 AngleXU=0 Radius=19 StartAngle=4.71239 EndAngle=6.28319
  constraints (16):
    c: Horizontal(g0)
    c: Distance(g0) = 98
    c: Coincident(g1,g0)
    c: Block(g1)
    c: Coincident(g2,g0)
    c: Vertical(g2)
    c: Distance(g2) = 19
    c: Horizontal(g3)
    c: Coincident(g4,g1)
    c: Vertical(g4)
    c: Coincident(g3,g4)
    c: Block(g3)
    c: Coincident(g5,g2)
    c: Coincident(g5,g3)
    c: Block(g0)
    c: Block(g5)
FEATURE [Part::Extrusion] Extrude070  label="sideA004"
  Base = -> Sketch080
  Dir = (0,0,1)
  DirMode = 2
  FaceMakerClass = Part::FaceMakerBullseye
  LengthFwd = 3
  LengthRev = 0
  Placement = pos=(0,0,-2.7) rot=(0,0,1;0rad)
  Solid = true
  Symmetric = false
FEATURE [Sketcher::SketchObject] Sketch081
  FullyConstrained = true
  Placement = pos=(117,19,0) rot=(0.57735,0.57735,0.57735;2.0944rad)
  sketch-geometry (8):
    g0: LineSegment StartX=-49.19 StartY=63.5 StartZ=0 EndX=-49.19 EndY=60.5 EndZ=0
    g1: LineSegment StartX=-49.19 StartY=11.5 StartZ=0 EndX=-49.19 EndY=8.5 EndZ=0
    g2: ArcOfCircle CenterX=-1.5 CenterY=62 CenterZ=0 NormalX=0 NormalY=0 NormalZ=1 AngleXU=0 Radius=1.5 StartAngle=4.71239 EndAngle=7.85398
    g3: ArcOfCircle CenterX=-1.5 CenterY=10 CenterZ=0 NormalX=0 NormalY=0 NormalZ=1 AngleXU=0 Radius=1.5 StartAngle=4.71239 EndAngle=7.85398
    g4: LineSegment StartX=-49.19 StartY=63.5 StartZ=0 EndX=-1.5 EndY=63.5 EndZ=0
    g5: LineSegment StartX=-49.19 StartY=60.5 StartZ=0 EndX=-1.5 EndY=60.5 EndZ=0
    g6: LineSegment StartX=-49.19 StartY=11.5 StartZ=0 EndX=-1.5 EndY=11.5 EndZ=0
    g7: LineSegment StartX=-49.19 StartY=8.5 StartZ=0 EndX=-1.5 EndY=8.5 EndZ=0
  constraints (19):
    c: Vertical(g0)
    c: Distance(g0) = 3
    c: Vertical(g1)
    c: Block(g1)
    c: Block(g2)
    c: Block(g3)
    c: Block(g0)
    c: Coincident(g4,g0)
    c: Coincident(g4,g2)
    c: Horizontal(g4)
    c: Coincident(g5,g0)
    c: Coincident(g5,g2)
    c: Horizontal(g5)
    c: Coincident(g6,g1)
    c: Coincident(g6,g3)
    c: Horizontal(g6)
    c: Coincident(g7,g1)
    c: Coincident(g7,g3)
    c: Horizontal(g7)
FEATURE [Part::Extrusion] Extrude071  label="sideB004"
  Base = -> Sketch079
  Dir = (0,0,1)
  DirMode = 2
  FaceMakerClass = Part::FaceMakerBullseye
  LengthFwd = 3
  LengthRev = 0
  Placement = pos=(0,0,71.7) rot=(0,0,1;0rad)
  Solid = true
  Symmetric = false
FEATURE [Part::MultiFuse] Fusion152  label="removeFromBottom004"
  Placement = pos=(2,0,0) rot=(0,0,1;0rad)
  Shapes = -> [Extrude070,Extrude071]
FEATURE [Part::Extrusion] Extrude072
  Base = -> Sketch081
  Dir = (1,0,0)
  DirMode = 2
  FaceMakerClass = Part::FaceMakerBullseye
  LengthFwd = 10
  LengthRev = 0
  Solid = true
  Symmetric = false
FEATURE [Part::Fillet] Fillet059  label="removeFromtMoreFrontCaseScrewRetainers004"
  Base = -> Extrude072
  Edges = 4 edges r=1.49: [Edge6,Edge11,Edge18,Edge23]
  Placement = pos=(-12,0,0) rot=(0,0,1;0rad)
FEATURE [Sketcher::SketchObject] Sketch082
  FullyConstrained = true
  Placement = pos=(117,19,0) rot=(0.57735,0.57735,0.57735;2.0944rad)
  sketch-geometry (8):
    g0: LineSegment StartX=-49.19 StartY=69.25 StartZ=0 EndX=-49.19 EndY=66.25 EndZ=0
    g1: LineSegment StartX=-49.19 StartY=5.75 StartZ=0 EndX=-49.19 EndY=2.75 EndZ=0
    g2: ArcOfCircle CenterX=-1.5 CenterY=67.75 CenterZ=0 NormalX=0 NormalY=0 NormalZ=1 AngleXU=0 Radius=1.5 StartAngle=4.71239 EndAngle=7.85398
    g3: ArcOfCircle CenterX=-1.5 CenterY=4.25 CenterZ=0 NormalX=0 NormalY=0 NormalZ=1 AngleXU=0 Radius=1.5 StartAngle=4.71239 EndAngle=7.85398
    g4: LineSegment StartX=-49.19 StartY=69.25 StartZ=0 EndX=-1.5 EndY=69.25 EndZ=0
    g5: LineSegment StartX=-49.19 StartY=66.25 StartZ=0 EndX=-1.5 EndY=66.25 EndZ=0
    g6: LineSegment StartX=-49.19 StartY=5.75 StartZ=0 EndX=-1.5 EndY=5.75 EndZ=0
    g7: LineSegment StartX=-49.19 StartY=2.75 StartZ=0 EndX=-1.5 EndY=2.75 EndZ=0
  constraints (19):
    c: Vertical(g0)
    c: Distance(g0) = 3
    c: Block(g0)
    c: Vertical(g1)
    c: Block(g2)
    c: Block(g3)
    c: Block(g1)
    c: Coincident(g4,g0)
    c: Coincident(g4,g2)
    c: Horizontal(g4)
    c: Coincident(g5,g0)
    c: Coincident(g5,g2)
    c: Horizontal(g5)
    c: Coincident(g6,g1)
    c: Coincident(g6,g3)
    c: Horizontal(g6)
    c: Coincident(g7,g1)
    c: Coincident(g7,g3)
    c: Horizontal(g7)
FEATURE [Part::Extrusion] Extrude073
  Base = -> Sketch082
  Dir = (1,0,0)
  DirMode = 2
  FaceMakerClass = Part::FaceMakerBullseye
  LengthFwd = 10
  LengthRev = 0
  Solid = true
  Symmetric = false
FEATURE [Part::Fillet] Fillet060  label="removeFromtMoreFrontCaseScrewRetainers005"
  Base = -> Extrude073
  Edges = 4 edges r=1.49: [Edge6,Edge11,Edge18,Edge23]
  Placement = pos=(-4,0,0) rot=(0,0,1;0rad)
FEATURE [Part::Revolution] Revolve163  label="backCaseScrewRetainer004"
  Angle = 360
  Axis = (0,1,0)
  Base = (0,0,0)
  FaceMakerClass = Part::FaceMakerBullseye
  Placement = pos=(12.5,3,62) rot=(0,0,1;0rad)
  Solid = false
  Source = -> Face149
  Symmetric = false
FEATURE [Part::Revolution] Revolve164  label="frontCaseScrewRetainer006"
  Angle = 360
  Axis = (0,1,0)
  Base = (0,0,0)
  FaceMakerClass = Part::FaceMakerBullseye
  Placement = pos=(89.5,3,68.5) rot=(0,0,1;0rad)
  Solid = false
  Source = -> Face151
  Symmetric = false
FEATURE [Part::Revolution] Revolve165  label="frontCaseScrewRetainer007"
  Angle = 360
  Axis = (0,1,0)
  Base = (0,0,0)
  FaceMakerClass = Part::FaceMakerBullseye
  Placement = pos=(89.5,3,3.5) rot=(0,0,1;0rad)
  Solid = false
  Source = -> Face152
  Symmetric = false
FEATURE [Part::Revolution] Revolve166  label="backCaseScrewRetainer005"
  Angle = 360
  Axis = (0,1,0)
  Base = (0,0,0)
  FaceMakerClass = Part::FaceMakerBullseye
  Placement = pos=(12.5,3,10) rot=(0,0,1;0rad)
  Solid = false
  Source = -> Face150
  Symmetric = false
FEATURE [Part::Revolution] Revolve167  label="moreFrontCaseScrewRetainer006"
  Angle = 360
  Axis = (0,1,0)
  Base = (0,0,0)
  FaceMakerClass = Part::FaceMakerBullseye
  Placement = pos=(109.5,4.5,68.5) rot=(0,0,1;0rad)
  Solid = false
  Source = -> Face153
  Symmetric = false
FEATURE [Part::Revolution] Revolve168  label="moreFrontCaseScrewRetainer007"
  Angle = 360
  Axis = (0,1,0)
  Base = (0,0,0)
  FaceMakerClass = Part::FaceMakerBullseye
  Placement = pos=(109.5,4.5,3.5) rot=(0,0,1;0rad)
  Solid = false
  Source = -> Face154
  Symmetric = false
FEATURE [Part::MultiFuse] Fusion151  label="screwRetainers003"
  Shapes = -> [Revolve168,Revolve167,Revolve166,Revolve165,Revolve164,Revolve163]
FEATURE [Part::Cut] Cut069  label="screwRetainers004"
  Base = -> Fusion151
  Tool = -> Fusion152
FEATURE [Part::Cut] Cut070
  Base = -> Cut069
  Tool = -> Fillet060
FEATURE [Part::Cut] Cut071  label="screwPillars001"
  Base = -> Cut070
  Tool = -> Fillet059
FEATURE [Part::MultiFuse] Fusion153  label="bottom024"
  Shapes = -> [Fusion149,Cut071]
FEATURE [Part::Cylinder] Cylinder067
  Angle = 360
  AttacherType = Attacher::AttachEngine3D
  Height = 10
  Placement = pos=(20.65,12,4.68) rot=(1,0,0;1.5708rad)
  Radius = 2
FEATURE [Part::Cylinder] Cylinder068
  Angle = 360
  AttacherType = Attacher::AttachEngine3D
  Height = 10
  Placement = pos=(20.65,12,67.38) rot=(1,0,0;1.5708rad)
  Radius = 2
FEATURE [Part::Cylinder] Cylinder069
  Angle = 360
  AttacherType = Attacher::AttachEngine3D
  Height = 10
  Placement = pos=(77.15,12,67.38) rot=(1,0,0;1.5708rad)
  Radius = 2
FEATURE [Part::Cylinder] Cylinder070
  Angle = 360
  AttacherType = Attacher::AttachEngine3D
  Height = 10
  Placement = pos=(77.15,12,4.68) rot=(1,0,0;1.5708rad)
  Radius = 2
FEATURE [Part::MultiFuse] Fusion154  label="removeFromThreadedInsertHousing001"
  Shapes = -> [Cylinder069,Cylinder068,Cylinder067,Cylinder070]
FEATURE [Part::Cut] Cut072  label="bottom025"
  Base = -> Fusion153
  Tool = -> Fusion154
FEATURE [Image::ImagePlane] ImagePlane
  XSize = 339
  YSize = 72
FEATURE [Sketcher::SketchObject] Sketch083
  FullyConstrained = true
  MapMode = 5
  Support = -> [XY_Plane]
  sketch-geometry (338):
    g0: LineSegment StartX=-151.619 StartY=28.8932 StartZ=0 EndX=-140.819 EndY=28.8932 EndZ=0
    g1: LineSegment StartX=-151.619 StartY=24.0313 StartZ=0 EndX=-151.619 EndY=28.8932 EndZ=0
    g2: LineSegment StartX=-140.819 StartY=17.7713 StartZ=0 EndX=-151.619 EndY=17.7713 EndZ=0
    g3: LineSegment StartX=-151.619 StartY=17.7713 StartZ=0 EndX=-151.619 EndY=22.6313 EndZ=0
    g4: LineSegment StartX=-151.619 StartY=22.6313 StartZ=0 EndX=-145.128 EndY=22.6313 EndZ=0
    g5: LineSegment StartX=-145.128 StartY=24.0313 StartZ=0 EndX=-140.819 EndY=28.8932 EndZ=0
    g6: LineSegment StartX=-145.128 StartY=22.6313 StartZ=0 EndX=-140.819 EndY=17.7713 EndZ=0
    g7: ArcOfCircle CenterX=-155.157 CenterY=23.3323 CenterZ=0 NormalX=0 NormalY=0 NormalZ=1 AngleXU=0 Radius=6.92354 StartAngle=1.03434 EndAngle=5.24885
    g8: ArcOfCircle CenterX=-155.157 CenterY=23.3323 CenterZ=0 NormalX=0 NormalY=0 NormalZ=1 AngleXU=0 Radius=12.6269 StartAngle=1.28675 EndAngle=4.99643
    g9: LineSegment StartX=-151.619 StartY=35.4532 StartZ=0 EndX=-151.619 EndY=29.2832 EndZ=0
    g10: LineSegment StartX=-151.619 StartY=17.3813 StartZ=0 EndX=-151.619 EndY=11.2113 EndZ=0
    g11-g21: Circle x11 (B-spline internal-alignment scaffolding for g22; pole/knot coordinates omitted)
    g22: BSplineCurve PolesCount=11 KnotsCount=9 Degree=3 IsPeriodic=0
    g23-g31: GeomPoint x9 (B-spline internal-alignment scaffolding for g22; pole/knot coordinates omitted)
    g32-g49: Circle x18 (B-spline internal-alignment scaffolding for g50; pole/knot coordinates omitted)
    g50: BSplineCurve PolesCount=18 KnotsCount=16 Degree=3 IsPeriodic=0
    g51-g66: GeomPoint x16 (B-spline internal-alignment scaffolding for g50; pole/knot coordinates omitted)
    g67: LineSegment StartX=-117.124 StartY=30.093 StartZ=0 EndX=-117.603 EndY=26.5272 EndZ=0
    g68: LineSegment StartX=-117.603 StartY=17.8472 StartZ=0 EndX=-117.124 EndY=14.2659 EndZ=0
    g69: Ellipse CenterX=-109.671 CenterY=20.025 CenterZ=0 NormalX=0 NormalY=0 NormalZ=1 MajorRadius=3.34798 MinorRadius=2.71052 AngleXU=-1.56793
    g70: GeomPoint X=-109.666 Y=18.0598 Z=0
    g71: GeomPoint X=-109.677 Y=21.9902 Z=0
    g72: Ellipse CenterX=-109.671 CenterY=20.0123 CenterZ=0 NormalX=0 NormalY=0 NormalZ=1 MajorRadius=6.93002 MinorRadius=6.36273 AngleXU=-3.13976
    g73: GeomPoint X=-112.417 Y=20.0073 Z=0
    g74: GeomPoint X=-106.925 Y=20.0173 Z=0
    g75: Ellipse CenterX=-51.7682 CenterY=20.1463 CenterZ=0 NormalX=0 NormalY=0 NormalZ=1 MajorRadius=3.19279 MinorRadius=2.71052 AngleXU=-1.52774
    g76: GeomPoint X=-51.6955 Y=18.4606 Z=0
    g77: GeomPoint X=-51.8408 Y=21.832 Z=0
    g78: GeomPoint X=-54.5142 Y=20.1413 Z=0
    g79: GeomPoint X=-49.0221 Y=20.1513 Z=0
    g80: Ellipse CenterX=-51.7682 CenterY=20.1463 CenterZ=0 NormalX=0 NormalY=0 NormalZ=1 MajorRadius=6.93002 MinorRadius=6.36273 AngleXU=-3.13976
    g81: Ellipse CenterX=-22.8436 CenterY=20.1783 CenterZ=0 NormalX=0 NormalY=0 NormalZ=1 MajorRadius=3.31512 MinorRadius=2.71052 AngleXU=-1.60214
    g82: GeomPoint X=-22.9034 Y=18.2706 Z=0
    g83: GeomPoint X=-22.7838 Y=22.0861 Z=0
    g84: GeomPoint X=-25.5897 Y=20.1733 Z=0
    g85: GeomPoint X=-20.0976 Y=20.1833 Z=0
    g86: Ellipse CenterX=-22.8436 CenterY=20.1783 CenterZ=0 NormalX=0 NormalY=0 NormalZ=1 MajorRadius=6.93002 MinorRadius=6.36273 AngleXU=-3.13976
    g87: LineSegment StartX=-101.889 StartY=14.1107 StartZ=0 EndX=-97.7455 EndY=14.1107 EndZ=0
    g88: LineSegment StartX=-93.8155 StartY=14.1107 StartZ=0 EndX=-89.6755 EndY=14.1107 EndZ=0
    g89: LineSegment StartX=-85.7455 StartY=14.1107 StartZ=0 EndX=-81.6055 EndY=14.1107 EndZ=0
    g90: LineSegment StartX=-101.889 StartY=14.1107 StartZ=0 EndX=-101.889 EndY=25.9907 EndZ=0
    g91: LineSegment StartX=-101.889 StartY=25.9907 StartZ=0 EndX=-97.8594 EndY=25.9907 EndZ=0
    g92: LineSegment StartX=-97.8594 StartY=25.9907 StartZ=0 EndX=-97.8594 EndY=24.0907 EndZ=0
    g93: LineSegment StartX=-97.7455 StartY=14.1107 StartZ=0 EndX=-97.7455 EndY=19.9107 EndZ=0
    g94: LineSegment StartX=-89.6755 StartY=14.1107 StartZ=0 EndX=-89.6755 EndY=19.9107 EndZ=0
    g95: LineSegment StartX=-93.8155 StartY=14.1107 StartZ=0 EndX=-93.8155 EndY=21.0107 EndZ=0
    g96-g106: Circle x11 (B-spline internal-alignment scaffolding for g107; pole/knot coordinates omitted)
    g107: BSplineCurve PolesCount=11 KnotsCount=9 Degree=3 IsPeriodic=0
    g108-g116: GeomPoint x9 (B-spline internal-alignment scaffolding for g107; pole/knot coordinates omitted)
    g117: BSplineCurve PolesCount=11 KnotsCount=9 Degree=3 IsPeriodic=0
    g118-g125: Circle x8 (B-spline internal-alignment scaffolding for g126; pole/knot coordinates omitted)
    g126: BSplineCurve PolesCount=8 KnotsCount=6 Degree=3 IsPeriodic=0
    g127-g132: GeomPoint x6 (B-spline internal-alignment scaffolding for g126; pole/knot coordinates omitted)
    g133: BSplineCurve PolesCount=8 KnotsCount=6 Degree=3 IsPeriodic=0
    g134: LineSegment StartX=-85.7455 StartY=21.0107 StartZ=0 EndX=-85.7455 EndY=14.1107 EndZ=0
    g135: LineSegment StartX=-80.0879 StartY=14.1107 StartZ=0 EndX=-75.944 EndY=14.1107 EndZ=0
    g136: LineSegment StartX=-72.014 StartY=14.1107 StartZ=0 EndX=-67.874 EndY=14.1107 EndZ=0
    g137: LineSegment StartX=-63.944 StartY=14.1107 StartZ=0 EndX=-59.804 EndY=14.1107 EndZ=0
    g138: LineSegment StartX=-80.0879 StartY=14.1107 StartZ=0 EndX=-80.0879 EndY=25.9907 EndZ=0
    g139: LineSegment StartX=-80.0879 StartY=25.9907 StartZ=0 EndX=-76.0579 EndY=25.9907 EndZ=0
    g140: LineSegment StartX=-76.0579 StartY=25.9907 StartZ=0 EndX=-76.0579 EndY=24.0907 EndZ=0
    g141: LineSegment StartX=-75.944 StartY=14.1107 StartZ=0 EndX=-75.944 EndY=19.9107 EndZ=0
    g142: LineSegment StartX=-67.874 StartY=14.1107 StartZ=0 EndX=-67.874 EndY=19.9107 EndZ=0
    g143: LineSegment StartX=-72.014 StartY=14.1107 StartZ=0 EndX=-72.014 EndY=21.0107 EndZ=0
    g144-g148: Circle x5 (B-spline internal-alignment scaffolding for g149; pole/knot coordinates omitted)
    g149: BSplineCurve PolesCount=11 KnotsCount=9 Degree=3 IsPeriodic=0
    g150-g158: GeomPoint x9 (B-spline internal-alignment scaffolding for g149; pole/knot coordinates omitted)
    g159: BSplineCurve PolesCount=11 KnotsCount=9 Degree=3 IsPeriodic=0
    g160-g167: Circle x8 (B-spline internal-alignment scaffolding for g168; pole/knot coordinates omitted)
    g168: BSplineCurve PolesCount=8 KnotsCount=6 Degree=3 IsPeriodic=0
    g169-g174: GeomPoint x6 (B-spline internal-alignment scaffolding for g168; pole/knot coordinates omitted)
    g175: BSplineCurve PolesCount=8 KnotsCount=6 Degree=3 IsPeriodic=0
    g176: LineSegment StartX=-63.944 StartY=21.0107 StartZ=0 EndX=-63.944 EndY=14.1107 EndZ=0
    g177: LineSegment StartX=-59.804 StartY=14.1107 StartZ=0 EndX=-59.804 EndY=21.5868 EndZ=0
    g178: BSplineCurve PolesCount=4 KnotsCount=2 Degree=3 IsPeriodic=0
    g179: GeomPoint X=-59.804 Y=21.5868 Z=0
    g180: GeomPoint X=-60.2379 Y=24.0907 Z=0
    g181: LineSegment StartX=-81.6055 StartY=14.1107 StartZ=0 EndX=-81.6055 EndY=21.5868 EndZ=0
    g182: LineSegment StartX=-151.619 StartY=24.0313 StartZ=0 EndX=-145.128 EndY=24.0313 EndZ=0
    g183: Circle CenterX=-82.0394 CenterY=24.0907 CenterZ=0 NormalX=0 NormalY=0 NormalZ=1 AngleXU=0 Radius=1
    g184: Circle CenterX=-81.7131 CenterY=23.2736 CenterZ=0 NormalX=0 NormalY=0 NormalZ=1 AngleXU=0 Radius=1
    g185: Circle CenterX=-81.6055 CenterY=21.5868 CenterZ=0 NormalX=0 NormalY=0 NormalZ=1 AngleXU=0 Radius=1
    g186: BSplineCurve PolesCount=3 KnotsCount=2 Degree=2 IsPeriodic=0
    g187: GeomPoint X=-82.0394 Y=24.0907 Z=0
    g188: GeomPoint X=-81.6055 Y=21.5868 Z=0
    g189: Ellipse CenterX=-37.3522 CenterY=19.9515 CenterZ=0 NormalX=0 NormalY=0 NormalZ=1 MajorRadius=2.99755 MinorRadius=2.49 AngleXU=1.5708
    g190: GeomPoint X=-37.3522 Y=21.6203 Z=0
    g191: GeomPoint X=-37.3522 Y=18.2826 Z=0
    g192: ArcOfEllipse CenterX=-38.7647 CenterY=20.06 CenterZ=0 NormalX=0 NormalY=0 NormalZ=1 MajorRadius=6.30025 MinorRadius=5.3849 AngleXU=1.57276 StartAngle=5.50632 EndAngle=10.3035
    g193: GeomPoint X=-38.7711 Y=23.3304 Z=0
    g194: GeomPoint X=-38.7583 Y=16.7895 Z=0
    g195: LineSegment StartX=-34.6109 StartY=14.1107 StartZ=0 EndX=-30.8984 EndY=14.1107 EndZ=0
    g196: LineSegment StartX=-30.8984 StartY=14.1107 StartZ=0 EndX=-30.8984 EndY=31.1784 EndZ=0
    g197: LineSegment StartX=-30.8984 StartY=31.1784 StartZ=0 EndX=-34.9984 EndY=31.1784 EndZ=0
    g198: LineSegment StartX=-34.9984 StartY=24.5602 StartZ=0 EndX=-34.9984 EndY=31.1784 EndZ=0
    g199: LineSegment StartX=-34.6109 StartY=16.0476 StartZ=0 EndX=-34.6109 EndY=14.1107 EndZ=0
    g200: LineSegment StartX=-14.8781 StartY=14.1107 StartZ=0 EndX=-10.5106 EndY=14.1107 EndZ=0
    g201: LineSegment StartX=-14.8781 StartY=14.1107 StartZ=0 EndX=-14.8781 EndY=25.8504 EndZ=0
    g202: LineSegment StartX=-14.8781 StartY=25.8504 StartZ=0 EndX=-10.8534 EndY=25.8504 EndZ=0
    g203: LineSegment StartX=-10.8534 StartY=25.8504 StartZ=0 EndX=-10.8534 EndY=24.0923 EndZ=0
    g204: LineSegment StartX=-10.5106 StartY=14.1107 StartZ=0 EndX=-10.5106 EndY=19.7752 EndZ=0
    g205: LineSegment StartX=-5.96397 StartY=25.9304 StartZ=0 EndX=-5.96397 EndY=22.574 EndZ=0
    g206-g214: Circle x9 (B-spline internal-alignment scaffolding for g215; pole/knot coordinates omitted)
    g215: BSplineCurve PolesCount=9 KnotsCount=7 Degree=3 IsPeriodic=0
    g216-g222: GeomPoint x7 (B-spline internal-alignment scaffolding for g215; pole/knot coordinates omitted)
    g223-g232: Circle x10 (B-spline internal-alignment scaffolding for g233; pole/knot coordinates omitted)
    g233: BSplineCurve PolesCount=10 KnotsCount=8 Degree=3 IsPeriodic=0
    g234-g241: GeomPoint x8 (B-spline internal-alignment scaffolding for g233; pole/knot coordinates omitted)
    g242: LineSegment StartX=-1.58923 StartY=21.0696 StartZ=0 EndX=2.62034 EndY=21.0696 EndZ=0
    g243: LineSegment StartX=-1.55856 StartY=18.7342 StartZ=0 EndX=6.45946 EndY=18.7342 EndZ=0
    g244: LineSegment StartX=5.29231 StartY=17.386 StartZ=0 EndX=5.29231 EndY=14.3674 EndZ=0
    g245-g269: Circle x25 (B-spline internal-alignment scaffolding for g270; pole/knot coordinates omitted)
    g270: BSplineCurve PolesCount=25 KnotsCount=23 Degree=3 IsPeriodic=0
    g271-g293: GeomPoint x23 (B-spline internal-alignment scaffolding for g270; pole/knot coordinates omitted)
    g294-g304: Circle x11 (B-spline internal-alignment scaffolding for g305; pole/knot coordinates omitted)
    g305: BSplineCurve PolesCount=11 KnotsCount=9 Degree=3 IsPeriodic=0
    g306-g314: GeomPoint x9 (B-spline internal-alignment scaffolding for g305; pole/knot coordinates omitted)
    g315-g326: Circle x12 (B-spline internal-alignment scaffolding for g327; pole/knot coordinates omitted)
    g327: BSplineCurve PolesCount=12 KnotsCount=10 Degree=3 IsPeriodic=0
    g328-g337: GeomPoint x10 (B-spline internal-alignment scaffolding for g327; pole/knot coordinates omitted)
  constraints (252):
    c: Coincident(g1,g0)
    c: Horizontal(g0)
    c: Vertical(g1)
    c: Coincident(g2,g3)
    c: Coincident(g3,g4)
    c: Horizontal(g4)
    c: Horizontal(g2)
    c: Vertical(g3)
    c: Block(g1)
    c: Distance(g3) = 4.86
    c: Block(g4)
    c: Distance(g0) = 10.8
    c: Distance(g2) = 10.8
    c: Coincident(g5,g0)
    c: Coincident(g6,g4)
    c: Coincident(g6,g2)
    c: Block(g8)
    c: Block(g7)
    c: Coincident(g9,g8)
    c: Coincident(g9,g7)
    c: Vertical(g9)
    c: Coincident(g10,g7)
    c: Coincident(g10,g8)
    c: Vertical(g10)
    c: Weight(g11) = 1
    c: Equal(g11, g12-g21) x10
    c: InternalAlignment(g11-g21 -> g22) x11
    c: InternalAlignment(g23-g31 -> g22) x9
    c: Block(g22)
    c: Weight(g32) = 1
    c: Equal(g32, g33-g49) x17
    c: InternalAlignment(g32-g49 -> g50) x18
    c: InternalAlignment(g51-g66 -> g50) x16
    c: Block(g50)
    c: Coincident(g67,g50)
    c: Coincident(g67,g22)
    c: Coincident(g68,g22)
    c: Coincident(g68,g50)
    c: InternalAlignment(g70,g69)
    c: InternalAlignment(g71,g69)
    c: Block(g69)
    c: InternalAlignment(g73,g72)
    c: InternalAlignment(g74,g72)
    c: Block(g72)
    c: InternalAlignment(g76,g75)
    c: InternalAlignment(g77,g75)
    c: InternalAlignment(g78,g80)
    c: InternalAlignment(g79,g80)
    c: Block(g80)
    c: Coincident(g75,g80)
    c: Block(g75)
    c: InternalAlignment(g82,g81)
    c: InternalAlignment(g83,g81)
    c: InternalAlignment(g84,g86)
    c: InternalAlignment(g85,g86)
    c: Block(g86)
    c: Coincident(g81,g86)
    c: Block(g81)
    c: Horizontal(g87)
    c: Block(g87)
    c: Horizontal(g88)
    c: Distance(g88) = 4.14
    c: Horizontal(g89)
    c: Equal(g88,g89) = 4.14
    c: Block(g89)
    c: Block(g88)
    c: Coincident(g90,g87)
    c: Vertical(g90)
    c: Distance(g90) = 11.88
    c: Coincident(g91,g90)
    c: Horizontal(g91)
    c: Coincident(g92,g91)
    c: Vertical(g92)
    c: Distance(g91) = 4.03
    c: Distance(g92) = 1.9
    c: Coincident(g93,g87)
    c: Vertical(g93)
    c: Vertical(g94)
    c: Coincident(g94,g88)
    c: Distance(g93) = 5.8
    c: Distance(g94) = 5.8
    c: Vertical(g95)
    c: Coincident(g95,g88)
    c: Distance(g95) = 6.9
    c: Coincident(g107,g92)
    c: Weight(g96) = 1
    c: Equal(g96, g97-g106) x10
    c: InternalAlignment(g96-g106 -> g107) x11
    c: InternalAlignment(g108-g116 -> g107) x9
    c: Block(g107)
    c: Block(g117)
    c: Coincident(g126,g93)
    c: Weight(g118) = 1
    c: Equal(g118, g119-g125) x7
    c: Coincident(g126,g95)
    c: InternalAlignment(g118-g125 -> g126) x8
    c: InternalAlignment(g127-g132 -> g126) x6
    c: Coincident(g133,g94)
    c: Block(g126)
    c: Block(g133)
    c: Coincident(g134,g133)
    c: Coincident(g134,g89)
    c: Vertical(g134)
    c: Horizontal(g135)
    c: Block(g135)
    c: Horizontal(g136)
    c: Equal(g88,g136) = 4.14
    c: Horizontal(g137)
    c: Equal(g136,g137) = 4.14
    c: Block(g137)
    c: Block(g136)
    c: Coincident(g138,g135)
    c: Vertical(g138)
    c: Equal(g90,g138) = 11.88
    c: Coincident(g139,g138)
    c: Horizontal(g139)
    c: Coincident(g140,g139)
    c: Vertical(g140)
    c: Equal(g91,g139) = 4.03
    c: Equal(g92,g140) = 1.9
    c: Coincident(g141,g135)
    c: Vertical(g141)
    c: Vertical(g142)
    c: Coincident(g142,g136)
    c: Equal(g93,g141) = 5.8
    c: Equal(g94,g142) = 5.8
    c: Vertical(g143)
    c: Coincident(g143,g136)
    c: Equal(g95,g143) = 6.9
    c: Coincident(g149,g140)
    c: Equal(g96,g144) = 1
    c: Equal(g144, g145-g148) x4
    c: InternalAlignment(g144-g148 -> g149) x5
    c: InternalAlignment(g150-g158 -> g149) x9
    c: Block(g149)
    c: Block(g159)
    c: Coincident(g168,g141)
    c: Equal(g118,g160) = 1
    c: Equal(g160, g161-g167) x7
    c: Coincident(g168,g143)
    c: InternalAlignment(g160-g167 -> g168) x8
    c: InternalAlignment(g169-g174 -> g168) x6
    c: Coincident(g175,g142)
    c: Block(g168)
    c: Block(g175)
    c: Coincident(g176,g175)
    c: Coincident(g176,g137)
    c: Vertical(g176)
    c: Coincident(g177,g137)
    c: Vertical(g177)
    c: Coincident(g178,g177)
    c: Coincident(g178,g159)
    c: InternalAlignment(g179,g178)
    c: InternalAlignment(g180,g178)
    c: Block(g178)
    c: Vertical(g181)
    c: Coincident(g181,g89)
    c: Block(g5)
    c: Coincident(g182,g1)
    c: Coincident(g182,g5)
    c: Horizontal(g182)
    c: Coincident(g186,g117)
    c: Weight(g183) = 1
    c: Equal(g183,g184)
    c: Equal(g183,g185)
    c: Coincident(g186,g181)
    c: InternalAlignment(g183,g186)
    c: InternalAlignment(g184,g186)
    c: InternalAlignment(g185,g186)
    c: InternalAlignment(g187,g186)
    c: InternalAlignment(g188,g186)
    c: Block(g186)
    c: InternalAlignment(g190,g189)
    c: InternalAlignment(g191,g189)
    c: Block(g189)
    c: InternalAlignment(g193,g192)
    c: InternalAlignment(g194,g192)
    c: Block(g192)
    c: Horizontal(g195)
    c: Block(g195)
    c: Coincident(g196,g195)
    c: Vertical(g196)
    c: Block(g196)
    c: Distance(g195) = 3.71244
    c: Coincident(g197,g196)
    c: Horizontal(g197)
    c: Distance(g197) = 4.1
    c: Coincident(g198,g192)
    c: Coincident(g198,g197)
    c: Vertical(g198)
    c: Block(g198)
    c: Coincident(g199,g192)
    c: Coincident(g199,g195)
    c: Vertical(g199)
    c: Block(g199)
    c: Horizontal(g200)
    c: Block(g200)
    c: Coincident(g201,g200)
    c: Vertical(g201)
    c: Block(g201)
    c: Coincident(g202,g201)
    c: Horizontal(g202)
    c: Block(g202)
    c: Coincident(g203,g202)
    c: Vertical(g203)
    c: Block(g203)
    c: Coincident(g204,g200)
    c: Vertical(g204)
    c: Block(g204)
    c: Coincident(g215,g203)
    c: Weight(g206) = 1
    c: Equal(g206, g207-g214) x8
    c: Coincident(g215,g205)
    c: InternalAlignment(g206-g214 -> g215) x9
    c: InternalAlignment(g216-g222 -> g215) x7
    c: Coincident(g233,g204)
    c: Weight(g223) = 1
    c: Equal(g223, g224-g232) x9
    c: Coincident(g233,g205)
    c: InternalAlignment(g223-g232 -> g233) x10
    c: InternalAlignment(g234-g241 -> g233) x8
    c: Vertical(g205)
    c: Block(g205)
    c: Block(g215)
    c: Block(g233)
    c: Horizontal(g242)
    c: Horizontal(g243)
    c: Block(g242)
    c: Block(g243)
    c: Vertical(g244)
    c: Block(g244)
    c: Coincident(g270,g243)
    c: Weight(g245) = 1
    c: Equal(g245, g246-g269) x24
    c: Coincident(g270,g244)
    c: InternalAlignment(g245-g269 -> g270) x25
    c: InternalAlignment(g271-g293 -> g270) x23
    c: Coincident(g305,g242)
    c: Weight(g294) = 1
    c: Equal(g294, g295-g304) x10
    c: Coincident(g305,g242)
    c: InternalAlignment(g294-g304 -> g305) x11
    c: InternalAlignment(g306-g314 -> g305) x9
    c: Block(g305)
    c: Coincident(g327,g243)
    c: Weight(g315) = 1
    c: Equal(g315, g316-g326) x11
    c: Coincident(g327,g244)
    c: InternalAlignment(g315-g326 -> g327) x12
    c: InternalAlignment(g328-g337 -> g327) x10
    c: Block(g327)
    c: Block(g270)
FEATURE [PartDesign::Body] Body  label="CommodoreLogoAndText"
  Group = -> [Sketch083]
  Origin = -> Origin
FEATURE [Part::Extrusion] Extrude074  label="CommodoreLogoAndText001"
  Base = -> Sketch083
  Dir = (0,0,1)
  DirMode = 2
  FaceMakerClass = Part::FaceMakerBullseye
  LengthFwd = 10
  LengthRev = 0
  Solid = true
  Symmetric = false
FEATURE [Part::FeaturePython] Clone  label="CommodoreLogoAndTextScale"  # Draft clone (typed FeaturePython)
  AttacherType = Attacher::AttachEngine3D
  Fuse = false
  Objects = -> [Extrude074]
  Placement = pos=(111,5.37,-11.6) rot=(0,0,1;0rad)
  Scale = (0.62,0.62,1)
FEATURE [Part::Mirroring] Part__Mirroring  label="CommodoreLogoAndTextScale (Mirror #1)"
  Base = (0,0,0)
  Normal = (1,0,0)
  Placement = pos=(123.576,0,0) rot=(0,0,1;0rad)
  Source = -> Clone
FEATURE [Sketcher::SketchObject] Sketch084
  FullyConstrained = true
  MapMode = 5
  Support = -> [XY_Plane001]
  sketch-geometry (338):
    g0: LineSegment StartX=-151.619 StartY=28.8932 StartZ=0 EndX=-140.819 EndY=28.8932 EndZ=0
    g1: LineSegment StartX=-151.619 StartY=24.0313 StartZ=0 EndX=-151.619 EndY=28.8932 EndZ=0
    g2: LineSegment StartX=-140.819 StartY=17.7713 StartZ=0 EndX=-151.619 EndY=17.7713 EndZ=0
    g3: LineSegment StartX=-151.619 StartY=17.7713 StartZ=0 EndX=-151.619 EndY=22.6313 EndZ=0
    g4: LineSegment StartX=-151.619 StartY=22.6313 StartZ=0 EndX=-145.128 EndY=22.6313 EndZ=0
    g5: LineSegment StartX=-145.128 StartY=24.0313 StartZ=0 EndX=-140.819 EndY=28.8932 EndZ=0
    g6: LineSegment StartX=-145.128 StartY=22.6313 StartZ=0 EndX=-140.819 EndY=17.7713 EndZ=0
    g7: ArcOfCircle CenterX=-155.157 CenterY=23.3323 CenterZ=0 NormalX=0 NormalY=0 NormalZ=1 AngleXU=0 Radius=6.92354 StartAngle=1.03434 EndAngle=5.24885
    g8: ArcOfCircle CenterX=-155.157 CenterY=23.3323 CenterZ=0 NormalX=0 NormalY=0 NormalZ=1 AngleXU=0 Radius=12.6269 StartAngle=1.28675 EndAngle=4.99643
    g9: LineSegment StartX=-151.619 StartY=35.4532 StartZ=0 EndX=-151.619 EndY=29.2832 EndZ=0
    g10: LineSegment StartX=-151.619 StartY=17.3813 StartZ=0 EndX=-151.619 EndY=11.2113 EndZ=0
    g11-g21: Circle x11 (B-spline internal-alignment scaffolding for g22; pole/knot coordinates omitted)
    g22: BSplineCurve PolesCount=11 KnotsCount=9 Degree=3 IsPeriodic=0
    g23-g31: GeomPoint x9 (B-spline internal-alignment scaffolding for g22; pole/knot coordinates omitted)
    g32-g49: Circle x18 (B-spline internal-alignment scaffolding for g50; pole/knot coordinates omitted)
    g50: BSplineCurve PolesCount=18 KnotsCount=16 Degree=3 IsPeriodic=0
    g51-g66: GeomPoint x16 (B-spline internal-alignment scaffolding for g50; pole/knot coordinates omitted)
    g67: LineSegment StartX=-117.124 StartY=30.093 StartZ=0 EndX=-117.603 EndY=26.5272 EndZ=0
    g68: LineSegment StartX=-117.603 StartY=17.8472 StartZ=0 EndX=-117.124 EndY=14.2659 EndZ=0
    g69: Ellipse CenterX=-109.671 CenterY=20.025 CenterZ=0 NormalX=0 NormalY=0 NormalZ=1 MajorRadius=3.34798 MinorRadius=2.71052 AngleXU=-1.56793
    g70: GeomPoint X=-109.666 Y=18.0598 Z=0
    g71: GeomPoint X=-109.677 Y=21.9902 Z=0
    g72: Ellipse CenterX=-109.671 CenterY=20.0123 CenterZ=0 NormalX=0 NormalY=0 NormalZ=1 MajorRadius=6.93002 MinorRadius=6.36273 AngleXU=-3.13976
    g73: GeomPoint X=-112.417 Y=20.0073 Z=0
    g74: GeomPoint X=-106.925 Y=20.0173 Z=0
    g75: Ellipse CenterX=-51.7682 CenterY=20.1463 CenterZ=0 NormalX=0 NormalY=0 NormalZ=1 MajorRadius=3.19279 MinorRadius=2.71052 AngleXU=-1.52774
    g76: GeomPoint X=-51.6955 Y=18.4606 Z=0
    g77: GeomPoint X=-51.8408 Y=21.832 Z=0
    g78: GeomPoint X=-54.5142 Y=20.1413 Z=0
    g79: GeomPoint X=-49.0221 Y=20.1513 Z=0
    g80: Ellipse CenterX=-51.7682 CenterY=20.1463 CenterZ=0 NormalX=0 NormalY=0 NormalZ=1 MajorRadius=6.93002 MinorRadius=6.36273 AngleXU=-3.13976
    g81: Ellipse CenterX=-22.8436 CenterY=20.1783 CenterZ=0 NormalX=0 NormalY=0 NormalZ=1 MajorRadius=3.31512 MinorRadius=2.71052 AngleXU=-1.60214
    g82: GeomPoint X=-22.9034 Y=18.2706 Z=0
    g83: GeomPoint X=-22.7838 Y=22.0861 Z=0
    g84: GeomPoint X=-25.5897 Y=20.1733 Z=0
    g85: GeomPoint X=-20.0976 Y=20.1833 Z=0
    g86: Ellipse CenterX=-22.8436 CenterY=20.1783 CenterZ=0 NormalX=0 NormalY=0 NormalZ=1 MajorRadius=6.93002 MinorRadius=6.36273 AngleXU=-3.13976
    g87: LineSegment StartX=-101.889 StartY=14.1107 StartZ=0 EndX=-97.7455 EndY=14.1107 EndZ=0
    g88: LineSegment StartX=-93.8155 StartY=14.1107 StartZ=0 EndX=-89.6755 EndY=14.1107 EndZ=0
    g89: LineSegment StartX=-85.7455 StartY=14.1107 StartZ=0 EndX=-81.6055 EndY=14.1107 EndZ=0
    g90: LineSegment StartX=-101.889 StartY=14.1107 StartZ=0 EndX=-101.889 EndY=25.9907 EndZ=0
    g91: LineSegment StartX=-101.889 StartY=25.9907 StartZ=0 EndX=-97.8594 EndY=25.9907 EndZ=0
    g92: LineSegment StartX=-97.8594 StartY=25.9907 StartZ=0 EndX=-97.8594 EndY=24.0907 EndZ=0
    g93: LineSegment StartX=-97.7455 StartY=14.1107 StartZ=0 EndX=-97.7455 EndY=19.9107 EndZ=0
    g94: LineSegment StartX=-89.6755 StartY=14.1107 StartZ=0 EndX=-89.6755 EndY=19.9107 EndZ=0
    g95: LineSegment StartX=-93.8155 StartY=14.1107 StartZ=0 EndX=-93.8155 EndY=21.0107 EndZ=0
    g96-g106: Circle x11 (B-spline internal-alignment scaffolding for g107; pole/knot coordinates omitted)
    g107: BSplineCurve PolesCount=11 KnotsCount=9 Degree=3 IsPeriodic=0
    g108-g116: GeomPoint x9 (B-spline internal-alignment scaffolding for g107; pole/knot coordinates omitted)
    g117: BSplineCurve PolesCount=11 KnotsCount=9 Degree=3 IsPeriodic=0
    g118-g125: Circle x8 (B-spline internal-alignment scaffolding for g126; pole/knot coordinates omitted)
    g126: BSplineCurve PolesCount=8 KnotsCount=6 Degree=3 IsPeriodic=0
    g127-g132: GeomPoint x6 (B-spline internal-alignment scaffolding for g126; pole/knot coordinates omitted)
    g133: BSplineCurve PolesCount=8 KnotsCount=6 Degree=3 IsPeriodic=0
    g134: LineSegment StartX=-85.7455 StartY=21.0107 StartZ=0 EndX=-85.7455 EndY=14.1107 EndZ=0
    g135: LineSegment StartX=-80.0879 StartY=14.1107 StartZ=0 EndX=-75.944 EndY=14.1107 EndZ=0
    g136: LineSegment StartX=-72.014 StartY=14.1107 StartZ=0 EndX=-67.874 EndY=14.1107 EndZ=0
    g137: LineSegment StartX=-63.944 StartY=14.1107 StartZ=0 EndX=-59.804 EndY=14.1107 EndZ=0
    g138: LineSegment StartX=-80.0879 StartY=14.1107 StartZ=0 EndX=-80.0879 EndY=25.9907 EndZ=0
    g139: LineSegment StartX=-80.0879 StartY=25.9907 StartZ=0 EndX=-76.0579 EndY=25.9907 EndZ=0
    g140: LineSegment StartX=-76.0579 StartY=25.9907 StartZ=0 EndX=-76.0579 EndY=24.0907 EndZ=0
    g141: LineSegment StartX=-75.944 StartY=14.1107 StartZ=0 EndX=-75.944 EndY=19.9107 EndZ=0
    g142: LineSegment StartX=-67.874 StartY=14.1107 StartZ=0 EndX=-67.874 EndY=19.9107 EndZ=0
    g143: LineSegment StartX=-72.014 StartY=14.1107 StartZ=0 EndX=-72.014 EndY=21.0107 EndZ=0
    g144-g148: Circle x5 (B-spline internal-alignment scaffolding for g149; pole/knot coordinates omitted)
    g149: BSplineCurve PolesCount=11 KnotsCount=9 Degree=3 IsPeriodic=0
    g150-g158: GeomPoint x9 (B-spline internal-alignment scaffolding for g149; pole/knot coordinates omitted)
    g159: BSplineCurve PolesCount=11 KnotsCount=9 Degree=3 IsPeriodic=0
    g160-g167: Circle x8 (B-spline internal-alignment scaffolding for g168; pole/knot coordinates omitted)
    g168: BSplineCurve PolesCount=8 KnotsCount=6 Degree=3 IsPeriodic=0
    g169-g174: GeomPoint x6 (B-spline internal-alignment scaffolding for g168; pole/knot coordinates omitted)
    g175: BSplineCurve PolesCount=8 KnotsCount=6 Degree=3 IsPeriodic=0
    g176: LineSegment StartX=-63.944 StartY=21.0107 StartZ=0 EndX=-63.944 EndY=14.1107 EndZ=0
    g177: LineSegment StartX=-59.804 StartY=14.1107 StartZ=0 EndX=-59.804 EndY=21.5868 EndZ=0
    g178: BSplineCurve PolesCount=4 KnotsCount=2 Degree=3 IsPeriodic=0
    g179: GeomPoint X=-59.804 Y=21.5868 Z=0
    g180: GeomPoint X=-60.2379 Y=24.0907 Z=0
    g181: LineSegment StartX=-81.6055 StartY=14.1107 StartZ=0 EndX=-81.6055 EndY=21.5868 EndZ=0
    g182: LineSegment StartX=-151.619 StartY=24.0313 StartZ=0 EndX=-145.128 EndY=24.0313 EndZ=0
    g183: Circle CenterX=-82.0394 CenterY=24.0907 CenterZ=0 NormalX=0 NormalY=0 NormalZ=1 AngleXU=0 Radius=1
    g184: Circle CenterX=-81.7131 CenterY=23.2736 CenterZ=0 NormalX=0 NormalY=0 NormalZ=1 AngleXU=0 Radius=1
    g185: Circle CenterX=-81.6055 CenterY=21.5868 CenterZ=0 NormalX=0 NormalY=0 NormalZ=1 AngleXU=0 Radius=1
    g186: BSplineCurve PolesCount=3 KnotsCount=2 Degree=2 IsPeriodic=0
    g187: GeomPoint X=-82.0394 Y=24.0907 Z=0
    g188: GeomPoint X=-81.6055 Y=21.5868 Z=0
    g189: Ellipse CenterX=-37.3522 CenterY=19.9515 CenterZ=0 NormalX=0 NormalY=0 NormalZ=1 MajorRadius=2.99755 MinorRadius=2.49 AngleXU=1.5708
    g190: GeomPoint X=-37.3522 Y=21.6203 Z=0
    g191: GeomPoint X=-37.3522 Y=18.2826 Z=0
    g192: ArcOfEllipse CenterX=-38.7647 CenterY=20.06 CenterZ=0 NormalX=0 NormalY=0 NormalZ=1 MajorRadius=6.30025 MinorRadius=5.3849 AngleXU=1.57276 StartAngle=5.50632 EndAngle=10.3035
    g193: GeomPoint X=-38.7711 Y=23.3304 Z=0
    g194: GeomPoint X=-38.7583 Y=16.7895 Z=0
    g195: LineSegment StartX=-34.6109 StartY=14.1107 StartZ=0 EndX=-30.8984 EndY=14.1107 EndZ=0
    g196: LineSegment StartX=-30.8984 StartY=14.1107 StartZ=0 EndX=-30.8984 EndY=31.1784 EndZ=0
    g197: LineSegment StartX=-30.8984 StartY=31.1784 StartZ=0 EndX=-34.9984 EndY=31.1784 EndZ=0
    g198: LineSegment StartX=-34.9984 StartY=24.5602 StartZ=0 EndX=-34.9984 EndY=31.1784 EndZ=0
    g199: LineSegment StartX=-34.6109 StartY=16.0476 StartZ=0 EndX=-34.6109 EndY=14.1107 EndZ=0
    g200: LineSegment StartX=-14.8781 StartY=14.1107 StartZ=0 EndX=-10.5106 EndY=14.1107 EndZ=0
    g201: LineSegment StartX=-14.8781 StartY=14.1107 StartZ=0 EndX=-14.8781 EndY=25.8504 EndZ=0
    g202: LineSegment StartX=-14.8781 StartY=25.8504 StartZ=0 EndX=-10.8534 EndY=25.8504 EndZ=0
    g203: LineSegment StartX=-10.8534 StartY=25.8504 StartZ=0 EndX=-10.8534 EndY=24.0923 EndZ=0
    g204: LineSegment StartX=-10.5106 StartY=14.1107 StartZ=0 EndX=-10.5106 EndY=19.7752 EndZ=0
    g205: LineSegment StartX=-5.96397 StartY=25.9304 StartZ=0 EndX=-5.96397 EndY=22.574 EndZ=0
    g206-g214: Circle x9 (B-spline internal-alignment scaffolding for g215; pole/knot coordinates omitted)
    g215: BSplineCurve PolesCount=9 KnotsCount=7 Degree=3 IsPeriodic=0
    g216-g222: GeomPoint x7 (B-spline internal-alignment scaffolding for g215; pole/knot coordinates omitted)
    g223-g232: Circle x10 (B-spline internal-alignment scaffolding for g233; pole/knot coordinates omitted)
    g233: BSplineCurve PolesCount=10 KnotsCount=8 Degree=3 IsPeriodic=0
    g234-g241: GeomPoint x8 (B-spline internal-alignment scaffolding for g233; pole/knot coordinates omitted)
    g242: LineSegment StartX=-1.58923 StartY=21.0696 StartZ=0 EndX=2.62034 EndY=21.0696 EndZ=0
    g243: LineSegment StartX=-1.55856 StartY=18.7342 StartZ=0 EndX=6.45946 EndY=18.7342 EndZ=0
    g244: LineSegment StartX=5.29231 StartY=17.386 StartZ=0 EndX=5.29231 EndY=14.3674 EndZ=0
    g245-g269: Circle x25 (B-spline internal-alignment scaffolding for g270; pole/knot coordinates omitted)
    g270: BSplineCurve PolesCount=25 KnotsCount=23 Degree=3 IsPeriodic=0
    g271-g293: GeomPoint x23 (B-spline internal-alignment scaffolding for g270; pole/knot coordinates omitted)
    g294-g304: Circle x11 (B-spline internal-alignment scaffolding for g305; pole/knot coordinates omitted)
    g305: BSplineCurve PolesCount=11 KnotsCount=9 Degree=3 IsPeriodic=0
    g306-g314: GeomPoint x9 (B-spline internal-alignment scaffolding for g305; pole/knot coordinates omitted)
    g315-g326: Circle x12 (B-spline internal-alignment scaffolding for g327; pole/knot coordinates omitted)
    g327: BSplineCurve PolesCount=12 KnotsCount=10 Degree=3 IsPeriodic=0
    g328-g337: GeomPoint x10 (B-spline internal-alignment scaffolding for g327; pole/knot coordinates omitted)
  constraints (252):
    c: Coincident(g1,g0)
    c: Horizontal(g0)
    c: Vertical(g1)
    c: Coincident(g2,g3)
    c: Coincident(g3,g4)
    c: Horizontal(g4)
    c: Horizontal(g2)
    c: Vertical(g3)
    c: Block(g1)
    c: Distance(g3) = 4.86
    c: Block(g4)
    c: Distance(g0) = 10.8
    c: Distance(g2) = 10.8
    c: Coincident(g5,g0)
    c: Coincident(g6,g4)
    c: Coincident(g6,g2)
    c: Block(g8)
    c: Block(g7)
    c: Coincident(g9,g8)
    c: Coincident(g9,g7)
    c: Vertical(g9)
    c: Coincident(g10,g7)
    c: Coincident(g10,g8)
    c: Vertical(g10)
    c: Weight(g11) = 1
    c: Equal(g11, g12-g21) x10
    c: InternalAlignment(g11-g21 -> g22) x11
    c: InternalAlignment(g23-g31 -> g22) x9
    c: Block(g22)
    c: Weight(g32) = 1
    c: Equal(g32, g33-g49) x17
    c: InternalAlignment(g32-g49 -> g50) x18
    c: InternalAlignment(g51-g66 -> g50) x16
    c: Block(g50)
    c: Coincident(g67,g50)
    c: Coincident(g67,g22)
    c: Coincident(g68,g22)
    c: Coincident(g68,g50)
    c: InternalAlignment(g70,g69)
    c: InternalAlignment(g71,g69)
    c: Block(g69)
    c: InternalAlignment(g73,g72)
    c: InternalAlignment(g74,g72)
    c: Block(g72)
    c: InternalAlignment(g76,g75)
    c: InternalAlignment(g77,g75)
    c: InternalAlignment(g78,g80)
    c: InternalAlignment(g79,g80)
    c: Block(g80)
    c: Coincident(g75,g80)
    c: Block(g75)
    c: InternalAlignment(g82,g81)
    c: InternalAlignment(g83,g81)
    c: InternalAlignment(g84,g86)
    c: InternalAlignment(g85,g86)
    c: Block(g86)
    c: Coincident(g81,g86)
    c: Block(g81)
    c: Horizontal(g87)
    c: Block(g87)
    c: Horizontal(g88)
    c: Distance(g88) = 4.14
    c: Horizontal(g89)
    c: Equal(g88,g89) = 4.14
    c: Block(g89)
    c: Block(g88)
    c: Coincident(g90,g87)
    c: Vertical(g90)
    c: Distance(g90) = 11.88
    c: Coincident(g91,g90)
    c: Horizontal(g91)
    c: Coincident(g92,g91)
    c: Vertical(g92)
    c: Distance(g91) = 4.03
    c: Distance(g92) = 1.9
    c: Coincident(g93,g87)
    c: Vertical(g93)
    c: Vertical(g94)
    c: Coincident(g94,g88)
    c: Distance(g93) = 5.8
    c: Distance(g94) = 5.8
    c: Vertical(g95)
    c: Coincident(g95,g88)
    c: Distance(g95) = 6.9
    c: Coincident(g107,g92)
    c: Weight(g96) = 1
    c: Equal(g96, g97-g106) x10
    c: InternalAlignment(g96-g106 -> g107) x11
    c: InternalAlignment(g108-g116 -> g107) x9
    c: Block(g107)
    c: Block(g117)
    c: Coincident(g126,g93)
    c: Weight(g118) = 1
    c: Equal(g118, g119-g125) x7
    c: Coincident(g126,g95)
    c: InternalAlignment(g118-g125 -> g126) x8
    c: InternalAlignment(g127-g132 -> g126) x6
    c: Coincident(g133,g94)
    c: Block(g126)
    c: Block(g133)
    c: Coincident(g134,g133)
    c: Coincident(g134,g89)
    c: Vertical(g134)
    c: Horizontal(g135)
    c: Block(g135)
    c: Horizontal(g136)
    c: Equal(g88,g136) = 4.14
    c: Horizontal(g137)
    c: Equal(g136,g137) = 4.14
    c: Block(g137)
    c: Block(g136)
    c: Coincident(g138,g135)
    c: Vertical(g138)
    c: Equal(g90,g138) = 11.88
    c: Coincident(g139,g138)
    c: Horizontal(g139)
    c: Coincident(g140,g139)
    c: Vertical(g140)
    c: Equal(g91,g139) = 4.03
    c: Equal(g92,g140) = 1.9
    c: Coincident(g141,g135)
    c: Vertical(g141)
    c: Vertical(g142)
    c: Coincident(g142,g136)
    c: Equal(g93,g141) = 5.8
    c: Equal(g94,g142) = 5.8
    c: Vertical(g143)
    c: Coincident(g143,g136)
    c: Equal(g95,g143) = 6.9
    c: Coincident(g149,g140)
    c: Equal(g96,g144) = 1
    c: Equal(g144, g145-g148) x4
    c: InternalAlignment(g144-g148 -> g149) x5
    c: InternalAlignment(g150-g158 -> g149) x9
    c: Block(g149)
    c: Block(g159)
    c: Coincident(g168,g141)
    c: Equal(g118,g160) = 1
    c: Equal(g160, g161-g167) x7
    c: Coincident(g168,g143)
    c: InternalAlignment(g160-g167 -> g168) x8
    c: InternalAlignment(g169-g174 -> g168) x6
    c: Coincident(g175,g142)
    c: Block(g168)
    c: Block(g175)
    c: Coincident(g176,g175)
    c: Coincident(g176,g137)
    c: Vertical(g176)
    c: Coincident(g177,g137)
    c: Vertical(g177)
    c: Coincident(g178,g177)
    c: Coincident(g178,g159)
    c: InternalAlignment(g179,g178)
    c: InternalAlignment(g180,g178)
    c: Block(g178)
    c: Vertical(g181)
    c: Coincident(g181,g89)
    c: Block(g5)
    c: Coincident(g182,g1)
    c: Coincident(g182,g5)
    c: Horizontal(g182)
    c: Coincident(g186,g117)
    c: Weight(g183) = 1
    c: Equal(g183,g184)
    c: Equal(g183,g185)
    c: Coincident(g186,g181)
    c: InternalAlignment(g183,g186)
    c: InternalAlignment(g184,g186)
    c: InternalAlignment(g185,g186)
    c: InternalAlignment(g187,g186)
    c: InternalAlignment(g188,g186)
    c: Block(g186)
    c: InternalAlignment(g190,g189)
    c: InternalAlignment(g191,g189)
    c: Block(g189)
    c: InternalAlignment(g193,g192)
    c: InternalAlignment(g194,g192)
    c: Block(g192)
    c: Horizontal(g195)
    c: Block(g195)
    c: Coincident(g196,g195)
    c: Vertical(g196)
    c: Block(g196)
    c: Distance(g195) = 3.71244
    c: Coincident(g197,g196)
    c: Horizontal(g197)
    c: Distance(g197) = 4.1
    c: Coincident(g198,g192)
    c: Coincident(g198,g197)
    c: Vertical(g198)
    c: Block(g198)
    c: Coincident(g199,g192)
    c: Coincident(g199,g195)
    c: Vertical(g199)
    c: Block(g199)
    c: Horizontal(g200)
    c: Block(g200)
    c: Coincident(g201,g200)
    c: Vertical(g201)
    c: Block(g201)
    c: Coincident(g202,g201)
    c: Horizontal(g202)
    c: Block(g202)
    c: Coincident(g203,g202)
    c: Vertical(g203)
    c: Block(g203)
    c: Coincident(g204,g200)
    c: Vertical(g204)
    c: Block(g204)
    c: Coincident(g215,g203)
    c: Weight(g206) = 1
    c: Equal(g206, g207-g214) x8
    c: Coincident(g215,g205)
    c: InternalAlignment(g206-g214 -> g215) x9
    c: InternalAlignment(g216-g222 -> g215) x7
    c: Coincident(g233,g204)
    c: Weight(g223) = 1
    c: Equal(g223, g224-g232) x9
    c: Coincident(g233,g205)
    c: InternalAlignment(g223-g232 -> g233) x10
    c: InternalAlignment(g234-g241 -> g233) x8
    c: Vertical(g205)
    c: Block(g205)
    c: Block(g215)
    c: Block(g233)
    c: Horizontal(g242)
    c: Horizontal(g243)
    c: Block(g242)
    c: Block(g243)
    c: Vertical(g244)
    c: Block(g244)
    c: Coincident(g270,g243)
    c: Weight(g245) = 1
    c: Equal(g245, g246-g269) x24
    c: Coincident(g270,g244)
    c: InternalAlignment(g245-g269 -> g270) x25
    c: InternalAlignment(g271-g293 -> g270) x23
    c: Coincident(g305,g242)
    c: Weight(g294) = 1
    c: Equal(g294, g295-g304) x10
    c: Coincident(g305,g242)
    c: InternalAlignment(g294-g304 -> g305) x11
    c: InternalAlignment(g306-g314 -> g305) x9
    c: Block(g305)
    c: Coincident(g327,g243)
    c: Weight(g315) = 1
    c: Equal(g315, g316-g326) x11
    c: Coincident(g327,g244)
    c: InternalAlignment(g315-g326 -> g327) x12
    c: InternalAlignment(g328-g337 -> g327) x10
    c: Block(g327)
    c: Block(g270)
FEATURE [Part::Extrusion] Extrude075  label="CommodoreLogoAndText002"
  Base = -> Sketch084
  Dir = (0,0,1)
  DirMode = 2
  FaceMakerClass = Part::FaceMakerBullseye
  LengthFwd = 10
  LengthRev = 0
  Solid = true
  Symmetric = false
FEATURE [Part::FeaturePython] Clone001  label="CommodoreLogoAndTextScale001"  # Draft clone (typed FeaturePython)
  AttacherType = Attacher::AttachEngine3D
  Fuse = false
  Objects = -> [Extrude075]
  Placement = pos=(112.566,5.37,73.6) rot=(0,0,1;0rad)
  Scale = (0.62,0.62,1)
FEATURE [Part::Cut] Cut073  label="sideA005"
  Base = -> Extrude002
  Tool = -> Part__Mirroring
FEATURE [Part::Cut] Cut074  label="sideB005"
  Base = -> Extrude028
  Tool = -> Clone001
FEATURE [Sketcher::SketchObject] Sketch085
  FullyConstrained = true
  Placement = pos=(0,0,0) rot=(-1,0,0;4.71239rad)
  sketch-geometry (10):
    g0: LineSegment StartX=0 StartY=0 StartZ=0 EndX=-7 EndY=0 EndZ=0
    g1: LineSegment StartX=-7 StartY=10 StartZ=0 EndX=-6.5 EndY=10 EndZ=0
    g2: LineSegment StartX=0 StartY=10 StartZ=0 EndX=-0.5 EndY=10 EndZ=0
    g3: ArcOfCircle CenterX=-3.5 CenterY=10 CenterZ=0 NormalX=0 NormalY=0 NormalZ=1 AngleXU=0 Radius=3 StartAngle=3.14159 EndAngle=6.28319
    g4: LineSegment StartX=-7 StartY=0 StartZ=0 EndX=-10.5 EndY=0 EndZ=0
    g5: LineSegment StartX=0 StartY=0 StartZ=0 EndX=3.5 EndY=0 EndZ=0
    g6: ArcOfCircle CenterX=-10.5 CenterY=3.5 CenterZ=0 NormalX=0 NormalY=0 NormalZ=1 AngleXU=0 Radius=3.5 StartAngle=4.71239 EndAngle=6.28319
    g7: ArcOfCircle CenterX=3.5 CenterY=3.5 CenterZ=0 NormalX=0 NormalY=0 NormalZ=1 AngleXU=0 Radius=3.5 StartAngle=3.14159 EndAngle=4.71239
    g8: LineSegment StartX=-7 StartY=3.5 StartZ=0 EndX=-7 EndY=10 EndZ=0
    g9: LineSegment StartX=0 StartY=10 StartZ=0 EndX=0 EndY=3.5 EndZ=0
  constraints (26):
    c: Coincident(g0,g-1)
    c: Horizontal(g0)
    c: Distance(g0) = 7
    c: Horizontal(g1)
    c: Distance(g1) = 0.5
    c: Horizontal(g2)
    c: Distance(g2) = 0.5
    c: Coincident(g3,g1)
    c: Coincident(g3,g2)
    c: Block(g3)
    c: Coincident(g4,g0)
    c: Horizontal(g4)
    c: Distance(g4) = 3.5
    c: Coincident(g5,g0)
    c: Distance(g5) = 3.5
    c: Horizontal(g5)
    c: Coincident(g6,g4)
    c: Block(g6)
    c: Coincident(g7,g5)
    c: Block(g7)
    c: Coincident(g8,g6)
    c: Coincident(g8,g1)
    c: Vertical(g8)
    c: Coincident(g9,g2)
    c: Coincident(g9,g7)
    c: Vertical(g9)
FEATURE [Part::Extrusion] Extrude076  label="backRightCasePillarSideBracket"
  Base = -> Sketch085
  Dir = (0,-1,3e-16)
  DirMode = 2
  FaceMakerClass = Part::FaceMakerBullseye
  LengthFwd = 6.7
  LengthRev = 0
  Placement = pos=(16,11.5,0) rot=(0,0,1;0rad)
  Solid = true
  Symmetric = false
FEATURE [Sketcher::SketchObject] Sketch086
  FullyConstrained = true
  Placement = pos=(0,0,0) rot=(1,0,0;1.5708rad)
  sketch-geometry (10):
    g0: LineSegment StartX=0 StartY=0 StartZ=0 EndX=-7 EndY=0 EndZ=0
    g1: LineSegment StartX=-7 StartY=10 StartZ=0 EndX=-6.5 EndY=10 EndZ=0
    g2: LineSegment StartX=0 StartY=10 StartZ=0 EndX=-0.5 EndY=10 EndZ=0
    g3: ArcOfCircle CenterX=-3.5 CenterY=10 CenterZ=0 NormalX=0 NormalY=0 NormalZ=1 AngleXU=0 Radius=3 StartAngle=3.14159 EndAngle=6.28319
    g4: LineSegment StartX=-7 StartY=0 StartZ=0 EndX=-10.5 EndY=0 EndZ=0
    g5: LineSegment StartX=0 StartY=0 StartZ=0 EndX=3.5 EndY=0 EndZ=0
    g6: ArcOfCircle CenterX=-10.5 CenterY=3.5 CenterZ=0 NormalX=0 NormalY=0 NormalZ=1 AngleXU=0 Radius=3.5 StartAngle=4.71239 EndAngle=6.28319
    g7: ArcOfCircle CenterX=3.5 CenterY=3.5 CenterZ=0 NormalX=0 NormalY=0 NormalZ=1 AngleXU=0 Radius=3.5 StartAngle=3.14159 EndAngle=4.71239
    g8: LineSegment StartX=-7 StartY=3.5 StartZ=0 EndX=-7 EndY=10 EndZ=0
    g9: LineSegment StartX=0 StartY=10 StartZ=0 EndX=0 EndY=3.5 EndZ=0
  constraints (26):
    c: Coincident(g0,g-1)
    c: Horizontal(g0)
    c: Distance(g0) = 7
    c: Horizontal(g1)
    c: Distance(g1) = 0.5
    c: Horizontal(g2)
    c: Distance(g2) = 0.5
    c: Coincident(g3,g1)
    c: Coincident(g3,g2)
    c: Block(g3)
    c: Coincident(g4,g0)
    c: Horizontal(g4)
    c: Distance(g4) = 3.5
    c: Coincident(g5,g0)
    c: Distance(g5) = 3.5
    c: Horizontal(g5)
    c: Coincident(g6,g4)
    c: Block(g6)
    c: Coincident(g7,g5)
    c: Block(g7)
    c: Coincident(g8,g6)
    c: Coincident(g8,g1)
    c: Vertical(g8)
    c: Coincident(g9,g2)
    c: Coincident(g9,g7)
    c: Vertical(g9)
FEATURE [Part::Extrusion] Extrude077  label="backLeftCasePillarSideBracket001"
  Base = -> Sketch086
  Dir = (0,-1,3e-16)
  DirMode = 2
  FaceMakerClass = Part::FaceMakerBullseye
  LengthFwd = 6.7
  LengthRev = 0
  Placement = pos=(9,11.5,72) rot=(0,1,0;3.14159rad)
  Solid = true
  Symmetric = false
FEATURE [Sketcher::SketchObject] Sketch087
  FullyConstrained = true
  Placement = pos=(0,0,0) rot=(1,0,0;1.5708rad)
  sketch-geometry (8):
    g0: LineSegment StartX=0 StartY=4e-16 StartZ=0 EndX=-7 EndY=4e-16 EndZ=0
    g1: LineSegment StartX=-7 StartY=4e-16 StartZ=0 EndX=-10.5 EndY=4e-16 EndZ=0
    g2: LineSegment StartX=0 StartY=4e-16 StartZ=0 EndX=3.5 EndY=4e-16 EndZ=0
    g3: ArcOfCircle CenterX=-10.5 CenterY=3.5 CenterZ=0 NormalX=0 NormalY=0 NormalZ=1 AngleXU=0 Radius=3.5 StartAngle=4.71239 EndAngle=6.28319
    g4: ArcOfCircle CenterX=3.5 CenterY=3.5 CenterZ=0 NormalX=0 NormalY=0 NormalZ=1 AngleXU=0 Radius=3.5 StartAngle=3.14159 EndAngle=4.71239
    g5: ArcOfCircle CenterX=-3.5 CenterY=3.5 CenterZ=0 NormalX=0 NormalY=0 NormalZ=1 AngleXU=0 Radius=3 StartAngle=3.14159 EndAngle=6.28319
    g6: LineSegment StartX=-7 StartY=3.5 StartZ=0 EndX=-6.5 EndY=3.5 EndZ=0
    g7: LineSegment StartX=-0.5 StartY=3.5 StartZ=0 EndX=0 EndY=3.5 EndZ=0
  constraints (20):
    c: Coincident(g0,g-1)
    c: Horizontal(g0)
    c: Distance(g0) = 7
    c: Coincident(g1,g0)
    c: Horizontal(g1)
    c: Distance(g1) = 3.5
    c: Coincident(g2,g0)
    c: Distance(g2) = 3.5
    c: Horizontal(g2)
    c: Coincident(g3,g1)
    c: Block(g3)
    c: Coincident(g4,g2)
    c: Block(g4)
    c: Horizontal(g6)
    c: Coincident(g5,g6)
    c: Block(g5)
    c: Coincident(g6,g3)
    c: Coincident(g7,g5)
    c: Coincident(g7,g4)
    c: Horizontal(g7)
FEATURE [Part::Extrusion] Extrude078  label="frontBackLeftCasePillarSideBracket001"
  Base = -> Sketch087
  Dir = (0,-1,2e-16)
  DirMode = 2
  FaceMakerClass = Part::FaceMakerBullseye
  LengthFwd = 6.7
  LengthRev = 0
  Placement = pos=(93,11.5,0) rot=(0,0,1;0rad)
  Solid = true
  Symmetric = false
FEATURE [Sketcher::SketchObject] Sketch088
  FullyConstrained = true
  Placement = pos=(0,0,0) rot=(1,0,0;1.5708rad)
  sketch-geometry (8):
    g0: LineSegment StartX=0 StartY=4e-16 StartZ=0 EndX=-7 EndY=4e-16 EndZ=0
    g1: LineSegment StartX=-7 StartY=4e-16 StartZ=0 EndX=-10.5 EndY=4e-16 EndZ=0
    g2: LineSegment StartX=0 StartY=4e-16 StartZ=0 EndX=3.5 EndY=4e-16 EndZ=0
    g3: ArcOfCircle CenterX=-10.5 CenterY=3.5 CenterZ=0 NormalX=0 NormalY=0 NormalZ=1 AngleXU=0 Radius=3.5 StartAngle=4.71239 EndAngle=6.28319
    g4: ArcOfCircle CenterX=3.5 CenterY=3.5 CenterZ=0 NormalX=0 NormalY=0 NormalZ=1 AngleXU=0 Radius=3.5 StartAngle=3.14159 EndAngle=4.71239
    g5: ArcOfCircle CenterX=-3.5 CenterY=3.5 CenterZ=0 NormalX=0 NormalY=0 NormalZ=1 AngleXU=0 Radius=3 StartAngle=3.14159 EndAngle=6.28319
    g6: LineSegment StartX=-7 StartY=3.5 StartZ=0 EndX=-6.5 EndY=3.5 EndZ=0
    g7: LineSegment StartX=-0.5 StartY=3.5 StartZ=0 EndX=0 EndY=3.5 EndZ=0
  constraints (20):
    c: Coincident(g0,g-1)
    c: Horizontal(g0)
    c: Distance(g0) = 7
    c: Coincident(g1,g0)
    c: Horizontal(g1)
    c: Distance(g1) = 3.5
    c: Coincident(g2,g0)
    c: Distance(g2) = 3.5
    c: Horizontal(g2)
    c: Coincident(g3,g1)
    c: Block(g3)
    c: Coincident(g4,g2)
    c: Block(g4)
    c: Horizontal(g6)
    c: Coincident(g5,g6)
    c: Block(g5)
    c: Coincident(g6,g3)
    c: Coincident(g7,g5)
    c: Coincident(g7,g4)
    c: Horizontal(g7)
FEATURE [Part::Extrusion] Extrude079  label="frontFrontRightCasePillarSideBracket002"
  Base = -> Sketch088
  Dir = (0,-1,2e-16)
  DirMode = 2
  FaceMakerClass = Part::FaceMakerBullseye
  LengthFwd = 2
  LengthRev = 0
  Placement = pos=(106,11.5,72) rot=(0,1,0;3.14159rad)
  Solid = true
  Symmetric = false
FEATURE [Part::Chamfer] Chamfer
  Base = -> Extrude076
  Edges = 1 edges r=3: [Edge19]
FEATURE [Part::Chamfer] Chamfer002
  Base = -> Extrude077
  Edges = 1 edges r=3: [Edge7]
FEATURE [Part::Chamfer] Chamfer003  label="backLeftCasePillarSideBracket002"
  Base = -> Chamfer002
  Edges = 1 edges r=3.8: [Edge29]
FEATURE [Part::Chamfer] Chamfer004  label="backRightCasePillarSideBracket001"
  Base = -> Chamfer
  Edges = 1 edges r=3.8: [Edge24]
FEATURE [Sketcher::SketchObject] Sketch089
  FullyConstrained = true
  Placement = pos=(0,0,0) rot=(1,0,0;1.5708rad)
  sketch-geometry (8):
    g0: LineSegment StartX=0 StartY=4e-16 StartZ=0 EndX=-7 EndY=4e-16 EndZ=0
    g1: LineSegment StartX=-7 StartY=4e-16 StartZ=0 EndX=-10.5 EndY=4e-16 EndZ=0
    g2: LineSegment StartX=0 StartY=4e-16 StartZ=0 EndX=3.5 EndY=4e-16 EndZ=0
    g3: ArcOfCircle CenterX=-10.5 CenterY=3.5 CenterZ=0 NormalX=0 NormalY=0 NormalZ=1 AngleXU=0 Radius=3.5 StartAngle=4.71239 EndAngle=6.28319
    g4: ArcOfCircle CenterX=3.5 CenterY=3.5 CenterZ=0 NormalX=0 NormalY=0 NormalZ=1 AngleXU=0 Radius=3.5 StartAngle=3.14159 EndAngle=4.71239
    g5: ArcOfCircle CenterX=-3.5 CenterY=3.5 CenterZ=0 NormalX=0 NormalY=0 NormalZ=1 AngleXU=0 Radius=3 StartAngle=3.14159 EndAngle=6.28319
    g6: LineSegment StartX=-7 StartY=3.5 StartZ=0 EndX=-6.5 EndY=3.5 EndZ=0
    g7: LineSegment StartX=-0.5 StartY=3.5 StartZ=0 EndX=0 EndY=3.5 EndZ=0
  constraints (20):
    c: Coincident(g0,g-1)
    c: Horizontal(g0)
    c: Distance(g0) = 7
    c: Coincident(g1,g0)
    c: Horizontal(g1)
    c: Distance(g1) = 3.5
    c: Coincident(g2,g0)
    c: Distance(g2) = 3.5
    c: Horizontal(g2)
    c: Coincident(g3,g1)
    c: Block(g3)
    c: Coincident(g4,g2)
    c: Block(g4)
    c: Horizontal(g6)
    c: Coincident(g5,g6)
    c: Block(g5)
    c: Coincident(g6,g3)
    c: Coincident(g7,g5)
    c: Coincident(g7,g4)
    c: Horizontal(g7)
FEATURE [Part::Extrusion] Extrude080  label="frontBackLeftCasePillarSideBracket002"
  Base = -> Sketch089
  Dir = (0,-1,2e-16)
  DirMode = 2
  FaceMakerClass = Part::FaceMakerBullseye
  LengthFwd = 6.7
  LengthRev = 0
  Placement = pos=(86,11.5,72) rot=(0,1,0;3.14159rad)
  Solid = true
  Symmetric = false
FEATURE [Part::Box] Box037  label="backLeftCasePillarAngledSideBracket"
  AttacherType = Attacher::AttachEngine3D
  Height = 14
  Length = 3.4
  Placement = pos=(0,10.8,0) rot=(0,1,0;0.785398rad)
  Width = 4
FEATURE [Part::Box] Box038  label="backRightCasePillarAngledSideBracket"
  AttacherType = Attacher::AttachEngine3D
  Height = 14
  Length = 3.4
  Placement = pos=(9.9,10.8,62.1) rot=(0,1,0;-0.785398rad)
  Width = 4
